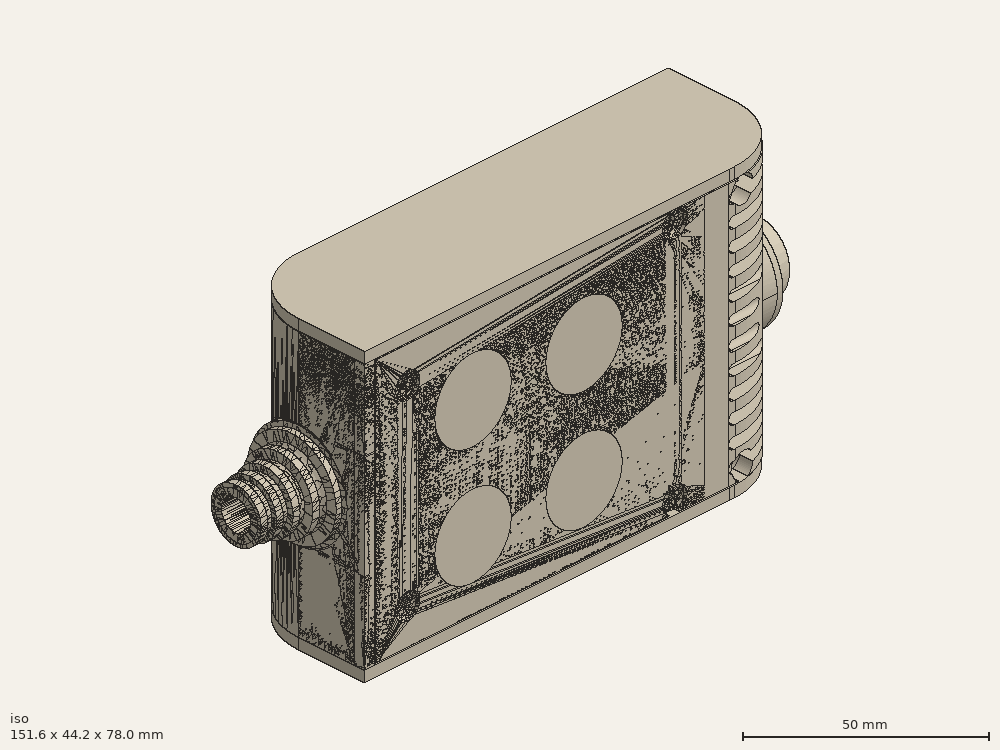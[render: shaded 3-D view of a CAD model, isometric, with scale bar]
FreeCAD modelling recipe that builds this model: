
FCSTD DOCUMENT  (FreeCAD 0.19R0.19.2)
Label: enclosure_189FCStd
License: All rights reserved
LicenseURL: http://en.wikipedia.org/wiki/All_rights_reserved
objects: Part::Revolution×152, Part::MultiFuse×146, Part::Feature×146, Sketcher::SketchObject×84, Part::Cut×70, Part::Cylinder×70, Part::Extrusion×67, Part::Fillet×58, Part::Box×36, App::MeasureDistance×4, PartDesign::Body×2, Image::ImagePlane×1
note: 831 computed .brp shape members not serialized (recipe doc carries the construction recipe); baked Part::Feature solids carry a one-line shape summary decoded from their .brp

FEATURE [Sketcher::SketchObject] Sketch  label="topSketch"
  FullyConstrained = true
  sketch-geometry (20):
    g0: LineSegment StartX=5.21097e-06 StartY=3 StartZ=0 EndX=5.21097e-06 EndY=19 EndZ=0
    g1: ArcOfCircle CenterX=19 CenterY=19 CenterZ=0 NormalX=0 NormalY=0 NormalZ=1 AngleXU=0 Radius=19 StartAngle=1.5708 EndAngle=3.14159
    g2: ArcOfCircle CenterX=19 CenterY=19 CenterZ=0 NormalX=0 NormalY=0 NormalZ=1 AngleXU=0 Radius=16 StartAngle=1.5708 EndAngle=3.14159
    g3: LineSegment StartX=114 StartY=35 StartZ=0 EndX=19 EndY=35 EndZ=0
    g4: LineSegment StartX=5.21097e-06 StartY=3 StartZ=0 EndX=5.21097e-06 EndY=0 EndZ=0
    g5: LineSegment StartX=3 StartY=0 StartZ=0 EndX=5.21097e-06 EndY=0 EndZ=0
    g6: LineSegment StartX=3 StartY=19 StartZ=0 EndX=3 EndY=0 EndZ=0
    g7: LineSegment StartX=19 StartY=38 StartZ=0 EndX=124 EndY=38 EndZ=0
    g8: Circle CenterX=119 CenterY=35 CenterZ=0 NormalX=0 NormalY=0 NormalZ=1 AngleXU=0 Radius=1
    g9: Circle CenterX=121 CenterY=35 CenterZ=0 NormalX=0 NormalY=0 NormalZ=1 AngleXU=0 Radius=1
    g10: Circle CenterX=121 CenterY=33 CenterZ=0 NormalX=0 NormalY=0 NormalZ=1 AngleXU=0 Radius=1
    g11: BSplineCurve PolesCount=3 KnotsCount=2 Degree=2 IsPeriodic=0
    g12: GeomPoint X=119 Y=35 Z=0
    g13: GeomPoint X=121 Y=33 Z=0
    g14: LineSegment StartX=119 StartY=35 StartZ=0 EndX=114 EndY=35 EndZ=0
    g15: ArcOfCircle CenterX=105 CenterY=19 CenterZ=0 NormalX=0 NormalY=0 NormalZ=1 AngleXU=0 Radius=19 StartAngle=5.7297 EndAngle=6.28319
    g16: ArcOfCircle CenterX=105 CenterY=19 CenterZ=0 NormalX=0 NormalY=0 NormalZ=1 AngleXU=0 Radius=16 StartAngle=5.60905 EndAngle=6.28319
    g17: LineSegment StartX=121 StartY=33 StartZ=0 EndX=121 EndY=19 EndZ=0
    g18: LineSegment StartX=124 StartY=38 StartZ=0 EndX=124 EndY=19 EndZ=0
    g19: LineSegment StartX=117.5 StartY=9.01251 StartZ=0 EndX=121.163 EndY=9.0125 EndZ=0
  constraints (46):
    c: Vertical(g0)
    c: Block(g0)
    c: Coincident(g1,g0)
    c: Block(g1)
    c: Coincident(g2,g1)
    c: Block(g2)
    c: Coincident(g3,g2)
    c: Horizontal(g3)
    c: Tangent(g3,g2)
    c: Coincident(g4,g0)
    c: Distance(g4) = 3
    c: Vertical(g4)
    c: Coincident(g5,g4)
    c: Horizontal(g5)
    c: Coincident(g6,g2)
    c: Coincident(g6,g5)
    c: Vertical(g6)
    c: Horizontal(g7)
    c: Distance(g7) = 105
    c: Coincident(g7,g1)
    c: Block(g3)
    c: Weight(g8) = 1
    c: Equal(g8,g9)
    c: Equal(g8,g10)
    c: InternalAlignment(g8,g11)
    c: InternalAlignment(g9,g11)
    c: InternalAlignment(g10,g11)
    c: InternalAlignment(g12,g11)
    c: InternalAlignment(g13,g11)
    c: Block(g11)
    c: Coincident(g14,g11)
    c: Coincident(g14,g3)
    c: Horizontal(g14)
    c: Block(g15)
    c: Coincident(g16,g15)
    c: Block(g16)
    c: Coincident(g17,g11)
    c: Coincident(g17,g16)
    c: Vertical(g17)
    c: Distance(g17) = 14
    c: Coincident(g18,g7)
    c: Coincident(g18,g15)
    c: Vertical(g18)
    c: Distance(g18) = 19
    c: Coincident(g19,g16)
    c: Coincident(g19,g15)
FEATURE [Sketcher::SketchObject] Sketch001  label="bottomSketch"
  FullyConstrained = true
  sketch-geometry (32):
    g0: LineSegment StartX=3.3 StartY=-6.03275e-07 StartZ=0 EndX=98 EndY=-6.03275e-07 EndZ=0
    g1: ArcOfCircle CenterX=98 CenterY=19 CenterZ=0 NormalX=0 NormalY=0 NormalZ=1 AngleXU=0 Radius=19 StartAngle=4.71239 EndAngle=5.71103
    g2: LineSegment StartX=6.3 StartY=8 StartZ=0 EndX=3.3 EndY=8 EndZ=0
    g3: LineSegment StartX=3.3 StartY=8 StartZ=0 EndX=3.3 EndY=-6.03275e-07 EndZ=0
    g4: ArcOfCircle CenterX=8.3 CenterY=5 CenterZ=0 NormalX=0 NormalY=0 NormalZ=1 AngleXU=0 Radius=2 StartAngle=3.14159 EndAngle=4.71239
    g5: LineSegment StartX=6.3 StartY=8 StartZ=0 EndX=6.3 EndY=5 EndZ=0
    g6: ArcOfCircle CenterX=98 CenterY=19 CenterZ=0 NormalX=0 NormalY=0 NormalZ=1 AngleXU=0 Radius=12.7 StartAngle=4.71239 EndAngle=6.28319
    g7: LineSegment StartX=94.7 StartY=3 StartZ=0 EndX=8.3 EndY=3 EndZ=0
    g8-g12: Circle x5 (B-spline internal-alignment scaffolding for g13; pole/knot coordinates omitted)
    g13: BSplineCurve PolesCount=5 KnotsCount=3 Degree=3 IsPeriodic=0
    g14: GeomPoint X=98 Y=6.3 Z=0
    g15: GeomPoint X=96.3938 Y=4.71946 Z=0
    g16: GeomPoint X=94.7 Y=3 Z=0
    g17-g23: Circle x7 (B-spline internal-alignment scaffolding for g24; pole/knot coordinates omitted)
    g24: BSplineCurve PolesCount=7 KnotsCount=5 Degree=3 IsPeriodic=0
    g25-g29: GeomPoint x5 (B-spline internal-alignment scaffolding for g24; pole/knot coordinates omitted)
    g30: ArcOfCircle CenterX=98 CenterY=19 CenterZ=0 NormalX=0 NormalY=0 NormalZ=1 AngleXU=0 Radius=15.7 StartAngle=5.81226 EndAngle=6.28319
    g31: LineSegment StartX=110.7 StartY=19 StartZ=0 EndX=113.7 EndY=19 EndZ=0
  constraints (41):
    c: Horizontal(g0)
    c: Coincident(g1,g0)
    c: Block(g1)
    c: Horizontal(g2)
    c: Distance(g2) = 3
    c: Coincident(g3,g2)
    c: Vertical(g3)
    c: Coincident(g3,g0)
    c: Block(g4)
    c: Block(g2)
    c: Coincident(g5,g2)
    c: Coincident(g5,g4)
    c: Vertical(g5)
    c: Coincident(g6,g1)
    c: Block(g6)
    c: Coincident(g7,g4)
    c: Horizontal(g7)
    c: Block(g0)
    c: Block(g7)
    c: Block(g3)
    c: Coincident(g13,g6)
    c: Weight(g8) = 1
    c: Equal(g8, g9-g12) x4
    c: Coincident(g13,g7)
    c: InternalAlignment(g8-g12 -> g13) x5
    c: InternalAlignment(g14,g13)
    c: InternalAlignment(g15,g13)
    c: InternalAlignment(g16,g13)
    c: Block(g13)
    c: Weight(g17) = 1
    c: Equal(g17, g18-g23) x6
    c: Coincident(g24,g1)
    c: InternalAlignment(g17-g23 -> g24) x7
    c: InternalAlignment(g25-g29 -> g24) x5
    c: Block(g24)
    c: Coincident(g30,g24)
    c: Coincident(g31,g6)
    c: Coincident(g31,g30)
    c: Horizontal(g31)
    c: Block(g31)
    c: Block(g30)
FEATURE [Part::Extrusion] Extrude  label="top"
  Base = -> Sketch
  Dir = (0,0,1)
  DirMode = 2
  FaceMakerClass = Part::FaceMakerBullseye
  LengthFwd = 72
  LengthRev = 0
  Solid = true
  Symmetric = false
FEATURE [Part::Extrusion] Extrude001  label="bottom"
  Base = -> Sketch001
  Dir = (0,0,1)
  DirMode = 2
  FaceMakerClass = Part::FaceMakerBullseye
  LengthFwd = 71.4
  LengthRev = 0
  Placement = pos=(0,0,0.3) rot=(0,0,1;0rad)
  Solid = true
  Symmetric = false
FEATURE [Sketcher::SketchObject] Sketch002  label="topSketch001"
  FullyConstrained = true
  sketch-geometry (8):
    g0: ArcOfCircle CenterX=19 CenterY=19.0975 CenterZ=0 NormalX=0 NormalY=0 NormalZ=1 AngleXU=0 Radius=18.9025 StartAngle=1.5708 EndAngle=3.14674
    g1: LineSegment StartX=0.0977805 StartY=19.0003 StartZ=0 EndX=0.0977805 EndY=0.000251602 EndZ=0
    g2: LineSegment StartX=19 StartY=38 StartZ=0 EndX=124 EndY=38 EndZ=0
    g3: LineSegment StartX=0.0977805 StartY=0.000251602 StartZ=0 EndX=105.098 EndY=0.000251602 EndZ=0
    g4: LineSegment StartX=124 StartY=38 StartZ=0 EndX=125.616 EndY=38 EndZ=0
    g5: LineSegment StartX=105.098 StartY=0.000251602 StartZ=0 EndX=106.713 EndY=0.000251602 EndZ=0
    g6: ArcOfCircle CenterX=106.616 CenterY=19 CenterZ=0 NormalX=0 NormalY=0 NormalZ=1 AngleXU=0 Radius=19 StartAngle=4.71754 EndAngle=6.28319
    g7: LineSegment StartX=125.616 StartY=38 StartZ=0 EndX=125.616 EndY=19 EndZ=0
  constraints (21):
    c: Block(g0)
    c: Coincident(g1,g0)
    c: Vertical(g1)
    c: Horizontal(g2)
    c: Distance(g2) = 105
    c: Coincident(g2,g0)
    c: Distance(g1) = 19
    c: Coincident(g3,g1)
    c: Horizontal(g3)
    c: Distance(g3) = 105
    c: Coincident(g4,g2)
    c: Horizontal(g4)
    c: Distance(g4) = 1.61553
    c: Horizontal(g5)
    c: Equal(g4,g5) = 1.61553
    c: Coincident(g5,g3)
    c: Block(g6)
    c: Coincident(g6,g5)
    c: Coincident(g7,g4)
    c: Coincident(g7,g6)
    c: Vertical(g7)
FEATURE [Part::Extrusion] Extrude002  label="sideA"
  Base = -> Sketch002
  Dir = (0,0,1)
  DirMode = 2
  FaceMakerClass = Part::FaceMakerBullseye
  LengthFwd = 3
  LengthRev = 0
  Placement = pos=(0,0,-3) rot=(0,0,1;0rad)
  Solid = true
  Symmetric = false
FEATURE [Sketcher::SketchObject] Sketch003  label="topSketch002"
  FullyConstrained = true
  sketch-geometry (6):
    g0: LineSegment StartX=19 StartY=38 StartZ=0 EndX=117 EndY=38 EndZ=0
    g1: ArcOfCircle CenterX=19 CenterY=19 CenterZ=0 NormalX=0 NormalY=0 NormalZ=1 AngleXU=0 Radius=19 StartAngle=1.5708 EndAngle=3.14159
    g2: LineSegment StartX=117 StartY=38 StartZ=0 EndX=117 EndY=19 EndZ=0
    g3: LineSegment StartX=98 StartY=1.0161e-12 StartZ=0 EndX=5.22862e-06 EndY=1.0161e-12 EndZ=0
    g4: LineSegment StartX=5.22862e-06 StartY=19 StartZ=0 EndX=5.22862e-06 EndY=1.0161e-12 EndZ=0
    g5: ArcOfCircle CenterX=98 CenterY=19 CenterZ=0 NormalX=0 NormalY=0 NormalZ=1 AngleXU=0 Radius=19 StartAngle=4.71239 EndAngle=6.28319
  constraints (16):
    c: Horizontal(g0)
    c: Distance(g0) = 98
    c: Coincident(g1,g0)
    c: Block(g1)
    c: Coincident(g2,g0)
    c: Vertical(g2)
    c: Distance(g2) = 19
    c: Horizontal(g3)
    c: Coincident(g4,g1)
    c: Vertical(g4)
    c: Coincident(g3,g4)
    c: Block(g3)
    c: Coincident(g5,g2)
    c: Coincident(g5,g3)
    c: Block(g0)
    c: Block(g5)
FEATURE [Sketcher::SketchObject] Sketch004
  FullyConstrained = true
  MapMode = 3
  Placement = pos=(0,0,0) rot=(1,0,0;1.5708rad)
  Support = -> [Extrude]
  sketch-geometry (8):
    g0: Circle CenterX=80.351 CenterY=-67.6202 CenterZ=0 NormalX=0 NormalY=0 NormalZ=1 AngleXU=0 Radius=2
    g1: Circle CenterX=80.351 CenterY=-67.6202 CenterZ=0 NormalX=0 NormalY=0 NormalZ=1 AngleXU=0 Radius=3
    g2: Circle CenterX=80.351 CenterY=-4.92017 CenterZ=0 NormalX=0 NormalY=0 NormalZ=1 AngleXU=0 Radius=2
    g3: Circle CenterX=80.351 CenterY=-4.92017 CenterZ=0 NormalX=0 NormalY=0 NormalZ=1 AngleXU=0 Radius=3
    g4: Circle CenterX=23.851 CenterY=-4.92017 CenterZ=0 NormalX=0 NormalY=0 NormalZ=1 AngleXU=0 Radius=2
    g5: Circle CenterX=23.851 CenterY=-4.92017 CenterZ=0 NormalX=0 NormalY=0 NormalZ=1 AngleXU=0 Radius=3
    g6: Circle CenterX=23.851 CenterY=-67.6202 CenterZ=0 NormalX=0 NormalY=0 NormalZ=1 AngleXU=0 Radius=2
    g7: Circle CenterX=23.851 CenterY=-67.6202 CenterZ=0 NormalX=0 NormalY=0 NormalZ=1 AngleXU=0 Radius=3
  constraints (8):
    c: Block(g3)
    c: Block(g2)
    c: Block(g1)
    c: Block(g0)
    c: Block(g6)
    c: Block(g7)
    c: Block(g4)
    c: Block(g5)
FEATURE [Part::Extrusion] Extrude004
  Base = -> Sketch004
  Dir = (0,-1,2e-16)
  DirMode = 2
  FaceMakerClass = Part::FaceMakerBullseye
  LengthFwd = 6
  LengthRev = 0
  Placement = pos=(0,9,0) rot=(0,0,1;0rad)
  Solid = true
  Symmetric = false
FEATURE [Sketcher::SketchObject] Sketch005
  FullyConstrained = true
  MapMode = 3
  Placement = pos=(0,0,0) rot=(1,0,0;1.5708rad)
  Support = -> [Extrude]
  sketch-geometry (8):
    g0: Circle CenterX=80.351 CenterY=-67.6202 CenterZ=0 NormalX=0 NormalY=0 NormalZ=1 AngleXU=0 Radius=3
    g1: Circle CenterX=80.351 CenterY=-4.92017 CenterZ=0 NormalX=0 NormalY=0 NormalZ=1 AngleXU=0 Radius=3
    g2: Circle CenterX=23.851 CenterY=-4.92017 CenterZ=0 NormalX=0 NormalY=0 NormalZ=1 AngleXU=0 Radius=3
    g3: Circle CenterX=23.851 CenterY=-67.6202 CenterZ=0 NormalX=0 NormalY=0 NormalZ=1 AngleXU=0 Radius=3
    g4: Circle CenterX=23.851 CenterY=-67.6202 CenterZ=0 NormalX=0 NormalY=0 NormalZ=1 AngleXU=0 Radius=5
    g5: Circle CenterX=80.351 CenterY=-67.6202 CenterZ=0 NormalX=0 NormalY=0 NormalZ=1 AngleXU=0 Radius=5
    g6: Circle CenterX=23.851 CenterY=-4.92017 CenterZ=0 NormalX=0 NormalY=0 NormalZ=1 AngleXU=0 Radius=5
    g7: Circle CenterX=80.351 CenterY=-4.92017 CenterZ=0 NormalX=0 NormalY=0 NormalZ=1 AngleXU=0 Radius=5
  constraints (8):
    c: Block(g1)
    c: Block(g0)
    c: Block(g3)
    c: Block(g2)
    c: Block(g5)
    c: Block(g4)
    c: Block(g6)
    c: Block(g7)
FEATURE [Part::Extrusion] Extrude005
  Base = -> Sketch005
  Dir = (0,-1,2e-16)
  DirMode = 2
  FaceMakerClass = Part::FaceMakerBullseye
  LengthFwd = 2
  LengthRev = 0
  Solid = true
  Symmetric = false
FEATURE [Sketcher::SketchObject] Sketch006
  FullyConstrained = true
  MapMode = 3
  Placement = pos=(0,0,0) rot=(1,0,0;1.5708rad)
  sketch-geometry (8):
    g0: Circle CenterX=80.351 CenterY=-67.6202 CenterZ=0 NormalX=0 NormalY=0 NormalZ=1 AngleXU=0 Radius=3
    g1: Circle CenterX=80.351 CenterY=-4.92017 CenterZ=0 NormalX=0 NormalY=0 NormalZ=1 AngleXU=0 Radius=3
    g2: Circle CenterX=23.851 CenterY=-4.92017 CenterZ=0 NormalX=0 NormalY=0 NormalZ=1 AngleXU=0 Radius=3
    g3: Circle CenterX=23.851 CenterY=-67.6202 CenterZ=0 NormalX=0 NormalY=0 NormalZ=1 AngleXU=0 Radius=3
    g4: Circle CenterX=23.851 CenterY=-67.6202 CenterZ=0 NormalX=0 NormalY=0 NormalZ=1 AngleXU=0 Radius=5
    g5: Circle CenterX=80.351 CenterY=-67.6202 CenterZ=0 NormalX=0 NormalY=0 NormalZ=1 AngleXU=0 Radius=5
    g6: Circle CenterX=23.851 CenterY=-4.92017 CenterZ=0 NormalX=0 NormalY=0 NormalZ=1 AngleXU=0 Radius=5
    g7: Circle CenterX=80.351 CenterY=-4.92017 CenterZ=0 NormalX=0 NormalY=0 NormalZ=1 AngleXU=0 Radius=5
  constraints (8):
    c: Block(g1)
    c: Block(g0)
    c: Block(g3)
    c: Block(g2)
    c: Block(g5)
    c: Block(g4)
    c: Block(g6)
    c: Block(g7)
FEATURE [Part::Extrusion] Extrude007
  Base = -> Sketch006
  Dir = (0,-1,2e-16)
  DirMode = 2
  FaceMakerClass = Part::FaceMakerBullseye
  LengthFwd = 2
  LengthRev = 0
  Solid = true
  Symmetric = false
FEATURE [Part::Fillet] Fillet
  Base = -> Extrude007
  Edges = 4 edges r=1.99: [Edge6,Edge12,Edge18,Edge24]
FEATURE [Part::Cut] Cut
  Base = -> Extrude005
  Placement = pos=(0,5,0) rot=(0,0,1;0rad)
  Tool = -> Fillet
FEATURE [Part::MultiFuse] Fusion  label="pCBScrews"
  Placement = pos=(-2.5,0,72.3) rot=(0,0,1;0rad)
  Shapes = -> [Extrude004,Cut]
FEATURE [App::MeasureDistance] Distance  label="Distance: 0.69 mm"
  Distance = 0.685967
  P1 = (24.0138,2.9647,0.3)
  P2 = (23.8901,3,-0.373787)
FEATURE [App::MeasureDistance] Distance001  label="Distance: 0.53 mm"
  Distance = 0.533607
  P1 = (80.2939,3,72.2334)
  P2 = (80.281,2.99661,71.7)
FEATURE [Part::Fillet] Fillet001
  Base = -> Extrude001
  Edges = 1 edges r=2.4: [Edge17]
FEATURE [Part::Fillet] Fillet002  label="bottom001"
  Base = -> Fillet001
  Edges = 1 edges r=2.4: [Edge36]
FEATURE [Part::Fillet] Fillet003  label="top001"
  Base = -> Extrude
  Edges = 1 edges r=2: [Edge1]
FEATURE [Sketcher::SketchObject] Sketch007
  FullyConstrained = true
  sketch-geometry (16):
    g0: LineSegment StartX=4 StartY=0 StartZ=0 EndX=4 EndY=2.4 EndZ=0
    g1: LineSegment StartX=4 StartY=2.4 StartZ=0 EndX=7 EndY=2.4 EndZ=0
    g2: LineSegment StartX=4 StartY=0 StartZ=0 EndX=5.7 EndY=0 EndZ=0
    g3: LineSegment StartX=5.7 StartY=0 StartZ=0 EndX=5.7 EndY=-5.6 EndZ=0
    g4-g8: Circle x5 (B-spline internal-alignment scaffolding for g9; pole/knot coordinates omitted)
    g9: BSplineCurve PolesCount=5 KnotsCount=3 Degree=3 IsPeriodic=0
    g10: GeomPoint X=7 Y=2.4 Z=0
    g11: GeomPoint X=10.4582 Y=-1.55472 Z=0
    g12: GeomPoint X=14 Y=-5.6 Z=0
    g13: LineSegment StartX=14 StartY=-5.6 StartZ=0 EndX=14 EndY=-14.1 EndZ=0
    g14: LineSegment StartX=14 StartY=-14.1 StartZ=0 EndX=6.5 EndY=-14.1 EndZ=0
    g15: LineSegment StartX=5.7 StartY=-5.6 StartZ=0 EndX=6.5 EndY=-14.1 EndZ=0
  constraints (28):
    c: Distance(g0) = 2.4
    c: Vertical(g0)
    c: Block(g0)
    c: Coincident(g1,g0)
    c: Horizontal(g1)
    c: Distance(g1) = 3
    c: Coincident(g2,g0)
    c: Horizontal(g2)
    c: Distance(g2) = 1.7
    c: Coincident(g3,g2)
    c: Vertical(g3)
    c: Distance(g3) = 5.6
    c: Coincident(g9,g1)
    c: Weight(g4) = 1
    c: Equal(g4, g5-g8) x4
    c: InternalAlignment(g4-g8 -> g9) x5
    c: InternalAlignment(g10,g9)
    c: InternalAlignment(g11,g9)
    c: InternalAlignment(g12,g9)
    c: Block(g9)
    c: Coincident(g13,g9)
    c: Vertical(g13)
    c: Distance(g13) = 8.5
    c: Coincident(g14,g13)
    c: Horizontal(g14)
    c: Distance(g14) = 7.5
    c: Coincident(g15,g3)
    c: Coincident(g15,g14)
FEATURE [Part::Feature] Face
  shape: bbox 10 x 16.5 x 2e-07 mm, 1 faces, 0 solids (baked)
FEATURE [Part::Revolution] Revolve  label="plugHousing"
  Angle = 360
  Axis = (0,1,0)
  Base = (0,0,0)
  FaceMakerClass = Part::FaceMakerBullseye
  Placement = pos=(0,0,36.15) rot=(0,0,1;0rad)
  Solid = false
  Source = -> Face
  Symmetric = false
FEATURE [Part::Feature] Face001
  shape: bbox 10 x 16.5 x 2e-07 mm, 1 faces, 0 solids (baked)
FEATURE [Part::Revolution] Revolve001  label="plugHousing001"
  Angle = 360
  Axis = (0,1,0)
  Base = (0,0,0)
  FaceMakerClass = Part::FaceMakerBullseye
  Placement = pos=(0,0,36.15) rot=(0,0,1;0rad)
  Solid = false
  Source = -> Face001
  Symmetric = false
FEATURE [Part::MultiFuse] Fusion001  label="plugHousing002"
  Placement = pos=(0,0,0) rot=(0,0,1;1.5708rad)
  Shapes = -> [Revolve001,Revolve]
FEATURE [Part::Feature] Face002
  shape: bbox 10 x 16.5 x 2e-07 mm, 1 faces, 0 solids (baked)
FEATURE [Part::Revolution] Revolve003  label="plugHousing005"
  Angle = 360
  Axis = (0,1,0)
  Base = (0,0,0)
  FaceMakerClass = Part::FaceMakerBullseye
  Placement = pos=(0,0,36.15) rot=(0,0,1;0rad)
  Solid = false
  Source = -> Face002
  Symmetric = false
FEATURE [Part::Feature] Face003
  shape: bbox 10 x 16.5 x 2e-07 mm, 1 faces, 0 solids (baked)
FEATURE [Part::Revolution] Revolve002  label="plugHousing003"
  Angle = 360
  Axis = (0,1,0)
  Base = (0,0,0)
  FaceMakerClass = Part::FaceMakerBullseye
  Placement = pos=(0,0,36.15) rot=(0,0,1;0rad)
  Solid = false
  Source = -> Face003
  Symmetric = false
FEATURE [Part::MultiFuse] Fusion002  label="plugHousing004"
  Placement = pos=(0,0,0) rot=(0,0,1;1.5708rad)
  Shapes = -> [Revolve002,Revolve003]
FEATURE [Part::MultiFuse] Fusion003  label="plugHousing006"
  Placement = pos=(0,19,0) rot=(0,0,1;3.14159rad)
  Shapes = -> [Fusion002,Fusion001]
FEATURE [Part::Feature] Face004
  shape: bbox 10 x 16.5 x 2e-07 mm, 1 faces, 0 solids (baked)
FEATURE [Part::Revolution] Revolve006  label="plugHousing010"
  Angle = 360
  Axis = (0,1,0)
  Base = (0,0,0)
  FaceMakerClass = Part::FaceMakerBullseye
  Placement = pos=(0,0,36.15) rot=(0,0,1;0rad)
  Solid = false
  Source = -> Face004
  Symmetric = false
FEATURE [Part::Feature] Face005
  shape: bbox 10 x 16.5 x 2e-07 mm, 1 faces, 0 solids (baked)
FEATURE [Part::Revolution] Revolve007  label="plugHousing011"
  Angle = 360
  Axis = (0,1,0)
  Base = (0,0,0)
  FaceMakerClass = Part::FaceMakerBullseye
  Placement = pos=(0,0,36.15) rot=(0,0,1;0rad)
  Solid = false
  Source = -> Face005
  Symmetric = false
FEATURE [Part::Feature] Face006
  shape: bbox 10 x 16.5 x 2e-07 mm, 1 faces, 0 solids (baked)
FEATURE [Part::Revolution] Revolve004  label="plugHousing007"
  Angle = 360
  Axis = (0,1,0)
  Base = (0,0,0)
  FaceMakerClass = Part::FaceMakerBullseye
  Placement = pos=(0,0,36.15) rot=(0,0,1;0rad)
  Solid = false
  Source = -> Face006
  Symmetric = false
FEATURE [Part::MultiFuse] Fusion004  label="plugHousing009"
  Placement = pos=(0,0,0) rot=(0,0,1;1.5708rad)
  Shapes = -> [Revolve004,Revolve007]
FEATURE [Part::Feature] Face007
  shape: bbox 10 x 16.5 x 2e-07 mm, 1 faces, 0 solids (baked)
FEATURE [Part::Revolution] Revolve005  label="plugHousing008"
  Angle = 360
  Axis = (0,1,0)
  Base = (0,0,0)
  FaceMakerClass = Part::FaceMakerBullseye
  Placement = pos=(0,0,36.15) rot=(0,0,1;0rad)
  Solid = false
  Source = -> Face007
  Symmetric = false
FEATURE [Part::MultiFuse] Fusion005  label="plugHousing012"
  Placement = pos=(0,0,0) rot=(0,0,1;1.5708rad)
  Shapes = -> [Revolve006,Revolve005]
FEATURE [Part::MultiFuse] Fusion006  label="plugHousing013"
  Placement = pos=(0,19,0) rot=(0,0,1;3.14159rad)
  Shapes = -> [Fusion005,Fusion004]
FEATURE [Part::MultiFuse] Fusion007  label="plugHousing014"
  Placement = pos=(122.621,0,-0.15) rot=(0,0,1;0rad)
  Shapes = -> [Fusion003,Fusion006]
FEATURE [Part::Cylinder] Cylinder002
  Angle = 360
  AttacherType = Attacher::AttachEngine3D
  Height = 20
  Placement = pos=(0,0,36.15) rot=(0,0,1;0rad)
  Radius = 4
FEATURE [Part::Cylinder] Cylinder003
  Angle = 360
  AttacherType = Attacher::AttachEngine3D
  Height = 10
  Placement = pos=(0,0,36.15) rot=(0,0,1;0rad)
  Radius = 4
FEATURE [Part::MultiFuse] Fusion009  label="removeToCreateHoleForPlugHousing"
  Placement = pos=(70,19,36.15) rot=(0,1,0;1.5708rad)
  Shapes = -> [Cylinder002,Cylinder003]
FEATURE [Part::Cylinder] Cylinder004
  Angle = 360
  AttacherType = Attacher::AttachEngine3D
  Height = 20
  Placement = pos=(0,0,36.15) rot=(0,0,1;0rad)
  Radius = 4
FEATURE [Part::Cylinder] Cylinder005
  Angle = 360
  AttacherType = Attacher::AttachEngine3D
  Height = 10
  Placement = pos=(0,0,36.15) rot=(0,0,1;0rad)
  Radius = 4
FEATURE [Part::MultiFuse] Fusion010  label="removeToCreateHoleForPlugHousing001"
  Placement = pos=(70,19,36.15) rot=(0,1,0;1.5708rad)
  Shapes = -> [Cylinder004,Cylinder005]
FEATURE [Part::Cut] Cut001
  Base = -> Fillet003
  Tool = -> Fusion010
FEATURE [Part::Cut] Cut002  label="Bottom"
  Base = -> Fillet002
  Tool = -> Fusion009
FEATURE [Part::Feature] Face008
  shape: bbox 10 x 16.5 x 2e-07 mm, 1 faces, 0 solids (baked)
FEATURE [Part::Revolution] Revolve011  label="plugHousing021"
  Angle = 360
  Axis = (0,1,0)
  Base = (0,0,0)
  FaceMakerClass = Part::FaceMakerBullseye
  Placement = pos=(0,0,36.15) rot=(0,0,1;0rad)
  Solid = false
  Source = -> Face008
  Symmetric = false
FEATURE [Part::Feature] Face009
  shape: bbox 10 x 16.5 x 2e-07 mm, 1 faces, 0 solids (baked)
FEATURE [Part::Revolution] Revolve012  label="plugHousing022"
  Angle = 360
  Axis = (0,1,0)
  Base = (0,0,0)
  FaceMakerClass = Part::FaceMakerBullseye
  Placement = pos=(0,0,36.15) rot=(0,0,1;0rad)
  Solid = false
  Source = -> Face009
  Symmetric = false
FEATURE [Part::Feature] Face010 .. Face013  x4 (patterned run collapsed; names and placements below)
  shape: bbox 10 x 16.5 x 2e-07 mm, 1 faces, 0 solids (baked)
FEATURE [Part::Revolution] Revolve015  label="plugHousing027"
  Angle = 360
  Axis = (0,1,0)
  Base = (0,0,0)
  FaceMakerClass = Part::FaceMakerBullseye
  Placement = pos=(0,0,36.15) rot=(0,0,1;0rad)
  Solid = false
  Source = -> Face013
  Symmetric = false
FEATURE [Part::Feature] Face014
  shape: bbox 10 x 16.5 x 2e-07 mm, 1 faces, 0 solids (baked)
FEATURE [Part::Feature] Face015
  shape: bbox 10 x 16.5 x 2e-07 mm, 1 faces, 0 solids (baked)
FEATURE [Part::Feature] Face016
  shape: bbox 10 x 16.5 x 2e-07 mm, 1 faces, 0 solids (baked)
FEATURE [Part::Revolution] Revolve019  label="plugHousing033"
  Angle = 360
  Axis = (0,1,0)
  Base = (0,0,0)
  FaceMakerClass = Part::FaceMakerBullseye
  Placement = pos=(0,0,36.15) rot=(0,0,1;0rad)
  Solid = false
  Source = -> Face016
  Symmetric = false
FEATURE [Part::Feature] Face017
  shape: bbox 10 x 16.5 x 2e-07 mm, 1 faces, 0 solids (baked)
FEATURE [Part::Revolution] Revolve020  label="plugHousing034"
  Angle = 360
  Axis = (0,1,0)
  Base = (0,0,0)
  FaceMakerClass = Part::FaceMakerBullseye
  Placement = pos=(0,0,36.15) rot=(0,0,1;0rad)
  Solid = false
  Source = -> Face017
  Symmetric = false
FEATURE [Part::Feature] Face018
  shape: bbox 10 x 16.5 x 2e-07 mm, 1 faces, 0 solids (baked)
FEATURE [Part::Revolution] Revolve016  label="plugHousing030"
  Angle = 360
  Axis = (0,1,0)
  Base = (0,0,0)
  FaceMakerClass = Part::FaceMakerBullseye
  Placement = pos=(0,0,36.15) rot=(0,0,1;0rad)
  Solid = false
  Source = -> Face018
  Symmetric = false
FEATURE [Part::MultiFuse] Fusion020  label="plugHousing038"
  Placement = pos=(0,0,0) rot=(0,0,1;1.5708rad)
  Shapes = -> [Revolve016,Revolve020]
FEATURE [Part::Feature] Face019
  shape: bbox 10 x 16.5 x 2e-07 mm, 1 faces, 0 solids (baked)
FEATURE [Part::Feature] Face020
  shape: bbox 10 x 16.5 x 2e-07 mm, 1 faces, 0 solids (baked)
FEATURE [Part::Revolution] Revolve017  label="plugHousing031"
  Angle = 360
  Axis = (0,1,0)
  Base = (0,0,0)
  FaceMakerClass = Part::FaceMakerBullseye
  Placement = pos=(0,0,36.15) rot=(0,0,1;0rad)
  Solid = false
  Source = -> Face020
  Symmetric = false
FEATURE [Part::MultiFuse] Fusion021  label="plugHousing039"
  Placement = pos=(0,0,0) rot=(0,0,1;1.5708rad)
  Shapes = -> [Revolve019,Revolve017]
FEATURE [Part::MultiFuse] Fusion023  label="plugHousing041"
  Placement = pos=(0,19,0) rot=(0,0,1;3.14159rad)
  Shapes = -> [Fusion021,Fusion020]
FEATURE [Part::Revolution] Revolve022  label="plugHousing043"
  Angle = 360
  Axis = (0,1,0)
  Base = (0,0,0)
  FaceMakerClass = Part::FaceMakerBullseye
  Placement = pos=(0,0,36.15) rot=(0,0,1;0rad)
  Solid = false
  Source = -> Face019
  Symmetric = false
FEATURE [Part::Feature] Face021
  shape: bbox 10 x 16.5 x 2e-07 mm, 1 faces, 0 solids (baked)
FEATURE [Part::Revolution] Revolve023  label="plugHousing044"
  Angle = 360
  Axis = (0,1,0)
  Base = (0,0,0)
  FaceMakerClass = Part::FaceMakerBullseye
  Placement = pos=(0,0,36.15) rot=(0,0,1;0rad)
  Solid = false
  Source = -> Face021
  Symmetric = false
FEATURE [Part::Feature] Face022
  shape: bbox 10 x 16.5 x 2e-07 mm, 1 faces, 0 solids (baked)
FEATURE [Part::Revolution] Revolve018  label="plugHousing032"
  Angle = 360
  Axis = (0,1,0)
  Base = (0,0,0)
  FaceMakerClass = Part::FaceMakerBullseye
  Placement = pos=(0,0,36.15) rot=(0,0,1;0rad)
  Solid = false
  Source = -> Face022
  Symmetric = false
FEATURE [Part::MultiFuse] Fusion022  label="plugHousing040"
  Placement = pos=(0,0,0) rot=(0,0,1;1.5708rad)
  Shapes = -> [Revolve018,Revolve023]
FEATURE [Part::Feature] Face023
  shape: bbox 10 x 16.5 x 2e-07 mm, 1 faces, 0 solids (baked)
FEATURE [Part::Revolution] Revolve021  label="plugHousing035"
  Angle = 360
  Axis = (0,1,0)
  Base = (0,0,0)
  FaceMakerClass = Part::FaceMakerBullseye
  Placement = pos=(0,0,36.15) rot=(0,0,1;0rad)
  Solid = false
  Source = -> Face023
  Symmetric = false
FEATURE [Part::MultiFuse] Fusion018  label="plugHousing036"
  Placement = pos=(0,0,0) rot=(0,0,1;1.5708rad)
  Shapes = -> [Revolve022,Revolve021]
FEATURE [Part::MultiFuse] Fusion019  label="plugHousing037"
  Placement = pos=(0,19,0) rot=(0,0,1;3.14159rad)
  Shapes = -> [Fusion018,Fusion022]
FEATURE [Part::MultiFuse] Fusion024  label="plugHousing042"
  Placement = pos=(122.621,0,-0.15) rot=(0,0,1;0rad)
  Shapes = -> [Fusion023,Fusion019]
FEATURE [Part::Cylinder] Cylinder006
  Angle = 360
  AttacherType = Attacher::AttachEngine3D
  Height = 20
  Placement = pos=(0,0,36.15) rot=(0,0,1;0rad)
  Radius = 14.3
FEATURE [Part::Cylinder] Cylinder007
  Angle = 360
  AttacherType = Attacher::AttachEngine3D
  Height = 10
  Placement = pos=(0,0,36.15) rot=(0,0,1;0rad)
  Radius = 4
FEATURE [Part::MultiFuse] Fusion026  label="removeToCreteHoleForPlugHousing"
  Placement = pos=(70,19,36) rot=(0,1,0;1.5708rad)
  Shapes = -> [Cylinder006,Cylinder007]
FEATURE [Part::Box] Box001  label="Cube001"
  AttacherType = Attacher::AttachEngine3D
  Height = 28
  Length = 3
  Placement = pos=(110.7,19,22) rot=(0,0,1;0rad)
  Width = 15.7
FEATURE [Part::Cut] Cut003  label="top002"
  Base = -> Cut001
  Tool = -> Fusion007
FEATURE [Part::Revolution] Revolve008  label="plugHousing015"
  Angle = 360
  Axis = (0,1,0)
  Base = (0,0,0)
  FaceMakerClass = Part::FaceMakerBullseye
  Placement = pos=(0,0,36.15) rot=(0,0,1;0rad)
  Solid = false
  Source = -> Face010
  Symmetric = false
FEATURE [Part::MultiFuse] Fusion013  label="plugHousing020"
  Placement = pos=(0,0,0) rot=(0,0,1;1.5708rad)
  Shapes = -> [Revolve008,Revolve012]
FEATURE [Part::Cut] Cut004  label="top003"
  Base = -> Cut003
  Placement = pos=(1,0,0) rot=(0,0,1;0rad)
  Tool = -> Fusion026
FEATURE [Part::Cylinder] Cylinder008
  Angle = 360
  AttacherType = Attacher::AttachEngine3D
  Height = 20
  Placement = pos=(0,0,36.15) rot=(0,0,1;0rad)
  Radius = 10.3
FEATURE [Part::Cylinder] Cylinder009
  Angle = 360
  AttacherType = Attacher::AttachEngine3D
  Height = 10
  Placement = pos=(0,0,36.15) rot=(0,0,1;0rad)
  Radius = 4
FEATURE [Part::MultiFuse] Fusion027  label="removeToCreteHoleForPlugHousing001"
  Placement = pos=(70,19,36) rot=(0,1,0;1.5708rad)
  Shapes = -> [Cylinder008,Cylinder009]
FEATURE [Part::Cut] Cut005  label="plugHousingTab"
  Base = -> Box001
  Tool = -> Fusion027
FEATURE [Part::MultiFuse] Fusion028  label="plugHousing045"
  Shapes = -> [Fusion024,Cut005]
FEATURE [Part::Box] Box002  label="Cube002"
  AttacherType = Attacher::AttachEngine3D
  Height = 28.8
  Length = 3
  Placement = pos=(107.3,28,21.6) rot=(0,0,1;0rad)
  Width = 7
FEATURE [Part::Box] Box003  label="Cube003"
  AttacherType = Attacher::AttachEngine3D
  Height = 3
  Length = 6.4
  Placement = pos=(107.3,28,18.6) rot=(0,0,1;0rad)
  Width = 7
FEATURE [Part::Box] Box004  label="Cube004"
  AttacherType = Attacher::AttachEngine3D
  Height = 3
  Length = 6.4
  Placement = pos=(107.3,28,50.4) rot=(0,0,1;0rad)
  Width = 7
FEATURE [Part::MultiFuse] Fusion029  label="plugHousingBracketHolder"
  Shapes = -> [Box004,Box002,Box003]
FEATURE [Part::Cylinder] Cylinder010
  Angle = 360
  AttacherType = Attacher::AttachEngine3D
  Height = 20
  Placement = pos=(0,0,36.15) rot=(0,0,1;0rad)
  Radius = 14.3
FEATURE [Part::Cylinder] Cylinder011
  Angle = 360
  AttacherType = Attacher::AttachEngine3D
  Height = 10
  Placement = pos=(0,0,36.15) rot=(0,0,1;0rad)
  Radius = 4
FEATURE [Part::MultiFuse] Fusion030  label="removeToCreteHoleForPlugHousing002"
  Placement = pos=(70,19,36) rot=(0,1,0;1.5708rad)
  Shapes = -> [Cylinder010,Cylinder011]
FEATURE [Part::Cut] Cut006  label="plugHousingBracketHolder001"
  Base = -> Fusion029
  Tool = -> Fusion030
FEATURE [Part::Cylinder] Cylinder012
  Angle = 360
  AttacherType = Attacher::AttachEngine3D
  Height = 20
  Placement = pos=(0,0,36.15) rot=(0,0,1;0rad)
  Radius = 7
FEATURE [Part::Cylinder] Cylinder013
  Angle = 360
  AttacherType = Attacher::AttachEngine3D
  Height = 10
  Placement = pos=(0,0,36.15) rot=(0,0,1;0rad)
  Radius = 4
FEATURE [Part::MultiFuse] Fusion032  label="removeToCreteHoleForPlugHousing003"
  Placement = pos=(70,19,36) rot=(0,1,0;1.5708rad)
  Shapes = -> [Cylinder012,Cylinder013]
FEATURE [Part::Cut] Cut007  label="bottom002"
  Base = -> Cut002
  Tool = -> Fusion032
FEATURE [Sketcher::SketchObject] Sketch008
  FullyConstrained = true
  sketch-geometry (54):
    g0: LineSegment StartX=-4.2 StartY=0 StartZ=0 EndX=-6.2 EndY=0 EndZ=0
    g1: LineSegment StartX=-14 StartY=-18 StartZ=0 EndX=-14 EndY=-26.5 EndZ=0
    g2: LineSegment StartX=-4.2 StartY=0 StartZ=0 EndX=-4.2 EndY=-13.4877 EndZ=0
    g3: Circle CenterX=-4.2 CenterY=-13.4877 CenterZ=0 NormalX=0 NormalY=0 NormalZ=1 AngleXU=0 Radius=1
    g4: Circle CenterX=-4.2 CenterY=-26.5 CenterZ=0 NormalX=0 NormalY=0 NormalZ=1 AngleXU=0 Radius=1
    g5: Circle CenterX=-8.2 CenterY=-26.5 CenterZ=0 NormalX=0 NormalY=0 NormalZ=1 AngleXU=0 Radius=1
    g6: BSplineCurve PolesCount=3 KnotsCount=2 Degree=2 IsPeriodic=0
    g7: GeomPoint X=-4.2 Y=-13.4877 Z=0
    g8: GeomPoint X=-8.2 Y=-26.5 Z=0
    g9: LineSegment StartX=-14 StartY=-26.5 StartZ=0 EndX=-8.2 EndY=-26.5 EndZ=0
    g10: LineSegment StartX=-10.15 StartY=-12 StartZ=0 EndX=-10.15 EndY=-14 EndZ=0
    g11: LineSegment StartX=-12.8401 StartY=-16 StartZ=0 EndX=-10.1571 EndY=-16 EndZ=0
    g12: LineSegment StartX=-10.15 StartY=-14 StartZ=0 EndX=-8.70761 EndY=-14 EndZ=0
    g13: LineSegment StartX=-12.8401 StartY=-16 StartZ=0 EndX=-12.8401 EndY=-17.6958 EndZ=0
    g14: LineSegment StartX=-10.15 StartY=-12 StartZ=0 EndX=-7.79258 EndY=-12 EndZ=0
    g15: Circle CenterX=-6.2215 CenterY=-2 CenterZ=0 NormalX=0 NormalY=0 NormalZ=1 AngleXU=0 Radius=1
    g16: Circle CenterX=-6.22762 CenterY=-2.58724 CenterZ=0 NormalX=0 NormalY=0 NormalZ=1 AngleXU=0 Radius=1
    g17: Circle CenterX=-6.32538 CenterY=-4 CenterZ=0 NormalX=0 NormalY=0 NormalZ=1 AngleXU=0 Radius=1
    g18: BSplineCurve PolesCount=3 KnotsCount=2 Degree=2 IsPeriodic=0
    g19: GeomPoint X=-6.2215 Y=-2 Z=0
    g20: GeomPoint X=-6.32538 Y=-4 Z=0
    g21: Circle CenterX=-6.48644 CenterY=-5.99526 CenterZ=0 NormalX=0 NormalY=0 NormalZ=1 AngleXU=0 Radius=1
    g22: Circle CenterX=-6.58486 CenterY=-6.99526 CenterZ=0 NormalX=0 NormalY=0 NormalZ=1 AngleXU=0 Radius=1
    g23: Circle CenterX=-6.77343 CenterY=-8 CenterZ=0 NormalX=0 NormalY=0 NormalZ=1 AngleXU=0 Radius=1
    g24: BSplineCurve PolesCount=3 KnotsCount=2 Degree=2 IsPeriodic=0
    g25: GeomPoint X=-6.48644 Y=-5.99526 Z=0
    g26: GeomPoint X=-6.77343 Y=-8 Z=0
    g27: Circle CenterX=-7.19003 CenterY=-10 CenterZ=0 NormalX=0 NormalY=0 NormalZ=1 AngleXU=0 Radius=1
    g28: Circle CenterX=-7.44407 CenterY=-11.0915 CenterZ=0 NormalX=0 NormalY=0 NormalZ=1 AngleXU=0 Radius=1
    g29: Circle CenterX=-7.79258 CenterY=-12 CenterZ=0 NormalX=0 NormalY=0 NormalZ=1 AngleXU=0 Radius=1
    g30: BSplineCurve PolesCount=3 KnotsCount=2 Degree=2 IsPeriodic=0
    g31: GeomPoint X=-7.19003 Y=-10 Z=0
    g32: GeomPoint X=-7.79258 Y=-12 Z=0
    g33: Circle CenterX=-8.70761 CenterY=-14 CenterZ=0 NormalX=0 NormalY=0 NormalZ=1 AngleXU=0 Radius=1
    g34: Circle CenterX=-9.33087 CenterY=-15.1837 CenterZ=0 NormalX=0 NormalY=0 NormalZ=1 AngleXU=0 Radius=1
    g35: Circle CenterX=-10.1571 CenterY=-16 CenterZ=0 NormalX=0 NormalY=0 NormalZ=1 AngleXU=0 Radius=1
    g36: BSplineCurve PolesCount=3 KnotsCount=2 Degree=2 IsPeriodic=0
    g37: GeomPoint X=-8.70761 Y=-14 Z=0
    g38: GeomPoint X=-10.1571 Y=-16 Z=0
    g39: Circle CenterX=-12.8401 CenterY=-17.6958 CenterZ=0 NormalX=0 NormalY=0 NormalZ=1 AngleXU=0 Radius=1
    g40: Circle CenterX=-13.3521 CenterY=-17.9027 CenterZ=0 NormalX=0 NormalY=0 NormalZ=1 AngleXU=0 Radius=1
    g41: Circle CenterX=-14 CenterY=-18 CenterZ=0 NormalX=0 NormalY=0 NormalZ=1 AngleXU=0 Radius=1
    g42: BSplineCurve PolesCount=3 KnotsCount=2 Degree=2 IsPeriodic=0
    g43: GeomPoint X=-12.8401 Y=-17.6958 Z=0
    g44: GeomPoint X=-14 Y=-18 Z=0
    g45: LineSegment StartX=-6.2 StartY=0 StartZ=0 EndX=-7.2 EndY=0 EndZ=0
    g46: LineSegment StartX=-7.2 StartY=0 StartZ=0 EndX=-7.2 EndY=-2 EndZ=0
    g47: LineSegment StartX=-7.2 StartY=-2 StartZ=0 EndX=-6.2215 EndY=-2 EndZ=0
    g48: LineSegment StartX=-6.32538 StartY=-4 StartZ=0 EndX=-7.65538 EndY=-4 EndZ=0
    g49: LineSegment StartX=-7.65538 StartY=-4 StartZ=0 EndX=-7.65538 EndY=-5.99526 EndZ=0
    g50: LineSegment StartX=-7.65538 StartY=-5.99526 StartZ=0 EndX=-6.48644 EndY=-5.99526 EndZ=0
    g51: LineSegment StartX=-6.77343 StartY=-8 StartZ=0 EndX=-8.43343 EndY=-8 EndZ=0
    g52: LineSegment StartX=-8.43343 StartY=-8 StartZ=0 EndX=-8.43343 EndY=-10 EndZ=0
    g53: LineSegment StartX=-8.43343 StartY=-10 StartZ=0 EndX=-7.19003 EndY=-10 EndZ=0
  constraints (112):
    c: Horizontal(g0)
    c: Distance(g0) = 2
    c: Block(g0)
    c: Vertical(g1)
    c: Coincident(g2,g0)
    c: Vertical(g2)
    c: Block(g2)
    c: Coincident(g6,g2)
    c: Weight(g3) = 1
    c: Equal(g3,g4)
    c: Equal(g3,g5)
    c: InternalAlignment(g3,g6)
    c: InternalAlignment(g4,g6)
    c: InternalAlignment(g5,g6)
    c: InternalAlignment(g7,g6)
    c: InternalAlignment(g8,g6)
    c: Block(g6)
    c: Coincident(g9,g1)
    c: Coincident(g9,g6)
    c: Horizontal(g9)
    c: Vertical(g10)
    c: Block(g10)
    c: Horizontal(g11)
    c: Block(g11)
    c: Coincident(g12,g10)
    c: Horizontal(g12)
    c: Block(g12)
    c: Coincident(g13,g11)
    c: Vertical(g13)
    c: Block(g13)
    c: Coincident(g14,g10)
    c: Horizontal(g14)
    c: Block(g14)
    c: Block(g9)
    c: Block(g1)
    c: Weight(g15) = 1
    c: Equal(g15,g16)
    c: Equal(g15,g17)
    c: InternalAlignment(g15,g18)
    c: InternalAlignment(g16,g18)
    c: InternalAlignment(g17,g18)
    c: InternalAlignment(g19,g18)
    c: InternalAlignment(g20,g18)
    c: Weight(g21) = 1
    c: Equal(g21,g22)
    c: Equal(g21,g23)
    c: InternalAlignment(g21,g24)
    c: InternalAlignment(g22,g24)
    c: InternalAlignment(g23,g24)
    c: InternalAlignment(g25,g24)
    c: InternalAlignment(g26,g24)
    c: Weight(g27) = 1
    c: Equal(g27,g28)
    c: Equal(g27,g29)
    c: Coincident(g30,g14)
    c: InternalAlignment(g27,g30)
    c: InternalAlignment(g28,g30)
    c: InternalAlignment(g29,g30)
    c: InternalAlignment(g31,g30)
    c: InternalAlignment(g32,g30)
    c: Coincident(g36,g12)
    c: Weight(g33) = 1
    c: Equal(g33,g34)
    c: Equal(g33,g35)
    c: Coincident(g36,g11)
    c: InternalAlignment(g33,g36)
    c: InternalAlignment(g34,g36)
    c: InternalAlignment(g35,g36)
    c: InternalAlignment(g37,g36)
    c: InternalAlignment(g38,g36)
    c: Coincident(g42,g13)
    c: Weight(g39) = 1
    c: Equal(g39,g40)
    c: Equal(g39,g41)
    c: Coincident(g42,g1)
    c: InternalAlignment(g39,g42)
    c: InternalAlignment(g40,g42)
    c: InternalAlignment(g41,g42)
    c: InternalAlignment(g43,g42)
    c: InternalAlignment(g44,g42)
    c: Block(g18)
    c: Block(g24)
    c: Block(g30)
    c: Block(g36)
    c: Block(g42)
    c: Horizontal(g45)
    c: Coincident(g45,g0)
    c: Vertical(g46)
    c: Coincident(g46,g45)
    c: Coincident(g47,g46)
    c: Coincident(g47,g18)
    c: Horizontal(g47)
    c: Block(g46)
    c: Coincident(g48,g18)
    c: Horizontal(g48)
    c: Distance(g48) = 1.33
    c: Vertical(g49)
    c: Coincident(g49,g48)
    c: Coincident(g50,g49)
    c: Coincident(g50,g24)
    c: Horizontal(g50)
    c: Tangent(g50,g22)
    c: Horizontal(g51)
    c: Coincident(g51,g24)
    c: Block(g51)
    c: Vertical(g52)
    c: Block(g52)
    c: Coincident(g52,g51)
    c: Coincident(g53,g52)
    c: Coincident(g53,g30)
    c: Horizontal(g53)
    c: Distance(g1) = 8.5
FEATURE [Part::Feature] Face024
  shape: bbox 9.8 x 26.5 x 2e-07 mm, 1 faces, 0 solids (baked)
FEATURE [Part::Revolution] Revolve024
  Angle = 360
  Axis = (0,1,0)
  Base = (0,0,0)
  FaceMakerClass = Part::FaceMakerBullseye
  Placement = pos=(0,0,0) rot=(0,0,1;1.5708rad)
  Solid = false
  Source = -> Face024
  Symmetric = false
FEATURE [Part::Feature] Face025
  shape: bbox 9.8 x 26.5 x 2e-07 mm, 1 faces, 0 solids (baked)
FEATURE [Part::Revolution] Revolve025
  Angle = 360
  Axis = (0,1,0)
  Base = (0,0,0)
  FaceMakerClass = Part::FaceMakerBullseye
  Placement = pos=(0,0,0) rot=(0,0,1;1.5708rad)
  Solid = false
  Source = -> Face025
  Symmetric = false
FEATURE [Part::MultiFuse] Fusion033
  Placement = pos=(-18,19,36) rot=(0,0,1;0rad)
  Shapes = -> [Revolve025,Revolve024]
FEATURE [Part::Cylinder] Cylinder014
  Angle = 360
  AttacherType = Attacher::AttachEngine3D
  Height = 20
  Placement = pos=(0,0,36.15) rot=(0,0,1;0rad)
  Radius = 14.3
FEATURE [Part::Cylinder] Cylinder015
  Angle = 360
  AttacherType = Attacher::AttachEngine3D
  Height = 10
  Placement = pos=(0,0,36.15) rot=(0,0,1;0rad)
  Radius = 4
FEATURE [Part::MultiFuse] Fusion034  label="removeToCreteHoleForPlugHousing004"
  Placement = pos=(-42,19,36) rot=(0,1,0;1.5708rad)
  Shapes = -> [Cylinder014,Cylinder015]
FEATURE [Part::Cut] Cut008  label="top004"
  Base = -> Cut004
  Placement = pos=(-1,0,0) rot=(0,0,1;0rad)
  Tool = -> Fusion034
FEATURE [Part::Box] Box005  label="Cube005"
  AttacherType = Attacher::AttachEngine3D
  Height = 28
  Length = 3
  Placement = pos=(110.7,19,22) rot=(0,0,1;0rad)
  Width = 15.7
FEATURE [Part::Cylinder] Cylinder016
  Angle = 360
  AttacherType = Attacher::AttachEngine3D
  Height = 10
  Placement = pos=(0,0,36.15) rot=(0,0,1;0rad)
  Radius = 4
FEATURE [Part::Cylinder] Cylinder017
  Angle = 360
  AttacherType = Attacher::AttachEngine3D
  Height = 20
  Placement = pos=(0,0,36.15) rot=(0,0,1;0rad)
  Radius = 10.3
FEATURE [Part::MultiFuse] Fusion035  label="removeToCreteHoleForPlugHousing005"
  Placement = pos=(70,19,36) rot=(0,1,0;1.5708rad)
  Shapes = -> [Cylinder017,Cylinder016]
FEATURE [Part::Cut] Cut009  label="plugHousingTab001"
  Base = -> Box005
  Placement = pos=(-107.4,-14,0) rot=(0,0,1;0rad)
  Tool = -> Fusion035
FEATURE [Part::Box] Box006  label="Cube006"
  AttacherType = Attacher::AttachEngine3D
  Height = 28
  Length = 3
  Placement = pos=(110.7,19,22) rot=(0,0,1;0rad)
  Width = 15.7
FEATURE [Part::Cylinder] Cylinder018
  Angle = 360
  AttacherType = Attacher::AttachEngine3D
  Height = 10
  Placement = pos=(0,0,36.15) rot=(0,0,1;0rad)
  Radius = 4
FEATURE [Part::Cylinder] Cylinder019
  Angle = 360
  AttacherType = Attacher::AttachEngine3D
  Height = 20
  Placement = pos=(0,0,36.15) rot=(0,0,1;0rad)
  Radius = 10.3
FEATURE [Part::MultiFuse] Fusion036  label="removeToCreteHoleForPlugHousing006"
  Placement = pos=(70,19,36) rot=(0,1,0;1.5708rad)
  Shapes = -> [Cylinder019,Cylinder018]
FEATURE [Part::Cut] Cut010  label="plugHousingTab002"
  Base = -> Box006
  Placement = pos=(-107.4,-14,0) rot=(0,0,1;0rad)
  Tool = -> Fusion036
FEATURE [Part::MultiFuse] Fusion037
  Placement = pos=(9.6,23,0) rot=(0,0,1;3.14159rad)
  Shapes = -> [Cut009,Cut010]
FEATURE [Part::Box] Box  label="Cube"
  AttacherType = Attacher::AttachEngine3D
  Height = 10
  Length = 3
  Placement = pos=(3.3,4,12) rot=(0,0,1;0rad)
  Width = 10
FEATURE [Part::Fillet] Fillet004
  Base = -> Fusion028
  Edges = 1 edges r=2: [Edge25]
FEATURE [Part::Fillet] Fillet005  label="plugHousing046"
  Base = -> Fillet004
  Edges = 1 edges r=2: [Edge8]
FEATURE [Part::Fillet] Fillet006
  Base = -> Box
  Edges = 1 edges r=2: [Edge11]
FEATURE [Part::Box] Box007  label="Cube007"
  AttacherType = Attacher::AttachEngine3D
  Height = 10
  Length = 3
  Placement = pos=(3.3,4,50) rot=(0,0,1;0rad)
  Width = 10
FEATURE [Part::Fillet] Fillet007
  Base = -> Box007
  Edges = 1 edges r=2: [Edge12]
FEATURE [Part::Box] Box008  label="Cube008"
  AttacherType = Attacher::AttachEngine3D
  Height = 28
  Length = 4
  Placement = pos=(5,0,22) rot=(0,0,1;0rad)
  Width = 10
FEATURE [Part::Fillet] Fillet008
  Base = -> Box008
  Edges = 1 edges r=1: [Edge7]
FEATURE [Part::Fillet] Fillet009
  Base = -> Fillet008
  Edges = 1 edges r=2: [Edge5]
FEATURE [Part::Fillet] Fillet010
  Base = -> Fillet009
  Edges = 1 edges r=2: [Edge2]
FEATURE [Sketcher::SketchObject] Sketch009  label="topSketch003"
  FullyConstrained = true
  sketch-geometry (4):
    g0: LineSegment StartX=16.8446 StartY=31.512 StartZ=0 EndX=16.3251 EndY=34.4666 EndZ=0
    g1: ArcOfCircle CenterX=19 CenterY=19.2524 CenterZ=0 NormalX=0 NormalY=0 NormalZ=1 AngleXU=0 Radius=15.4476 StartAngle=1.74483 EndAngle=2.72717
    g2: ArcOfCircle CenterX=19 CenterY=19.2524 CenterZ=0 NormalX=0 NormalY=0 NormalZ=1 AngleXU=0 Radius=12.4476 StartAngle=1.74483 EndAngle=2.73189
    g3: LineSegment StartX=4.86004 StartY=25.4725 StartZ=0 EndX=7.58253 EndY=24.2107 EndZ=0
  constraints (7):
    c: Block(g0)
    c: Coincident(g1,g0)
    c: Coincident(g2,g0)
    c: Coincident(g3,g1)
    c: Coincident(g3,g2)
    c: Block(g1)
    c: Block(g2)
FEATURE [Part::Extrusion] Extrude008
  Base = -> Sketch009
  Dir = (0,0,1)
  DirMode = 2
  FaceMakerClass = Part::FaceMakerBullseye
  LengthFwd = 10
  LengthRev = 0
  Placement = pos=(0,0,31) rot=(0,0,1;0rad)
  Solid = true
  Symmetric = false
FEATURE [Part::Cylinder] Cylinder020
  Angle = 360
  AttacherType = Attacher::AttachEngine3D
  Height = 20
  Placement = pos=(0,0,36.15) rot=(0,0,1;0rad)
  Radius = 8.2
FEATURE [Part::Cylinder] Cylinder021
  Angle = 360
  AttacherType = Attacher::AttachEngine3D
  Height = 10
  Placement = pos=(0,0,36.15) rot=(0,0,1;0rad)
  Radius = 4
FEATURE [Part::MultiFuse] Fusion038  label="removeToCreteHoleForPlugHousing007"
  Placement = pos=(-42,19,36) rot=(0,1,0;1.5708rad)
  Shapes = -> [Cylinder020,Cylinder021]
FEATURE [Part::Cut] Cut011
  Base = -> Extrude008
  Tool = -> Fusion038
FEATURE [Part::Fillet] Fillet011
  Base = -> Cut011
  Edges = 1 edges r=2: [Edge1]
FEATURE [Part::Fillet] Fillet012
  Base = -> Fillet011
  Edges = 1 edges r=2.5: [Edge1]
FEATURE [Part::Fillet] Fillet013
  Base = -> Fillet012
  Edges = 1 edges r=2.5: [Edge2]
FEATURE [Part::Box] Box010  label="Cube010"
  AttacherType = Attacher::AttachEngine3D
  Height = 16
  Length = 8
  Placement = pos=(12.7,31.52,28) rot=(0,0,1;0rad)
  Width = 4
FEATURE [Sketcher::SketchObject] Sketch010  label="topSketch004"
  FullyConstrained = true
  sketch-geometry (4):
    g0: LineSegment StartX=16.8446 StartY=31.512 StartZ=0 EndX=16.3251 EndY=34.4666 EndZ=0
    g1: ArcOfCircle CenterX=19 CenterY=19.2524 CenterZ=0 NormalX=0 NormalY=0 NormalZ=1 AngleXU=0 Radius=15.4476 StartAngle=1.74483 EndAngle=2.72717
    g2: ArcOfCircle CenterX=19 CenterY=19.2524 CenterZ=0 NormalX=0 NormalY=0 NormalZ=1 AngleXU=0 Radius=12.4476 StartAngle=1.74483 EndAngle=2.73189
    g3: LineSegment StartX=4.86004 StartY=25.4725 StartZ=0 EndX=7.58253 EndY=24.2107 EndZ=0
  constraints (7):
    c: Block(g0)
    c: Coincident(g1,g0)
    c: Coincident(g2,g0)
    c: Coincident(g3,g1)
    c: Coincident(g3,g2)
    c: Block(g1)
    c: Block(g2)
FEATURE [Part::Cylinder] Cylinder022
  Angle = 360
  AttacherType = Attacher::AttachEngine3D
  Height = 10
  Placement = pos=(0,0,36.15) rot=(0,0,1;0rad)
  Radius = 4
FEATURE [Sketcher::SketchObject] Sketch011  label="topSketch005"
  FullyConstrained = true
  sketch-geometry (4):
    g0: LineSegment StartX=16.8446 StartY=31.512 StartZ=0 EndX=16.3251 EndY=34.4666 EndZ=0
    g1: ArcOfCircle CenterX=19 CenterY=19.2524 CenterZ=0 NormalX=0 NormalY=0 NormalZ=1 AngleXU=0 Radius=15.4476 StartAngle=1.74483 EndAngle=2.72717
    g2: ArcOfCircle CenterX=19 CenterY=19.2524 CenterZ=0 NormalX=0 NormalY=0 NormalZ=1 AngleXU=0 Radius=12.4476 StartAngle=1.74483 EndAngle=2.73189
    g3: LineSegment StartX=4.86004 StartY=25.4725 StartZ=0 EndX=7.58253 EndY=24.2107 EndZ=0
  constraints (7):
    c: Block(g0)
    c: Coincident(g1,g0)
    c: Coincident(g2,g0)
    c: Coincident(g3,g1)
    c: Coincident(g3,g2)
    c: Block(g1)
    c: Block(g2)
FEATURE [Part::Extrusion] Extrude010
  Base = -> Sketch011
  Dir = (0,0,1)
  DirMode = 2
  FaceMakerClass = Part::FaceMakerBullseye
  LengthFwd = 10.6
  LengthRev = 0
  Placement = pos=(0,0,31) rot=(0,0,1;0rad)
  Solid = true
  Symmetric = false
FEATURE [Part::Cylinder] Cylinder023
  Angle = 360
  AttacherType = Attacher::AttachEngine3D
  Height = 20
  Placement = pos=(0,0,36.15) rot=(0,0,1;0rad)
  Radius = 8.2
FEATURE [Part::MultiFuse] Fusion039  label="removeToCreteHoleForPlugHousing008"
  Placement = pos=(-42,19,36) rot=(0,1,0;1.5708rad)
  Shapes = -> [Cylinder023,Cylinder022]
FEATURE [Part::Cut] Cut012
  Base = -> Extrude010
  Placement = pos=(0,0,-0.3) rot=(0,0,1;0rad)
  Tool = -> Fusion039
FEATURE [Part::Cut] Cut013
  Base = -> Box010
  Tool = -> Cut012
FEATURE [Part::Fillet] Fillet014
  Base = -> Cut013
  Edges = 1 edges r=0.7: [Edge13]
FEATURE [Part::Fillet] Fillet015
  Base = -> Fillet014
  Edges = 1 edges r=0.7: [Edge13]
FEATURE [Part::Fillet] Fillet016
  Base = -> Fillet015
  Edges = 1 edges r=0.7: [Edge16]
FEATURE [Part::Fillet] Fillet017
  Base = -> Fillet016
  Edges = 1 edges r=0.7: [Edge11]
FEATURE [Part::Fillet] Fillet018
  Base = -> Fillet017
  Edges = 1 edges r=0.7: [Edge10]
FEATURE [Part::Fillet] Fillet019
  Base = -> Fillet018
  Edges = 1 edges r=1.2: [Edge5]
FEATURE [Part::Fillet] Fillet020
  Base = -> Fillet019
  Edges = 1 edges r=1.2: [Edge12]
FEATURE [Part::Fillet] Fillet021
  Base = -> Fillet020
  Edges = 1 edges r=2: [Edge1]
  Placement = pos=(0.3,0,0) rot=(0,0,1;0rad)
FEATURE [Part::MultiFuse] Fusion040  label="top005"
  Shapes = -> [Cut008,Fillet021]
FEATURE [Part::MultiFuse] Fusion041  label="wireHolder"
  Shapes = -> [Fusion033,Fillet013]
FEATURE [Part::MultiFuse] Fusion042
  Shapes = -> [Fillet007,Fusion041]
FEATURE [Part::MultiFuse] Fusion043  label="wireHolder001"
  Shapes = -> [Fusion042,Fillet010]
FEATURE [Part::MultiFuse] Fusion044  label="wireHolder002"
  Shapes = -> [Fillet006,Fusion037,Fusion043]
FEATURE [Part::Feature] Face026
  shape: bbox 11 x 6 x 2e-07 mm, 1 faces, 0 solids (baked)
FEATURE [Part::Revolution] Revolve026
  Angle = 360
  Axis = (0,1,0)
  Base = (0,0,0)
  FaceMakerClass = Part::FaceMakerBullseye
  Placement = pos=(30.3,-1,19.7) rot=(0,0,1;0rad)
  Solid = false
  Source = -> Face026
  Symmetric = false
FEATURE [Sketcher::SketchObject] Sketch013  label="topSketch006"
  FullyConstrained = true
  sketch-geometry (13):
    g0: LineSegment StartX=117 StartY=19 StartZ=0 EndX=117 EndY=38 EndZ=0
    g1: ArcOfCircle CenterX=98 CenterY=19 CenterZ=0 NormalX=0 NormalY=0 NormalZ=1 AngleXU=0 Radius=19 StartAngle=5.7297 EndAngle=6.28319
    g2: LineSegment StartX=0 StartY=3 StartZ=0 EndX=0 EndY=19 EndZ=0
    g3: LineSegment StartX=19 StartY=38 StartZ=0 EndX=117 EndY=38 EndZ=0
    g4: ArcOfCircle CenterX=19 CenterY=19 CenterZ=0 NormalX=0 NormalY=0 NormalZ=1 AngleXU=0 Radius=19 StartAngle=1.5708 EndAngle=3.14159
    g5: ArcOfCircle CenterX=19 CenterY=19 CenterZ=0 NormalX=0 NormalY=0 NormalZ=1 AngleXU=0 Radius=16 StartAngle=1.5708 EndAngle=3.14159
    g6: ArcOfCircle CenterX=98 CenterY=19 CenterZ=0 NormalX=0 NormalY=0 NormalZ=1 AngleXU=0 Radius=16 StartAngle=5.60905 EndAngle=6.28319
    g7: LineSegment StartX=114 StartY=19 StartZ=0 EndX=114 EndY=35 EndZ=0
    g8: LineSegment StartX=110.5 StartY=9.01251 StartZ=0 EndX=114.163 EndY=9.01251 EndZ=0
    g9: LineSegment StartX=114 StartY=35 StartZ=0 EndX=19 EndY=35 EndZ=0
    g10: LineSegment StartX=0 StartY=3 StartZ=0 EndX=0 EndY=0 EndZ=0
    g11: LineSegment StartX=3 StartY=0 StartZ=0 EndX=0 EndY=0 EndZ=0
    g12: LineSegment StartX=3 StartY=19 StartZ=0 EndX=3 EndY=0 EndZ=0
  constraints (33):
    c: Vertical(g0)
    c: Distance(g0) = 19
    c: Block(g0)
    c: Coincident(g1,g0)
    c: Block(g1)
    c: Vertical(g2)
    c: Block(g2)
    c: Coincident(g3,g0)
    c: Horizontal(g3)
    c: Distance(g3) = 98
    c: Coincident(g4,g3)
    c: Coincident(g4,g2)
    c: Block(g4)
    c: Coincident(g5,g4)
    c: Coincident(g6,g1)
    c: Block(g6)
    c: Block(g5)
    c: Coincident(g7,g6)
    c: Vertical(g7)
    c: Coincident(g8,g6)
    c: Coincident(g8,g1)
    c: Coincident(g9,g7)
    c: Coincident(g9,g5)
    c: Horizontal(g9)
    c: Tangent(g9,g5)
    c: Coincident(g10,g2)
    c: Distance(g10) = 3
    c: Vertical(g10)
    c: Coincident(g11,g10)
    c: Horizontal(g11)
    c: Coincident(g12,g5)
    c: Coincident(g12,g11)
    c: Vertical(g12)
FEATURE [Part::Extrusion] Extrude011  label="top006"
  Base = -> Sketch013
  Dir = (0,0,1)
  DirMode = 2
  FaceMakerClass = Part::FaceMakerBullseye
  LengthFwd = 72
  LengthRev = 0
  Solid = true
  Symmetric = false
FEATURE [Sketcher::SketchObject] Sketch014
  FullyConstrained = true
  MapMode = 3
  Placement = pos=(0,0,0) rot=(1,0,0;1.5708rad)
  Support = -> [Extrude011]
  sketch-geometry (8):
    g0: Circle CenterX=80.351 CenterY=-67.6202 CenterZ=0 NormalX=0 NormalY=0 NormalZ=1 AngleXU=0 Radius=2
    g1: Circle CenterX=80.351 CenterY=-67.6202 CenterZ=0 NormalX=0 NormalY=0 NormalZ=1 AngleXU=0 Radius=3
    g2: Circle CenterX=80.351 CenterY=-4.92017 CenterZ=0 NormalX=0 NormalY=0 NormalZ=1 AngleXU=0 Radius=2
    g3: Circle CenterX=80.351 CenterY=-4.92017 CenterZ=0 NormalX=0 NormalY=0 NormalZ=1 AngleXU=0 Radius=3
    g4: Circle CenterX=23.851 CenterY=-4.92017 CenterZ=0 NormalX=0 NormalY=0 NormalZ=1 AngleXU=0 Radius=2
    g5: Circle CenterX=23.851 CenterY=-4.92017 CenterZ=0 NormalX=0 NormalY=0 NormalZ=1 AngleXU=0 Radius=3
    g6: Circle CenterX=23.851 CenterY=-67.6202 CenterZ=0 NormalX=0 NormalY=0 NormalZ=1 AngleXU=0 Radius=2
    g7: Circle CenterX=23.851 CenterY=-67.6202 CenterZ=0 NormalX=0 NormalY=0 NormalZ=1 AngleXU=0 Radius=3
  constraints (8):
    c: Block(g3)
    c: Block(g2)
    c: Block(g1)
    c: Block(g0)
    c: Block(g6)
    c: Block(g7)
    c: Block(g4)
    c: Block(g5)
FEATURE [Part::Feature] Face027
  shape: bbox 11 x 6 x 2e-07 mm, 1 faces, 0 solids (baked)
FEATURE [Part::Revolution] Revolve027
  Angle = 360
  Axis = (0,1,0)
  Base = (0,0,0)
  FaceMakerClass = Part::FaceMakerBullseye
  Placement = pos=(30.3,-1,51.7) rot=(0,0,1;0rad)
  Solid = false
  Source = -> Face027
  Symmetric = false
FEATURE [Part::Feature] Face028
  shape: bbox 11 x 6 x 2e-07 mm, 1 faces, 0 solids (baked)
FEATURE [Part::Revolution] Revolve028
  Angle = 360
  Axis = (0,1,0)
  Base = (0,0,0)
  FaceMakerClass = Part::FaceMakerBullseye
  Placement = pos=(62.3,-1,19.7) rot=(0,0,1;0rad)
  Solid = false
  Source = -> Face028
  Symmetric = false
FEATURE [Part::Feature] Face029
  shape: bbox 11 x 6 x 2e-07 mm, 1 faces, 0 solids (baked)
FEATURE [Part::Revolution] Revolve029
  Angle = 360
  Axis = (0,1,0)
  Base = (0,0,0)
  FaceMakerClass = Part::FaceMakerBullseye
  Placement = pos=(62.3,-1,51.7) rot=(0,0,1;0rad)
  Solid = false
  Source = -> Face029
  Symmetric = false
FEATURE [Part::Feature] Wire
  shape: bbox 11 x 5.2 x 2e-07 mm, 0 faces, 0 solids (baked)
FEATURE [Part::Revolution] Revolve030
  Angle = 360
  Axis = (0,1,0)
  Base = (0,0,0)
  FaceMakerClass = Part::FaceMakerBullseye
  Placement = pos=(30.3,38,19.7) rot=(0,0,1;0rad)
  Solid = true
  Source = -> Wire
  Symmetric = false
FEATURE [Part::Feature] Wire001
  shape: bbox 11 x 5.2 x 2e-07 mm, 0 faces, 0 solids (baked)
FEATURE [Part::Revolution] Revolve031
  Angle = 360
  Axis = (0,1,0)
  Base = (0,0,0)
  FaceMakerClass = Part::FaceMakerBullseye
  Placement = pos=(30.3,38,51.7) rot=(0,0,1;0rad)
  Solid = true
  Source = -> Wire001
  Symmetric = false
FEATURE [Part::Feature] Wire002
  shape: bbox 11 x 5.2 x 2e-07 mm, 0 faces, 0 solids (baked)
FEATURE [Part::Revolution] Revolve032
  Angle = 360
  Axis = (0,1,0)
  Base = (0,0,0)
  FaceMakerClass = Part::FaceMakerBullseye
  Placement = pos=(62.3,38,51.7) rot=(0,0,1;0rad)
  Solid = true
  Source = -> Wire002
  Symmetric = false
FEATURE [Part::Feature] Wire003
  shape: bbox 11 x 5.2 x 2e-07 mm, 0 faces, 0 solids (baked)
FEATURE [Part::Revolution] Revolve033
  Angle = 360
  Axis = (0,1,0)
  Base = (0,0,0)
  FaceMakerClass = Part::FaceMakerBullseye
  Placement = pos=(62.3,38,19.7) rot=(0,0,1;0rad)
  Solid = true
  Source = -> Wire003
  Symmetric = false
FEATURE [Part::MultiFuse] Fusion045  label="altRandScrewHousing"
  Shapes = -> [Revolve029,Revolve027,Revolve028,Revolve026]
FEATURE [Part::MultiFuse] Fusion046  label="fanScrewHousing"
  Shapes = -> [Revolve033,Revolve032,Revolve031,Revolve030]
FEATURE [Sketcher::SketchObject] Sketch015
  FullyConstrained = true
  sketch-geometry (17):
    g0: Circle CenterX=-3.5 CenterY=23.5 CenterZ=0 NormalX=0 NormalY=0 NormalZ=1 AngleXU=0 Radius=1
    g1: Circle CenterX=-1 CenterY=15.25 CenterZ=0 NormalX=0 NormalY=0 NormalZ=1 AngleXU=0 Radius=1
    g2: Circle CenterX=-3.5 CenterY=7 CenterZ=0 NormalX=0 NormalY=0 NormalZ=1 AngleXU=0 Radius=1
    g3: BSplineCurve PolesCount=3 KnotsCount=2 Degree=2 IsPeriodic=0
    g4: GeomPoint X=-3.5 Y=23.5 Z=0
    g5: GeomPoint X=-3.5 Y=7 Z=0
    g6: Circle CenterX=-4.8 CenterY=30.5 CenterZ=0 NormalX=0 NormalY=0 NormalZ=1 AngleXU=0 Radius=1
    g7: Circle CenterX=-3.5 CenterY=30.5 CenterZ=0 NormalX=0 NormalY=0 NormalZ=1 AngleXU=0 Radius=1
    g8: Circle CenterX=-3.5 CenterY=29.2 CenterZ=0 NormalX=0 NormalY=0 NormalZ=1 AngleXU=0 Radius=1
    g9: BSplineCurve PolesCount=3 KnotsCount=2 Degree=2 IsPeriodic=0
    g10: GeomPoint X=-4.8 Y=30.5 Z=0
    g11: GeomPoint X=-3.5 Y=29.2 Z=0
    g12: LineSegment StartX=-3.5 StartY=29.2 StartZ=0 EndX=-3.5 EndY=23.5 EndZ=0
    g13: LineSegment StartX=-4.8 StartY=30.5 StartZ=0 EndX=0 EndY=30.5 EndZ=0
    g14: LineSegment StartX=-3.5 StartY=0.3 StartZ=0 EndX=0 EndY=0.3 EndZ=0
    g15: LineSegment StartX=-3.5 StartY=0.3 StartZ=0 EndX=-3.5 EndY=7 EndZ=0
    g16: LineSegment StartX=0 StartY=0.3 StartZ=0 EndX=0 EndY=30.5 EndZ=0
  constraints (33):
    c: Weight(g0) = 1
    c: Equal(g0,g1)
    c: Equal(g0,g2)
    c: InternalAlignment(g0,g3)
    c: InternalAlignment(g1,g3)
    c: InternalAlignment(g2,g3)
    c: InternalAlignment(g4,g3)
    c: InternalAlignment(g5,g3)
    c: Block(g3)
    c: Weight(g6) = 1
    c: Equal(g6,g7)
    c: Equal(g6,g8)
    c: InternalAlignment(g6,g9)
    c: InternalAlignment(g7,g9)
    c: InternalAlignment(g8,g9)
    c: InternalAlignment(g10,g9)
    c: InternalAlignment(g11,g9)
    c: Block(g9)
    c: Coincident(g12,g9)
    c: Coincident(g12,g3)
    c: Vertical(g12)
    c: Coincident(g13,g9)
    c: Horizontal(g13)
    c: Distance(g13) = 4.8
    c: Horizontal(g14)
    c: Block(g14)
    c: Coincident(g15,g14)
    c: Coincident(g15,g3)
    c: Vertical(g15)
    c: Coincident(g16,g14)
    c: Coincident(g16,g13)
    c: Vertical(g16)
    c: Tangent(g16,g1)
FEATURE [Sketcher::SketchObject] Sketch016
  FullyConstrained = true
  sketch-geometry (16):
    g0: Circle CenterX=-3.5 CenterY=23.5 CenterZ=0 NormalX=0 NormalY=0 NormalZ=1 AngleXU=0 Radius=1
    g1: Circle CenterX=-1 CenterY=15.25 CenterZ=0 NormalX=0 NormalY=0 NormalZ=1 AngleXU=0 Radius=1
    g2: Circle CenterX=-3.5 CenterY=7 CenterZ=0 NormalX=0 NormalY=0 NormalZ=1 AngleXU=0 Radius=1
    g3: BSplineCurve PolesCount=3 KnotsCount=2 Degree=2 IsPeriodic=0
    g4: GeomPoint X=-3.5 Y=23.5 Z=0
    g5: GeomPoint X=-3.5 Y=7 Z=0
    g6: LineSegment StartX=-3.5 StartY=28.2 StartZ=0 EndX=-3.5 EndY=23.5 EndZ=0
    g7: LineSegment StartX=0 StartY=29.5 StartZ=0 EndX=0 EndY=30 EndZ=0
    g8: LineSegment StartX=-3.5 StartY=28.2 StartZ=0 EndX=-3.5 EndY=30 EndZ=0
    g9: LineSegment StartX=0 StartY=30 StartZ=0 EndX=0 EndY=30.5 EndZ=0
    g10: LineSegment StartX=0 StartY=30.5 StartZ=0 EndX=-3.5 EndY=30.5 EndZ=0
    g11: LineSegment StartX=-3.5 StartY=30.5 StartZ=0 EndX=-3.5 EndY=30 EndZ=0
    g12: LineSegment StartX=0 StartY=29.5 StartZ=0 EndX=0 EndY=5 EndZ=0
    g13: LineSegment StartX=-3.5 StartY=0.3 StartZ=0 EndX=-3.5 EndY=7 EndZ=0
    g14: LineSegment StartX=-3.5 StartY=0.3 StartZ=0 EndX=0 EndY=0.3 EndZ=0
    g15: LineSegment StartX=0 StartY=5 StartZ=0 EndX=0 EndY=0.3 EndZ=0
  constraints (39):
    c: Weight(g0) = 1
    c: Equal(g0,g1)
    c: Equal(g0,g2)
    c: InternalAlignment(g0,g3)
    c: InternalAlignment(g1,g3)
    c: InternalAlignment(g2,g3)
    c: InternalAlignment(g4,g3)
    c: InternalAlignment(g5,g3)
    c: Block(g3)
    c: Coincident(g6,g3)
    c: Vertical(g6)
    c: Vertical(g7)
    c: Distance(g7) = 0.5
    c: Coincident(g8,g6)
    c: Vertical(g8)
    c: Block(g6)
    c: Block(g7)
    c: Vertical(g9)
    c: Equal(g7,g9) = 0.5
    c: Block(g9)
    c: Coincident(g9,g7)
    c: Horizontal(g10)
    c: Coincident(g10,g9)
    c: Coincident(g11,g10)
    c: Coincident(g11,g8)
    c: Vertical(g11)
    c: Block(g11)
    c: Coincident(g12,g7)
    c: Vertical(g12)
    c: Coincident(g13,g3)
    c: Vertical(g13)
    c: Distance(g13) = 6.7
    c: Coincident(g14,g13)
    c: Horizontal(g14)
    c: Block(g14)
    c: Coincident(g15,g12)
    c: Coincident(g15,g14)
    c: Vertical(g15)
    c: Block(g15)
FEATURE [Sketcher::SketchObject] Sketch017
  FullyConstrained = true
  sketch-geometry (11):
    g0: LineSegment StartX=-3.5 StartY=1e-16 StartZ=0 EndX=-1.6 EndY=1e-16 EndZ=0
    g1: LineSegment StartX=-1.6 StartY=1e-16 StartZ=0 EndX=-1.6 EndY=1.5 EndZ=0
    g2: LineSegment StartX=-3.5 StartY=1.5 StartZ=0 EndX=-1.6 EndY=1.5 EndZ=0
    g3: LineSegment StartX=-3.5 StartY=1e-16 StartZ=0 EndX=-4.8 EndY=1e-16 EndZ=0
    g4: Circle CenterX=-3.5 CenterY=1.3 CenterZ=0 NormalX=0 NormalY=0 NormalZ=1 AngleXU=0 Radius=1
    g5: Circle CenterX=-3.5 CenterY=1e-16 CenterZ=0 NormalX=0 NormalY=0 NormalZ=1 AngleXU=0 Radius=1
    g6: Circle CenterX=-4.8 CenterY=1e-16 CenterZ=0 NormalX=0 NormalY=0 NormalZ=1 AngleXU=0 Radius=1
    g7: BSplineCurve PolesCount=3 KnotsCount=2 Degree=2 IsPeriodic=0
    g8: GeomPoint X=-3.5 Y=1.3 Z=0
    g9: GeomPoint X=-4.8 Y=1e-16 Z=0
    g10: LineSegment StartX=-3.5 StartY=1.3 StartZ=0 EndX=-3.5 EndY=1.5 EndZ=0
  constraints (24):
    c: Horizontal(g0)
    c: Distance(g0) = 1.9
    c: Block(g0)
    c: Coincident(g1,g0)
    c: Vertical(g1)
    c: Coincident(g2,g1)
    c: Horizontal(g2)
    c: Coincident(g3,g0)
    c: Horizontal(g3)
    c: Distance(g3) = 1.3
    c: Weight(g4) = 1
    c: Equal(g4,g5)
    c: Coincident(g5,g0)
    c: Equal(g4,g6)
    c: Coincident(g7,g3)
    c: InternalAlignment(g4,g7)
    c: InternalAlignment(g5,g7)
    c: InternalAlignment(g6,g7)
    c: InternalAlignment(g8,g7)
    c: InternalAlignment(g9,g7)
    c: Coincident(g10,g7)
    c: Coincident(g10,g2)
    c: Vertical(g10)
    c: Block(g10)
FEATURE [Part::Feature] Face035
  shape: bbox 3.2 x 1.5 x 2e-07 mm, 1 faces, 0 solids (baked)
FEATURE [Part::Revolution] Revolve039  label="backCaseScrewRetainer"
  Angle = 360
  Axis = (0,1,0)
  Base = (0,0,0)
  FaceMakerClass = Part::FaceMakerBullseye
  Placement = pos=(12.5,3,62) rot=(0,0,1;0rad)
  Solid = false
  Source = -> Face035
  Symmetric = false
FEATURE [Part::Feature] Face036
  shape: bbox 3.2 x 1.5 x 2e-07 mm, 1 faces, 0 solids (baked)
FEATURE [Part::Feature] Face039
  shape: bbox 4.8 x 30.2 x 2e-07 mm, 1 faces, 0 solids (baked)
FEATURE [Part::Revolution] Revolve043  label="frontCaseScrewPost002"
  Angle = 360
  Axis = (0,1,0)
  Base = (0,0,0)
  FaceMakerClass = Part::FaceMakerBullseye
  Placement = pos=(89.5,4.5,3.5) rot=(0,0,1;0rad)
  Solid = false
  Source = -> Face039
  Symmetric = false
FEATURE [Part::Feature] Face042
  shape: bbox 4.8 x 30.2 x 2e-07 mm, 1 faces, 0 solids (baked)
FEATURE [Part::Revolution] Revolve046  label="frontCaseScrewPost003"
  Angle = 360
  Axis = (0,1,0)
  Base = (0,0,0)
  FaceMakerClass = Part::FaceMakerBullseye
  Placement = pos=(89.5,4.5,68.5) rot=(0,0,1;0rad)
  Solid = false
  Source = -> Face042
  Symmetric = false
FEATURE [Part::Feature] Face043
  shape: bbox 3.2 x 1.5 x 2e-07 mm, 1 faces, 0 solids (baked)
FEATURE [Part::Revolution] Revolve047  label="frontCaseScrewRetainer002"
  Angle = 360
  Axis = (0,1,0)
  Base = (0,0,0)
  FaceMakerClass = Part::FaceMakerBullseye
  Placement = pos=(89.5,3,68.5) rot=(0,0,1;0rad)
  Solid = false
  Source = -> Face043
  Symmetric = false
FEATURE [Part::Feature] Face044
  shape: bbox 3.2 x 1.5 x 2e-07 mm, 1 faces, 0 solids (baked)
FEATURE [Part::Revolution] Revolve048  label="frontCaseScrewRetainer003"
  Angle = 360
  Axis = (0,1,0)
  Base = (0,0,0)
  FaceMakerClass = Part::FaceMakerBullseye
  Placement = pos=(89.5,3,3.5) rot=(0,0,1;0rad)
  Solid = false
  Source = -> Face044
  Symmetric = false
FEATURE [App::MeasureDistance] Distance002  label="Distance: 1.67 mm"
  Distance = 1.66921
  P1 = (99.2361,4.7524,71.7)
  P2 = (99.2347,6.42161,71.7)
FEATURE [Sketcher::SketchObject] Sketch018
  FullyConstrained = true
  sketch-geometry (7):
    g0: LineSegment StartX=0 StartY=0 StartZ=0 EndX=0 EndY=6 EndZ=0
    g1: Circle CenterX=0 CenterY=0 CenterZ=0 NormalX=0 NormalY=0 NormalZ=1 AngleXU=0 Radius=1
    g2: Circle CenterX=8 CenterY=6 CenterZ=0 NormalX=0 NormalY=0 NormalZ=1 AngleXU=0 Radius=1
    g3: BSplineCurve PolesCount=3 KnotsCount=2 Degree=2 IsPeriodic=0
    g4: GeomPoint X=0 Y=0 Z=0
    g5: GeomPoint X=8 Y=6 Z=0
    g6: LineSegment StartX=0 StartY=6 StartZ=0 EndX=8 EndY=6 EndZ=0
  constraints (14):
    c: Coincident(g0,g-1)
    c: Distance(g0) = 6
    c: Vertical(g0)
    c: Coincident(g3,g0)
    c: Weight(g1) = 1
    c: Equal(g1,g2)
    c: InternalAlignment(g1,g3)
    c: InternalAlignment(g2,g3)
    c: InternalAlignment(g4,g3)
    c: InternalAlignment(g5,g3)
    c: Block(g3)
    c: Coincident(g6,g0)
    c: Coincident(g6,g3)
    c: Horizontal(g6)
FEATURE [Part::Extrusion] Extrude012  label="caseScrewPillarBracket"
  Base = -> Sketch018
  Dir = (0,0,1)
  DirMode = 2
  FaceMakerClass = Part::FaceMakerBullseye
  LengthFwd = 2.4
  LengthRev = 0
  Placement = pos=(15.76,29,8.8) rot=(0,1,0;0rad)
  Solid = true
  Symmetric = false
FEATURE [Sketcher::SketchObject] Sketch019
  FullyConstrained = true
  sketch-geometry (7):
    g0: LineSegment StartX=0 StartY=0 StartZ=0 EndX=0 EndY=6 EndZ=0
    g1: Circle CenterX=0 CenterY=0 CenterZ=0 NormalX=0 NormalY=0 NormalZ=1 AngleXU=0 Radius=1
    g2: Circle CenterX=8 CenterY=6 CenterZ=0 NormalX=0 NormalY=0 NormalZ=1 AngleXU=0 Radius=1
    g3: BSplineCurve PolesCount=3 KnotsCount=2 Degree=2 IsPeriodic=0
    g4: GeomPoint X=0 Y=0 Z=0
    g5: GeomPoint X=8 Y=6 Z=0
    g6: LineSegment StartX=0 StartY=6 StartZ=0 EndX=8 EndY=6 EndZ=0
  constraints (14):
    c: Coincident(g0,g-1)
    c: Distance(g0) = 6
    c: Vertical(g0)
    c: Coincident(g3,g0)
    c: Weight(g1) = 1
    c: Equal(g1,g2)
    c: InternalAlignment(g1,g3)
    c: InternalAlignment(g2,g3)
    c: InternalAlignment(g4,g3)
    c: InternalAlignment(g5,g3)
    c: Block(g3)
    c: Coincident(g6,g0)
    c: Coincident(g6,g3)
    c: Horizontal(g6)
FEATURE [Part::Extrusion] Extrude013  label="caseScrewPillarBracket001"
  Base = -> Sketch019
  Dir = (0,0,1)
  DirMode = 2
  FaceMakerClass = Part::FaceMakerBullseye
  LengthFwd = 2.4
  LengthRev = 0
  Placement = pos=(15.76,29,60.8) rot=(0,0,1;0rad)
  Solid = true
  Symmetric = false
FEATURE [Sketcher::SketchObject] Sketch020
  FullyConstrained = true
  sketch-geometry (7):
    g0: LineSegment StartX=0 StartY=0 StartZ=0 EndX=0 EndY=6 EndZ=0
    g1: Circle CenterX=0 CenterY=0 CenterZ=0 NormalX=0 NormalY=0 NormalZ=1 AngleXU=0 Radius=1
    g2: Circle CenterX=8 CenterY=6 CenterZ=0 NormalX=0 NormalY=0 NormalZ=1 AngleXU=0 Radius=1
    g3: BSplineCurve PolesCount=3 KnotsCount=2 Degree=2 IsPeriodic=0
    g4: GeomPoint X=0 Y=0 Z=0
    g5: GeomPoint X=8 Y=6 Z=0
    g6: LineSegment StartX=0 StartY=6 StartZ=0 EndX=8 EndY=6 EndZ=0
  constraints (14):
    c: Coincident(g0,g-1)
    c: Distance(g0) = 6
    c: Vertical(g0)
    c: Coincident(g3,g0)
    c: Weight(g1) = 1
    c: Equal(g1,g2)
    c: InternalAlignment(g1,g3)
    c: InternalAlignment(g2,g3)
    c: InternalAlignment(g4,g3)
    c: InternalAlignment(g5,g3)
    c: Block(g3)
    c: Coincident(g6,g0)
    c: Coincident(g6,g3)
    c: Horizontal(g6)
FEATURE [Part::Extrusion] Extrude014  label="caseScrewPillarBracket002"
  Base = -> Sketch020
  Dir = (0,0,1)
  DirMode = 2
  FaceMakerClass = Part::FaceMakerBullseye
  LengthFwd = 2.4
  LengthRev = 0
  Placement = pos=(13.7,29,13.26) rot=(0,-1,0;1.5708rad)
  Solid = true
  Symmetric = false
FEATURE [Sketcher::SketchObject] Sketch021
  FullyConstrained = true
  sketch-geometry (7):
    g0: LineSegment StartX=0 StartY=0 StartZ=0 EndX=0 EndY=6 EndZ=0
    g1: Circle CenterX=0 CenterY=0 CenterZ=0 NormalX=0 NormalY=0 NormalZ=1 AngleXU=0 Radius=1
    g2: Circle CenterX=8 CenterY=6 CenterZ=0 NormalX=0 NormalY=0 NormalZ=1 AngleXU=0 Radius=1
    g3: BSplineCurve PolesCount=3 KnotsCount=2 Degree=2 IsPeriodic=0
    g4: GeomPoint X=0 Y=0 Z=0
    g5: GeomPoint X=8 Y=6 Z=0
    g6: LineSegment StartX=0 StartY=6 StartZ=0 EndX=8 EndY=6 EndZ=0
  constraints (14):
    c: Coincident(g0,g-1)
    c: Distance(g0) = 6
    c: Vertical(g0)
    c: Coincident(g3,g0)
    c: Weight(g1) = 1
    c: Equal(g1,g2)
    c: InternalAlignment(g1,g3)
    c: InternalAlignment(g2,g3)
    c: InternalAlignment(g4,g3)
    c: InternalAlignment(g5,g3)
    c: Block(g3)
    c: Coincident(g6,g0)
    c: Coincident(g6,g3)
    c: Horizontal(g6)
FEATURE [Part::Extrusion] Extrude015  label="caseScrewPillarBracket003"
  Base = -> Sketch021
  Dir = (0,0,1)
  DirMode = 2
  FaceMakerClass = Part::FaceMakerBullseye
  LengthFwd = 2.4
  LengthRev = 0
  Placement = pos=(11.3,29,58.74) rot=(0,1,0;1.5708rad)
  Solid = true
  Symmetric = false
FEATURE [Sketcher::SketchObject] Sketch022
  FullyConstrained = true
  sketch-geometry (7):
    g0: LineSegment StartX=0 StartY=0 StartZ=0 EndX=0 EndY=6 EndZ=0
    g1: Circle CenterX=0 CenterY=0 CenterZ=0 NormalX=0 NormalY=0 NormalZ=1 AngleXU=0 Radius=1
    g2: Circle CenterX=8 CenterY=6 CenterZ=0 NormalX=0 NormalY=0 NormalZ=1 AngleXU=0 Radius=1
    g3: BSplineCurve PolesCount=3 KnotsCount=2 Degree=2 IsPeriodic=0
    g4: GeomPoint X=0 Y=0 Z=0
    g5: GeomPoint X=8 Y=6 Z=0
    g6: LineSegment StartX=0 StartY=6 StartZ=0 EndX=8 EndY=6 EndZ=0
  constraints (14):
    c: Coincident(g0,g-1)
    c: Distance(g0) = 6
    c: Vertical(g0)
    c: Coincident(g3,g0)
    c: Weight(g1) = 1
    c: Equal(g1,g2)
    c: InternalAlignment(g1,g3)
    c: InternalAlignment(g2,g3)
    c: InternalAlignment(g4,g3)
    c: InternalAlignment(g5,g3)
    c: Block(g3)
    c: Coincident(g6,g0)
    c: Coincident(g6,g3)
    c: Horizontal(g6)
FEATURE [Part::Extrusion] Extrude016  label="caseScrewPillarBracket004"
  Base = -> Sketch022
  Dir = (0,0,1)
  DirMode = 2
  FaceMakerClass = Part::FaceMakerBullseye
  LengthFwd = 2.4
  LengthRev = 0
  Placement = pos=(88.3,29,65.23) rot=(0,1,0;1.5708rad)
  Solid = true
  Symmetric = false
FEATURE [Sketcher::SketchObject] Sketch023
  FullyConstrained = true
  sketch-geometry (7):
    g0: LineSegment StartX=0 StartY=0 StartZ=0 EndX=0 EndY=6 EndZ=0
    g1: Circle CenterX=0 CenterY=0 CenterZ=0 NormalX=0 NormalY=0 NormalZ=1 AngleXU=0 Radius=1
    g2: Circle CenterX=8 CenterY=6 CenterZ=0 NormalX=0 NormalY=0 NormalZ=1 AngleXU=0 Radius=1
    g3: BSplineCurve PolesCount=3 KnotsCount=2 Degree=2 IsPeriodic=0
    g4: GeomPoint X=0 Y=0 Z=0
    g5: GeomPoint X=8 Y=6 Z=0
    g6: LineSegment StartX=0 StartY=6 StartZ=0 EndX=8 EndY=6 EndZ=0
  constraints (14):
    c: Coincident(g0,g-1)
    c: Distance(g0) = 6
    c: Vertical(g0)
    c: Coincident(g3,g0)
    c: Weight(g1) = 1
    c: Equal(g1,g2)
    c: InternalAlignment(g1,g3)
    c: InternalAlignment(g2,g3)
    c: InternalAlignment(g4,g3)
    c: InternalAlignment(g5,g3)
    c: Block(g3)
    c: Coincident(g6,g0)
    c: Coincident(g6,g3)
    c: Horizontal(g6)
FEATURE [Part::Extrusion] Extrude017  label="caseScrewPillarBracket005"
  Base = -> Sketch023
  Dir = (0,0,1)
  DirMode = 2
  FaceMakerClass = Part::FaceMakerBullseye
  LengthFwd = 2.4
  LengthRev = 0
  Placement = pos=(90.7,29,6.77) rot=(0,-1,0;1.5708rad)
  Solid = true
  Symmetric = false
FEATURE [Sketcher::SketchObject] Sketch024
  FullyConstrained = true
  sketch-geometry (7):
    g0: LineSegment StartX=0 StartY=0 StartZ=0 EndX=0 EndY=6 EndZ=0
    g1: Circle CenterX=0 CenterY=0 CenterZ=0 NormalX=0 NormalY=0 NormalZ=1 AngleXU=0 Radius=1
    g2: Circle CenterX=8 CenterY=6 CenterZ=0 NormalX=0 NormalY=0 NormalZ=1 AngleXU=0 Radius=1
    g3: BSplineCurve PolesCount=3 KnotsCount=2 Degree=2 IsPeriodic=0
    g4: GeomPoint X=0 Y=0 Z=0
    g5: GeomPoint X=8 Y=6 Z=0
    g6: LineSegment StartX=0 StartY=6 StartZ=0 EndX=8 EndY=6 EndZ=0
  constraints (14):
    c: Coincident(g0,g-1)
    c: Distance(g0) = 6
    c: Vertical(g0)
    c: Coincident(g3,g0)
    c: Weight(g1) = 1
    c: Equal(g1,g2)
    c: InternalAlignment(g1,g3)
    c: InternalAlignment(g2,g3)
    c: InternalAlignment(g4,g3)
    c: InternalAlignment(g5,g3)
    c: Block(g3)
    c: Coincident(g6,g0)
    c: Coincident(g6,g3)
    c: Horizontal(g6)
FEATURE [Part::Extrusion] Extrude018  label="caseScrewPillarBracket006"
  Base = -> Sketch024
  Dir = (0,0,1)
  DirMode = 2
  FaceMakerClass = Part::FaceMakerBullseye
  LengthFwd = 2.4
  LengthRev = 0
  Placement = pos=(103.7,29,6.77) rot=(0,-1,0;1.5708rad)
  Solid = true
  Symmetric = false
FEATURE [Sketcher::SketchObject] Sketch025
  FullyConstrained = true
  sketch-geometry (7):
    g0: LineSegment StartX=0 StartY=0 StartZ=0 EndX=0 EndY=6 EndZ=0
    g1: Circle CenterX=0 CenterY=0 CenterZ=0 NormalX=0 NormalY=0 NormalZ=1 AngleXU=0 Radius=1
    g2: Circle CenterX=8 CenterY=6 CenterZ=0 NormalX=0 NormalY=0 NormalZ=1 AngleXU=0 Radius=1
    g3: BSplineCurve PolesCount=3 KnotsCount=2 Degree=2 IsPeriodic=0
    g4: GeomPoint X=0 Y=0 Z=0
    g5: GeomPoint X=8 Y=6 Z=0
    g6: LineSegment StartX=0 StartY=6 StartZ=0 EndX=8 EndY=6 EndZ=0
  constraints (14):
    c: Coincident(g0,g-1)
    c: Distance(g0) = 6
    c: Vertical(g0)
    c: Coincident(g3,g0)
    c: Weight(g1) = 1
    c: Equal(g1,g2)
    c: InternalAlignment(g1,g3)
    c: InternalAlignment(g2,g3)
    c: InternalAlignment(g4,g3)
    c: InternalAlignment(g5,g3)
    c: Block(g3)
    c: Coincident(g6,g0)
    c: Coincident(g6,g3)
    c: Horizontal(g6)
FEATURE [Part::Extrusion] Extrude019  label="caseScrewPillarBracket007"
  Base = -> Sketch025
  Dir = (0,0,1)
  DirMode = 2
  FaceMakerClass = Part::FaceMakerBullseye
  LengthFwd = 2.4
  LengthRev = 0
  Placement = pos=(101.3,29,65.23) rot=(0,1,0;1.5708rad)
  Solid = true
  Symmetric = false
FEATURE [Part::Box] Box011  label="frontCaseScrewPillarBracket"
  AttacherType = Attacher::AttachEngine3D
  Height = 2.4
  Length = 16
  Placement = pos=(87,28,2.3) rot=(0,0,1;0rad)
  Width = 7
FEATURE [Part::Box] Box012  label="frontCaseScrewPillarBracket001"
  AttacherType = Attacher::AttachEngine3D
  Height = 2.4
  Length = 16
  Placement = pos=(87,28,67.3) rot=(0,0,1;0rad)
  Width = 7
FEATURE [Sketcher::SketchObject] Sketch026
  FullyConstrained = true
  sketch-geometry (17):
    g0: Circle CenterX=-3.5 CenterY=23.5 CenterZ=0 NormalX=0 NormalY=0 NormalZ=1 AngleXU=0 Radius=1
    g1: Circle CenterX=-1 CenterY=15.25 CenterZ=0 NormalX=0 NormalY=0 NormalZ=1 AngleXU=0 Radius=1
    g2: Circle CenterX=-3.5 CenterY=7 CenterZ=0 NormalX=0 NormalY=0 NormalZ=1 AngleXU=0 Radius=1
    g3: BSplineCurve PolesCount=3 KnotsCount=2 Degree=2 IsPeriodic=0
    g4: GeomPoint X=-3.5 Y=23.5 Z=0
    g5: GeomPoint X=-3.5 Y=7 Z=0
    g6: Circle CenterX=-4.8 CenterY=30.5 CenterZ=0 NormalX=0 NormalY=0 NormalZ=1 AngleXU=0 Radius=1
    g7: Circle CenterX=-3.5 CenterY=30.5 CenterZ=0 NormalX=0 NormalY=0 NormalZ=1 AngleXU=0 Radius=1
    g8: Circle CenterX=-3.5 CenterY=29.2 CenterZ=0 NormalX=0 NormalY=0 NormalZ=1 AngleXU=0 Radius=1
    g9: BSplineCurve PolesCount=3 KnotsCount=2 Degree=2 IsPeriodic=0
    g10: GeomPoint X=-4.8 Y=30.5 Z=0
    g11: GeomPoint X=-3.5 Y=29.2 Z=0
    g12: LineSegment StartX=-3.5 StartY=29.2 StartZ=0 EndX=-3.5 EndY=23.5 EndZ=0
    g13: LineSegment StartX=-4.8 StartY=30.5 StartZ=0 EndX=0 EndY=30.5 EndZ=0
    g14: LineSegment StartX=-3.5 StartY=5 StartZ=0 EndX=-3.5 EndY=7 EndZ=0
    g15: LineSegment StartX=0 StartY=5 StartZ=0 EndX=0 EndY=30.5 EndZ=0
    g16: LineSegment StartX=-3.5 StartY=5 StartZ=0 EndX=0 EndY=5 EndZ=0
  constraints (33):
    c: Weight(g0) = 1
    c: Equal(g0,g1)
    c: Equal(g0,g2)
    c: InternalAlignment(g0,g3)
    c: InternalAlignment(g1,g3)
    c: InternalAlignment(g2,g3)
    c: InternalAlignment(g4,g3)
    c: InternalAlignment(g5,g3)
    c: Block(g3)
    c: Weight(g6) = 1
    c: Equal(g6,g7)
    c: Equal(g6,g8)
    c: InternalAlignment(g6,g9)
    c: InternalAlignment(g7,g9)
    c: InternalAlignment(g8,g9)
    c: InternalAlignment(g10,g9)
    c: InternalAlignment(g11,g9)
    c: Block(g9)
    c: Coincident(g12,g9)
    c: Coincident(g12,g3)
    c: Vertical(g12)
    c: Coincident(g13,g9)
    c: Horizontal(g13)
    c: Distance(g13) = 4.8
    c: Coincident(g14,g3)
    c: Vertical(g14)
    c: Coincident(g15,g13)
    c: Vertical(g15)
    c: Tangent(g15,g1)
    c: Distance(g14) = 2
    c: Coincident(g16,g14)
    c: Horizontal(g16)
    c: Coincident(g15,g16)
FEATURE [Part::Feature] Face050
  shape: bbox 4.8 x 25.5 x 2e-07 mm, 1 faces, 0 solids (baked)
FEATURE [Part::Revolution] Revolve054  label="moreFrontCaseScrewPost001"
  Angle = 360
  Axis = (0,1,0)
  Base = (0,0,0)
  FaceMakerClass = Part::FaceMakerBullseye
  Placement = pos=(102.5,4.5,3.5) rot=(0,0,1;0rad)
  Solid = false
  Source = -> Face050
  Symmetric = false
FEATURE [Part::Feature] Face051
  shape: bbox 4.8 x 25.5 x 2e-07 mm, 1 faces, 0 solids (baked)
FEATURE [Part::Revolution] Revolve055  label="moreFrontCaseScrewPost002"
  Angle = 360
  Axis = (0,1,0)
  Base = (0,0,0)
  FaceMakerClass = Part::FaceMakerBullseye
  Placement = pos=(102.5,4.5,68.5) rot=(0,0,1;0rad)
  Solid = false
  Source = -> Face051
  Symmetric = false
FEATURE [Sketcher::SketchObject] Sketch027
  FullyConstrained = true
  sketch-geometry (10):
    g0: LineSegment StartX=-1.6 StartY=4.7 StartZ=0 EndX=-1.6 EndY=1.7 EndZ=0
    g1: LineSegment StartX=-3.5 StartY=4.7 StartZ=0 EndX=-1.6 EndY=4.7 EndZ=0
    g2: LineSegment StartX=-1.6 StartY=1.7 StartZ=0 EndX=-1.6 EndY=1.5 EndZ=0
    g3: LineSegment StartX=-1.6 StartY=1.5 StartZ=0 EndX=-5.2 EndY=1.5 EndZ=0
    g4: Circle CenterX=-3.5 CenterY=4.7 CenterZ=0 NormalX=0 NormalY=0 NormalZ=1 AngleXU=0 Radius=1
    g5: Circle CenterX=-3.59627 CenterY=2.99743 CenterZ=0 NormalX=0 NormalY=0 NormalZ=1 AngleXU=0 Radius=1
    g6: Circle CenterX=-5.2 CenterY=1.5 CenterZ=0 NormalX=0 NormalY=0 NormalZ=1 AngleXU=0 Radius=1
    g7: BSplineCurve PolesCount=3 KnotsCount=2 Degree=2 IsPeriodic=0
    g8: GeomPoint X=-3.5 Y=4.7 Z=0
    g9: GeomPoint X=-5.2 Y=1.5 Z=0
  constraints (23):
    c: Vertical(g0)
    c: Distance(g0) = 3
    c: Coincident(g1,g0)
    c: Horizontal(g1)
    c: Block(g0)
    c: Block(g1)
    c: Coincident(g2,g0)
    c: Vertical(g2)
    c: Distance(g2) = 0.2
    c: Coincident(g3,g2)
    c: Horizontal(g3)
    c: Block(g3)
    c: Coincident(g7,g1)
    c: Weight(g4) = 1
    c: Equal(g4,g5)
    c: Equal(g4,g6)
    c: Coincident(g7,g3)
    c: InternalAlignment(g4,g7)
    c: InternalAlignment(g5,g7)
    c: InternalAlignment(g6,g7)
    c: InternalAlignment(g8,g7)
    c: InternalAlignment(g9,g7)
    c: Block(g7)
FEATURE [Sketcher::SketchObject] Sketch028
  FullyConstrained = true
  sketch-geometry (18):
    g0: LineSegment StartX=0 StartY=3e-16 StartZ=0 EndX=0 EndY=1.7 EndZ=0
    g1: LineSegment StartX=-3.5 StartY=0 StartZ=0 EndX=-3.5 EndY=0.9 EndZ=0
    g2: Circle CenterX=-2.7 CenterY=1.7 CenterZ=0 NormalX=0 NormalY=0 NormalZ=1 AngleXU=0 Radius=1
    g3: Circle CenterX=-3.5 CenterY=1.7 CenterZ=0 NormalX=0 NormalY=0 NormalZ=1 AngleXU=0 Radius=1
    g4: Circle CenterX=-3.5 CenterY=0.9 CenterZ=0 NormalX=0 NormalY=0 NormalZ=1 AngleXU=0 Radius=1
    g5: BSplineCurve PolesCount=3 KnotsCount=2 Degree=2 IsPeriodic=0
    g6: GeomPoint X=-2.7 Y=1.7 Z=0
    g7: GeomPoint X=-3.5 Y=0.9 Z=0
    g8: LineSegment StartX=-3.5 StartY=0 StartZ=0 EndX=-3.5 EndY=-7 EndZ=0
    g9: LineSegment StartX=0 StartY=3e-16 StartZ=0 EndX=0 EndY=-7 EndZ=0
    g10: LineSegment StartX=-3.5 StartY=-7 StartZ=0 EndX=0 EndY=-7 EndZ=0
    g11: LineSegment StartX=-2.7 StartY=1.7 StartZ=0 EndX=-1.6 EndY=1.7 EndZ=0
    g12: LineSegment StartX=0 StartY=1.7 StartZ=0 EndX=0 EndY=4.5 EndZ=0
    g13: LineSegment StartX=0 StartY=4.5 StartZ=0 EndX=0 EndY=10.8 EndZ=0
    g14: LineSegment StartX=0 StartY=10.8 StartZ=0 EndX=-2 EndY=10.8 EndZ=0
    g15: LineSegment StartX=-1.6 StartY=4.7 StartZ=0 EndX=-1.6 EndY=1.7 EndZ=0
    g16: LineSegment StartX=-1.6 StartY=4.7 StartZ=0 EndX=-2 EndY=4.7 EndZ=0
    g17: LineSegment StartX=-2 StartY=4.7 StartZ=0 EndX=-2 EndY=10.8 EndZ=0
  constraints (44):
    c: Vertical(g0)
    c: Vertical(g1)
    c: Distance(g1) = 0.9
    c: Block(g0)
    c: Distance(g0) = 1.7
    c: Weight(g2) = 1
    c: Equal(g2,g3)
    c: Equal(g2,g4)
    c: Coincident(g5,g1)
    c: InternalAlignment(g2,g5)
    c: InternalAlignment(g3,g5)
    c: InternalAlignment(g4,g5)
    c: InternalAlignment(g6,g5)
    c: InternalAlignment(g7,g5)
    c: Block(g5)
    c: Coincident(g8,g1)
    c: Vertical(g8)
    c: Distance(g8) = 7
    c: Vertical(g9)
    c: Equal(g8,g9) = 7
    c: Coincident(g9,g0)
    c: Coincident(g10,g8)
    c: Coincident(g10,g9)
    c: Horizontal(g10)
    c: Coincident(g11,g5)
    c: Horizontal(g11)
    c: Coincident(g12,g0)
    c: Vertical(g12)
    c: Distance(g12) = 2.8
    c: Coincident(g13,g12)
    c: Vertical(g13)
    c: Distance(g13) = 6.3
    c: Coincident(g14,g13)
    c: Horizontal(g14)
    c: Distance(g14) = 2
    c: Vertical(g15)
    c: Distance(g15) = 3
    c: Block(g11)
    c: Coincident(g15,g11)
    c: Coincident(g16,g15)
    c: Horizontal(g16)
    c: Coincident(g17,g16)
    c: Coincident(g17,g14)
    c: Vertical(g17)
FEATURE [Part::Revolution] Revolve040  label="backCaseScrewRetainer001"
  Angle = 360
  Axis = (0,1,0)
  Base = (0,0,0)
  FaceMakerClass = Part::FaceMakerBullseye
  Placement = pos=(12.5,3,10) rot=(0,0,1;0rad)
  Solid = false
  Source = -> Face036
  Symmetric = false
FEATURE [Part::Feature] Face055
  shape: bbox 3.5 x 30.2 x 2e-07 mm, 1 faces, 0 solids (baked)
FEATURE [Part::Revolution] Revolve059  label="backCaseScrewPost"
  Angle = 360
  Axis = (0,1,0)
  Base = (0,0,0)
  FaceMakerClass = Part::FaceMakerBullseye
  Placement = pos=(12.5,4.5,10) rot=(0,0,1;0rad)
  Solid = false
  Source = -> Face055
  Symmetric = false
FEATURE [Part::Feature] Face056
  shape: bbox 3.5 x 30.2 x 2e-07 mm, 1 faces, 0 solids (baked)
FEATURE [Part::Revolution] Revolve060  label="backCaseScrewPost001"
  Angle = 360
  Axis = (0,1,0)
  Base = (0,0,0)
  FaceMakerClass = Part::FaceMakerBullseye
  Placement = pos=(12.5,4.5,62) rot=(0,0,1;0rad)
  Solid = false
  Source = -> Face056
  Symmetric = false
FEATURE [Part::Feature] Face057
  shape: bbox 3.5 x 17.8 x 2e-07 mm, 1 faces, 0 solids (baked)
FEATURE [Part::Revolution] Revolve061  label="removeToCreateScrewAndThreadedInsertHole"
  Angle = 360
  Axis = (0,1,0)
  Base = (0,0,0)
  FaceMakerClass = Part::FaceMakerBullseye
  Placement = pos=(12.5,0,10) rot=(0,0,1;0rad)
  Solid = false
  Source = -> Face057
  Symmetric = false
FEATURE [Part::Feature] Face058
  shape: bbox 3.5 x 17.8 x 2e-07 mm, 1 faces, 0 solids (baked)
FEATURE [Part::Revolution] Revolve062  label="removeToCreateScrewAndThreadedInsertHole001"
  Angle = 360
  Axis = (0,1,0)
  Base = (0,0,0)
  FaceMakerClass = Part::FaceMakerBullseye
  Placement = pos=(12.5,0,62) rot=(0,0,1;0rad)
  Solid = false
  Source = -> Face058
  Symmetric = false
FEATURE [Part::Feature] Face059
  shape: bbox 3.5 x 17.8 x 2e-07 mm, 1 faces, 0 solids (baked)
FEATURE [Part::Revolution] Revolve063  label="removeToCreateScrewAndThreadedInsertHole002"
  Angle = 360
  Axis = (0,1,0)
  Base = (0,0,0)
  FaceMakerClass = Part::FaceMakerBullseye
  Placement = pos=(89.5,0,68.5) rot=(0,0,1;0rad)
  Solid = false
  Source = -> Face059
  Symmetric = false
FEATURE [Part::Feature] Face060
  shape: bbox 3.5 x 17.8 x 2e-07 mm, 1 faces, 0 solids (baked)
FEATURE [Part::Revolution] Revolve064  label="removeToCreateScrewAndThreadedInsertHole003"
  Angle = 360
  Axis = (0,1,0)
  Base = (0,0,0)
  FaceMakerClass = Part::FaceMakerBullseye
  Placement = pos=(89.5,0,3.5) rot=(0,0,1;0rad)
  Solid = false
  Source = -> Face060
  Symmetric = false
FEATURE [Part::Feature] Face061
  shape: bbox 3.5 x 17.8 x 2e-07 mm, 1 faces, 0 solids (baked)
FEATURE [Part::Revolution] Revolve065  label="removeToCreateScrewAndThreadedInsertHole004"
  Angle = 360
  Axis = (0,1,0)
  Base = (0,0,0)
  FaceMakerClass = Part::FaceMakerBullseye
  Placement = pos=(102.5,4.7,3.5) rot=(0,0,1;0rad)
  Solid = false
  Source = -> Face061
  Symmetric = false
FEATURE [Part::Feature] Face062
  shape: bbox 3.5 x 17.8 x 2e-07 mm, 1 faces, 0 solids (baked)
FEATURE [Part::Revolution] Revolve066  label="removeToCreateScrewAndThreadedInsertHole005"
  Angle = 360
  Axis = (0,1,0)
  Base = (0,0,0)
  FaceMakerClass = Part::FaceMakerBullseye
  Placement = pos=(102.5,4.7,68.5) rot=(0,0,1;0rad)
  Solid = false
  Source = -> Face062
  Symmetric = false
FEATURE [Part::MultiFuse] Fusion047  label="makeHoles"
  Shapes = -> [Revolve066,Revolve065,Revolve064,Revolve063,Revolve062,Revolve061]
FEATURE [Part::Feature] Face063
  shape: bbox 3.6 x 3.2 x 2e-07 mm, 1 faces, 0 solids (baked)
FEATURE [Part::Revolution] Revolve067  label="moreFrontCaseScrewRetainer002"
  Angle = 360
  Axis = (0,1,0)
  Base = (0,0,0)
  FaceMakerClass = Part::FaceMakerBullseye
  Placement = pos=(102.5,4.5,68.5) rot=(0,0,1;0rad)
  Solid = false
  Source = -> Face063
  Symmetric = false
FEATURE [Part::Feature] Face064
  shape: bbox 3.6 x 3.2 x 2e-07 mm, 1 faces, 0 solids (baked)
FEATURE [Part::Revolution] Revolve068  label="moreFrontCaseScrewRetainer003"
  Angle = 360
  Axis = (0,1,0)
  Base = (0,0,0)
  FaceMakerClass = Part::FaceMakerBullseye
  Placement = pos=(102.5,4.5,3.5) rot=(0,0,1;0rad)
  Solid = false
  Source = -> Face064
  Symmetric = false
FEATURE [Part::Feature] Face065
  shape: bbox 3.5 x 17.8 x 2e-07 mm, 1 faces, 0 solids (baked)
FEATURE [Part::Revolution] Revolve069  label="removeToCreateScrewAndThreadedInsertHole006"
  Angle = 360
  Axis = (0,1,0)
  Base = (0,0,0)
  FaceMakerClass = Part::FaceMakerBullseye
  Placement = pos=(12.5,0,10) rot=(0,0,1;0rad)
  Solid = false
  Source = -> Face065
  Symmetric = false
FEATURE [Part::Feature] Face066
  shape: bbox 3.5 x 17.8 x 2e-07 mm, 1 faces, 0 solids (baked)
FEATURE [Part::Revolution] Revolve070  label="removeToCreateScrewAndThreadedInsertHole007"
  Angle = 360
  Axis = (0,1,0)
  Base = (0,0,0)
  FaceMakerClass = Part::FaceMakerBullseye
  Placement = pos=(12.5,0,62) rot=(0,0,1;0rad)
  Solid = false
  Source = -> Face066
  Symmetric = false
FEATURE [Part::Feature] Face067
  shape: bbox 3.5 x 17.8 x 2e-07 mm, 1 faces, 0 solids (baked)
FEATURE [Part::Revolution] Revolve071  label="removeToCreateScrewAndThreadedInsertHole008"
  Angle = 360
  Axis = (0,1,0)
  Base = (0,0,0)
  FaceMakerClass = Part::FaceMakerBullseye
  Placement = pos=(89.5,0,68.5) rot=(0,0,1;0rad)
  Solid = false
  Source = -> Face067
  Symmetric = false
FEATURE [Part::Feature] Face068
  shape: bbox 3.5 x 17.8 x 2e-07 mm, 1 faces, 0 solids (baked)
FEATURE [Part::Revolution] Revolve072  label="removeToCreateScrewAndThreadedInsertHole009"
  Angle = 360
  Axis = (0,1,0)
  Base = (0,0,0)
  FaceMakerClass = Part::FaceMakerBullseye
  Placement = pos=(89.5,0,3.5) rot=(0,0,1;0rad)
  Solid = false
  Source = -> Face068
  Symmetric = false
FEATURE [Part::Feature] Face069
  shape: bbox 3.5 x 17.8 x 2e-07 mm, 1 faces, 0 solids (baked)
FEATURE [Part::Feature] Face070
  shape: bbox 3.5 x 17.8 x 2e-07 mm, 1 faces, 0 solids (baked)
FEATURE [Part::Revolution] Revolve073  label="removeToCreateScrewAndThreadedInsertHole010"
  Angle = 360
  Axis = (0,1,0)
  Base = (0,0,0)
  FaceMakerClass = Part::FaceMakerBullseye
  Placement = pos=(102.5,4.7,3.5) rot=(0,0,1;0rad)
  Solid = false
  Source = -> Face069
  Symmetric = false
FEATURE [Part::Revolution] Revolve074  label="removeToCreateScrewAndThreadedInsertHole011"
  Angle = 360
  Axis = (0,1,0)
  Base = (0,0,0)
  FaceMakerClass = Part::FaceMakerBullseye
  Placement = pos=(102.5,4.7,68.5) rot=(0,0,1;0rad)
  Solid = false
  Source = -> Face070
  Symmetric = false
FEATURE [Part::MultiFuse] Fusion048  label="makeHoles001"
  Shapes = -> [Revolve074,Revolve073,Revolve072,Revolve071,Revolve070,Revolve069]
FEATURE [Part::MultiFuse] Fusion049  label="caseScrewRetainers"
  Shapes = -> [Revolve067,Revolve068,Revolve048,Revolve047,Revolve039,Revolve040]
FEATURE [Part::Cut] Cut015  label="caseScrewRetainers001"
  Base = -> Fusion049
  Tool = -> Fusion048
FEATURE [Part::MultiFuse] Fusion050  label="casePillars"
  Shapes = -> [Revolve055,Revolve054,Revolve043,Revolve046,Revolve059,Revolve060]
FEATURE [Part::Feature] Face071 .. Face076  x6 (patterned run collapsed; names and placements below)
  shape: bbox 3.5 x 17.8 x 2e-07 mm, 1 faces, 0 solids (baked)
FEATURE [Part::Revolution] Revolve075  label="removeToCreateScrewAndThreadedInsertHole012"
  Angle = 360
  Axis = (0,1,0)
  Base = (0,0,0)
  FaceMakerClass = Part::FaceMakerBullseye
  Placement = pos=(12.5,0,10) rot=(0,0,1;0rad)
  Solid = false
  Source = -> Face071
  Symmetric = false
FEATURE [Part::Revolution] Revolve076  label="removeToCreateScrewAndThreadedInsertHole013"
  Angle = 360
  Axis = (0,1,0)
  Base = (0,0,0)
  FaceMakerClass = Part::FaceMakerBullseye
  Placement = pos=(12.5,0,62) rot=(0,0,1;0rad)
  Solid = false
  Source = -> Face072
  Symmetric = false
FEATURE [Part::Revolution] Revolve077  label="removeToCreateScrewAndThreadedInsertHole014"
  Angle = 360
  Axis = (0,1,0)
  Base = (0,0,0)
  FaceMakerClass = Part::FaceMakerBullseye
  Placement = pos=(89.5,0,68.5) rot=(0,0,1;0rad)
  Solid = false
  Source = -> Face073
  Symmetric = false
FEATURE [Part::Revolution] Revolve078  label="removeToCreateScrewAndThreadedInsertHole015"
  Angle = 360
  Axis = (0,1,0)
  Base = (0,0,0)
  FaceMakerClass = Part::FaceMakerBullseye
  Placement = pos=(89.5,0,3.5) rot=(0,0,1;0rad)
  Solid = false
  Source = -> Face074
  Symmetric = false
FEATURE [Part::Revolution] Revolve079  label="removeToCreateScrewAndThreadedInsertHole016"
  Angle = 360
  Axis = (0,1,0)
  Base = (0,0,0)
  FaceMakerClass = Part::FaceMakerBullseye
  Placement = pos=(102.5,4.7,3.5) rot=(0,0,1;0rad)
  Solid = false
  Source = -> Face075
  Symmetric = false
FEATURE [Part::Revolution] Revolve080  label="removeToCreateScrewAndThreadedInsertHole017"
  Angle = 360
  Axis = (0,1,0)
  Base = (0,0,0)
  FaceMakerClass = Part::FaceMakerBullseye
  Placement = pos=(102.5,4.7,68.5) rot=(0,0,1;0rad)
  Solid = false
  Source = -> Face076
  Symmetric = false
FEATURE [Part::MultiFuse] Fusion051  label="makeHoles002"
  Shapes = -> [Revolve080,Revolve079,Revolve078,Revolve077,Revolve076,Revolve075]
FEATURE [Part::Cut] Cut016  label="caesPillars"
  Base = -> Fusion050
  Tool = -> Fusion051
FEATURE [Part::Revolution] Revolve009  label="plugHousing016"
  Angle = 360
  Axis = (0,1,0)
  Base = (0,0,0)
  FaceMakerClass = Part::FaceMakerBullseye
  Placement = pos=(0,0,36.15) rot=(0,0,1;0rad)
  Solid = false
  Source = -> Face012
  Symmetric = false
FEATURE [Part::MultiFuse] Fusion014  label="plugHousing023"
  Placement = pos=(0,0,0) rot=(0,0,1;1.5708rad)
  Shapes = -> [Revolve011,Revolve009]
FEATURE [Part::Revolution] Revolve010  label="plugHousing017"
  Angle = 360
  Axis = (0,1,0)
  Base = (0,0,0)
  FaceMakerClass = Part::FaceMakerBullseye
  Placement = pos=(0,0,36.15) rot=(0,0,1;0rad)
  Solid = false
  Source = -> Face014
  Symmetric = false
FEATURE [Part::MultiFuse] Fusion015  label="plugHousing024"
  Placement = pos=(0,0,0) rot=(0,0,1;1.5708rad)
  Shapes = -> [Revolve010,Revolve015]
FEATURE [Part::Revolution] Revolve014  label="plugHousing026"
  Angle = 360
  Axis = (0,1,0)
  Base = (0,0,0)
  FaceMakerClass = Part::FaceMakerBullseye
  Placement = pos=(0,0,36.15) rot=(0,0,1;0rad)
  Solid = false
  Source = -> Face011
  Symmetric = false
FEATURE [Part::Revolution] Revolve013  label="plugHousing025"
  Angle = 360
  Axis = (0,1,0)
  Base = (0,0,0)
  FaceMakerClass = Part::FaceMakerBullseye
  Placement = pos=(0,0,36.15) rot=(0,0,1;0rad)
  Solid = false
  Source = -> Face015
  Symmetric = false
FEATURE [Part::MultiFuse] Fusion016  label="plugHousing028"
  Placement = pos=(0,19,0) rot=(0,0,1;3.14159rad)
  Shapes = -> [Fusion014,Fusion013]
FEATURE [Part::MultiFuse] Fusion011  label="plugHousing018"
  Placement = pos=(0,0,0) rot=(0,0,1;1.5708rad)
  Shapes = -> [Revolve014,Revolve013]
FEATURE [Part::MultiFuse] Fusion012  label="plugHousing019"
  Placement = pos=(0,19,0) rot=(0,0,1;3.14159rad)
  Shapes = -> [Fusion011,Fusion015]
FEATURE [Part::MultiFuse] Fusion017  label="plugHousing029"
  Placement = pos=(122.621,0,-0.15) rot=(0,0,1;0rad)
  Shapes = -> [Fusion016,Fusion012]
FEATURE [Part::MultiFuse] Fusion052  label="casePillarRetainers"
  Shapes = -> [Extrude012,Extrude013,Extrude014,Extrude015,Extrude016,Extrude017,Extrude018,Extrude019,Box011,Box012]
FEATURE [Part::Feature] Face077
  shape: bbox 3.5 x 17.8 x 2e-07 mm, 1 faces, 0 solids (baked)
FEATURE [Part::Revolution] Revolve081  label="removeToCreateScrewAndThreadedInsertHole018"
  Angle = 360
  Axis = (0,1,0)
  Base = (0,0,0)
  FaceMakerClass = Part::FaceMakerBullseye
  Placement = pos=(62.3,30.3,19.7) rot=(0,0,1;0rad)
  Solid = false
  Source = -> Face077
  Symmetric = false
FEATURE [Part::Feature] Face078
  shape: bbox 3.5 x 17.8 x 2e-07 mm, 1 faces, 0 solids (baked)
FEATURE [Part::Revolution] Revolve082  label="removeToCreateScrewAndThreadedInsertHole019"
  Angle = 360
  Axis = (0,1,0)
  Base = (0,0,0)
  FaceMakerClass = Part::FaceMakerBullseye
  Placement = pos=(62.3,30.3,51.7) rot=(0,0,1;0rad)
  Solid = false
  Source = -> Face078
  Symmetric = false
FEATURE [Part::Feature] Face079
  shape: bbox 3.5 x 17.8 x 2e-07 mm, 1 faces, 0 solids (baked)
FEATURE [Part::Revolution] Revolve083  label="removeToCreateScrewAndThreadedInsertHole020"
  Angle = 360
  Axis = (0,1,0)
  Base = (0,0,0)
  FaceMakerClass = Part::FaceMakerBullseye
  Placement = pos=(30.3,30.3,19.7) rot=(0,0,1;0rad)
  Solid = false
  Source = -> Face079
  Symmetric = false
FEATURE [Part::Feature] Face080
  shape: bbox 3.5 x 17.8 x 2e-07 mm, 1 faces, 0 solids (baked)
FEATURE [Part::Revolution] Revolve084  label="removeToCreateScrewAndThreadedInsertHole021"
  Angle = 360
  Axis = (0,1,0)
  Base = (0,0,0)
  FaceMakerClass = Part::FaceMakerBullseye
  Placement = pos=(30.3,30.3,51.7) rot=(0,0,1;0rad)
  Solid = false
  Source = -> Face080
  Symmetric = false
FEATURE [Part::MultiFuse] Fusion053  label="createThreadedInsertHolesForFan"
  Shapes = -> [Revolve081,Revolve082,Revolve083,Revolve084]
FEATURE [Part::Cut] Cut017  label="fanScrewHousing001"
  Base = -> Fusion046
  Tool = -> Fusion053
FEATURE [Part::Feature] Face081
  shape: bbox 3.5 x 17.8 x 2e-07 mm, 1 faces, 0 solids (baked)
FEATURE [Part::Revolution] Revolve085  label="removeToCreateScrewAndThreadedInsertHole022"
  Angle = 360
  Axis = (0,1,0)
  Base = (0,0,0)
  FaceMakerClass = Part::FaceMakerBullseye
  Placement = pos=(62.3,30.3,19.7) rot=(0,0,1;0rad)
  Solid = false
  Source = -> Face081
  Symmetric = false
FEATURE [Part::Feature] Face082
  shape: bbox 3.5 x 17.8 x 2e-07 mm, 1 faces, 0 solids (baked)
FEATURE [Part::Revolution] Revolve086  label="removeToCreateScrewAndThreadedInsertHole023"
  Angle = 360
  Axis = (0,1,0)
  Base = (0,0,0)
  FaceMakerClass = Part::FaceMakerBullseye
  Placement = pos=(62.3,30.3,51.7) rot=(0,0,1;0rad)
  Solid = false
  Source = -> Face082
  Symmetric = false
FEATURE [Part::Feature] Face083
  shape: bbox 3.5 x 17.8 x 2e-07 mm, 1 faces, 0 solids (baked)
FEATURE [Part::Revolution] Revolve087  label="removeToCreateScrewAndThreadedInsertHole024"
  Angle = 360
  Axis = (0,1,0)
  Base = (0,0,0)
  FaceMakerClass = Part::FaceMakerBullseye
  Placement = pos=(30.3,30.3,19.7) rot=(0,0,1;0rad)
  Solid = false
  Source = -> Face083
  Symmetric = false
FEATURE [Part::Feature] Face084
  shape: bbox 3.5 x 17.8 x 2e-07 mm, 1 faces, 0 solids (baked)
FEATURE [Part::Revolution] Revolve088  label="removeToCreateScrewAndThreadedInsertHole025"
  Angle = 360
  Axis = (0,1,0)
  Base = (0,0,0)
  FaceMakerClass = Part::FaceMakerBullseye
  Placement = pos=(30.3,30.3,51.7) rot=(0,0,1;0rad)
  Solid = false
  Source = -> Face084
  Symmetric = false
FEATURE [Part::MultiFuse] Fusion054  label="createThreadedInsertHolesForFan001"
  Shapes = -> [Revolve085,Revolve086,Revolve087,Revolve088]
FEATURE [Part::Cut] Cut018  label="top007"
  Base = -> Fusion040
  Tool = -> Fusion054
FEATURE [Sketcher::SketchObject] Sketch029
  FullyConstrained = false
  Placement = pos=(0,0,0) rot=(1,0,0;1.5708rad)
  sketch-geometry (24):
    g0: ArcOfCircle CenterX=-4 CenterY=-10.5 CenterZ=0 NormalX=0 NormalY=0 NormalZ=1 AngleXU=0 Radius=1.5 StartAngle=6e-16 EndAngle=3.14159
    g1: ArcOfCircle CenterX=-34.2 CenterY=-10.5 CenterZ=0 NormalX=0 NormalY=0 NormalZ=1 AngleXU=0 Radius=1.5 StartAngle=0 EndAngle=3.14159
    g2: ArcOfCircle CenterX=-34.2 CenterY=-27.7 CenterZ=0 NormalX=0 NormalY=0 NormalZ=1 AngleXU=0 Radius=1.5 StartAngle=3.14159 EndAngle=6.28319
    g3: ArcOfCircle CenterX=-4 CenterY=-27.7 CenterZ=0 NormalX=0 NormalY=0 NormalZ=1 AngleXU=0 Radius=1.5 StartAngle=3.1416 EndAngle=6.28319
    g4: ArcOfCircle CenterX=-10 CenterY=-4.3 CenterZ=0 NormalX=0 NormalY=0 NormalZ=1 AngleXU=0 Radius=1.5 StartAngle=2e-16 EndAngle=3.14159
    g5: ArcOfCircle CenterX=-16.1 CenterY=-1.8 CenterZ=0 NormalX=0 NormalY=0 NormalZ=1 AngleXU=0 Radius=1.5 StartAngle=5e-16 EndAngle=3.14159
    g6: ArcOfCircle CenterX=-22.1 CenterY=-1.8 CenterZ=0 NormalX=0 NormalY=0 NormalZ=1 AngleXU=0 Radius=1.5 StartAngle=5e-16 EndAngle=3.14159
    g7: ArcOfCircle CenterX=-28.2 CenterY=-4.3 CenterZ=0 NormalX=0 NormalY=0 NormalZ=1 AngleXU=0 Radius=1.5 StartAngle=2e-16 EndAngle=3.14159
    g8: ArcOfCircle CenterX=-10 CenterY=-33.9 CenterZ=0 NormalX=0 NormalY=0 NormalZ=1 AngleXU=0 Radius=1.5 StartAngle=3.14159 EndAngle=6.28319
    g9: ArcOfCircle CenterX=-16.1 CenterY=-36.4 CenterZ=0 NormalX=0 NormalY=0 NormalZ=1 AngleXU=0 Radius=1.5 StartAngle=3.14159 EndAngle=6.28319
    g10: ArcOfCircle CenterX=-22.1 CenterY=-36.4 CenterZ=0 NormalX=0 NormalY=0 NormalZ=1 AngleXU=0 Radius=1.5 StartAngle=3.14159 EndAngle=6.28319
    g11: ArcOfCircle CenterX=-28.2 CenterY=-33.9 CenterZ=0 NormalX=0 NormalY=0 NormalZ=1 AngleXU=0 Radius=1.5 StartAngle=3.14159 EndAngle=6.28319
    g12: LineSegment StartX=-35.7 StartY=-10.5 StartZ=0 EndX=-35.7 EndY=-27.7 EndZ=0
    g13: LineSegment StartX=-32.7 StartY=-10.5 StartZ=0 EndX=-32.7 EndY=-27.7 EndZ=0
    g14: LineSegment StartX=-29.7 StartY=-33.9 StartZ=0 EndX=-29.7 EndY=-4.3 EndZ=0
    g15: LineSegment StartX=-26.7 StartY=-33.9 StartZ=0 EndX=-26.7 EndY=-4.3 EndZ=0
    g16: LineSegment StartX=-2.5 StartY=-10.5 StartZ=0 EndX=-2.5 EndY=-27.7 EndZ=0
    g17: LineSegment StartX=-8.5 StartY=-4.3 StartZ=0 EndX=-8.5 EndY=-33.9 EndZ=0
    g18: LineSegment StartX=-5.5 StartY=-10.5 StartZ=0 EndX=-5.5 EndY=-27.7 EndZ=0
    g19: LineSegment StartX=-11.5 StartY=-4.3 StartZ=0 EndX=-11.5 EndY=-33.9 EndZ=0
    g20: LineSegment StartX=-14.6 StartY=-1.8 StartZ=0 EndX=-14.6 EndY=-36.4 EndZ=0
    g21: LineSegment StartX=-17.6 StartY=-1.8 StartZ=0 EndX=-17.6 EndY=-36.4 EndZ=0
    g22: LineSegment StartX=-20.6 StartY=-36.4 StartZ=0 EndX=-20.6 EndY=-1.8 EndZ=0
    g23: LineSegment StartX=-23.6 StartY=-1.8 StartZ=0 EndX=-23.6 EndY=-36.4 EndZ=0
  constraints (48):
    c: Block(g0)
    c: Block(g1)
    c: Block(g2)
    c: Block(g3)
    c: Block(g4)
    c: Block(g5)
    c: Block(g6)
    c: Block(g7)
    c: Block(g8)
    c: Block(g9)
    c: Block(g10)
    c: Block(g11)
    c: Coincident(g12,g1)
    c: Coincident(g12,g2)
    c: Vertical(g12)
    c: Coincident(g13,g1)
    c: Coincident(g13,g2)
    c: Vertical(g13)
    c: Coincident(g14,g11)
    c: Coincident(g14,g7)
    c: Vertical(g14)
    c: Coincident(g15,g11)
    c: Coincident(g15,g7)
    c: Vertical(g15)
    c: Coincident(g16,g0)
    c: Coincident(g16,g3)
    c: Vertical(g16)
    c: Coincident(g17,g4)
    c: Coincident(g17,g8)
    c: Vertical(g17)
    c: Coincident(g18,g0)
    c: Coincident(g18,g3)
    c: Vertical(g18)
    c: Coincident(g19,g4)
    c: Coincident(g19,g8)
    c: Vertical(g19)
    c: Coincident(g20,g5)
    c: Coincident(g20,g9)
    c: Vertical(g20)
    c: Coincident(g21,g5)
    c: Coincident(g21,g9)
    c: Vertical(g21)
    c: Coincident(g22,g10)
    c: Coincident(g22,g6)
    c: Vertical(g22)
    c: Coincident(g23,g6)
    c: Coincident(g23,g10)
    c: Vertical(g23)
FEATURE [Part::Extrusion] Extrude020  label="removeToCreateFanGrillHoles"
  Base = -> Sketch029
  Dir = (0,-1,6e-16)
  DirMode = 2
  FaceMakerClass = Part::FaceMakerBullseye
  LengthFwd = 10
  LengthRev = 0
  Placement = pos=(65.4,44,54.82) rot=(0,0,1;0rad)
  Solid = true
  Symmetric = false
FEATURE [Part::MultiFuse] Fusion055  label="top008"
  Shapes = -> [Cut017,Cut018]
FEATURE [Part::Cut] Cut019  label="top009"
  Base = -> Fusion055
  Tool = -> Extrude020
FEATURE [App::MeasureDistance] Distance003  label="Distance: 71.95 mm"
  Distance = 71.9513
  P1 = (117,38,72)
  P2 = (117,38,0.0487319)
FEATURE [Sketcher::SketchObject] Sketch030
  FullyConstrained = true
  Placement = pos=(117,19,0) rot=(0.57735,0.57735,0.57735;2.0944rad)
  sketch-geometry (48):
    g0: LineSegment StartX=-49.19 StartY=69.25 StartZ=0 EndX=-49.19 EndY=66.25 EndZ=0
    g1: LineSegment StartX=-49.19 StartY=63.5 StartZ=0 EndX=-49.19 EndY=60.5 EndZ=0
    g2: LineSegment StartX=-49.19 StartY=57.75 StartZ=0 EndX=-49.19 EndY=54.75 EndZ=0
    g3: LineSegment StartX=-49.19 StartY=52 StartZ=0 EndX=-49.19 EndY=49 EndZ=0
    g4: LineSegment StartX=-49.19 StartY=46.25 StartZ=0 EndX=-49.19 EndY=43.25 EndZ=0
    g5: LineSegment StartX=-49.19 StartY=40.5 StartZ=0 EndX=-49.19 EndY=37.5 EndZ=0
    g6: LineSegment StartX=-49.19 StartY=34.5 StartZ=0 EndX=-49.19 EndY=31.5 EndZ=0
    g7: LineSegment StartX=-49.19 StartY=28.75 StartZ=0 EndX=-49.19 EndY=25.75 EndZ=0
    g8: LineSegment StartX=-49.19 StartY=23 StartZ=0 EndX=-49.19 EndY=20 EndZ=0
    g9: LineSegment StartX=-49.19 StartY=17.25 StartZ=0 EndX=-49.19 EndY=14.25 EndZ=0
    g10: LineSegment StartX=-49.19 StartY=11.5 StartZ=0 EndX=-49.19 EndY=8.5 EndZ=0
    g11: LineSegment StartX=-49.19 StartY=5.75 StartZ=0 EndX=-49.19 EndY=2.75 EndZ=0
    g12: ArcOfCircle CenterX=-1.5 CenterY=67.75 CenterZ=0 NormalX=0 NormalY=0 NormalZ=1 AngleXU=0 Radius=1.5 StartAngle=4.71239 EndAngle=7.85398
    g13: ArcOfCircle CenterX=-1.5 CenterY=62 CenterZ=0 NormalX=0 NormalY=0 NormalZ=1 AngleXU=0 Radius=1.5 StartAngle=4.71239 EndAngle=7.85398
    g14: ArcOfCircle CenterX=-1.5 CenterY=56.25 CenterZ=0 NormalX=0 NormalY=0 NormalZ=1 AngleXU=0 Radius=1.5 StartAngle=4.71239 EndAngle=7.85398
    g15: ArcOfCircle CenterX=-11.49 CenterY=50.5 CenterZ=0 NormalX=0 NormalY=0 NormalZ=1 AngleXU=0 Radius=1.5 StartAngle=4.71239 EndAngle=7.85398
    g16: ArcOfCircle CenterX=-16.28 CenterY=44.75 CenterZ=0 NormalX=0 NormalY=0 NormalZ=1 AngleXU=0 Radius=1.5 StartAngle=4.71239 EndAngle=7.85398
    g17: ArcOfCircle CenterX=-18.2337 CenterY=39 CenterZ=0 NormalX=0 NormalY=0 NormalZ=1 AngleXU=0 Radius=1.5 StartAngle=4.71485 EndAngle=7.85398
    g18: ArcOfCircle CenterX=-16.2837 CenterY=27.25 CenterZ=0 NormalX=0 NormalY=0 NormalZ=1 AngleXU=0 Radius=1.5 StartAngle=4.71485 EndAngle=7.85398
    g19: ArcOfCircle CenterX=-18.2337 CenterY=33 CenterZ=0 NormalX=0 NormalY=0 NormalZ=1 AngleXU=0 Radius=1.5 StartAngle=4.71485 EndAngle=7.85398
    g20: ArcOfCircle CenterX=-11.49 CenterY=21.5 CenterZ=0 NormalX=0 NormalY=0 NormalZ=1 AngleXU=0 Radius=1.5 StartAngle=4.71239 EndAngle=7.85398
    g21: ArcOfCircle CenterX=-1.5 CenterY=4.25 CenterZ=0 NormalX=0 NormalY=0 NormalZ=1 AngleXU=0 Radius=1.5 StartAngle=4.71239 EndAngle=7.85398
    g22: ArcOfCircle CenterX=-1.5 CenterY=10 CenterZ=0 NormalX=0 NormalY=0 NormalZ=1 AngleXU=0 Radius=1.5 StartAngle=4.71239 EndAngle=7.85398
    g23: ArcOfCircle CenterX=-1.5 CenterY=15.75 CenterZ=0 NormalX=0 NormalY=0 NormalZ=1 AngleXU=0 Radius=1.5 StartAngle=4.71239 EndAngle=7.85398
    g24: LineSegment StartX=-49.19 StartY=69.25 StartZ=0 EndX=-1.5 EndY=69.25 EndZ=0
    g25: LineSegment StartX=-49.19 StartY=66.25 StartZ=0 EndX=-1.5 EndY=66.25 EndZ=0
    g26: LineSegment StartX=-49.19 StartY=63.5 StartZ=0 EndX=-1.5 EndY=63.5 EndZ=0
    g27: LineSegment StartX=-49.19 StartY=60.5 StartZ=0 EndX=-1.5 EndY=60.5 EndZ=0
    g28: LineSegment StartX=-49.19 StartY=57.75 StartZ=0 EndX=-1.5 EndY=57.75 EndZ=0
    g29: LineSegment StartX=-49.19 StartY=54.75 StartZ=0 EndX=-1.5 EndY=54.75 EndZ=0
    g30: LineSegment StartX=-49.19 StartY=52 StartZ=0 EndX=-11.49 EndY=52 EndZ=0
    g31: LineSegment StartX=-49.19 StartY=49 StartZ=0 EndX=-11.49 EndY=49 EndZ=0
    g32: LineSegment StartX=-49.19 StartY=46.25 StartZ=0 EndX=-16.28 EndY=46.25 EndZ=0
    g33: LineSegment StartX=-49.19 StartY=43.25 StartZ=0 EndX=-16.28 EndY=43.25 EndZ=0
    g34: LineSegment StartX=-49.19 StartY=40.5 StartZ=0 EndX=-18.2337 EndY=40.5 EndZ=0
    g35: LineSegment StartX=-49.19 StartY=37.5 StartZ=0 EndX=-18.23 EndY=37.5 EndZ=0
    g36: LineSegment StartX=-49.19 StartY=34.5 StartZ=0 EndX=-18.2337 EndY=34.5 EndZ=0
    g37: LineSegment StartX=-49.19 StartY=31.5 StartZ=0 EndX=-18.23 EndY=31.5 EndZ=0
    g38: LineSegment StartX=-49.19 StartY=28.75 StartZ=0 EndX=-16.2837 EndY=28.75 EndZ=0
    g39: LineSegment StartX=-49.19 StartY=25.75 StartZ=0 EndX=-16.28 EndY=25.75 EndZ=0
    g40: LineSegment StartX=-49.19 StartY=23 StartZ=0 EndX=-11.49 EndY=23 EndZ=0
    g41: LineSegment StartX=-49.19 StartY=20 StartZ=0 EndX=-11.49 EndY=20 EndZ=0
    g42: LineSegment StartX=-49.19 StartY=17.25 StartZ=0 EndX=-1.5 EndY=17.25 EndZ=0
    g43: LineSegment StartX=-49.19 StartY=14.25 StartZ=0 EndX=-1.5 EndY=14.25 EndZ=0
    g44: LineSegment StartX=-49.19 StartY=11.5 StartZ=0 EndX=-1.5 EndY=11.5 EndZ=0
    g45: LineSegment StartX=-49.19 StartY=8.5 StartZ=0 EndX=-1.5 EndY=8.5 EndZ=0
    g46: LineSegment StartX=-49.19 StartY=5.75 StartZ=0 EndX=-1.5 EndY=5.75 EndZ=0
    g47: LineSegment StartX=-49.19 StartY=2.75 StartZ=0 EndX=-1.5 EndY=2.75 EndZ=0
  constraints (120):
    c: Vertical(g0)
    c: Distance(g0) = 3
    c: Block(g0)
    c: Vertical(g1)
    c: Distance(g1) = 3
    c: Vertical(g2)
    c: Equal(g0,g2) = 3
    c: Block(g2)
    c: Vertical(g3)
    c: Equal(g1,g3) = 3
    c: Vertical(g4)
    c: Equal(g0,g4) = 3
    c: Block(g4)
    c: Vertical(g5)
    c: Equal(g1,g5) = 3
    c: Vertical(g6)
    c: Equal(g0,g6) = 3
    c: Block(g6)
    c: Vertical(g7)
    c: Equal(g1,g7) = 3
    c: Vertical(g8)
    c: Equal(g0,g8) = 3
    c: Block(g8)
    c: Vertical(g9)
    c: Equal(g1,g9) = 3
    c: Vertical(g10)
    c: Equal(g0,g10) = 3
    c: Block(g10)
    c: Vertical(g11)
    c: Equal(g1,g11) = 3
    c: Block(g12)
    c: Block(g13)
    c: Block(g14)
    c: Block(g15)
    c: Block(g16)
    c: Block(g17)
    c: Block(g18)
    c: Block(g19)
    c: Block(g20)
    c: Block(g21)
    c: Block(g22)
    c: Block(g23)
    c: Block(g11)
    c: Block(g9)
    c: Block(g7)
    c: Block(g5)
    c: Block(g3)
    c: Block(g1)
    c: Coincident(g24,g0)
    c: Coincident(g24,g12)
    c: Horizontal(g24)
    c: Coincident(g25,g0)
    c: Coincident(g25,g12)
    c: Horizontal(g25)
    c: Coincident(g26,g1)
    c: Coincident(g26,g13)
    c: Horizontal(g26)
    c: Coincident(g27,g1)
    c: Coincident(g27,g13)
    c: Horizontal(g27)
    c: Coincident(g28,g2)
    c: Coincident(g28,g14)
    c: Horizontal(g28)
    c: Coincident(g29,g2)
    c: Coincident(g29,g14)
    c: Horizontal(g29)
    c: Coincident(g30,g3)
    c: Coincident(g30,g15)
    c: Horizontal(g30)
    c: Coincident(g31,g3)
    c: Coincident(g31,g15)
    c: Horizontal(g31)
    c: Coincident(g32,g4)
    c: Coincident(g32,g16)
    c: Horizontal(g32)
    c: Coincident(g33,g4)
    c: Coincident(g33,g16)
    c: Horizontal(g33)
    c: Coincident(g34,g5)
    c: Coincident(g34,g17)
    c: Horizontal(g34)
    c: Coincident(g35,g5)
    c: Coincident(g35,g17)
    c: Horizontal(g35)
    c: Coincident(g36,g6)
    c: Coincident(g36,g19)
    c: Horizontal(g36)
    c: Coincident(g37,g6)
    c: Coincident(g37,g19)
    c: Horizontal(g37)
    c: Coincident(g38,g7)
    c: Coincident(g38,g18)
    c: Horizontal(g38)
    c: Coincident(g39,g7)
    c: Coincident(g39,g18)
    c: Horizontal(g39)
    c: Coincident(g40,g8)
    c: Coincident(g40,g20)
    c: Horizontal(g40)
    c: Coincident(g41,g8)
    c: Coincident(g41,g20)
    c: Horizontal(g41)
    c: Coincident(g42,g9)
    c: Coincident(g42,g23)
    c: Horizontal(g42)
    c: Coincident(g43,g9)
    c: Coincident(g43,g23)
    c: Horizontal(g43)
    c: Coincident(g44,g10)
    c: Coincident(g44,g22)
    c: Horizontal(g44)
    c: Coincident(g45,g10)
    c: Coincident(g45,g22)
    c: Horizontal(g45)
    c: Coincident(g46,g11)
    c: Coincident(g46,g21)
    c: Horizontal(g46)
    c: Coincident(g47,g11)
    c: Coincident(g47,g21)
    c: Horizontal(g47)
FEATURE [Sketcher::SketchObject] Sketch031
  FullyConstrained = true
  Placement = pos=(117,19,0) rot=(0.57735,0.57735,0.57735;2.0944rad)
  sketch-geometry (24):
    g0: ArcOfCircle CenterX=-49.19 CenterY=67.75 CenterZ=0 NormalX=0 NormalY=0 NormalZ=1 AngleXU=0 Radius=1.5 StartAngle=1.5708 EndAngle=4.71239
    g1: ArcOfCircle CenterX=-49.19 CenterY=62 CenterZ=0 NormalX=0 NormalY=0 NormalZ=1 AngleXU=0 Radius=1.5 StartAngle=1.5708 EndAngle=4.71239
    g2: ArcOfCircle CenterX=-49.19 CenterY=56.25 CenterZ=0 NormalX=0 NormalY=0 NormalZ=1 AngleXU=0 Radius=1.5 StartAngle=1.5708 EndAngle=4.71239
    g3: ArcOfCircle CenterX=-49.19 CenterY=50.5 CenterZ=0 NormalX=0 NormalY=0 NormalZ=1 AngleXU=0 Radius=1.5 StartAngle=1.5708 EndAngle=4.71239
    g4: ArcOfCircle CenterX=-49.19 CenterY=44.75 CenterZ=0 NormalX=0 NormalY=0 NormalZ=1 AngleXU=0 Radius=1.5 StartAngle=1.5708 EndAngle=4.71239
    g5: ArcOfCircle CenterX=-49.19 CenterY=39 CenterZ=0 NormalX=0 NormalY=0 NormalZ=1 AngleXU=0 Radius=1.5 StartAngle=1.5708 EndAngle=4.71239
    g6: ArcOfCircle CenterX=-49.19 CenterY=33 CenterZ=0 NormalX=0 NormalY=0 NormalZ=1 AngleXU=0 Radius=1.5 StartAngle=1.5708 EndAngle=4.71239
    g7: ArcOfCircle CenterX=-49.19 CenterY=27.25 CenterZ=0 NormalX=0 NormalY=0 NormalZ=1 AngleXU=0 Radius=1.5 StartAngle=1.5708 EndAngle=4.71239
    g8: ArcOfCircle CenterX=-49.19 CenterY=21.5 CenterZ=0 NormalX=0 NormalY=0 NormalZ=1 AngleXU=0 Radius=1.5 StartAngle=1.5708 EndAngle=4.71239
    g9: ArcOfCircle CenterX=-49.19 CenterY=15.75 CenterZ=0 NormalX=0 NormalY=0 NormalZ=1 AngleXU=0 Radius=1.5 StartAngle=1.5708 EndAngle=4.71239
    g10: ArcOfCircle CenterX=-49.19 CenterY=10 CenterZ=0 NormalX=0 NormalY=0 NormalZ=1 AngleXU=0 Radius=1.5 StartAngle=1.5708 EndAngle=4.71239
    g11: ArcOfCircle CenterX=-49.19 CenterY=4.25 CenterZ=0 NormalX=0 NormalY=0 NormalZ=1 AngleXU=0 Radius=1.5 StartAngle=1.5708 EndAngle=4.71239
    g12: LineSegment StartX=-49.19 StartY=69.25 StartZ=0 EndX=-49.19 EndY=66.25 EndZ=0
    g13: LineSegment StartX=-49.19 StartY=63.5 StartZ=0 EndX=-49.19 EndY=60.5 EndZ=0
    g14: LineSegment StartX=-49.19 StartY=57.75 StartZ=0 EndX=-49.19 EndY=54.75 EndZ=0
    g15: LineSegment StartX=-49.19 StartY=52 StartZ=0 EndX=-49.19 EndY=49 EndZ=0
    g16: LineSegment StartX=-49.19 StartY=46.25 StartZ=0 EndX=-49.19 EndY=43.25 EndZ=0
    g17: LineSegment StartX=-49.19 StartY=40.5 StartZ=0 EndX=-49.19 EndY=37.5 EndZ=0
    g18: LineSegment StartX=-49.19 StartY=34.5 StartZ=0 EndX=-49.19 EndY=31.5 EndZ=0
    g19: LineSegment StartX=-49.19 StartY=28.75 StartZ=0 EndX=-49.19 EndY=25.75 EndZ=0
    g20: LineSegment StartX=-49.19 StartY=23 StartZ=0 EndX=-49.19 EndY=20 EndZ=0
    g21: LineSegment StartX=-49.19 StartY=17.25 StartZ=0 EndX=-49.19 EndY=14.25 EndZ=0
    g22: LineSegment StartX=-49.19 StartY=11.5 StartZ=0 EndX=-49.19 EndY=8.5 EndZ=0
    g23: LineSegment StartX=-49.19 StartY=5.75 StartZ=0 EndX=-49.19 EndY=2.75 EndZ=0
  constraints (48):
    c: Block(g0)
    c: Block(g1)
    c: Block(g2)
    c: Block(g3)
    c: Block(g4)
    c: Block(g5)
    c: Block(g6)
    c: Block(g7)
    c: Block(g8)
    c: Block(g9)
    c: Block(g10)
    c: Block(g11)
    c: Coincident(g12,g0)
    c: Coincident(g12,g0)
    c: Vertical(g12)
    c: Vertical(g13)
    c: Coincident(g13,g1)
    c: Vertical(g14)
    c: Coincident(g14,g2)
    c: Vertical(g15)
    c: Coincident(g15,g3)
    c: Vertical(g16)
    c: Coincident(g16,g4)
    c: Vertical(g17)
    c: Coincident(g17,g5)
    c: Vertical(g18)
    c: Coincident(g18,g6)
    c: Vertical(g19)
    c: Coincident(g19,g7)
    c: Vertical(g20)
    c: Coincident(g20,g8)
    c: Vertical(g21)
    c: Coincident(g21,g9)
    c: Vertical(g22)
    c: Coincident(g22,g10)
    c: Vertical(g23)
    c: Coincident(g23,g11)
    c: Block(g23)
    c: Block(g22)
    c: Block(g21)
    c: Block(g20)
    c: Block(g13)
    c: Block(g14)
    c: Block(g15)
    c: Block(g16)
    c: Block(g17)
    c: Block(g18)
    c: Block(g19)
FEATURE [Part::Extrusion] Extrude022
  Base = -> Sketch030
  Dir = (1,-2e-16,2e-16)
  DirMode = 2
  FaceMakerClass = Part::FaceMakerBullseye
  LengthFwd = 19
  LengthRev = 0
  Placement = pos=(-19,0,0) rot=(0,0,1;0rad)
  Solid = true
  Symmetric = false
FEATURE [Part::Fillet] Fillet022
  Base = -> Extrude022
  Edges = 24 edges r=1.49: [Edge6,Edge11,Edge18,Edge23,Edge30,Edge35,Edge42,Edge47,Edge54,Edge59,Edge66,Edge71,Edge78,Edge83,Edge90,Edge95,Edge102,Edge107,Edge114,Edge119,Edge126,Edge131,Edge138,Edge143]
FEATURE [Part::Cut] Cut020  label="top010"
  Base = -> Cut019
  Tool = -> Fillet022
FEATURE [Sketcher::SketchObject] Sketch032
  FullyConstrained = true
  Placement = pos=(117,19,0) rot=(0.57735,0.57735,0.57735;2.0944rad)
  sketch-geometry (48):
    g0: LineSegment StartX=-49.19 StartY=69.25 StartZ=0 EndX=-49.19 EndY=66.25 EndZ=0
    g1: LineSegment StartX=-49.19 StartY=63.5 StartZ=0 EndX=-49.19 EndY=60.5 EndZ=0
    g2: LineSegment StartX=-49.19 StartY=57.75 StartZ=0 EndX=-49.19 EndY=54.75 EndZ=0
    g3: LineSegment StartX=-49.19 StartY=52 StartZ=0 EndX=-49.19 EndY=49 EndZ=0
    g4: LineSegment StartX=-49.19 StartY=46.25 StartZ=0 EndX=-49.19 EndY=43.25 EndZ=0
    g5: LineSegment StartX=-49.19 StartY=40.5 StartZ=0 EndX=-49.19 EndY=37.5 EndZ=0
    g6: LineSegment StartX=-49.19 StartY=34.5 StartZ=0 EndX=-49.19 EndY=31.5 EndZ=0
    g7: LineSegment StartX=-49.19 StartY=28.75 StartZ=0 EndX=-49.19 EndY=25.75 EndZ=0
    g8: LineSegment StartX=-49.19 StartY=23 StartZ=0 EndX=-49.19 EndY=20 EndZ=0
    g9: LineSegment StartX=-49.19 StartY=17.25 StartZ=0 EndX=-49.19 EndY=14.25 EndZ=0
    g10: LineSegment StartX=-49.19 StartY=11.5 StartZ=0 EndX=-49.19 EndY=8.5 EndZ=0
    g11: LineSegment StartX=-49.19 StartY=5.75 StartZ=0 EndX=-49.19 EndY=2.75 EndZ=0
    g12: ArcOfCircle CenterX=-1.5 CenterY=67.75 CenterZ=0 NormalX=0 NormalY=0 NormalZ=1 AngleXU=0 Radius=1.5 StartAngle=4.71239 EndAngle=7.85398
    g13: ArcOfCircle CenterX=-1.5 CenterY=62 CenterZ=0 NormalX=0 NormalY=0 NormalZ=1 AngleXU=0 Radius=1.5 StartAngle=4.71239 EndAngle=7.85398
    g14: ArcOfCircle CenterX=-1.5 CenterY=56.25 CenterZ=0 NormalX=0 NormalY=0 NormalZ=1 AngleXU=0 Radius=1.5 StartAngle=4.71239 EndAngle=7.85398
    g15: ArcOfCircle CenterX=-11.49 CenterY=50.5 CenterZ=0 NormalX=0 NormalY=0 NormalZ=1 AngleXU=0 Radius=1.5 StartAngle=4.71239 EndAngle=7.85398
    g16: ArcOfCircle CenterX=-16.28 CenterY=44.75 CenterZ=0 NormalX=0 NormalY=0 NormalZ=1 AngleXU=0 Radius=1.5 StartAngle=4.71239 EndAngle=7.85398
    g17: ArcOfCircle CenterX=-18.2337 CenterY=39 CenterZ=0 NormalX=0 NormalY=0 NormalZ=1 AngleXU=0 Radius=1.5 StartAngle=4.71485 EndAngle=7.85398
    g18: ArcOfCircle CenterX=-16.2837 CenterY=27.25 CenterZ=0 NormalX=0 NormalY=0 NormalZ=1 AngleXU=0 Radius=1.5 StartAngle=4.71485 EndAngle=7.85398
    g19: ArcOfCircle CenterX=-18.2337 CenterY=33 CenterZ=0 NormalX=0 NormalY=0 NormalZ=1 AngleXU=0 Radius=1.5 StartAngle=4.71485 EndAngle=7.85398
    g20: ArcOfCircle CenterX=-11.49 CenterY=21.5 CenterZ=0 NormalX=0 NormalY=0 NormalZ=1 AngleXU=0 Radius=1.5 StartAngle=4.71239 EndAngle=7.85398
    g21: ArcOfCircle CenterX=-1.5 CenterY=4.25 CenterZ=0 NormalX=0 NormalY=0 NormalZ=1 AngleXU=0 Radius=1.5 StartAngle=4.71239 EndAngle=7.85398
    g22: ArcOfCircle CenterX=-1.5 CenterY=10 CenterZ=0 NormalX=0 NormalY=0 NormalZ=1 AngleXU=0 Radius=1.5 StartAngle=4.71239 EndAngle=7.85398
    g23: ArcOfCircle CenterX=-1.5 CenterY=15.75 CenterZ=0 NormalX=0 NormalY=0 NormalZ=1 AngleXU=0 Radius=1.5 StartAngle=4.71239 EndAngle=7.85398
    g24: LineSegment StartX=-49.19 StartY=69.25 StartZ=0 EndX=-1.5 EndY=69.25 EndZ=0
    g25: LineSegment StartX=-49.19 StartY=66.25 StartZ=0 EndX=-1.5 EndY=66.25 EndZ=0
    g26: LineSegment StartX=-49.19 StartY=63.5 StartZ=0 EndX=-1.5 EndY=63.5 EndZ=0
    g27: LineSegment StartX=-49.19 StartY=60.5 StartZ=0 EndX=-1.5 EndY=60.5 EndZ=0
    g28: LineSegment StartX=-49.19 StartY=57.75 StartZ=0 EndX=-1.5 EndY=57.75 EndZ=0
    g29: LineSegment StartX=-49.19 StartY=54.75 StartZ=0 EndX=-1.5 EndY=54.75 EndZ=0
    g30: LineSegment StartX=-49.19 StartY=52 StartZ=0 EndX=-11.49 EndY=52 EndZ=0
    g31: LineSegment StartX=-49.19 StartY=49 StartZ=0 EndX=-11.49 EndY=49 EndZ=0
    g32: LineSegment StartX=-49.19 StartY=46.25 StartZ=0 EndX=-16.28 EndY=46.25 EndZ=0
    g33: LineSegment StartX=-49.19 StartY=43.25 StartZ=0 EndX=-16.28 EndY=43.25 EndZ=0
    g34: LineSegment StartX=-49.19 StartY=40.5 StartZ=0 EndX=-18.2337 EndY=40.5 EndZ=0
    g35: LineSegment StartX=-49.19 StartY=37.5 StartZ=0 EndX=-18.23 EndY=37.5 EndZ=0
    g36: LineSegment StartX=-49.19 StartY=34.5 StartZ=0 EndX=-18.2337 EndY=34.5 EndZ=0
    g37: LineSegment StartX=-49.19 StartY=31.5 StartZ=0 EndX=-18.23 EndY=31.5 EndZ=0
    g38: LineSegment StartX=-49.19 StartY=28.75 StartZ=0 EndX=-16.2837 EndY=28.75 EndZ=0
    g39: LineSegment StartX=-49.19 StartY=25.75 StartZ=0 EndX=-16.28 EndY=25.75 EndZ=0
    g40: LineSegment StartX=-49.19 StartY=23 StartZ=0 EndX=-11.49 EndY=23 EndZ=0
    g41: LineSegment StartX=-49.19 StartY=20 StartZ=0 EndX=-11.49 EndY=20 EndZ=0
    g42: LineSegment StartX=-49.19 StartY=17.25 StartZ=0 EndX=-1.5 EndY=17.25 EndZ=0
    g43: LineSegment StartX=-49.19 StartY=14.25 StartZ=0 EndX=-1.5 EndY=14.25 EndZ=0
    g44: LineSegment StartX=-49.19 StartY=11.5 StartZ=0 EndX=-1.5 EndY=11.5 EndZ=0
    g45: LineSegment StartX=-49.19 StartY=8.5 StartZ=0 EndX=-1.5 EndY=8.5 EndZ=0
    g46: LineSegment StartX=-49.19 StartY=5.75 StartZ=0 EndX=-1.5 EndY=5.75 EndZ=0
    g47: LineSegment StartX=-49.19 StartY=2.75 StartZ=0 EndX=-1.5 EndY=2.75 EndZ=0
  constraints (120):
    c: Vertical(g0)
    c: Distance(g0) = 3
    c: Block(g0)
    c: Vertical(g1)
    c: Distance(g1) = 3
    c: Vertical(g2)
    c: Equal(g0,g2) = 3
    c: Block(g2)
    c: Vertical(g3)
    c: Equal(g1,g3) = 3
    c: Vertical(g4)
    c: Equal(g0,g4) = 3
    c: Block(g4)
    c: Vertical(g5)
    c: Equal(g1,g5) = 3
    c: Vertical(g6)
    c: Equal(g0,g6) = 3
    c: Block(g6)
    c: Vertical(g7)
    c: Equal(g1,g7) = 3
    c: Vertical(g8)
    c: Equal(g0,g8) = 3
    c: Block(g8)
    c: Vertical(g9)
    c: Equal(g1,g9) = 3
    c: Vertical(g10)
    c: Equal(g0,g10) = 3
    c: Block(g10)
    c: Vertical(g11)
    c: Equal(g1,g11) = 3
    c: Block(g12)
    c: Block(g13)
    c: Block(g14)
    c: Block(g15)
    c: Block(g16)
    c: Block(g17)
    c: Block(g18)
    c: Block(g19)
    c: Block(g20)
    c: Block(g21)
    c: Block(g22)
    c: Block(g23)
    c: Block(g11)
    c: Block(g9)
    c: Block(g7)
    c: Block(g5)
    c: Block(g3)
    c: Block(g1)
    c: Coincident(g24,g0)
    c: Coincident(g24,g12)
    c: Horizontal(g24)
    c: Coincident(g25,g0)
    c: Coincident(g25,g12)
    c: Horizontal(g25)
    c: Coincident(g26,g1)
    c: Coincident(g26,g13)
    c: Horizontal(g26)
    c: Coincident(g27,g1)
    c: Coincident(g27,g13)
    c: Horizontal(g27)
    c: Coincident(g28,g2)
    c: Coincident(g28,g14)
    c: Horizontal(g28)
    c: Coincident(g29,g2)
    c: Coincident(g29,g14)
    c: Horizontal(g29)
    c: Coincident(g30,g3)
    c: Coincident(g30,g15)
    c: Horizontal(g30)
    c: Coincident(g31,g3)
    c: Coincident(g31,g15)
    c: Horizontal(g31)
    c: Coincident(g32,g4)
    c: Coincident(g32,g16)
    c: Horizontal(g32)
    c: Coincident(g33,g4)
    c: Coincident(g33,g16)
    c: Horizontal(g33)
    c: Coincident(g34,g5)
    c: Coincident(g34,g17)
    c: Horizontal(g34)
    c: Coincident(g35,g5)
    c: Coincident(g35,g17)
    c: Horizontal(g35)
    c: Coincident(g36,g6)
    c: Coincident(g36,g19)
    c: Horizontal(g36)
    c: Coincident(g37,g6)
    c: Coincident(g37,g19)
    c: Horizontal(g37)
    c: Coincident(g38,g7)
    c: Coincident(g38,g18)
    c: Horizontal(g38)
    c: Coincident(g39,g7)
    c: Coincident(g39,g18)
    c: Horizontal(g39)
    c: Coincident(g40,g8)
    c: Coincident(g40,g20)
    c: Horizontal(g40)
    c: Coincident(g41,g8)
    c: Coincident(g41,g20)
    c: Horizontal(g41)
    c: Coincident(g42,g9)
    c: Coincident(g42,g23)
    c: Horizontal(g42)
    c: Coincident(g43,g9)
    c: Coincident(g43,g23)
    c: Horizontal(g43)
    c: Coincident(g44,g10)
    c: Coincident(g44,g22)
    c: Horizontal(g44)
    c: Coincident(g45,g10)
    c: Coincident(g45,g22)
    c: Horizontal(g45)
    c: Coincident(g46,g11)
    c: Coincident(g46,g21)
    c: Horizontal(g46)
    c: Coincident(g47,g11)
    c: Coincident(g47,g21)
    c: Horizontal(g47)
FEATURE [Part::Extrusion] Extrude023
  Base = -> Sketch032
  Dir = (1,-2e-16,2e-16)
  DirMode = 2
  FaceMakerClass = Part::FaceMakerBullseye
  LengthFwd = 19
  LengthRev = 0
  Placement = pos=(-19,0,0) rot=(0,0,1;0rad)
  Solid = true
  Symmetric = false
FEATURE [Part::Fillet] Fillet023
  Base = -> Extrude023
  Edges = <same value as first occurrence — deduplicated (x6 in doc)>
  Placement = pos=(0,0.05,0) rot=(0,0,1;0rad)
FEATURE [Part::Cut] Cut014  label="bottom003"
  Base = -> Cut007
  Tool = -> Fusion047
FEATURE [Part::Cut] Cut021  label="bottom004"
  Base = -> Cut014
  Tool = -> Fillet023
FEATURE [Sketcher::SketchObject] Sketch033
  FullyConstrained = true
  Placement = pos=(117,19,0) rot=(0.57735,0.57735,0.57735;2.0944rad)
  sketch-geometry (8):
    g0: LineSegment StartX=-49.19 StartY=69.25 StartZ=0 EndX=-49.19 EndY=66.25 EndZ=0
    g1: LineSegment StartX=-49.19 StartY=5.75 StartZ=0 EndX=-49.19 EndY=2.75 EndZ=0
    g2: ArcOfCircle CenterX=-1.5 CenterY=67.75 CenterZ=0 NormalX=0 NormalY=0 NormalZ=1 AngleXU=0 Radius=1.5 StartAngle=4.71239 EndAngle=7.85398
    g3: ArcOfCircle CenterX=-1.5 CenterY=4.25 CenterZ=0 NormalX=0 NormalY=0 NormalZ=1 AngleXU=0 Radius=1.5 StartAngle=4.71239 EndAngle=7.85398
    g4: LineSegment StartX=-49.19 StartY=69.25 StartZ=0 EndX=-1.5 EndY=69.25 EndZ=0
    g5: LineSegment StartX=-49.19 StartY=66.25 StartZ=0 EndX=-1.5 EndY=66.25 EndZ=0
    g6: LineSegment StartX=-49.19 StartY=5.75 StartZ=0 EndX=-1.5 EndY=5.75 EndZ=0
    g7: LineSegment StartX=-49.19 StartY=2.75 StartZ=0 EndX=-1.5 EndY=2.75 EndZ=0
  constraints (19):
    c: Vertical(g0)
    c: Distance(g0) = 3
    c: Block(g0)
    c: Vertical(g1)
    c: Block(g2)
    c: Block(g3)
    c: Block(g1)
    c: Coincident(g4,g0)
    c: Coincident(g4,g2)
    c: Horizontal(g4)
    c: Coincident(g5,g0)
    c: Coincident(g5,g2)
    c: Horizontal(g5)
    c: Coincident(g6,g1)
    c: Coincident(g6,g3)
    c: Horizontal(g6)
    c: Coincident(g7,g1)
    c: Coincident(g7,g3)
    c: Horizontal(g7)
FEATURE [Sketcher::SketchObject] Sketch034
  FullyConstrained = true
  Placement = pos=(117,19,0) rot=(0.57735,0.57735,0.57735;2.0944rad)
  sketch-geometry (8):
    g0: LineSegment StartX=-49.19 StartY=63.5 StartZ=0 EndX=-49.19 EndY=60.5 EndZ=0
    g1: LineSegment StartX=-49.19 StartY=11.5 StartZ=0 EndX=-49.19 EndY=8.5 EndZ=0
    g2: ArcOfCircle CenterX=-1.5 CenterY=62 CenterZ=0 NormalX=0 NormalY=0 NormalZ=1 AngleXU=0 Radius=1.5 StartAngle=4.71239 EndAngle=7.85398
    g3: ArcOfCircle CenterX=-1.5 CenterY=10 CenterZ=0 NormalX=0 NormalY=0 NormalZ=1 AngleXU=0 Radius=1.5 StartAngle=4.71239 EndAngle=7.85398
    g4: LineSegment StartX=-49.19 StartY=63.5 StartZ=0 EndX=-1.5 EndY=63.5 EndZ=0
    g5: LineSegment StartX=-49.19 StartY=60.5 StartZ=0 EndX=-1.5 EndY=60.5 EndZ=0
    g6: LineSegment StartX=-49.19 StartY=11.5 StartZ=0 EndX=-1.5 EndY=11.5 EndZ=0
    g7: LineSegment StartX=-49.19 StartY=8.5 StartZ=0 EndX=-1.5 EndY=8.5 EndZ=0
  constraints (19):
    c: Vertical(g0)
    c: Distance(g0) = 3
    c: Vertical(g1)
    c: Block(g1)
    c: Block(g2)
    c: Block(g3)
    c: Block(g0)
    c: Coincident(g4,g0)
    c: Coincident(g4,g2)
    c: Horizontal(g4)
    c: Coincident(g5,g0)
    c: Coincident(g5,g2)
    c: Horizontal(g5)
    c: Coincident(g6,g1)
    c: Coincident(g6,g3)
    c: Horizontal(g6)
    c: Coincident(g7,g1)
    c: Coincident(g7,g3)
    c: Horizontal(g7)
FEATURE [Part::Extrusion] Extrude024
  Base = -> Sketch033
  Dir = (1,0,0)
  DirMode = 2
  FaceMakerClass = Part::FaceMakerBullseye
  LengthFwd = 10
  LengthRev = 0
  Solid = true
  Symmetric = false
FEATURE [Part::Extrusion] Extrude025
  Base = -> Sketch034
  Dir = (1,0,0)
  DirMode = 2
  FaceMakerClass = Part::FaceMakerBullseye
  LengthFwd = 10
  LengthRev = 0
  Solid = true
  Symmetric = false
FEATURE [Part::Fillet] Fillet024  label="removeFromtMoreFrontCaseScrewRetainers"
  Base = -> Extrude024
  Edges = 4 edges r=1.49: [Edge6,Edge11,Edge18,Edge23]
  Placement = pos=(-11,0,0) rot=(0,0,1;0rad)
FEATURE [Part::Fillet] Fillet025  label="removeFromtMoreFrontCaseScrewRetainers001"
  Base = -> Extrude025
  Edges = 4 edges r=1.49: [Edge6,Edge11,Edge18,Edge23]
  Placement = pos=(-19,0,0) rot=(0,0,1;0rad)
FEATURE [Part::Cut] Cut022
  Base = -> Cut015
  Tool = -> Fillet025
FEATURE [Part::Cut] Cut023  label="screwRetainers"
  Base = -> Cut022
  Tool = -> Fillet024
FEATURE [Part::MultiFuse] Fusion056  label="bottom005"
  Shapes = -> [Fusion044,Cut021]
FEATURE [Part::MultiFuse] Fusion057  label="casePillars001"
  Shapes = -> [Cut016,Fusion052]
FEATURE [Part::MultiFuse] Fusion058  label="bottom006"
  Shapes = -> [Fusion056,Cut023]
FEATURE [Part::MultiFuse] Fusion059  label="bottom007"
  Shapes = -> [Fusion058,Fillet005]
FEATURE [Part::MultiFuse] Fusion060  label="bottom008"
  Shapes = -> [Fusion059,Fusion]
FEATURE [Part::MultiFuse] Fusion061  label="top011"
  Shapes = -> [Cut006,Cut020]
FEATURE [Part::MultiFuse] Fusion062  label="top012"
  Shapes = -> [Fusion057,Fusion061]
FEATURE [Sketcher::SketchObject] Sketch035  label="topSketch007"
  FullyConstrained = true
  sketch-geometry (6):
    g0: LineSegment StartX=19 StartY=38 StartZ=0 EndX=117 EndY=38 EndZ=0
    g1: ArcOfCircle CenterX=19 CenterY=19 CenterZ=0 NormalX=0 NormalY=0 NormalZ=1 AngleXU=0 Radius=19 StartAngle=1.5708 EndAngle=3.14159
    g2: LineSegment StartX=117 StartY=38 StartZ=0 EndX=117 EndY=19 EndZ=0
    g3: LineSegment StartX=98 StartY=1.0161e-12 StartZ=0 EndX=5.22862e-06 EndY=1.0161e-12 EndZ=0
    g4: LineSegment StartX=5.22862e-06 StartY=19 StartZ=0 EndX=5.22862e-06 EndY=1.0161e-12 EndZ=0
    g5: ArcOfCircle CenterX=98 CenterY=19 CenterZ=0 NormalX=0 NormalY=0 NormalZ=1 AngleXU=0 Radius=19 StartAngle=4.71239 EndAngle=6.28319
  constraints (16):
    c: Horizontal(g0)
    c: Distance(g0) = 98
    c: Coincident(g1,g0)
    c: Block(g1)
    c: Coincident(g2,g0)
    c: Vertical(g2)
    c: Distance(g2) = 19
    c: Horizontal(g3)
    c: Coincident(g4,g1)
    c: Vertical(g4)
    c: Coincident(g3,g4)
    c: Block(g3)
    c: Coincident(g5,g2)
    c: Coincident(g5,g3)
    c: Block(g0)
    c: Block(g5)
FEATURE [Part::Extrusion] Extrude026  label="sideA001"
  Base = -> Sketch035
  Dir = (0,0,1)
  DirMode = 2
  FaceMakerClass = Part::FaceMakerBullseye
  LengthFwd = 3
  LengthRev = 0
  Placement = pos=(0,0,-2.7) rot=(0,0,1;0rad)
  Solid = true
  Symmetric = false
FEATURE [Sketcher::SketchObject] Sketch036  label="topSketch008"
  FullyConstrained = true
  sketch-geometry (6):
    g0: LineSegment StartX=19 StartY=38 StartZ=0 EndX=117 EndY=38 EndZ=0
    g1: ArcOfCircle CenterX=19 CenterY=19 CenterZ=0 NormalX=0 NormalY=0 NormalZ=1 AngleXU=0 Radius=19 StartAngle=1.5708 EndAngle=3.14159
    g2: LineSegment StartX=117 StartY=38 StartZ=0 EndX=117 EndY=19 EndZ=0
    g3: LineSegment StartX=98 StartY=1.0161e-12 StartZ=0 EndX=5.22862e-06 EndY=1.0161e-12 EndZ=0
    g4: LineSegment StartX=5.22862e-06 StartY=19 StartZ=0 EndX=5.22862e-06 EndY=1.0161e-12 EndZ=0
    g5: ArcOfCircle CenterX=98 CenterY=19 CenterZ=0 NormalX=0 NormalY=0 NormalZ=1 AngleXU=0 Radius=19 StartAngle=4.71239 EndAngle=6.28319
  constraints (16):
    c: Horizontal(g0)
    c: Distance(g0) = 98
    c: Coincident(g1,g0)
    c: Block(g1)
    c: Coincident(g2,g0)
    c: Vertical(g2)
    c: Distance(g2) = 19
    c: Horizontal(g3)
    c: Coincident(g4,g1)
    c: Vertical(g4)
    c: Coincident(g3,g4)
    c: Block(g3)
    c: Coincident(g5,g2)
    c: Coincident(g5,g3)
    c: Block(g0)
    c: Block(g5)
FEATURE [Part::Extrusion] Extrude027  label="sideB001"
  Base = -> Sketch036
  Dir = (0,0,1)
  DirMode = 2
  FaceMakerClass = Part::FaceMakerBullseye
  LengthFwd = 3
  LengthRev = 0
  Placement = pos=(0,0,71.7) rot=(0,0,1;0rad)
  Solid = true
  Symmetric = false
FEATURE [Part::MultiFuse] Fusion064  label="removeFromBottom"
  Shapes = -> [Extrude026,Extrude027]
FEATURE [Part::Cut] Cut024  label="bottom009"
  Base = -> Fusion060
  Tool = -> Fusion064
FEATURE [Sketcher::SketchObject] Sketch037  label="topSketch009"
  FullyConstrained = true
  sketch-geometry (8):
    g0: ArcOfCircle CenterX=19 CenterY=19.1201 CenterZ=0 NormalX=0 NormalY=0 NormalZ=1 AngleXU=0 Radius=18.8799 StartAngle=1.5708 EndAngle=3.14793
    g1: LineSegment StartX=0.120501 StartY=19.0004 StartZ=0 EndX=0.120501 EndY=0.000382114 EndZ=0
    g2: LineSegment StartX=19 StartY=38 StartZ=0 EndX=124 EndY=38 EndZ=0
    g3: LineSegment StartX=0.120501 StartY=0.000382114 StartZ=0 EndX=105.121 EndY=0.000382114 EndZ=0
    g4: LineSegment StartX=124 StartY=38 StartZ=0 EndX=125.616 EndY=38 EndZ=0
    g5: LineSegment StartX=105.121 StartY=0.000382114 StartZ=0 EndX=106.736 EndY=0.000382114 EndZ=0
    g6: ArcOfCircle CenterX=106.616 CenterY=19 CenterZ=0 NormalX=0 NormalY=0 NormalZ=1 AngleXU=0 Radius=19 StartAngle=4.71873 EndAngle=6.28319
    g7: LineSegment StartX=125.616 StartY=38 StartZ=0 EndX=125.616 EndY=19 EndZ=0
  constraints (21):
    c: Block(g0)
    c: Coincident(g1,g0)
    c: Vertical(g1)
    c: Horizontal(g2)
    c: Distance(g2) = 105
    c: Coincident(g2,g0)
    c: Distance(g1) = 19
    c: Coincident(g3,g1)
    c: Horizontal(g3)
    c: Distance(g3) = 105
    c: Coincident(g4,g2)
    c: Horizontal(g4)
    c: Distance(g4) = 1.61553
    c: Horizontal(g5)
    c: Equal(g4,g5) = 1.61553
    c: Coincident(g5,g3)
    c: Block(g6)
    c: Coincident(g6,g5)
    c: Coincident(g7,g4)
    c: Coincident(g7,g6)
    c: Vertical(g7)
FEATURE [Part::Extrusion] Extrude028  label="sideB"
  Base = -> Sketch037
  Dir = (0,0,1)
  DirMode = 2
  FaceMakerClass = Part::FaceMakerBullseye
  LengthFwd = 3
  LengthRev = 0
  Placement = pos=(0,0,72) rot=(0,0,1;0rad)
  Solid = true
  Symmetric = false
FEATURE [Sketcher::SketchObject] Sketch038  label="topSketch010"
  FullyConstrained = true
  sketch-geometry (22):
    g0: LineSegment StartX=5.21097e-06 StartY=3 StartZ=0 EndX=5.21097e-06 EndY=19 EndZ=0
    g1: ArcOfCircle CenterX=19 CenterY=19 CenterZ=0 NormalX=0 NormalY=0 NormalZ=1 AngleXU=0 Radius=19 StartAngle=1.5708 EndAngle=3.14159
    g2: ArcOfCircle CenterX=19 CenterY=19 CenterZ=0 NormalX=0 NormalY=0 NormalZ=1 AngleXU=0 Radius=16 StartAngle=1.5708 EndAngle=3.14159
    g3: LineSegment StartX=114 StartY=35 StartZ=0 EndX=19 EndY=35 EndZ=0
    g4: LineSegment StartX=5.21097e-06 StartY=3 StartZ=0 EndX=5.21097e-06 EndY=0 EndZ=0
    g5: LineSegment StartX=3 StartY=0 StartZ=0 EndX=5.21097e-06 EndY=0 EndZ=0
    g6: LineSegment StartX=3 StartY=19 StartZ=0 EndX=3 EndY=0 EndZ=0
    g7: LineSegment StartX=19 StartY=38 StartZ=0 EndX=124 EndY=38 EndZ=0
    g8: Circle CenterX=119 CenterY=35 CenterZ=0 NormalX=0 NormalY=0 NormalZ=1 AngleXU=0 Radius=1
    g9: Circle CenterX=121 CenterY=35 CenterZ=0 NormalX=0 NormalY=0 NormalZ=1 AngleXU=0 Radius=1
    g10: Circle CenterX=121 CenterY=33 CenterZ=0 NormalX=0 NormalY=0 NormalZ=1 AngleXU=0 Radius=1
    g11: BSplineCurve PolesCount=3 KnotsCount=2 Degree=2 IsPeriodic=0
    g12: GeomPoint X=119 Y=35 Z=0
    g13: GeomPoint X=121 Y=33 Z=0
    g14: LineSegment StartX=119 StartY=35 StartZ=0 EndX=114 EndY=35 EndZ=0
    g15: ArcOfCircle CenterX=105 CenterY=19 CenterZ=0 NormalX=0 NormalY=0 NormalZ=1 AngleXU=0 Radius=16 StartAngle=5.60905 EndAngle=6.28319
    g16: LineSegment StartX=121 StartY=33 StartZ=0 EndX=121 EndY=19 EndZ=0
    g17: LineSegment StartX=117.5 StartY=9.01251 StartZ=0 EndX=121.163 EndY=9.0125 EndZ=0
    g18: ArcOfCircle CenterX=105 CenterY=19 CenterZ=0 NormalX=0 NormalY=0 NormalZ=1 AngleXU=0 Radius=20.6155 StartAngle=5.7297 EndAngle=6.28319
    g19: LineSegment StartX=121.163 StartY=9.0125 StartZ=0 EndX=122.538 EndY=8.16329 EndZ=0
    g20: LineSegment StartX=124 StartY=38 StartZ=0 EndX=125.616 EndY=38 EndZ=0
    g21: LineSegment StartX=125.616 StartY=19 StartZ=0 EndX=125.616 EndY=38 EndZ=0
  constraints (49):
    c: Vertical(g0)
    c: Block(g0)
    c: Coincident(g1,g0)
    c: Block(g1)
    c: Coincident(g2,g1)
    c: Block(g2)
    c: Coincident(g3,g2)
    c: Horizontal(g3)
    c: Tangent(g3,g2)
    c: Coincident(g4,g0)
    c: Distance(g4) = 3
    c: Vertical(g4)
    c: Coincident(g5,g4)
    c: Horizontal(g5)
    c: Coincident(g6,g2)
    c: Coincident(g6,g5)
    c: Vertical(g6)
    c: Horizontal(g7)
    c: Distance(g7) = 105
    c: Coincident(g7,g1)
    c: Block(g3)
    c: Weight(g8) = 1
    c: Equal(g8,g9)
    c: Equal(g8,g10)
    c: InternalAlignment(g8,g11)
    c: InternalAlignment(g9,g11)
    c: InternalAlignment(g10,g11)
    c: InternalAlignment(g12,g11)
    c: InternalAlignment(g13,g11)
    c: Block(g11)
    c: Coincident(g14,g11)
    c: Coincident(g14,g3)
    c: Horizontal(g14)
    c: Block(g15)
    c: Coincident(g16,g11)
    c: Coincident(g16,g15)
    c: Vertical(g16)
    c: Distance(g16) = 14
    c: Coincident(g17,g15)
    c: Block(g18)
    c: Coincident(g19,g18)
    c: Coincident(g20,g7)
    c: Horizontal(g20)
    c: Vertical(g21)
    c: Coincident(g20,g21)
    c: Block(g20)
    c: Block(g21)
    c: Block(g19)
    c: Block(g17)
FEATURE [Part::Extrusion] Extrude029
  Base = -> Sketch038
  Dir = (0,0,1)
  DirMode = 2
  FaceMakerClass = Part::FaceMakerBullseye
  LengthFwd = 72
  LengthRev = 0
  Solid = true
  Symmetric = false
FEATURE [Part::Feature] Face085
  shape: bbox 4.8 x 25.5 x 2e-07 mm, 1 faces, 0 solids (baked)
FEATURE [Part::Revolution] Revolve089  label="moreFrontCaseScrewPost003"
  Angle = 360
  Axis = (0,1,0)
  Base = (0,0,0)
  FaceMakerClass = Part::FaceMakerBullseye
  Placement = pos=(109.5,4.5,3.5) rot=(0,0,1;0rad)
  Solid = false
  Source = -> Face085
  Symmetric = false
FEATURE [Part::Feature] Face086
  shape: bbox 4.8 x 25.5 x 2e-07 mm, 1 faces, 0 solids (baked)
FEATURE [Part::Revolution] Revolve090  label="moreFrontCaseScrewPost004"
  Angle = 360
  Axis = (0,1,0)
  Base = (0,0,0)
  FaceMakerClass = Part::FaceMakerBullseye
  Placement = pos=(109.5,4.5,68.5) rot=(0,0,1;0rad)
  Solid = false
  Source = -> Face086
  Symmetric = false
FEATURE [Part::Fillet] Fillet026  label="top013"
  Base = -> Extrude029
  Edges = 1 edges r=2: [Edge35]
FEATURE [Sketcher::SketchObject] Sketch039
  FullyConstrained = true
  sketch-geometry (7):
    g0: LineSegment StartX=0 StartY=0 StartZ=0 EndX=0 EndY=6 EndZ=0
    g1: Circle CenterX=0 CenterY=0 CenterZ=0 NormalX=0 NormalY=0 NormalZ=1 AngleXU=0 Radius=1
    g2: Circle CenterX=8 CenterY=6 CenterZ=0 NormalX=0 NormalY=0 NormalZ=1 AngleXU=0 Radius=1
    g3: BSplineCurve PolesCount=3 KnotsCount=2 Degree=2 IsPeriodic=0
    g4: GeomPoint X=0 Y=0 Z=0
    g5: GeomPoint X=8 Y=6 Z=0
    g6: LineSegment StartX=0 StartY=6 StartZ=0 EndX=8 EndY=6 EndZ=0
  constraints (14):
    c: Coincident(g0,g-1)
    c: Distance(g0) = 6
    c: Vertical(g0)
    c: Coincident(g3,g0)
    c: Weight(g1) = 1
    c: Equal(g1,g2)
    c: InternalAlignment(g1,g3)
    c: InternalAlignment(g2,g3)
    c: InternalAlignment(g4,g3)
    c: InternalAlignment(g5,g3)
    c: Block(g3)
    c: Coincident(g6,g0)
    c: Coincident(g6,g3)
    c: Horizontal(g6)
FEATURE [Sketcher::SketchObject] Sketch040
  FullyConstrained = true
  sketch-geometry (7):
    g0: LineSegment StartX=0 StartY=0 StartZ=0 EndX=0 EndY=6 EndZ=0
    g1: Circle CenterX=0 CenterY=0 CenterZ=0 NormalX=0 NormalY=0 NormalZ=1 AngleXU=0 Radius=1
    g2: Circle CenterX=8 CenterY=6 CenterZ=0 NormalX=0 NormalY=0 NormalZ=1 AngleXU=0 Radius=1
    g3: BSplineCurve PolesCount=3 KnotsCount=2 Degree=2 IsPeriodic=0
    g4: GeomPoint X=0 Y=0 Z=0
    g5: GeomPoint X=8 Y=6 Z=0
    g6: LineSegment StartX=0 StartY=6 StartZ=0 EndX=8 EndY=6 EndZ=0
  constraints (14):
    c: Coincident(g0,g-1)
    c: Distance(g0) = 6
    c: Vertical(g0)
    c: Coincident(g3,g0)
    c: Weight(g1) = 1
    c: Equal(g1,g2)
    c: InternalAlignment(g1,g3)
    c: InternalAlignment(g2,g3)
    c: InternalAlignment(g4,g3)
    c: InternalAlignment(g5,g3)
    c: Block(g3)
    c: Coincident(g6,g0)
    c: Coincident(g6,g3)
    c: Horizontal(g6)
FEATURE [Sketcher::SketchObject] Sketch041
  FullyConstrained = true
  sketch-geometry (7):
    g0: LineSegment StartX=0 StartY=0 StartZ=0 EndX=0 EndY=6 EndZ=0
    g1: Circle CenterX=0 CenterY=0 CenterZ=0 NormalX=0 NormalY=0 NormalZ=1 AngleXU=0 Radius=1
    g2: Circle CenterX=8 CenterY=6 CenterZ=0 NormalX=0 NormalY=0 NormalZ=1 AngleXU=0 Radius=1
    g3: BSplineCurve PolesCount=3 KnotsCount=2 Degree=2 IsPeriodic=0
    g4: GeomPoint X=0 Y=0 Z=0
    g5: GeomPoint X=8 Y=6 Z=0
    g6: LineSegment StartX=0 StartY=6 StartZ=0 EndX=8 EndY=6 EndZ=0
  constraints (14):
    c: Coincident(g0,g-1)
    c: Distance(g0) = 6
    c: Vertical(g0)
    c: Coincident(g3,g0)
    c: Weight(g1) = 1
    c: Equal(g1,g2)
    c: InternalAlignment(g1,g3)
    c: InternalAlignment(g2,g3)
    c: InternalAlignment(g4,g3)
    c: InternalAlignment(g5,g3)
    c: Block(g3)
    c: Coincident(g6,g0)
    c: Coincident(g6,g3)
    c: Horizontal(g6)
FEATURE [Sketcher::SketchObject] Sketch042
  FullyConstrained = true
  sketch-geometry (7):
    g0: LineSegment StartX=0 StartY=0 StartZ=0 EndX=0 EndY=6 EndZ=0
    g1: Circle CenterX=0 CenterY=0 CenterZ=0 NormalX=0 NormalY=0 NormalZ=1 AngleXU=0 Radius=1
    g2: Circle CenterX=8 CenterY=6 CenterZ=0 NormalX=0 NormalY=0 NormalZ=1 AngleXU=0 Radius=1
    g3: BSplineCurve PolesCount=3 KnotsCount=2 Degree=2 IsPeriodic=0
    g4: GeomPoint X=0 Y=0 Z=0
    g5: GeomPoint X=8 Y=6 Z=0
    g6: LineSegment StartX=0 StartY=6 StartZ=0 EndX=8 EndY=6 EndZ=0
  constraints (14):
    c: Coincident(g0,g-1)
    c: Distance(g0) = 6
    c: Vertical(g0)
    c: Coincident(g3,g0)
    c: Weight(g1) = 1
    c: Equal(g1,g2)
    c: InternalAlignment(g1,g3)
    c: InternalAlignment(g2,g3)
    c: InternalAlignment(g4,g3)
    c: InternalAlignment(g5,g3)
    c: Block(g3)
    c: Coincident(g6,g0)
    c: Coincident(g6,g3)
    c: Horizontal(g6)
FEATURE [Part::Extrusion] Extrude030  label="caseScrewPillarBracket008"
  Base = -> Sketch039
  Dir = (0,0,1)
  DirMode = 2
  FaceMakerClass = Part::FaceMakerBullseye
  LengthFwd = 2.4
  LengthRev = 0
  Placement = pos=(15.76,29,8.8) rot=(0,1,0;0rad)
  Solid = true
  Symmetric = false
FEATURE [Part::Extrusion] Extrude031  label="caseScrewPillarBracket009"
  Base = -> Sketch040
  Dir = (0,0,1)
  DirMode = 2
  FaceMakerClass = Part::FaceMakerBullseye
  LengthFwd = 2.4
  LengthRev = 0
  Placement = pos=(15.76,29,60.8) rot=(0,0,1;0rad)
  Solid = true
  Symmetric = false
FEATURE [Part::Extrusion] Extrude032  label="caseScrewPillarBracket010"
  Base = -> Sketch041
  Dir = (0,0,1)
  DirMode = 2
  FaceMakerClass = Part::FaceMakerBullseye
  LengthFwd = 2.4
  LengthRev = 0
  Placement = pos=(13.7,29,13.26) rot=(0,-1,0;1.5708rad)
  Solid = true
  Symmetric = false
FEATURE [Part::Extrusion] Extrude033  label="caseScrewPillarBracket011"
  Base = -> Sketch042
  Dir = (0,0,1)
  DirMode = 2
  FaceMakerClass = Part::FaceMakerBullseye
  LengthFwd = 2.4
  LengthRev = 0
  Placement = pos=(11.3,29,58.74) rot=(0,1,0;1.5708rad)
  Solid = true
  Symmetric = false
FEATURE [Sketcher::SketchObject] Sketch043
  FullyConstrained = true
  sketch-geometry (7):
    g0: LineSegment StartX=0 StartY=0 StartZ=0 EndX=0 EndY=6 EndZ=0
    g1: Circle CenterX=0 CenterY=0 CenterZ=0 NormalX=0 NormalY=0 NormalZ=1 AngleXU=0 Radius=1
    g2: Circle CenterX=8 CenterY=6 CenterZ=0 NormalX=0 NormalY=0 NormalZ=1 AngleXU=0 Radius=1
    g3: BSplineCurve PolesCount=3 KnotsCount=2 Degree=2 IsPeriodic=0
    g4: GeomPoint X=0 Y=0 Z=0
    g5: GeomPoint X=8 Y=6 Z=0
    g6: LineSegment StartX=0 StartY=6 StartZ=0 EndX=8 EndY=6 EndZ=0
  constraints (14):
    c: Coincident(g0,g-1)
    c: Distance(g0) = 6
    c: Vertical(g0)
    c: Coincident(g3,g0)
    c: Weight(g1) = 1
    c: Equal(g1,g2)
    c: InternalAlignment(g1,g3)
    c: InternalAlignment(g2,g3)
    c: InternalAlignment(g4,g3)
    c: InternalAlignment(g5,g3)
    c: Block(g3)
    c: Coincident(g6,g0)
    c: Coincident(g6,g3)
    c: Horizontal(g6)
FEATURE [Part::Extrusion] Extrude034  label="caseScrewPillarBracket012"
  Base = -> Sketch043
  Dir = (0,0,1)
  DirMode = 2
  FaceMakerClass = Part::FaceMakerBullseye
  LengthFwd = 2.4
  LengthRev = 0
  Placement = pos=(88.3,29,65.23) rot=(0,1,0;1.5708rad)
  Solid = true
  Symmetric = false
FEATURE [Sketcher::SketchObject] Sketch044
  FullyConstrained = true
  sketch-geometry (7):
    g0: LineSegment StartX=0 StartY=0 StartZ=0 EndX=0 EndY=6 EndZ=0
    g1: Circle CenterX=0 CenterY=0 CenterZ=0 NormalX=0 NormalY=0 NormalZ=1 AngleXU=0 Radius=1
    g2: Circle CenterX=8 CenterY=6 CenterZ=0 NormalX=0 NormalY=0 NormalZ=1 AngleXU=0 Radius=1
    g3: BSplineCurve PolesCount=3 KnotsCount=2 Degree=2 IsPeriodic=0
    g4: GeomPoint X=0 Y=0 Z=0
    g5: GeomPoint X=8 Y=6 Z=0
    g6: LineSegment StartX=0 StartY=6 StartZ=0 EndX=8 EndY=6 EndZ=0
  constraints (14):
    c: Coincident(g0,g-1)
    c: Distance(g0) = 6
    c: Vertical(g0)
    c: Coincident(g3,g0)
    c: Weight(g1) = 1
    c: Equal(g1,g2)
    c: InternalAlignment(g1,g3)
    c: InternalAlignment(g2,g3)
    c: InternalAlignment(g4,g3)
    c: InternalAlignment(g5,g3)
    c: Block(g3)
    c: Coincident(g6,g0)
    c: Coincident(g6,g3)
    c: Horizontal(g6)
FEATURE [Part::Extrusion] Extrude035  label="caseScrewPillarBracket013"
  Base = -> Sketch044
  Dir = (0,0,1)
  DirMode = 2
  FaceMakerClass = Part::FaceMakerBullseye
  LengthFwd = 2.4
  LengthRev = 0
  Placement = pos=(90.7,29,6.77) rot=(0,-1,0;1.5708rad)
  Solid = true
  Symmetric = false
FEATURE [Sketcher::SketchObject] Sketch045
  FullyConstrained = true
  sketch-geometry (7):
    g0: LineSegment StartX=0 StartY=0 StartZ=0 EndX=0 EndY=6 EndZ=0
    g1: Circle CenterX=0 CenterY=0 CenterZ=0 NormalX=0 NormalY=0 NormalZ=1 AngleXU=0 Radius=1
    g2: Circle CenterX=8 CenterY=6 CenterZ=0 NormalX=0 NormalY=0 NormalZ=1 AngleXU=0 Radius=1
    g3: BSplineCurve PolesCount=3 KnotsCount=2 Degree=2 IsPeriodic=0
    g4: GeomPoint X=0 Y=0 Z=0
    g5: GeomPoint X=8 Y=6 Z=0
    g6: LineSegment StartX=0 StartY=6 StartZ=0 EndX=8 EndY=6 EndZ=0
  constraints (14):
    c: Coincident(g0,g-1)
    c: Distance(g0) = 6
    c: Vertical(g0)
    c: Coincident(g3,g0)
    c: Weight(g1) = 1
    c: Equal(g1,g2)
    c: InternalAlignment(g1,g3)
    c: InternalAlignment(g2,g3)
    c: InternalAlignment(g4,g3)
    c: InternalAlignment(g5,g3)
    c: Block(g3)
    c: Coincident(g6,g0)
    c: Coincident(g6,g3)
    c: Horizontal(g6)
FEATURE [Sketcher::SketchObject] Sketch046
  FullyConstrained = true
  sketch-geometry (7):
    g0: LineSegment StartX=0 StartY=0 StartZ=0 EndX=0 EndY=6 EndZ=0
    g1: Circle CenterX=0 CenterY=0 CenterZ=0 NormalX=0 NormalY=0 NormalZ=1 AngleXU=0 Radius=1
    g2: Circle CenterX=8 CenterY=6 CenterZ=0 NormalX=0 NormalY=0 NormalZ=1 AngleXU=0 Radius=1
    g3: BSplineCurve PolesCount=3 KnotsCount=2 Degree=2 IsPeriodic=0
    g4: GeomPoint X=0 Y=0 Z=0
    g5: GeomPoint X=8 Y=6 Z=0
    g6: LineSegment StartX=0 StartY=6 StartZ=0 EndX=8 EndY=6 EndZ=0
  constraints (14):
    c: Coincident(g0,g-1)
    c: Distance(g0) = 6
    c: Vertical(g0)
    c: Coincident(g3,g0)
    c: Weight(g1) = 1
    c: Equal(g1,g2)
    c: InternalAlignment(g1,g3)
    c: InternalAlignment(g2,g3)
    c: InternalAlignment(g4,g3)
    c: InternalAlignment(g5,g3)
    c: Block(g3)
    c: Coincident(g6,g0)
    c: Coincident(g6,g3)
    c: Horizontal(g6)
FEATURE [Part::Extrusion] Extrude036  label="caseScrewPillarBracket014"
  Base = -> Sketch045
  Dir = (0,0,1)
  DirMode = 2
  FaceMakerClass = Part::FaceMakerBullseye
  LengthFwd = 2.4
  LengthRev = 0
  Placement = pos=(110.7,29,6.77) rot=(0,-1,0;1.5708rad)
  Solid = true
  Symmetric = false
FEATURE [Part::Extrusion] Extrude037  label="caseScrewPillarBracket015"
  Base = -> Sketch046
  Dir = (0,0,1)
  DirMode = 2
  FaceMakerClass = Part::FaceMakerBullseye
  LengthFwd = 2.4
  LengthRev = 0
  Placement = pos=(108.3,29,65.23) rot=(0,1,0;1.5708rad)
  Solid = true
  Symmetric = false
FEATURE [Part::Box] Box013  label="frontCaseScrewPillarBracket002"
  AttacherType = Attacher::AttachEngine3D
  Height = 2.4
  Length = 22
  Placement = pos=(87,28,2.3) rot=(0,0,1;0rad)
  Width = 7
FEATURE [Part::Box] Box014  label="frontCaseScrewPillarBracket003"
  AttacherType = Attacher::AttachEngine3D
  Height = 2.4
  Length = 22
  Placement = pos=(87,28,67.3) rot=(0,0,1;0rad)
  Width = 7
FEATURE [Part::Feature] Face087
  shape: bbox 4.8 x 30.2 x 2e-07 mm, 1 faces, 0 solids (baked)
FEATURE [Part::Revolution] Revolve091  label="frontCaseScrewPost004"
  Angle = 360
  Axis = (0,1,0)
  Base = (0,0,0)
  FaceMakerClass = Part::FaceMakerBullseye
  Placement = pos=(89.5,4.5,3.5) rot=(0,0,1;0rad)
  Solid = false
  Source = -> Face087
  Symmetric = false
FEATURE [Part::Feature] Face088
  shape: bbox 4.8 x 30.2 x 2e-07 mm, 1 faces, 0 solids (baked)
FEATURE [Part::Revolution] Revolve092  label="frontCaseScrewPost005"
  Angle = 360
  Axis = (0,1,0)
  Base = (0,0,0)
  FaceMakerClass = Part::FaceMakerBullseye
  Placement = pos=(89.5,4.5,68.5) rot=(0,0,1;0rad)
  Solid = false
  Source = -> Face088
  Symmetric = false
FEATURE [Part::Feature] Face089
  shape: bbox 3.5 x 30.2 x 2e-07 mm, 1 faces, 0 solids (baked)
FEATURE [Part::Revolution] Revolve093  label="backCaseScrewPost002"
  Angle = 360
  Axis = (0,1,0)
  Base = (0,0,0)
  FaceMakerClass = Part::FaceMakerBullseye
  Placement = pos=(12.5,4.5,10) rot=(0,0,1;0rad)
  Solid = false
  Source = -> Face089
  Symmetric = false
FEATURE [Part::Feature] Face090
  shape: bbox 3.5 x 30.2 x 2e-07 mm, 1 faces, 0 solids (baked)
FEATURE [Part::Revolution] Revolve094  label="backCaseScrewPost003"
  Angle = 360
  Axis = (0,1,0)
  Base = (0,0,0)
  FaceMakerClass = Part::FaceMakerBullseye
  Placement = pos=(12.5,4.5,62) rot=(0,0,1;0rad)
  Solid = false
  Source = -> Face090
  Symmetric = false
FEATURE [Part::Box] Box015  label="Cube011"
  AttacherType = Attacher::AttachEngine3D
  Height = 28.8
  Length = 3
  Placement = pos=(107.3,28,21.6) rot=(0,0,1;0rad)
  Width = 7
FEATURE [Part::Box] Box016  label="Cube012"
  AttacherType = Attacher::AttachEngine3D
  Height = 3
  Length = 7.4
  Placement = pos=(107.3,28,18.6) rot=(0,0,1;0rad)
  Width = 7
FEATURE [Part::Box] Box017  label="Cube013"
  AttacherType = Attacher::AttachEngine3D
  Height = 3
  Length = 7.4
  Placement = pos=(107.3,28,50.4) rot=(0,0,1;0rad)
  Width = 7
FEATURE [Part::Cylinder] Cylinder024
  Angle = 360
  AttacherType = Attacher::AttachEngine3D
  Height = 20
  Placement = pos=(0,0,36.15) rot=(0,0,1;0rad)
  Radius = 14.3
FEATURE [Part::Cylinder] Cylinder025
  Angle = 360
  AttacherType = Attacher::AttachEngine3D
  Height = 10
  Placement = pos=(0,0,36.15) rot=(0,0,1;0rad)
  Radius = 4
FEATURE [Part::MultiFuse] Fusion066  label="removeToCreteHoleForPlugHousing009"
  Placement = pos=(70,19,36) rot=(0,1,0;1.5708rad)
  Shapes = -> [Cylinder024,Cylinder025]
FEATURE [Part::MultiFuse] Fusion065  label="plugHousingBracketHolder002"
  Shapes = -> [Box017,Box015,Box016]
FEATURE [Part::Cut] Cut025  label="plugHousingBracketHolder003"
  Base = -> Fusion065
  Placement = pos=(7,0,0) rot=(0,0,1;0rad)
  Tool = -> Fusion066
FEATURE [Sketcher::SketchObject] Sketch047
  FullyConstrained = false
  Placement = pos=(0,0,0) rot=(1,0,0;1.5708rad)
  sketch-geometry (24):
    g0: ArcOfCircle CenterX=-4 CenterY=-10.5 CenterZ=0 NormalX=0 NormalY=0 NormalZ=1 AngleXU=0 Radius=1.5 StartAngle=6e-16 EndAngle=3.14159
    g1: ArcOfCircle CenterX=-34.2 CenterY=-10.5 CenterZ=0 NormalX=0 NormalY=0 NormalZ=1 AngleXU=0 Radius=1.5 StartAngle=0 EndAngle=3.14159
    g2: ArcOfCircle CenterX=-34.2 CenterY=-27.7 CenterZ=0 NormalX=0 NormalY=0 NormalZ=1 AngleXU=0 Radius=1.5 StartAngle=3.14159 EndAngle=6.28319
    g3: ArcOfCircle CenterX=-4 CenterY=-27.7 CenterZ=0 NormalX=0 NormalY=0 NormalZ=1 AngleXU=0 Radius=1.5 StartAngle=3.1416 EndAngle=6.28319
    g4: ArcOfCircle CenterX=-10 CenterY=-4.3 CenterZ=0 NormalX=0 NormalY=0 NormalZ=1 AngleXU=0 Radius=1.5 StartAngle=2e-16 EndAngle=3.14159
    g5: ArcOfCircle CenterX=-16.1 CenterY=-1.8 CenterZ=0 NormalX=0 NormalY=0 NormalZ=1 AngleXU=0 Radius=1.5 StartAngle=5e-16 EndAngle=3.14159
    g6: ArcOfCircle CenterX=-22.1 CenterY=-1.8 CenterZ=0 NormalX=0 NormalY=0 NormalZ=1 AngleXU=0 Radius=1.5 StartAngle=5e-16 EndAngle=3.14159
    g7: ArcOfCircle CenterX=-28.2 CenterY=-4.3 CenterZ=0 NormalX=0 NormalY=0 NormalZ=1 AngleXU=0 Radius=1.5 StartAngle=2e-16 EndAngle=3.14159
    g8: ArcOfCircle CenterX=-10 CenterY=-33.9 CenterZ=0 NormalX=0 NormalY=0 NormalZ=1 AngleXU=0 Radius=1.5 StartAngle=3.14159 EndAngle=6.28319
    g9: ArcOfCircle CenterX=-16.1 CenterY=-36.4 CenterZ=0 NormalX=0 NormalY=0 NormalZ=1 AngleXU=0 Radius=1.5 StartAngle=3.14159 EndAngle=6.28319
    g10: ArcOfCircle CenterX=-22.1 CenterY=-36.4 CenterZ=0 NormalX=0 NormalY=0 NormalZ=1 AngleXU=0 Radius=1.5 StartAngle=3.14159 EndAngle=6.28319
    g11: ArcOfCircle CenterX=-28.2 CenterY=-33.9 CenterZ=0 NormalX=0 NormalY=0 NormalZ=1 AngleXU=0 Radius=1.5 StartAngle=3.14159 EndAngle=6.28319
    g12: LineSegment StartX=-35.7 StartY=-10.5 StartZ=0 EndX=-35.7 EndY=-27.7 EndZ=0
    g13: LineSegment StartX=-32.7 StartY=-10.5 StartZ=0 EndX=-32.7 EndY=-27.7 EndZ=0
    g14: LineSegment StartX=-29.7 StartY=-33.9 StartZ=0 EndX=-29.7 EndY=-4.3 EndZ=0
    g15: LineSegment StartX=-26.7 StartY=-33.9 StartZ=0 EndX=-26.7 EndY=-4.3 EndZ=0
    g16: LineSegment StartX=-2.5 StartY=-10.5 StartZ=0 EndX=-2.5 EndY=-27.7 EndZ=0
    g17: LineSegment StartX=-8.5 StartY=-4.3 StartZ=0 EndX=-8.5 EndY=-33.9 EndZ=0
    g18: LineSegment StartX=-5.5 StartY=-10.5 StartZ=0 EndX=-5.5 EndY=-27.7 EndZ=0
    g19: LineSegment StartX=-11.5 StartY=-4.3 StartZ=0 EndX=-11.5 EndY=-33.9 EndZ=0
    g20: LineSegment StartX=-14.6 StartY=-1.8 StartZ=0 EndX=-14.6 EndY=-36.4 EndZ=0
    g21: LineSegment StartX=-17.6 StartY=-1.8 StartZ=0 EndX=-17.6 EndY=-36.4 EndZ=0
    g22: LineSegment StartX=-20.6 StartY=-36.4 StartZ=0 EndX=-20.6 EndY=-1.8 EndZ=0
    g23: LineSegment StartX=-23.6 StartY=-1.8 StartZ=0 EndX=-23.6 EndY=-36.4 EndZ=0
  constraints (48):
    c: Block(g0)
    c: Block(g1)
    c: Block(g2)
    c: Block(g3)
    c: Block(g4)
    c: Block(g5)
    c: Block(g6)
    c: Block(g7)
    c: Block(g8)
    c: Block(g9)
    c: Block(g10)
    c: Block(g11)
    c: Coincident(g12,g1)
    c: Coincident(g12,g2)
    c: Vertical(g12)
    c: Coincident(g13,g1)
    c: Coincident(g13,g2)
    c: Vertical(g13)
    c: Coincident(g14,g11)
    c: Coincident(g14,g7)
    c: Vertical(g14)
    c: Coincident(g15,g11)
    c: Coincident(g15,g7)
    c: Vertical(g15)
    c: Coincident(g16,g0)
    c: Coincident(g16,g3)
    c: Vertical(g16)
    c: Coincident(g17,g4)
    c: Coincident(g17,g8)
    c: Vertical(g17)
    c: Coincident(g18,g0)
    c: Coincident(g18,g3)
    c: Vertical(g18)
    c: Coincident(g19,g4)
    c: Coincident(g19,g8)
    c: Vertical(g19)
    c: Coincident(g20,g5)
    c: Coincident(g20,g9)
    c: Vertical(g20)
    c: Coincident(g21,g5)
    c: Coincident(g21,g9)
    c: Vertical(g21)
    c: Coincident(g22,g10)
    c: Coincident(g22,g6)
    c: Vertical(g22)
    c: Coincident(g23,g6)
    c: Coincident(g23,g10)
    c: Vertical(g23)
FEATURE [Part::Extrusion] Extrude038  label="removeToCreateFanGrillHoles001"
  Base = -> Sketch047
  Dir = (0,-1,6e-16)
  DirMode = 2
  FaceMakerClass = Part::FaceMakerBullseye
  LengthFwd = 10
  LengthRev = 0
  Placement = pos=(65.4,44,54.82) rot=(0,0,1;0rad)
  Solid = true
  Symmetric = false
FEATURE [Part::Feature] Wire004
  shape: bbox 11 x 5.2 x 2e-07 mm, 0 faces, 0 solids (baked)
FEATURE [Part::Revolution] Revolve095
  Angle = 360
  Axis = (0,1,0)
  Base = (0,0,0)
  FaceMakerClass = Part::FaceMakerBullseye
  Placement = pos=(30.3,38,19.7) rot=(0,0,1;0rad)
  Solid = true
  Source = -> Wire004
  Symmetric = false
FEATURE [Part::Feature] Wire005
  shape: bbox 11 x 5.2 x 2e-07 mm, 0 faces, 0 solids (baked)
FEATURE [Part::Revolution] Revolve096
  Angle = 360
  Axis = (0,1,0)
  Base = (0,0,0)
  FaceMakerClass = Part::FaceMakerBullseye
  Placement = pos=(30.3,38,51.7) rot=(0,0,1;0rad)
  Solid = true
  Source = -> Wire005
  Symmetric = false
FEATURE [Part::Feature] Wire006
  shape: bbox 11 x 5.2 x 2e-07 mm, 0 faces, 0 solids (baked)
FEATURE [Part::Revolution] Revolve097
  Angle = 360
  Axis = (0,1,0)
  Base = (0,0,0)
  FaceMakerClass = Part::FaceMakerBullseye
  Placement = pos=(62.3,38,51.7) rot=(0,0,1;0rad)
  Solid = true
  Source = -> Wire006
  Symmetric = false
FEATURE [Part::Feature] Wire007
  shape: bbox 11 x 5.2 x 2e-07 mm, 0 faces, 0 solids (baked)
FEATURE [Part::Revolution] Revolve098
  Angle = 360
  Axis = (0,1,0)
  Base = (0,0,0)
  FaceMakerClass = Part::FaceMakerBullseye
  Placement = pos=(62.3,38,19.7) rot=(0,0,1;0rad)
  Solid = true
  Source = -> Wire007
  Symmetric = false
FEATURE [Part::MultiFuse] Fusion067  label="fanScrewHousing002"
  Shapes = -> [Revolve098,Revolve097,Revolve096,Revolve095]
FEATURE [Part::Feature] Face091 .. Face094  x4 (patterned run collapsed; names and placements below)
  shape: bbox 3.5 x 17.8 x 2e-07 mm, 1 faces, 0 solids (baked)
FEATURE [Part::Revolution] Revolve099  label="removeToCreateScrewAndThreadedInsertHole026"
  Angle = 360
  Axis = (0,1,0)
  Base = (0,0,0)
  FaceMakerClass = Part::FaceMakerBullseye
  Placement = pos=(62.3,30.3,19.7) rot=(0,0,1;0rad)
  Solid = false
  Source = -> Face091
  Symmetric = false
FEATURE [Part::Revolution] Revolve100  label="removeToCreateScrewAndThreadedInsertHole027"
  Angle = 360
  Axis = (0,1,0)
  Base = (0,0,0)
  FaceMakerClass = Part::FaceMakerBullseye
  Placement = pos=(62.3,30.3,51.7) rot=(0,0,1;0rad)
  Solid = false
  Source = -> Face092
  Symmetric = false
FEATURE [Part::Revolution] Revolve101  label="removeToCreateScrewAndThreadedInsertHole028"
  Angle = 360
  Axis = (0,1,0)
  Base = (0,0,0)
  FaceMakerClass = Part::FaceMakerBullseye
  Placement = pos=(30.3,30.3,19.7) rot=(0,0,1;0rad)
  Solid = false
  Source = -> Face093
  Symmetric = false
FEATURE [Part::Revolution] Revolve102  label="removeToCreateScrewAndThreadedInsertHole029"
  Angle = 360
  Axis = (0,1,0)
  Base = (0,0,0)
  FaceMakerClass = Part::FaceMakerBullseye
  Placement = pos=(30.3,30.3,51.7) rot=(0,0,1;0rad)
  Solid = false
  Source = -> Face094
  Symmetric = false
FEATURE [Part::MultiFuse] Fusion068  label="createThreadedInsertHolesForFan002"
  Shapes = -> [Revolve099,Revolve100,Revolve101,Revolve102]
FEATURE [Part::Cut] Cut026  label="fanScrewHousing003"
  Base = -> Fusion067
  Tool = -> Fusion068
FEATURE [Sketcher::SketchObject] Sketch048
  FullyConstrained = false
  Placement = pos=(0,0,0) rot=(1,0,0;1.5708rad)
  sketch-geometry (24):
    g0: ArcOfCircle CenterX=-4 CenterY=-10.5 CenterZ=0 NormalX=0 NormalY=0 NormalZ=1 AngleXU=0 Radius=1.5 StartAngle=6e-16 EndAngle=3.14159
    g1: ArcOfCircle CenterX=-34.2 CenterY=-10.5 CenterZ=0 NormalX=0 NormalY=0 NormalZ=1 AngleXU=0 Radius=1.5 StartAngle=0 EndAngle=3.14159
    g2: ArcOfCircle CenterX=-34.2 CenterY=-27.7 CenterZ=0 NormalX=0 NormalY=0 NormalZ=1 AngleXU=0 Radius=1.5 StartAngle=3.14159 EndAngle=6.28319
    g3: ArcOfCircle CenterX=-4 CenterY=-27.7 CenterZ=0 NormalX=0 NormalY=0 NormalZ=1 AngleXU=0 Radius=1.5 StartAngle=3.1416 EndAngle=6.28319
    g4: ArcOfCircle CenterX=-10 CenterY=-4.3 CenterZ=0 NormalX=0 NormalY=0 NormalZ=1 AngleXU=0 Radius=1.5 StartAngle=2e-16 EndAngle=3.14159
    g5: ArcOfCircle CenterX=-16.1 CenterY=-1.8 CenterZ=0 NormalX=0 NormalY=0 NormalZ=1 AngleXU=0 Radius=1.5 StartAngle=5e-16 EndAngle=3.14159
    g6: ArcOfCircle CenterX=-22.1 CenterY=-1.8 CenterZ=0 NormalX=0 NormalY=0 NormalZ=1 AngleXU=0 Radius=1.5 StartAngle=5e-16 EndAngle=3.14159
    g7: ArcOfCircle CenterX=-28.2 CenterY=-4.3 CenterZ=0 NormalX=0 NormalY=0 NormalZ=1 AngleXU=0 Radius=1.5 StartAngle=2e-16 EndAngle=3.14159
    g8: ArcOfCircle CenterX=-10 CenterY=-33.9 CenterZ=0 NormalX=0 NormalY=0 NormalZ=1 AngleXU=0 Radius=1.5 StartAngle=3.14159 EndAngle=6.28319
    g9: ArcOfCircle CenterX=-16.1 CenterY=-36.4 CenterZ=0 NormalX=0 NormalY=0 NormalZ=1 AngleXU=0 Radius=1.5 StartAngle=3.14159 EndAngle=6.28319
    g10: ArcOfCircle CenterX=-22.1 CenterY=-36.4 CenterZ=0 NormalX=0 NormalY=0 NormalZ=1 AngleXU=0 Radius=1.5 StartAngle=3.14159 EndAngle=6.28319
    g11: ArcOfCircle CenterX=-28.2 CenterY=-33.9 CenterZ=0 NormalX=0 NormalY=0 NormalZ=1 AngleXU=0 Radius=1.5 StartAngle=3.14159 EndAngle=6.28319
    g12: LineSegment StartX=-35.7 StartY=-10.5 StartZ=0 EndX=-35.7 EndY=-27.7 EndZ=0
    g13: LineSegment StartX=-32.7 StartY=-10.5 StartZ=0 EndX=-32.7 EndY=-27.7 EndZ=0
    g14: LineSegment StartX=-29.7 StartY=-33.9 StartZ=0 EndX=-29.7 EndY=-4.3 EndZ=0
    g15: LineSegment StartX=-26.7 StartY=-33.9 StartZ=0 EndX=-26.7 EndY=-4.3 EndZ=0
    g16: LineSegment StartX=-2.5 StartY=-10.5 StartZ=0 EndX=-2.5 EndY=-27.7 EndZ=0
    g17: LineSegment StartX=-8.5 StartY=-4.3 StartZ=0 EndX=-8.5 EndY=-33.9 EndZ=0
    g18: LineSegment StartX=-5.5 StartY=-10.5 StartZ=0 EndX=-5.5 EndY=-27.7 EndZ=0
    g19: LineSegment StartX=-11.5 StartY=-4.3 StartZ=0 EndX=-11.5 EndY=-33.9 EndZ=0
    g20: LineSegment StartX=-14.6 StartY=-1.8 StartZ=0 EndX=-14.6 EndY=-36.4 EndZ=0
    g21: LineSegment StartX=-17.6 StartY=-1.8 StartZ=0 EndX=-17.6 EndY=-36.4 EndZ=0
    g22: LineSegment StartX=-20.6 StartY=-36.4 StartZ=0 EndX=-20.6 EndY=-1.8 EndZ=0
    g23: LineSegment StartX=-23.6 StartY=-1.8 StartZ=0 EndX=-23.6 EndY=-36.4 EndZ=0
  constraints (48):
    c: Block(g0)
    c: Block(g1)
    c: Block(g2)
    c: Block(g3)
    c: Block(g4)
    c: Block(g5)
    c: Block(g6)
    c: Block(g7)
    c: Block(g8)
    c: Block(g9)
    c: Block(g10)
    c: Block(g11)
    c: Coincident(g12,g1)
    c: Coincident(g12,g2)
    c: Vertical(g12)
    c: Coincident(g13,g1)
    c: Coincident(g13,g2)
    c: Vertical(g13)
    c: Coincident(g14,g11)
    c: Coincident(g14,g7)
    c: Vertical(g14)
    c: Coincident(g15,g11)
    c: Coincident(g15,g7)
    c: Vertical(g15)
    c: Coincident(g16,g0)
    c: Coincident(g16,g3)
    c: Vertical(g16)
    c: Coincident(g17,g4)
    c: Coincident(g17,g8)
    c: Vertical(g17)
    c: Coincident(g18,g0)
    c: Coincident(g18,g3)
    c: Vertical(g18)
    c: Coincident(g19,g4)
    c: Coincident(g19,g8)
    c: Vertical(g19)
    c: Coincident(g20,g5)
    c: Coincident(g20,g9)
    c: Vertical(g20)
    c: Coincident(g21,g5)
    c: Coincident(g21,g9)
    c: Vertical(g21)
    c: Coincident(g22,g10)
    c: Coincident(g22,g6)
    c: Vertical(g22)
    c: Coincident(g23,g6)
    c: Coincident(g23,g10)
    c: Vertical(g23)
FEATURE [Part::Extrusion] Extrude039  label="removeToCreateFanGrillHoles002"
  Base = -> Sketch048
  Dir = (0,-1,6e-16)
  DirMode = 2
  FaceMakerClass = Part::FaceMakerBullseye
  LengthFwd = 10
  LengthRev = 0
  Placement = pos=(65.4,44,54.82) rot=(0,0,1;0rad)
  Solid = true
  Symmetric = false
FEATURE [Part::Cut] Cut027  label="fanScrewHousing004"
  Base = -> Cut026
  Tool = -> Extrude038
FEATURE [Part::Cut] Cut028  label="top014"
  Base = -> Fillet026
  Tool = -> Extrude039
FEATURE [Part::Feature] Face095 .. Face098  x4 (patterned run collapsed; names and placements below)
  shape: bbox 3.5 x 17.8 x 2e-07 mm, 1 faces, 0 solids (baked)
FEATURE [Part::Revolution] Revolve103  label="removeToCreateScrewAndThreadedInsertHole030"
  Angle = 360
  Axis = (0,1,0)
  Base = (0,0,0)
  FaceMakerClass = Part::FaceMakerBullseye
  Placement = pos=(62.3,30.3,19.7) rot=(0,0,1;0rad)
  Solid = false
  Source = -> Face095
  Symmetric = false
FEATURE [Part::Revolution] Revolve104  label="removeToCreateScrewAndThreadedInsertHole031"
  Angle = 360
  Axis = (0,1,0)
  Base = (0,0,0)
  FaceMakerClass = Part::FaceMakerBullseye
  Placement = pos=(62.3,30.3,51.7) rot=(0,0,1;0rad)
  Solid = false
  Source = -> Face096
  Symmetric = false
FEATURE [Part::Revolution] Revolve105  label="removeToCreateScrewAndThreadedInsertHole032"
  Angle = 360
  Axis = (0,1,0)
  Base = (0,0,0)
  FaceMakerClass = Part::FaceMakerBullseye
  Placement = pos=(30.3,30.3,19.7) rot=(0,0,1;0rad)
  Solid = false
  Source = -> Face097
  Symmetric = false
FEATURE [Part::Revolution] Revolve106  label="removeToCreateScrewAndThreadedInsertHole033"
  Angle = 360
  Axis = (0,1,0)
  Base = (0,0,0)
  FaceMakerClass = Part::FaceMakerBullseye
  Placement = pos=(30.3,30.3,51.7) rot=(0,0,1;0rad)
  Solid = false
  Source = -> Face098
  Symmetric = false
FEATURE [Part::MultiFuse] Fusion069  label="createThreadedInsertHolesForFan003"
  Shapes = -> [Revolve103,Revolve104,Revolve105,Revolve106]
FEATURE [Part::Cut] Cut029  label="top015"
  Base = -> Cut028
  Tool = -> Fusion054
FEATURE [Part::Cut] Cut030  label="fanScrewHousing005"
  Base = -> Cut027
  Tool = -> Fusion069
FEATURE [Part::Cylinder] Cylinder026  label="removeToCreteHoleForPlugHousing010"
  Angle = 360
  AttacherType = Attacher::AttachEngine3D
  Height = 20
  Placement = pos=(-2,19,36) rot=(0,1,0;1.5708rad)
  Radius = 14.3
FEATURE [Part::Box] Box018  label="removeToCreteHoleForPlugHousing011"
  AttacherType = Attacher::AttachEngine3D
  Height = 28.6
  Length = 10
  Placement = pos=(-2,0,21.7) rot=(0,0,1;0rad)
  Width = 19
FEATURE [Part::Box] Box019  label="wireHolderBottomCaseBit"
  AttacherType = Attacher::AttachEngine3D
  Height = 28
  Length = 3
  Placement = pos=(0,0,22) rot=(0,0,1;0rad)
  Width = 21
FEATURE [Part::Cylinder] Cylinder027  label="removeToCreteHoleForPlugHousing012"
  Angle = 360
  AttacherType = Attacher::AttachEngine3D
  Height = 20
  Placement = pos=(-2,19,36) rot=(0,1,0;1.5708rad)
  Radius = 14.3
FEATURE [Part::Cut] Cut031  label="wireHolderBottomCaseBit001"
  Base = -> Box019
  Tool = -> Cylinder027
FEATURE [Part::MultiFuse] Fusion070  label="removeToCreteHoleForPlugHousing013"
  Shapes = -> [Box018,Cylinder026]
FEATURE [Part::Cut] Cut032  label="top016"
  Base = -> Cut029
  Tool = -> Fusion070
FEATURE [Part::Cylinder] Cylinder028
  Angle = 360
  AttacherType = Attacher::AttachEngine3D
  Height = 20
  Placement = pos=(0,0,36.15) rot=(0,0,1;0rad)
  Radius = 14.3
FEATURE [Part::Cylinder] Cylinder029
  Angle = 360
  AttacherType = Attacher::AttachEngine3D
  Height = 10
  Placement = pos=(0,0,36.15) rot=(0,0,1;0rad)
  Radius = 4
FEATURE [Part::MultiFuse] Fusion071  label="removeToCreteHoleForPlugHousing014"
  Placement = pos=(70,19,36) rot=(0,1,0;1.5708rad)
  Shapes = -> [Cylinder028,Cylinder029]
FEATURE [Sketcher::SketchObject] Sketch049  label="topSketch011"
  FullyConstrained = true
  sketch-geometry (4):
    g0: ArcOfCircle CenterX=105 CenterY=19 CenterZ=0 NormalX=0 NormalY=0 NormalZ=1 AngleXU=0 Radius=20.6155 StartAngle=5.54125 EndAngle=6.28319
    g1: ArcOfCircle CenterX=105 CenterY=19 CenterZ=0 NormalX=0 NormalY=0 NormalZ=1 AngleXU=0 Radius=13 StartAngle=5.54125 EndAngle=6.28319
    g2: LineSegment StartX=118 StartY=19 StartZ=0 EndX=125.616 EndY=19 EndZ=0
    g3: LineSegment StartX=114.583 StartY=10.2157 StartZ=0 EndX=120.197 EndY=5.06982 EndZ=0
  constraints (7):
    c: Block(g0)
    c: Block(g1)
    c: Coincident(g2,g1)
    c: Coincident(g2,g0)
    c: Horizontal(g2)
    c: Coincident(g3,g1)
    c: Coincident(g3,g0)
FEATURE [Part::Box] Box020  label="removeToCreteHoleForPlugHousing015"
  AttacherType = Attacher::AttachEngine3D
  Height = 28.6
  Length = 20
  Placement = pos=(106.15,0,21.7) rot=(0,0,1;0rad)
  Width = 19
FEATURE [Part::MultiFuse] Fusion072  label="removeToCreteHoleForPlugHousing016"
  Shapes = -> [Box020,Fusion071]
FEATURE [Part::Cut] Cut033  label="removeToCreteHoleForPlugHousing017"
  Base = -> Cut032
  Tool = -> Fusion072
FEATURE [Part::Cylinder] Cylinder030
  Angle = 360
  AttacherType = Attacher::AttachEngine3D
  Height = 20
  Placement = pos=(0,0,36.15) rot=(0,0,1;0rad)
  Radius = 14.3
FEATURE [Part::Cylinder] Cylinder031
  Angle = 360
  AttacherType = Attacher::AttachEngine3D
  Height = 10
  Placement = pos=(0,0,36.15) rot=(0,0,1;0rad)
  Radius = 4
FEATURE [Part::Box] Box021  label="removeToCreteHoleForPlugHousing019"
  AttacherType = Attacher::AttachEngine3D
  Height = 28.6
  Length = 20
  Placement = pos=(106.15,0,21.7) rot=(0,0,1;0rad)
  Width = 19
FEATURE [Part::MultiFuse] Fusion074  label="removeToCreteHoleForPlugHousing020"
  Placement = pos=(70,19,36) rot=(0,1,0;1.5708rad)
  Shapes = -> [Cylinder030,Cylinder031]
FEATURE [Part::MultiFuse] Fusion073  label="removeToCreteHoleForPlugHousing018"
  Placement = pos=(0,0,28.3) rot=(0,0,1;0rad)
  Shapes = -> [Box021,Fusion074]
FEATURE [Part::Cylinder] Cylinder032
  Angle = 360
  AttacherType = Attacher::AttachEngine3D
  Height = 20
  Placement = pos=(0,0,36.15) rot=(0,0,1;0rad)
  Radius = 14.3
FEATURE [Part::Cylinder] Cylinder033
  Angle = 360
  AttacherType = Attacher::AttachEngine3D
  Height = 10
  Placement = pos=(0,0,36.15) rot=(0,0,1;0rad)
  Radius = 4
FEATURE [Part::Box] Box022  label="removeToCreteHoleForPlugHousing021"
  AttacherType = Attacher::AttachEngine3D
  Height = 28.6
  Length = 20
  Placement = pos=(106.15,0,21.7) rot=(0,0,1;0rad)
  Width = 19
FEATURE [Part::MultiFuse] Fusion076  label="removeToCreteHoleForPlugHousing023"
  Placement = pos=(70,19,36) rot=(0,1,0;1.5708rad)
  Shapes = -> [Cylinder032,Cylinder033]
FEATURE [Part::MultiFuse] Fusion075  label="removeToCreteHoleForPlugHousing022"
  Placement = pos=(0,0,-28.3) rot=(0,0,1;0rad)
  Shapes = -> [Box022,Fusion076]
FEATURE [Part::MultiFuse] Fusion077  label="removeToCreatePlugHousingBottomBit"
  Shapes = -> [Fusion075,Fusion073]
FEATURE [Part::Cylinder] Cylinder034
  Angle = 360
  AttacherType = Attacher::AttachEngine3D
  Height = 20
  Placement = pos=(0,0,36.15) rot=(0,0,1;0rad)
  Radius = 14
FEATURE [Part::Cylinder] Cylinder035
  Angle = 360
  AttacherType = Attacher::AttachEngine3D
  Height = 10
  Placement = pos=(0,0,36.15) rot=(0,0,1;0rad)
  Radius = 4
FEATURE [Part::MultiFuse] Fusion078  label="removeToCreteHoleForPlugHousing024"
  Placement = pos=(70,19,36) rot=(0,1,0;1.5708rad)
  Shapes = -> [Cylinder034,Cylinder035]
FEATURE [Part::MultiFuse] Fusion079  label="removeToCreatePlugHousingBottomBit001"
  Shapes = -> [Fusion078,Fusion077]
FEATURE [Part::Extrusion] Extrude040  label="bottomPlugHousingBit"
  Base = -> Sketch049
  Dir = (0,0,1)
  DirMode = 2
  FaceMakerClass = Part::FaceMakerBullseye
  LengthFwd = 72
  LengthRev = 0
  Solid = true
  Symmetric = false
FEATURE [Part::Cut] Cut034  label="bottomPlugHousingBit001"
  Base = -> Extrude040
  Placement = pos=(-0.09,0,0) rot=(0,0,1;0rad)
  Tool = -> Fusion079
FEATURE [Part::Box] Box023  label="Cube014"
  AttacherType = Attacher::AttachEngine3D
  Height = 16
  Length = 8
  Placement = pos=(12.7,31.52,28) rot=(0,0,1;0rad)
  Width = 4
FEATURE [Part::Cylinder] Cylinder036
  Angle = 360
  AttacherType = Attacher::AttachEngine3D
  Height = 10
  Placement = pos=(0,0,36.15) rot=(0,0,1;0rad)
  Radius = 4
FEATURE [Part::Cylinder] Cylinder037
  Angle = 360
  AttacherType = Attacher::AttachEngine3D
  Height = 20
  Placement = pos=(0,0,36.15) rot=(0,0,1;0rad)
  Radius = 8.2
FEATURE [Part::MultiFuse] Fusion080  label="removeToCreteHoleForPlugHousing025"
  Placement = pos=(-42,19,36) rot=(0,1,0;1.5708rad)
  Shapes = -> [Cylinder037,Cylinder036]
FEATURE [Sketcher::SketchObject] Sketch050  label="topSketch012"
  FullyConstrained = true
  sketch-geometry (4):
    g0: LineSegment StartX=16.8446 StartY=31.512 StartZ=0 EndX=16.3251 EndY=34.4666 EndZ=0
    g1: ArcOfCircle CenterX=19 CenterY=19.2524 CenterZ=0 NormalX=0 NormalY=0 NormalZ=1 AngleXU=0 Radius=15.4476 StartAngle=1.74483 EndAngle=2.72717
    g2: ArcOfCircle CenterX=19 CenterY=19.2524 CenterZ=0 NormalX=0 NormalY=0 NormalZ=1 AngleXU=0 Radius=12.4476 StartAngle=1.74483 EndAngle=2.73189
    g3: LineSegment StartX=4.86004 StartY=25.4725 StartZ=0 EndX=7.58253 EndY=24.2107 EndZ=0
  constraints (7):
    c: Block(g0)
    c: Coincident(g1,g0)
    c: Coincident(g2,g0)
    c: Coincident(g3,g1)
    c: Coincident(g3,g2)
    c: Block(g1)
    c: Block(g2)
FEATURE [Part::Extrusion] Extrude041
  Base = -> Sketch050
  Dir = (0,0,1)
  DirMode = 2
  FaceMakerClass = Part::FaceMakerBullseye
  LengthFwd = 10.6
  LengthRev = 0
  Placement = pos=(0,0,31) rot=(0,0,1;0rad)
  Solid = true
  Symmetric = false
FEATURE [Part::Cut] Cut035
  Base = -> Extrude041
  Placement = pos=(0,0,-0.3) rot=(0,0,1;0rad)
  Tool = -> Fusion080
FEATURE [Part::Cut] Cut036
  Base = -> Box023
  Tool = -> Cut035
FEATURE [Part::Fillet] Fillet027
  Base = -> Cut036
  Edges = 1 edges r=0.7: [Edge13]
FEATURE [Part::Fillet] Fillet028
  Base = -> Fillet027
  Edges = 1 edges r=0.7: [Edge13]
FEATURE [Part::Fillet] Fillet029
  Base = -> Fillet028
  Edges = 1 edges r=0.7: [Edge16]
FEATURE [Part::Fillet] Fillet030
  Base = -> Fillet029
  Edges = 1 edges r=0.7: [Edge11]
FEATURE [Part::Fillet] Fillet031
  Base = -> Fillet030
  Edges = 1 edges r=0.7: [Edge10]
FEATURE [Part::Fillet] Fillet032
  Base = -> Fillet031
  Edges = 1 edges r=1.2: [Edge5]
FEATURE [Part::Fillet] Fillet033
  Base = -> Fillet032
  Edges = 1 edges r=1.2: [Edge12]
FEATURE [Part::Fillet] Fillet034  label="wireHousingRetainer"
  Base = -> Fillet033
  Edges = 1 edges r=2: [Edge1]
  Placement = pos=(0.3,0,0) rot=(0,0,1;0rad)
FEATURE [Part::Feature] Face099
  shape: bbox 3.5 x 17.8 x 2e-07 mm, 1 faces, 0 solids (baked)
FEATURE [Part::Revolution] Revolve107  label="removeToCreateScrewAndThreadedInsertHole034"
  Angle = 360
  Axis = (0,1,0)
  Base = (0,0,0)
  FaceMakerClass = Part::FaceMakerBullseye
  Placement = pos=(12.5,0,10) rot=(0,0,1;0rad)
  Solid = false
  Source = -> Face099
  Symmetric = false
FEATURE [Part::Feature] Face100
  shape: bbox 3.5 x 17.8 x 2e-07 mm, 1 faces, 0 solids (baked)
FEATURE [Part::Revolution] Revolve108  label="removeToCreateScrewAndThreadedInsertHole035"
  Angle = 360
  Axis = (0,1,0)
  Base = (0,0,0)
  FaceMakerClass = Part::FaceMakerBullseye
  Placement = pos=(12.5,0,62) rot=(0,0,1;0rad)
  Solid = false
  Source = -> Face100
  Symmetric = false
FEATURE [Part::Feature] Face101
  shape: bbox 3.5 x 17.8 x 2e-07 mm, 1 faces, 0 solids (baked)
FEATURE [Part::Revolution] Revolve109  label="removeToCreateScrewAndThreadedInsertHole036"
  Angle = 360
  Axis = (0,1,0)
  Base = (0,0,0)
  FaceMakerClass = Part::FaceMakerBullseye
  Placement = pos=(89.5,0,68.5) rot=(0,0,1;0rad)
  Solid = false
  Source = -> Face101
  Symmetric = false
FEATURE [Part::Feature] Face102
  shape: bbox 3.5 x 17.8 x 2e-07 mm, 1 faces, 0 solids (baked)
FEATURE [Part::Revolution] Revolve110  label="removeToCreateScrewAndThreadedInsertHole037"
  Angle = 360
  Axis = (0,1,0)
  Base = (0,0,0)
  FaceMakerClass = Part::FaceMakerBullseye
  Placement = pos=(89.5,0,3.5) rot=(0,0,1;0rad)
  Solid = false
  Source = -> Face102
  Symmetric = false
FEATURE [Part::Feature] Face103
  shape: bbox 3.5 x 17.8 x 2e-07 mm, 1 faces, 0 solids (baked)
FEATURE [Part::Revolution] Revolve111  label="removeToCreateScrewAndThreadedInsertHole038"
  Angle = 360
  Axis = (0,1,0)
  Base = (0,0,0)
  FaceMakerClass = Part::FaceMakerBullseye
  Placement = pos=(109.5,4.7,3.5) rot=(0,0,1;0rad)
  Solid = false
  Source = -> Face103
  Symmetric = false
FEATURE [Part::Feature] Face104
  shape: bbox 3.5 x 17.8 x 2e-07 mm, 1 faces, 0 solids (baked)
FEATURE [Part::Revolution] Revolve112  label="removeToCreateScrewAndThreadedInsertHole039"
  Angle = 360
  Axis = (0,1,0)
  Base = (0,0,0)
  FaceMakerClass = Part::FaceMakerBullseye
  Placement = pos=(109.5,4.7,68.5) rot=(0,0,1;0rad)
  Solid = false
  Source = -> Face104
  Symmetric = false
FEATURE [Part::MultiFuse] Fusion081  label="removeToCreateScrewAndThreadedInsertHole040"
  Shapes = -> [Revolve107,Revolve108,Revolve109,Revolve110,Revolve111,Revolve112]
FEATURE [Part::MultiFuse] Fusion082  label="casePillars002"
  Shapes = -> [Revolve094,Revolve092,Revolve090,Revolve089,Revolve091,Revolve093]
FEATURE [Part::Cut] Cut037  label="casePillars003"
  Base = -> Fusion082
  Tool = -> Fusion081
FEATURE [Sketcher::SketchObject] Sketch051
  FullyConstrained = true
  Placement = pos=(117,19,0) rot=(0.57735,0.57735,0.57735;2.0944rad)
  sketch-geometry (48):
    g0: LineSegment StartX=-49.19 StartY=69.25 StartZ=0 EndX=-49.19 EndY=66.25 EndZ=0
    g1: LineSegment StartX=-49.19 StartY=63.5 StartZ=0 EndX=-49.19 EndY=60.5 EndZ=0
    g2: LineSegment StartX=-49.19 StartY=57.75 StartZ=0 EndX=-49.19 EndY=54.75 EndZ=0
    g3: LineSegment StartX=-49.19 StartY=52 StartZ=0 EndX=-49.19 EndY=49 EndZ=0
    g4: LineSegment StartX=-49.19 StartY=46.25 StartZ=0 EndX=-49.19 EndY=43.25 EndZ=0
    g5: LineSegment StartX=-49.19 StartY=40.5 StartZ=0 EndX=-49.19 EndY=37.5 EndZ=0
    g6: LineSegment StartX=-49.19 StartY=34.5 StartZ=0 EndX=-49.19 EndY=31.5 EndZ=0
    g7: LineSegment StartX=-49.19 StartY=28.75 StartZ=0 EndX=-49.19 EndY=25.75 EndZ=0
    g8: LineSegment StartX=-49.19 StartY=23 StartZ=0 EndX=-49.19 EndY=20 EndZ=0
    g9: LineSegment StartX=-49.19 StartY=17.25 StartZ=0 EndX=-49.19 EndY=14.25 EndZ=0
    g10: LineSegment StartX=-49.19 StartY=11.5 StartZ=0 EndX=-49.19 EndY=8.5 EndZ=0
    g11: LineSegment StartX=-49.19 StartY=5.75 StartZ=0 EndX=-49.19 EndY=2.75 EndZ=0
    g12: ArcOfCircle CenterX=-1.5 CenterY=67.75 CenterZ=0 NormalX=0 NormalY=0 NormalZ=1 AngleXU=0 Radius=1.5 StartAngle=4.71239 EndAngle=7.85398
    g13: ArcOfCircle CenterX=-1.5 CenterY=62 CenterZ=0 NormalX=0 NormalY=0 NormalZ=1 AngleXU=0 Radius=1.5 StartAngle=4.71239 EndAngle=7.85398
    g14: ArcOfCircle CenterX=-1.5 CenterY=56.25 CenterZ=0 NormalX=0 NormalY=0 NormalZ=1 AngleXU=0 Radius=1.5 StartAngle=4.71239 EndAngle=7.85398
    g15: ArcOfCircle CenterX=-11.49 CenterY=50.5 CenterZ=0 NormalX=0 NormalY=0 NormalZ=1 AngleXU=0 Radius=1.5 StartAngle=4.71239 EndAngle=7.85398
    g16: ArcOfCircle CenterX=-16.28 CenterY=44.75 CenterZ=0 NormalX=0 NormalY=0 NormalZ=1 AngleXU=0 Radius=1.5 StartAngle=4.71239 EndAngle=7.85398
    g17: ArcOfCircle CenterX=-18.2337 CenterY=39 CenterZ=0 NormalX=0 NormalY=0 NormalZ=1 AngleXU=0 Radius=1.5 StartAngle=4.71485 EndAngle=7.85398
    g18: ArcOfCircle CenterX=-16.2837 CenterY=27.25 CenterZ=0 NormalX=0 NormalY=0 NormalZ=1 AngleXU=0 Radius=1.5 StartAngle=4.71485 EndAngle=7.85398
    g19: ArcOfCircle CenterX=-18.2337 CenterY=33 CenterZ=0 NormalX=0 NormalY=0 NormalZ=1 AngleXU=0 Radius=1.5 StartAngle=4.71485 EndAngle=7.85398
    g20: ArcOfCircle CenterX=-11.49 CenterY=21.5 CenterZ=0 NormalX=0 NormalY=0 NormalZ=1 AngleXU=0 Radius=1.5 StartAngle=4.71239 EndAngle=7.85398
    g21: ArcOfCircle CenterX=-1.5 CenterY=4.25 CenterZ=0 NormalX=0 NormalY=0 NormalZ=1 AngleXU=0 Radius=1.5 StartAngle=4.71239 EndAngle=7.85398
    g22: ArcOfCircle CenterX=-1.5 CenterY=10 CenterZ=0 NormalX=0 NormalY=0 NormalZ=1 AngleXU=0 Radius=1.5 StartAngle=4.71239 EndAngle=7.85398
    g23: ArcOfCircle CenterX=-1.5 CenterY=15.75 CenterZ=0 NormalX=0 NormalY=0 NormalZ=1 AngleXU=0 Radius=1.5 StartAngle=4.71239 EndAngle=7.85398
    g24: LineSegment StartX=-49.19 StartY=69.25 StartZ=0 EndX=-1.5 EndY=69.25 EndZ=0
    g25: LineSegment StartX=-49.19 StartY=66.25 StartZ=0 EndX=-1.5 EndY=66.25 EndZ=0
    g26: LineSegment StartX=-49.19 StartY=63.5 StartZ=0 EndX=-1.5 EndY=63.5 EndZ=0
    g27: LineSegment StartX=-49.19 StartY=60.5 StartZ=0 EndX=-1.5 EndY=60.5 EndZ=0
    g28: LineSegment StartX=-49.19 StartY=57.75 StartZ=0 EndX=-1.5 EndY=57.75 EndZ=0
    g29: LineSegment StartX=-49.19 StartY=54.75 StartZ=0 EndX=-1.5 EndY=54.75 EndZ=0
    g30: LineSegment StartX=-49.19 StartY=52 StartZ=0 EndX=-11.49 EndY=52 EndZ=0
    g31: LineSegment StartX=-49.19 StartY=49 StartZ=0 EndX=-11.49 EndY=49 EndZ=0
    g32: LineSegment StartX=-49.19 StartY=46.25 StartZ=0 EndX=-16.28 EndY=46.25 EndZ=0
    g33: LineSegment StartX=-49.19 StartY=43.25 StartZ=0 EndX=-16.28 EndY=43.25 EndZ=0
    g34: LineSegment StartX=-49.19 StartY=40.5 StartZ=0 EndX=-18.2337 EndY=40.5 EndZ=0
    g35: LineSegment StartX=-49.19 StartY=37.5 StartZ=0 EndX=-18.23 EndY=37.5 EndZ=0
    g36: LineSegment StartX=-49.19 StartY=34.5 StartZ=0 EndX=-18.2337 EndY=34.5 EndZ=0
    g37: LineSegment StartX=-49.19 StartY=31.5 StartZ=0 EndX=-18.23 EndY=31.5 EndZ=0
    g38: LineSegment StartX=-49.19 StartY=28.75 StartZ=0 EndX=-16.2837 EndY=28.75 EndZ=0
    g39: LineSegment StartX=-49.19 StartY=25.75 StartZ=0 EndX=-16.28 EndY=25.75 EndZ=0
    g40: LineSegment StartX=-49.19 StartY=23 StartZ=0 EndX=-11.49 EndY=23 EndZ=0
    g41: LineSegment StartX=-49.19 StartY=20 StartZ=0 EndX=-11.49 EndY=20 EndZ=0
    g42: LineSegment StartX=-49.19 StartY=17.25 StartZ=0 EndX=-1.5 EndY=17.25 EndZ=0
    g43: LineSegment StartX=-49.19 StartY=14.25 StartZ=0 EndX=-1.5 EndY=14.25 EndZ=0
    g44: LineSegment StartX=-49.19 StartY=11.5 StartZ=0 EndX=-1.5 EndY=11.5 EndZ=0
    g45: LineSegment StartX=-49.19 StartY=8.5 StartZ=0 EndX=-1.5 EndY=8.5 EndZ=0
    g46: LineSegment StartX=-49.19 StartY=5.75 StartZ=0 EndX=-1.5 EndY=5.75 EndZ=0
    g47: LineSegment StartX=-49.19 StartY=2.75 StartZ=0 EndX=-1.5 EndY=2.75 EndZ=0
  constraints (120):
    c: Vertical(g0)
    c: Distance(g0) = 3
    c: Block(g0)
    c: Vertical(g1)
    c: Distance(g1) = 3
    c: Vertical(g2)
    c: Equal(g0,g2) = 3
    c: Block(g2)
    c: Vertical(g3)
    c: Equal(g1,g3) = 3
    c: Vertical(g4)
    c: Equal(g0,g4) = 3
    c: Block(g4)
    c: Vertical(g5)
    c: Equal(g1,g5) = 3
    c: Vertical(g6)
    c: Equal(g0,g6) = 3
    c: Block(g6)
    c: Vertical(g7)
    c: Equal(g1,g7) = 3
    c: Vertical(g8)
    c: Equal(g0,g8) = 3
    c: Block(g8)
    c: Vertical(g9)
    c: Equal(g1,g9) = 3
    c: Vertical(g10)
    c: Equal(g0,g10) = 3
    c: Block(g10)
    c: Vertical(g11)
    c: Equal(g1,g11) = 3
    c: Block(g12)
    c: Block(g13)
    c: Block(g14)
    c: Block(g15)
    c: Block(g16)
    c: Block(g17)
    c: Block(g18)
    c: Block(g19)
    c: Block(g20)
    c: Block(g21)
    c: Block(g22)
    c: Block(g23)
    c: Block(g11)
    c: Block(g9)
    c: Block(g7)
    c: Block(g5)
    c: Block(g3)
    c: Block(g1)
    c: Coincident(g24,g0)
    c: Coincident(g24,g12)
    c: Horizontal(g24)
    c: Coincident(g25,g0)
    c: Coincident(g25,g12)
    c: Horizontal(g25)
    c: Coincident(g26,g1)
    c: Coincident(g26,g13)
    c: Horizontal(g26)
    c: Coincident(g27,g1)
    c: Coincident(g27,g13)
    c: Horizontal(g27)
    c: Coincident(g28,g2)
    c: Coincident(g28,g14)
    c: Horizontal(g28)
    c: Coincident(g29,g2)
    c: Coincident(g29,g14)
    c: Horizontal(g29)
    c: Coincident(g30,g3)
    c: Coincident(g30,g15)
    c: Horizontal(g30)
    c: Coincident(g31,g3)
    c: Coincident(g31,g15)
    c: Horizontal(g31)
    c: Coincident(g32,g4)
    c: Coincident(g32,g16)
    c: Horizontal(g32)
    c: Coincident(g33,g4)
    c: Coincident(g33,g16)
    c: Horizontal(g33)
    c: Coincident(g34,g5)
    c: Coincident(g34,g17)
    c: Horizontal(g34)
    c: Coincident(g35,g5)
    c: Coincident(g35,g17)
    c: Horizontal(g35)
    c: Coincident(g36,g6)
    c: Coincident(g36,g19)
    c: Horizontal(g36)
    c: Coincident(g37,g6)
    c: Coincident(g37,g19)
    c: Horizontal(g37)
    c: Coincident(g38,g7)
    c: Coincident(g38,g18)
    c: Horizontal(g38)
    c: Coincident(g39,g7)
    c: Coincident(g39,g18)
    c: Horizontal(g39)
    c: Coincident(g40,g8)
    c: Coincident(g40,g20)
    c: Horizontal(g40)
    c: Coincident(g41,g8)
    c: Coincident(g41,g20)
    c: Horizontal(g41)
    c: Coincident(g42,g9)
    c: Coincident(g42,g23)
    c: Horizontal(g42)
    c: Coincident(g43,g9)
    c: Coincident(g43,g23)
    c: Horizontal(g43)
    c: Coincident(g44,g10)
    c: Coincident(g44,g22)
    c: Horizontal(g44)
    c: Coincident(g45,g10)
    c: Coincident(g45,g22)
    c: Horizontal(g45)
    c: Coincident(g46,g11)
    c: Coincident(g46,g21)
    c: Horizontal(g46)
    c: Coincident(g47,g11)
    c: Coincident(g47,g21)
    c: Horizontal(g47)
FEATURE [Part::Extrusion] Extrude042
  Base = -> Sketch051
  Dir = (1,-2e-16,2e-16)
  DirMode = 2
  FaceMakerClass = Part::FaceMakerBullseye
  LengthFwd = 19
  LengthRev = 0
  Placement = pos=(-19,0,0) rot=(0,0,1;0rad)
  Solid = true
  Symmetric = false
FEATURE [Part::Fillet] Fillet035  label="removeToCreateVentalationHoles"
  Base = -> Extrude042
  Edges = <same value as first occurrence — deduplicated (x6 in doc)>
  Placement = pos=(7,0,0) rot=(0,0,1;0rad)
FEATURE [Part::Cut] Cut038  label="top017"
  Base = -> Cut033
  Tool = -> Fillet035
FEATURE [Sketcher::SketchObject] Sketch052  label="bottomSketch001"
  FullyConstrained = true
  sketch-geometry (45):
    g0: LineSegment StartX=6.29999 StartY=8 StartZ=0 EndX=3.29999 EndY=8 EndZ=0
    g1: LineSegment StartX=3.29999 StartY=8 StartZ=0 EndX=3.29999 EndY=-6.03275e-07 EndZ=0
    g2: ArcOfCircle CenterX=8.29999 CenterY=5 CenterZ=0 NormalX=0 NormalY=0 NormalZ=1 AngleXU=0 Radius=2 StartAngle=3.14159 EndAngle=4.71239
    g3: LineSegment StartX=6.29999 StartY=8 StartZ=0 EndX=6.29999 EndY=5 EndZ=0
    g4: ArcOfCircle CenterX=105 CenterY=19 CenterZ=0 NormalX=0 NormalY=0 NormalZ=1 AngleXU=0 Radius=12.7 StartAngle=4.71239 EndAngle=5.94289
    g5-g11: Circle x7 (B-spline internal-alignment scaffolding for g12; pole/knot coordinates omitted)
    g12: BSplineCurve PolesCount=7 KnotsCount=5 Degree=3 IsPeriodic=0
    g13-g17: GeomPoint x5 (B-spline internal-alignment scaffolding for g12; pole/knot coordinates omitted)
    g18: ArcOfCircle CenterX=105 CenterY=19 CenterZ=0 NormalX=0 NormalY=0 NormalZ=1 AngleXU=0 Radius=15.7 StartAngle=5.81226 EndAngle=6.28319
    g19: BSplineCurve PolesCount=5 KnotsCount=3 Degree=3 IsPeriodic=0
    g20: LineSegment StartX=8.29999 StartY=3 StartZ=0 EndX=101.7 EndY=3 EndZ=0
    g21: LineSegment StartX=3.29999 StartY=-6.03275e-07 StartZ=0 EndX=105 EndY=-6.03275e-07 EndZ=0
    g22: LineSegment StartX=120.974 StartY=8.71251 StartZ=0 EndX=122.332 EndY=7.83778 EndZ=0
    g23: LineSegment StartX=105 StartY=-6.03274e-07 StartZ=0 EndX=113 EndY=-6.03274e-07 EndZ=0
    g24: ArcOfCircle CenterX=105 CenterY=19 CenterZ=0 NormalX=0 NormalY=0 NormalZ=1 AngleXU=0 Radius=20.6155 StartAngle=5.11091 EndAngle=5.71103
    g25: ArcOfCircle CenterX=117.7 CenterY=19 CenterZ=0 NormalX=0 NormalY=0 NormalZ=1 AngleXU=0 Radius=3 StartAngle=1.2e-15 EndAngle=2.10468
    g26: Circle CenterX=116.345 CenterY=16.3232 CenterZ=0 NormalX=0 NormalY=0 NormalZ=1 AngleXU=0 Radius=1
    g27: Circle CenterX=117.24 CenterY=15.7584 CenterZ=0 NormalX=0 NormalY=0 NormalZ=1 AngleXU=0 Radius=1
    g28: Circle CenterX=116.972 CenterY=14.7612 CenterZ=0 NormalX=0 NormalY=0 NormalZ=1 AngleXU=0 Radius=1
    g29: BSplineCurve PolesCount=3 KnotsCount=2 Degree=2 IsPeriodic=0
    g30: GeomPoint X=116.345 Y=16.3232 Z=0
    g31: GeomPoint X=116.972 Y=14.7612 Z=0
    g32: Circle CenterX=115.828 CenterY=17.157 CenterZ=0 NormalX=0 NormalY=0 NormalZ=1 AngleXU=0 Radius=1
    g33: Circle CenterX=115.841 CenterY=16.639 CenterZ=0 NormalX=0 NormalY=0 NormalZ=1 AngleXU=0 Radius=1
    g34: Circle CenterX=116.345 CenterY=16.3232 CenterZ=0 NormalX=0 NormalY=0 NormalZ=1 AngleXU=0 Radius=1
    g35: BSplineCurve PolesCount=3 KnotsCount=2 Degree=2 IsPeriodic=0
    g36: GeomPoint X=115.828 Y=17.157 Z=0
    g37: GeomPoint X=116.345 Y=16.3232 Z=0
    g38: LineSegment StartX=115.828 StartY=17.157 StartZ=0 EndX=115.828 EndY=20.8307 EndZ=0
    g39: Circle CenterX=115.828 CenterY=20.8307 CenterZ=0 NormalX=0 NormalY=0 NormalZ=1 AngleXU=0 Radius=1
    g40: Circle CenterX=115.831 CenterY=21.3396 CenterZ=0 NormalX=0 NormalY=0 NormalZ=1 AngleXU=0 Radius=1
    g41: Circle CenterX=116.173 CenterY=21.5825 CenterZ=0 NormalX=0 NormalY=0 NormalZ=1 AngleXU=0 Radius=1
    g42: BSplineCurve PolesCount=3 KnotsCount=2 Degree=2 IsPeriodic=0
    g43: GeomPoint X=115.828 Y=20.8307 Z=0
    g44: GeomPoint X=116.173 Y=21.5825 Z=0
  constraints (70):
    c: Horizontal(g0)
    c: Distance(g0) = 3
    c: Coincident(g1,g0)
    c: Vertical(g1)
    c: Block(g2)
    c: Block(g0)
    c: Coincident(g3,g0)
    c: Coincident(g3,g2)
    c: Vertical(g3)
    c: Block(g1)
    c: Block(g4)
    c: Coincident(g19,g4)
    c: Block(g19)
    c: Equal(g5, g6-g11) x6
    c: InternalAlignment(g5-g11 -> g12) x7
    c: InternalAlignment(g13-g17 -> g12) x5
    c: Block(g12)
    c: Coincident(g18,g12)
    c: Block(g18)
    c: Coincident(g20,g2)
    c: Coincident(g20,g19)
    c: Horizontal(g20)
    c: Distance(g20) = 93.4
    c: Coincident(g21,g1)
    c: Horizontal(g21)
    c: Distance(g21) = 101.7
    c: Horizontal(g23)
    c: Distance(g23) = 8
    c: Coincident(g24,g23)
    c: Block(g23)
    c: Coincident(g22,g24)
    c: Block(g24)
    c: Block(g22)
    c: Distance(g22) = 1.61553
    c: Coincident(g25,g18)
    c: Block(g25)
    c: Weight(g26) = 1
    c: Equal(g26,g27)
    c: Equal(g26,g28)
    c: Coincident(g29,g4)
    c: InternalAlignment(g26,g29)
    c: InternalAlignment(g27,g29)
    c: InternalAlignment(g28,g29)
    c: InternalAlignment(g30,g29)
    c: InternalAlignment(g31,g29)
    c: Block(g29)
    c: Weight(g32) = 1
    c: Equal(g32,g33)
    c: Equal(g32,g34)
    c: Coincident(g35,g29)
    c: InternalAlignment(g32,g35)
    c: InternalAlignment(g33,g35)
    c: InternalAlignment(g34,g35)
    c: InternalAlignment(g36,g35)
    c: InternalAlignment(g37,g35)
    c: Block(g35)
    c: Coincident(g38,g35)
    c: Vertical(g38)
    c: Block(g38)
    c: Coincident(g42,g38)
    c: Weight(g39) = 1
    c: Equal(g39,g40)
    c: Equal(g39,g41)
    c: Coincident(g42,g25)
    c: InternalAlignment(g39,g42)
    c: InternalAlignment(g40,g42)
    c: InternalAlignment(g41,g42)
    c: InternalAlignment(g43,g42)
    c: InternalAlignment(g44,g42)
    c: Block(g42)
FEATURE [Part::Extrusion] Extrude043  label="bottom010"
  Base = -> Sketch052
  Dir = (0,0,1)
  DirMode = 2
  FaceMakerClass = Part::FaceMakerBullseye
  LengthFwd = 71.4
  LengthRev = 0
  Placement = pos=(0,0,0.3) rot=(0,0,1;0rad)
  Solid = true
  Symmetric = false
FEATURE [Sketcher::SketchObject] Sketch053  label="topSketch013"
  FullyConstrained = true
  sketch-geometry (22):
    g0: LineSegment StartX=5.21097e-06 StartY=3 StartZ=0 EndX=5.21097e-06 EndY=19 EndZ=0
    g1: ArcOfCircle CenterX=19 CenterY=19 CenterZ=0 NormalX=0 NormalY=0 NormalZ=1 AngleXU=0 Radius=19 StartAngle=1.5708 EndAngle=3.14159
    g2: ArcOfCircle CenterX=19 CenterY=19 CenterZ=0 NormalX=0 NormalY=0 NormalZ=1 AngleXU=0 Radius=16 StartAngle=1.5708 EndAngle=3.14159
    g3: LineSegment StartX=114 StartY=35 StartZ=0 EndX=19 EndY=35 EndZ=0
    g4: LineSegment StartX=5.21097e-06 StartY=3 StartZ=0 EndX=5.21097e-06 EndY=0 EndZ=0
    g5: LineSegment StartX=3 StartY=0 StartZ=0 EndX=5.21097e-06 EndY=0 EndZ=0
    g6: LineSegment StartX=3 StartY=19 StartZ=0 EndX=3 EndY=0 EndZ=0
    g7: LineSegment StartX=19 StartY=38 StartZ=0 EndX=124 EndY=38 EndZ=0
    g8: Circle CenterX=119 CenterY=35 CenterZ=0 NormalX=0 NormalY=0 NormalZ=1 AngleXU=0 Radius=1
    g9: Circle CenterX=121 CenterY=35 CenterZ=0 NormalX=0 NormalY=0 NormalZ=1 AngleXU=0 Radius=1
    g10: Circle CenterX=121 CenterY=33 CenterZ=0 NormalX=0 NormalY=0 NormalZ=1 AngleXU=0 Radius=1
    g11: BSplineCurve PolesCount=3 KnotsCount=2 Degree=2 IsPeriodic=0
    g12: GeomPoint X=119 Y=35 Z=0
    g13: GeomPoint X=121 Y=33 Z=0
    g14: LineSegment StartX=119 StartY=35 StartZ=0 EndX=114 EndY=35 EndZ=0
    g15: ArcOfCircle CenterX=105 CenterY=19 CenterZ=0 NormalX=0 NormalY=0 NormalZ=1 AngleXU=0 Radius=16 StartAngle=5.60905 EndAngle=6.28319
    g16: LineSegment StartX=121 StartY=33 StartZ=0 EndX=121 EndY=19 EndZ=0
    g17: LineSegment StartX=117.5 StartY=9.01251 StartZ=0 EndX=121.163 EndY=9.0125 EndZ=0
    g18: ArcOfCircle CenterX=105 CenterY=19 CenterZ=0 NormalX=0 NormalY=0 NormalZ=1 AngleXU=0 Radius=20.6155 StartAngle=5.7297 EndAngle=6.28319
    g19: LineSegment StartX=121.163 StartY=9.0125 StartZ=0 EndX=122.538 EndY=8.16329 EndZ=0
    g20: LineSegment StartX=124 StartY=38 StartZ=0 EndX=125.616 EndY=38 EndZ=0
    g21: LineSegment StartX=125.616 StartY=19 StartZ=0 EndX=125.616 EndY=38 EndZ=0
  constraints (50):
    c: Vertical(g0)
    c: Block(g0)
    c: Coincident(g1,g0)
    c: Block(g1)
    c: Coincident(g2,g1)
    c: Block(g2)
    c: Coincident(g3,g2)
    c: Horizontal(g3)
    c: Tangent(g3,g2)
    c: Coincident(g4,g0)
    c: Distance(g4) = 3
    c: Vertical(g4)
    c: Coincident(g5,g4)
    c: Horizontal(g5)
    c: Coincident(g6,g2)
    c: Coincident(g6,g5)
    c: Vertical(g6)
    c: Horizontal(g7)
    c: Distance(g7) = 105
    c: Coincident(g7,g1)
    c: Block(g3)
    c: Weight(g8) = 1
    c: Equal(g8,g9)
    c: Equal(g8,g10)
    c: InternalAlignment(g8,g11)
    c: InternalAlignment(g9,g11)
    c: InternalAlignment(g10,g11)
    c: InternalAlignment(g12,g11)
    c: InternalAlignment(g13,g11)
    c: Block(g11)
    c: Coincident(g14,g11)
    c: Coincident(g14,g3)
    c: Horizontal(g14)
    c: Block(g15)
    c: Coincident(g16,g11)
    c: Coincident(g16,g15)
    c: Vertical(g16)
    c: Distance(g16) = 14
    c: Coincident(g17,g15)
    c: Block(g18)
    c: Coincident(g19,g18)
    c: Coincident(g20,g7)
    c: Horizontal(g20)
    c: Vertical(g21)
    c: Coincident(g20,g21)
    c: Block(g20)
    c: Block(g21)
    c: Block(g19)
    c: Block(g17)
    c: Distance(g20) = 1.61553
FEATURE [Part::Extrusion] Extrude044
  Base = -> Sketch053
  Dir = (0,0,1)
  DirMode = 2
  FaceMakerClass = Part::FaceMakerBullseye
  LengthFwd = 72
  LengthRev = 0
  Solid = true
  Symmetric = false
FEATURE [Part::Fillet] Fillet036  label="top018"
  Base = -> Extrude044
  Edges = 1 edges r=2: [Edge41]
FEATURE [Sketcher::SketchObject] Sketch054
  FullyConstrained = false
  Placement = pos=(0,0,0) rot=(1,0,0;1.5708rad)
  sketch-geometry (24):
    g0: ArcOfCircle CenterX=-4 CenterY=-10.5 CenterZ=0 NormalX=0 NormalY=0 NormalZ=1 AngleXU=0 Radius=1.5 StartAngle=6e-16 EndAngle=3.14159
    g1: ArcOfCircle CenterX=-34.2 CenterY=-10.5 CenterZ=0 NormalX=0 NormalY=0 NormalZ=1 AngleXU=0 Radius=1.5 StartAngle=0 EndAngle=3.14159
    g2: ArcOfCircle CenterX=-34.2 CenterY=-27.7 CenterZ=0 NormalX=0 NormalY=0 NormalZ=1 AngleXU=0 Radius=1.5 StartAngle=3.14159 EndAngle=6.28319
    g3: ArcOfCircle CenterX=-4 CenterY=-27.7 CenterZ=0 NormalX=0 NormalY=0 NormalZ=1 AngleXU=0 Radius=1.5 StartAngle=3.1416 EndAngle=6.28319
    g4: ArcOfCircle CenterX=-10 CenterY=-4.3 CenterZ=0 NormalX=0 NormalY=0 NormalZ=1 AngleXU=0 Radius=1.5 StartAngle=2e-16 EndAngle=3.14159
    g5: ArcOfCircle CenterX=-16.1 CenterY=-1.8 CenterZ=0 NormalX=0 NormalY=0 NormalZ=1 AngleXU=0 Radius=1.5 StartAngle=5e-16 EndAngle=3.14159
    g6: ArcOfCircle CenterX=-22.1 CenterY=-1.8 CenterZ=0 NormalX=0 NormalY=0 NormalZ=1 AngleXU=0 Radius=1.5 StartAngle=5e-16 EndAngle=3.14159
    g7: ArcOfCircle CenterX=-28.2 CenterY=-4.3 CenterZ=0 NormalX=0 NormalY=0 NormalZ=1 AngleXU=0 Radius=1.5 StartAngle=2e-16 EndAngle=3.14159
    g8: ArcOfCircle CenterX=-10 CenterY=-33.9 CenterZ=0 NormalX=0 NormalY=0 NormalZ=1 AngleXU=0 Radius=1.5 StartAngle=3.14159 EndAngle=6.28319
    g9: ArcOfCircle CenterX=-16.1 CenterY=-36.4 CenterZ=0 NormalX=0 NormalY=0 NormalZ=1 AngleXU=0 Radius=1.5 StartAngle=3.14159 EndAngle=6.28319
    g10: ArcOfCircle CenterX=-22.1 CenterY=-36.4 CenterZ=0 NormalX=0 NormalY=0 NormalZ=1 AngleXU=0 Radius=1.5 StartAngle=3.14159 EndAngle=6.28319
    g11: ArcOfCircle CenterX=-28.2 CenterY=-33.9 CenterZ=0 NormalX=0 NormalY=0 NormalZ=1 AngleXU=0 Radius=1.5 StartAngle=3.14159 EndAngle=6.28319
    g12: LineSegment StartX=-35.7 StartY=-10.5 StartZ=0 EndX=-35.7 EndY=-27.7 EndZ=0
    g13: LineSegment StartX=-32.7 StartY=-10.5 StartZ=0 EndX=-32.7 EndY=-27.7 EndZ=0
    g14: LineSegment StartX=-29.7 StartY=-33.9 StartZ=0 EndX=-29.7 EndY=-4.3 EndZ=0
    g15: LineSegment StartX=-26.7 StartY=-33.9 StartZ=0 EndX=-26.7 EndY=-4.3 EndZ=0
    g16: LineSegment StartX=-2.5 StartY=-10.5 StartZ=0 EndX=-2.5 EndY=-27.7 EndZ=0
    g17: LineSegment StartX=-8.5 StartY=-4.3 StartZ=0 EndX=-8.5 EndY=-33.9 EndZ=0
    g18: LineSegment StartX=-5.5 StartY=-10.5 StartZ=0 EndX=-5.5 EndY=-27.7 EndZ=0
    g19: LineSegment StartX=-11.5 StartY=-4.3 StartZ=0 EndX=-11.5 EndY=-33.9 EndZ=0
    g20: LineSegment StartX=-14.6 StartY=-1.8 StartZ=0 EndX=-14.6 EndY=-36.4 EndZ=0
    g21: LineSegment StartX=-17.6 StartY=-1.8 StartZ=0 EndX=-17.6 EndY=-36.4 EndZ=0
    g22: LineSegment StartX=-20.6 StartY=-36.4 StartZ=0 EndX=-20.6 EndY=-1.8 EndZ=0
    g23: LineSegment StartX=-23.6 StartY=-1.8 StartZ=0 EndX=-23.6 EndY=-36.4 EndZ=0
  constraints (48):
    c: Block(g0)
    c: Block(g1)
    c: Block(g2)
    c: Block(g3)
    c: Block(g4)
    c: Block(g5)
    c: Block(g6)
    c: Block(g7)
    c: Block(g8)
    c: Block(g9)
    c: Block(g10)
    c: Block(g11)
    c: Coincident(g12,g1)
    c: Coincident(g12,g2)
    c: Vertical(g12)
    c: Coincident(g13,g1)
    c: Coincident(g13,g2)
    c: Vertical(g13)
    c: Coincident(g14,g11)
    c: Coincident(g14,g7)
    c: Vertical(g14)
    c: Coincident(g15,g11)
    c: Coincident(g15,g7)
    c: Vertical(g15)
    c: Coincident(g16,g0)
    c: Coincident(g16,g3)
    c: Vertical(g16)
    c: Coincident(g17,g4)
    c: Coincident(g17,g8)
    c: Vertical(g17)
    c: Coincident(g18,g0)
    c: Coincident(g18,g3)
    c: Vertical(g18)
    c: Coincident(g19,g4)
    c: Coincident(g19,g8)
    c: Vertical(g19)
    c: Coincident(g20,g5)
    c: Coincident(g20,g9)
    c: Vertical(g20)
    c: Coincident(g21,g5)
    c: Coincident(g21,g9)
    c: Vertical(g21)
    c: Coincident(g22,g10)
    c: Coincident(g22,g6)
    c: Vertical(g22)
    c: Coincident(g23,g6)
    c: Coincident(g23,g10)
    c: Vertical(g23)
FEATURE [Part::Extrusion] Extrude045  label="removeToCreateFanGrillHoles003"
  Base = -> Sketch054
  Dir = (0,-1,6e-16)
  DirMode = 2
  FaceMakerClass = Part::FaceMakerBullseye
  LengthFwd = 10
  LengthRev = 0
  Placement = pos=(65.4,44,54.82) rot=(0,0,1;0rad)
  Solid = true
  Symmetric = false
FEATURE [Part::Feature] Face105 .. Face108  x4 (patterned run collapsed; names and placements below)
  shape: bbox 3.5 x 17.8 x 2e-07 mm, 1 faces, 0 solids (baked)
FEATURE [Part::Revolution] Revolve113  label="removeToCreateScrewAndThreadedInsertHole041"
  Angle = 360
  Axis = (0,1,0)
  Base = (0,0,0)
  FaceMakerClass = Part::FaceMakerBullseye
  Placement = pos=(62.3,30.3,19.7) rot=(0,0,1;0rad)
  Solid = false
  Source = -> Face105
  Symmetric = false
FEATURE [Part::Revolution] Revolve114  label="removeToCreateScrewAndThreadedInsertHole042"
  Angle = 360
  Axis = (0,1,0)
  Base = (0,0,0)
  FaceMakerClass = Part::FaceMakerBullseye
  Placement = pos=(62.3,30.3,51.7) rot=(0,0,1;0rad)
  Solid = false
  Source = -> Face106
  Symmetric = false
FEATURE [Part::Revolution] Revolve115  label="removeToCreateScrewAndThreadedInsertHole043"
  Angle = 360
  Axis = (0,1,0)
  Base = (0,0,0)
  FaceMakerClass = Part::FaceMakerBullseye
  Placement = pos=(30.3,30.3,19.7) rot=(0,0,1;0rad)
  Solid = false
  Source = -> Face107
  Symmetric = false
FEATURE [Part::Revolution] Revolve116  label="removeToCreateScrewAndThreadedInsertHole044"
  Angle = 360
  Axis = (0,1,0)
  Base = (0,0,0)
  FaceMakerClass = Part::FaceMakerBullseye
  Placement = pos=(30.3,30.3,51.7) rot=(0,0,1;0rad)
  Solid = false
  Source = -> Face108
  Symmetric = false
FEATURE [Part::MultiFuse] Fusion083  label="createThreadedInsertHolesForFan004"
  Shapes = -> [Revolve113,Revolve114,Revolve115,Revolve116]
FEATURE [Part::Box] Box024  label="removeToCreteHoleForPlugHousing026"
  AttacherType = Attacher::AttachEngine3D
  Height = 28.6
  Length = 10
  Placement = pos=(-2,0,21.7) rot=(0,0,1;0rad)
  Width = 19
FEATURE [Part::Cylinder] Cylinder038  label="removeToCreteHoleForPlugHousing027"
  Angle = 360
  AttacherType = Attacher::AttachEngine3D
  Height = 20
  Placement = pos=(-2,19,36) rot=(0,1,0;1.5708rad)
  Radius = 14.3
FEATURE [Part::MultiFuse] Fusion084  label="removeToCreteHoleForPlugHousing028"
  Shapes = -> [Box024,Cylinder038]
FEATURE [Part::Cylinder] Cylinder039
  Angle = 360
  AttacherType = Attacher::AttachEngine3D
  Height = 20
  Placement = pos=(0,0,36.15) rot=(0,0,1;0rad)
  Radius = 14.3
FEATURE [Part::Cylinder] Cylinder040
  Angle = 360
  AttacherType = Attacher::AttachEngine3D
  Height = 10
  Placement = pos=(0,0,36.15) rot=(0,0,1;0rad)
  Radius = 4
FEATURE [Part::Box] Box025  label="removeToCreteHoleForPlugHousing030"
  AttacherType = Attacher::AttachEngine3D
  Height = 28.6
  Length = 20
  Placement = pos=(106.15,0,21.7) rot=(0,0,1;0rad)
  Width = 19
FEATURE [Part::MultiFuse] Fusion086  label="removeToCreteHoleForPlugHousing031"
  Placement = pos=(70,19,36) rot=(0,1,0;1.5708rad)
  Shapes = -> [Cylinder039,Cylinder040]
FEATURE [Part::MultiFuse] Fusion085  label="removeToCreteHoleForPlugHousing029"
  Shapes = -> [Box025,Fusion086]
FEATURE [Sketcher::SketchObject] Sketch055
  FullyConstrained = true
  Placement = pos=(117,19,0) rot=(0.57735,0.57735,0.57735;2.0944rad)
  sketch-geometry (48):
    g0: LineSegment StartX=-49.19 StartY=69.25 StartZ=0 EndX=-49.19 EndY=66.25 EndZ=0
    g1: LineSegment StartX=-49.19 StartY=63.5 StartZ=0 EndX=-49.19 EndY=60.5 EndZ=0
    g2: LineSegment StartX=-49.19 StartY=57.75 StartZ=0 EndX=-49.19 EndY=54.75 EndZ=0
    g3: LineSegment StartX=-49.19 StartY=52 StartZ=0 EndX=-49.19 EndY=49 EndZ=0
    g4: LineSegment StartX=-49.19 StartY=46.25 StartZ=0 EndX=-49.19 EndY=43.25 EndZ=0
    g5: LineSegment StartX=-49.19 StartY=40.5 StartZ=0 EndX=-49.19 EndY=37.5 EndZ=0
    g6: LineSegment StartX=-49.19 StartY=34.5 StartZ=0 EndX=-49.19 EndY=31.5 EndZ=0
    g7: LineSegment StartX=-49.19 StartY=28.75 StartZ=0 EndX=-49.19 EndY=25.75 EndZ=0
    g8: LineSegment StartX=-49.19 StartY=23 StartZ=0 EndX=-49.19 EndY=20 EndZ=0
    g9: LineSegment StartX=-49.19 StartY=17.25 StartZ=0 EndX=-49.19 EndY=14.25 EndZ=0
    g10: LineSegment StartX=-49.19 StartY=11.5 StartZ=0 EndX=-49.19 EndY=8.5 EndZ=0
    g11: LineSegment StartX=-49.19 StartY=5.75 StartZ=0 EndX=-49.19 EndY=2.75 EndZ=0
    g12: ArcOfCircle CenterX=-1.5 CenterY=67.75 CenterZ=0 NormalX=0 NormalY=0 NormalZ=1 AngleXU=0 Radius=1.5 StartAngle=4.71239 EndAngle=7.85398
    g13: ArcOfCircle CenterX=-1.5 CenterY=62 CenterZ=0 NormalX=0 NormalY=0 NormalZ=1 AngleXU=0 Radius=1.5 StartAngle=4.71239 EndAngle=7.85398
    g14: ArcOfCircle CenterX=-1.5 CenterY=56.25 CenterZ=0 NormalX=0 NormalY=0 NormalZ=1 AngleXU=0 Radius=1.5 StartAngle=4.71239 EndAngle=7.85398
    g15: ArcOfCircle CenterX=-11.49 CenterY=50.5 CenterZ=0 NormalX=0 NormalY=0 NormalZ=1 AngleXU=0 Radius=1.5 StartAngle=4.71239 EndAngle=7.85398
    g16: ArcOfCircle CenterX=-16.28 CenterY=44.75 CenterZ=0 NormalX=0 NormalY=0 NormalZ=1 AngleXU=0 Radius=1.5 StartAngle=4.71239 EndAngle=7.85398
    g17: ArcOfCircle CenterX=-18.2337 CenterY=39 CenterZ=0 NormalX=0 NormalY=0 NormalZ=1 AngleXU=0 Radius=1.5 StartAngle=4.71485 EndAngle=7.85398
    g18: ArcOfCircle CenterX=-16.2837 CenterY=27.25 CenterZ=0 NormalX=0 NormalY=0 NormalZ=1 AngleXU=0 Radius=1.5 StartAngle=4.71485 EndAngle=7.85398
    g19: ArcOfCircle CenterX=-18.2337 CenterY=33 CenterZ=0 NormalX=0 NormalY=0 NormalZ=1 AngleXU=0 Radius=1.5 StartAngle=4.71485 EndAngle=7.85398
    g20: ArcOfCircle CenterX=-11.49 CenterY=21.5 CenterZ=0 NormalX=0 NormalY=0 NormalZ=1 AngleXU=0 Radius=1.5 StartAngle=4.71239 EndAngle=7.85398
    g21: ArcOfCircle CenterX=-1.5 CenterY=4.25 CenterZ=0 NormalX=0 NormalY=0 NormalZ=1 AngleXU=0 Radius=1.5 StartAngle=4.71239 EndAngle=7.85398
    g22: ArcOfCircle CenterX=-1.5 CenterY=10 CenterZ=0 NormalX=0 NormalY=0 NormalZ=1 AngleXU=0 Radius=1.5 StartAngle=4.71239 EndAngle=7.85398
    g23: ArcOfCircle CenterX=-1.5 CenterY=15.75 CenterZ=0 NormalX=0 NormalY=0 NormalZ=1 AngleXU=0 Radius=1.5 StartAngle=4.71239 EndAngle=7.85398
    g24: LineSegment StartX=-49.19 StartY=69.25 StartZ=0 EndX=-1.5 EndY=69.25 EndZ=0
    g25: LineSegment StartX=-49.19 StartY=66.25 StartZ=0 EndX=-1.5 EndY=66.25 EndZ=0
    g26: LineSegment StartX=-49.19 StartY=63.5 StartZ=0 EndX=-1.5 EndY=63.5 EndZ=0
    g27: LineSegment StartX=-49.19 StartY=60.5 StartZ=0 EndX=-1.5 EndY=60.5 EndZ=0
    g28: LineSegment StartX=-49.19 StartY=57.75 StartZ=0 EndX=-1.5 EndY=57.75 EndZ=0
    g29: LineSegment StartX=-49.19 StartY=54.75 StartZ=0 EndX=-1.5 EndY=54.75 EndZ=0
    g30: LineSegment StartX=-49.19 StartY=52 StartZ=0 EndX=-11.49 EndY=52 EndZ=0
    g31: LineSegment StartX=-49.19 StartY=49 StartZ=0 EndX=-11.49 EndY=49 EndZ=0
    g32: LineSegment StartX=-49.19 StartY=46.25 StartZ=0 EndX=-16.28 EndY=46.25 EndZ=0
    g33: LineSegment StartX=-49.19 StartY=43.25 StartZ=0 EndX=-16.28 EndY=43.25 EndZ=0
    g34: LineSegment StartX=-49.19 StartY=40.5 StartZ=0 EndX=-18.2337 EndY=40.5 EndZ=0
    g35: LineSegment StartX=-49.19 StartY=37.5 StartZ=0 EndX=-18.23 EndY=37.5 EndZ=0
    g36: LineSegment StartX=-49.19 StartY=34.5 StartZ=0 EndX=-18.2337 EndY=34.5 EndZ=0
    g37: LineSegment StartX=-49.19 StartY=31.5 StartZ=0 EndX=-18.23 EndY=31.5 EndZ=0
    g38: LineSegment StartX=-49.19 StartY=28.75 StartZ=0 EndX=-16.2837 EndY=28.75 EndZ=0
    g39: LineSegment StartX=-49.19 StartY=25.75 StartZ=0 EndX=-16.28 EndY=25.75 EndZ=0
    g40: LineSegment StartX=-49.19 StartY=23 StartZ=0 EndX=-11.49 EndY=23 EndZ=0
    g41: LineSegment StartX=-49.19 StartY=20 StartZ=0 EndX=-11.49 EndY=20 EndZ=0
    g42: LineSegment StartX=-49.19 StartY=17.25 StartZ=0 EndX=-1.5 EndY=17.25 EndZ=0
    g43: LineSegment StartX=-49.19 StartY=14.25 StartZ=0 EndX=-1.5 EndY=14.25 EndZ=0
    g44: LineSegment StartX=-49.19 StartY=11.5 StartZ=0 EndX=-1.5 EndY=11.5 EndZ=0
    g45: LineSegment StartX=-49.19 StartY=8.5 StartZ=0 EndX=-1.5 EndY=8.5 EndZ=0
    g46: LineSegment StartX=-49.19 StartY=5.75 StartZ=0 EndX=-1.5 EndY=5.75 EndZ=0
    g47: LineSegment StartX=-49.19 StartY=2.75 StartZ=0 EndX=-1.5 EndY=2.75 EndZ=0
  constraints (120):
    c: Vertical(g0)
    c: Distance(g0) = 3
    c: Block(g0)
    c: Vertical(g1)
    c: Distance(g1) = 3
    c: Vertical(g2)
    c: Equal(g0,g2) = 3
    c: Block(g2)
    c: Vertical(g3)
    c: Equal(g1,g3) = 3
    c: Vertical(g4)
    c: Equal(g0,g4) = 3
    c: Block(g4)
    c: Vertical(g5)
    c: Equal(g1,g5) = 3
    c: Vertical(g6)
    c: Equal(g0,g6) = 3
    c: Block(g6)
    c: Vertical(g7)
    c: Equal(g1,g7) = 3
    c: Vertical(g8)
    c: Equal(g0,g8) = 3
    c: Block(g8)
    c: Vertical(g9)
    c: Equal(g1,g9) = 3
    c: Vertical(g10)
    c: Equal(g0,g10) = 3
    c: Block(g10)
    c: Vertical(g11)
    c: Equal(g1,g11) = 3
    c: Block(g12)
    c: Block(g13)
    c: Block(g14)
    c: Block(g15)
    c: Block(g16)
    c: Block(g17)
    c: Block(g18)
    c: Block(g19)
    c: Block(g20)
    c: Block(g21)
    c: Block(g22)
    c: Block(g23)
    c: Block(g11)
    c: Block(g9)
    c: Block(g7)
    c: Block(g5)
    c: Block(g3)
    c: Block(g1)
    c: Coincident(g24,g0)
    c: Coincident(g24,g12)
    c: Horizontal(g24)
    c: Coincident(g25,g0)
    c: Coincident(g25,g12)
    c: Horizontal(g25)
    c: Coincident(g26,g1)
    c: Coincident(g26,g13)
    c: Horizontal(g26)
    c: Coincident(g27,g1)
    c: Coincident(g27,g13)
    c: Horizontal(g27)
    c: Coincident(g28,g2)
    c: Coincident(g28,g14)
    c: Horizontal(g28)
    c: Coincident(g29,g2)
    c: Coincident(g29,g14)
    c: Horizontal(g29)
    c: Coincident(g30,g3)
    c: Coincident(g30,g15)
    c: Horizontal(g30)
    c: Coincident(g31,g3)
    c: Coincident(g31,g15)
    c: Horizontal(g31)
    c: Coincident(g32,g4)
    c: Coincident(g32,g16)
    c: Horizontal(g32)
    c: Coincident(g33,g4)
    c: Coincident(g33,g16)
    c: Horizontal(g33)
    c: Coincident(g34,g5)
    c: Coincident(g34,g17)
    c: Horizontal(g34)
    c: Coincident(g35,g5)
    c: Coincident(g35,g17)
    c: Horizontal(g35)
    c: Coincident(g36,g6)
    c: Coincident(g36,g19)
    c: Horizontal(g36)
    c: Coincident(g37,g6)
    c: Coincident(g37,g19)
    c: Horizontal(g37)
    c: Coincident(g38,g7)
    c: Coincident(g38,g18)
    c: Horizontal(g38)
    c: Coincident(g39,g7)
    c: Coincident(g39,g18)
    c: Horizontal(g39)
    c: Coincident(g40,g8)
    c: Coincident(g40,g20)
    c: Horizontal(g40)
    c: Coincident(g41,g8)
    c: Coincident(g41,g20)
    c: Horizontal(g41)
    c: Coincident(g42,g9)
    c: Coincident(g42,g23)
    c: Horizontal(g42)
    c: Coincident(g43,g9)
    c: Coincident(g43,g23)
    c: Horizontal(g43)
    c: Coincident(g44,g10)
    c: Coincident(g44,g22)
    c: Horizontal(g44)
    c: Coincident(g45,g10)
    c: Coincident(g45,g22)
    c: Horizontal(g45)
    c: Coincident(g46,g11)
    c: Coincident(g46,g21)
    c: Horizontal(g46)
    c: Coincident(g47,g11)
    c: Coincident(g47,g21)
    c: Horizontal(g47)
FEATURE [Part::Extrusion] Extrude046
  Base = -> Sketch055
  Dir = (1,0,0)
  DirMode = 2
  FaceMakerClass = Part::FaceMakerBullseye
  LengthFwd = 23
  LengthRev = 0
  Placement = pos=(-19,0,0) rot=(0,0,1;0rad)
  Solid = true
  Symmetric = false
FEATURE [Part::Fillet] Fillet038  label="removeToCreateVentalationHoles001"
  Base = -> Extrude046
  Edges = <same value as first occurrence — deduplicated (x6 in doc)>
  Placement = pos=(7,0,0) rot=(0,0,1;0rad)
FEATURE [Sketcher::SketchObject] Sketch056  label="topSketch014"
  FullyConstrained = true
  sketch-geometry (22):
    g0: LineSegment StartX=5.21097e-06 StartY=3 StartZ=0 EndX=5.21097e-06 EndY=19 EndZ=0
    g1: ArcOfCircle CenterX=19 CenterY=19 CenterZ=0 NormalX=0 NormalY=0 NormalZ=1 AngleXU=0 Radius=19 StartAngle=1.5708 EndAngle=3.14159
    g2: ArcOfCircle CenterX=19 CenterY=19 CenterZ=0 NormalX=0 NormalY=0 NormalZ=1 AngleXU=0 Radius=16 StartAngle=1.5708 EndAngle=3.14159
    g3: LineSegment StartX=114 StartY=35 StartZ=0 EndX=19 EndY=35 EndZ=0
    g4: LineSegment StartX=5.21097e-06 StartY=3 StartZ=0 EndX=5.21097e-06 EndY=0 EndZ=0
    g5: LineSegment StartX=3 StartY=0 StartZ=0 EndX=5.21097e-06 EndY=0 EndZ=0
    g6: LineSegment StartX=3 StartY=19 StartZ=0 EndX=3 EndY=0 EndZ=0
    g7: LineSegment StartX=19 StartY=38 StartZ=0 EndX=124 EndY=38 EndZ=0
    g8: Circle CenterX=119 CenterY=35 CenterZ=0 NormalX=0 NormalY=0 NormalZ=1 AngleXU=0 Radius=1
    g9: Circle CenterX=121 CenterY=35 CenterZ=0 NormalX=0 NormalY=0 NormalZ=1 AngleXU=0 Radius=1
    g10: Circle CenterX=121 CenterY=33 CenterZ=0 NormalX=0 NormalY=0 NormalZ=1 AngleXU=0 Radius=1
    g11: BSplineCurve PolesCount=3 KnotsCount=2 Degree=2 IsPeriodic=0
    g12: GeomPoint X=119 Y=35 Z=0
    g13: GeomPoint X=121 Y=33 Z=0
    g14: LineSegment StartX=119 StartY=35 StartZ=0 EndX=114 EndY=35 EndZ=0
    g15: ArcOfCircle CenterX=105 CenterY=19 CenterZ=0 NormalX=0 NormalY=0 NormalZ=1 AngleXU=0 Radius=16 StartAngle=5.60905 EndAngle=6.28319
    g16: LineSegment StartX=121 StartY=33 StartZ=0 EndX=121 EndY=19 EndZ=0
    g17: LineSegment StartX=117.5 StartY=9.01251 StartZ=0 EndX=121.163 EndY=9.0125 EndZ=0
    g18: ArcOfCircle CenterX=105 CenterY=19 CenterZ=0 NormalX=0 NormalY=0 NormalZ=1 AngleXU=0 Radius=20.6155 StartAngle=5.7297 EndAngle=6.28319
    g19: LineSegment StartX=121.163 StartY=9.0125 StartZ=0 EndX=122.538 EndY=8.16329 EndZ=0
    g20: LineSegment StartX=124 StartY=38 StartZ=0 EndX=125.616 EndY=38 EndZ=0
    g21: LineSegment StartX=125.616 StartY=19 StartZ=0 EndX=125.616 EndY=38 EndZ=0
  constraints (49):
    c: Vertical(g0)
    c: Block(g0)
    c: Coincident(g1,g0)
    c: Block(g1)
    c: Coincident(g2,g1)
    c: Block(g2)
    c: Coincident(g3,g2)
    c: Horizontal(g3)
    c: Tangent(g3,g2)
    c: Coincident(g4,g0)
    c: Distance(g4) = 3
    c: Vertical(g4)
    c: Coincident(g5,g4)
    c: Horizontal(g5)
    c: Coincident(g6,g2)
    c: Coincident(g6,g5)
    c: Vertical(g6)
    c: Horizontal(g7)
    c: Distance(g7) = 105
    c: Coincident(g7,g1)
    c: Block(g3)
    c: Weight(g8) = 1
    c: Equal(g8,g9)
    c: Equal(g8,g10)
    c: InternalAlignment(g8,g11)
    c: InternalAlignment(g9,g11)
    c: InternalAlignment(g10,g11)
    c: InternalAlignment(g12,g11)
    c: InternalAlignment(g13,g11)
    c: Block(g11)
    c: Coincident(g14,g11)
    c: Coincident(g14,g3)
    c: Horizontal(g14)
    c: Block(g15)
    c: Coincident(g16,g11)
    c: Coincident(g16,g15)
    c: Vertical(g16)
    c: Distance(g16) = 14
    c: Coincident(g17,g15)
    c: Block(g18)
    c: Coincident(g19,g18)
    c: Coincident(g20,g7)
    c: Horizontal(g20)
    c: Vertical(g21)
    c: Coincident(g20,g21)
    c: Block(g20)
    c: Block(g21)
    c: Block(g19)
    c: Block(g17)
FEATURE [Part::Box] Box026  label="removeToCreteHoleForPlugHousing032"
  AttacherType = Attacher::AttachEngine3D
  Height = 28.6
  Length = 10
  Placement = pos=(-2,0,21.7) rot=(0,0,1;0rad)
  Width = 19
FEATURE [Part::Feature] Face109 .. Face112  x4 (patterned run collapsed; names and placements below)
  shape: bbox 3.5 x 17.8 x 2e-07 mm, 1 faces, 0 solids (baked)
FEATURE [Part::Revolution] Revolve117  label="removeToCreateScrewAndThreadedInsertHole045"
  Angle = 360
  Axis = (0,1,0)
  Base = (0,0,0)
  FaceMakerClass = Part::FaceMakerBullseye
  Placement = pos=(62.3,30.3,19.7) rot=(0,0,1;0rad)
  Solid = false
  Source = -> Face109
  Symmetric = false
FEATURE [Part::Revolution] Revolve118  label="removeToCreateScrewAndThreadedInsertHole046"
  Angle = 360
  Axis = (0,1,0)
  Base = (0,0,0)
  FaceMakerClass = Part::FaceMakerBullseye
  Placement = pos=(62.3,30.3,51.7) rot=(0,0,1;0rad)
  Solid = false
  Source = -> Face110
  Symmetric = false
FEATURE [Part::Revolution] Revolve119  label="removeToCreateScrewAndThreadedInsertHole047"
  Angle = 360
  Axis = (0,1,0)
  Base = (0,0,0)
  FaceMakerClass = Part::FaceMakerBullseye
  Placement = pos=(30.3,30.3,19.7) rot=(0,0,1;0rad)
  Solid = false
  Source = -> Face111
  Symmetric = false
FEATURE [Part::Revolution] Revolve120  label="removeToCreateScrewAndThreadedInsertHole048"
  Angle = 360
  Axis = (0,1,0)
  Base = (0,0,0)
  FaceMakerClass = Part::FaceMakerBullseye
  Placement = pos=(30.3,30.3,51.7) rot=(0,0,1;0rad)
  Solid = false
  Source = -> Face112
  Symmetric = false
FEATURE [Part::MultiFuse] Fusion087  label="createThreadedInsertHolesForFan005"
  Shapes = -> [Revolve117,Revolve118,Revolve119,Revolve120]
FEATURE [Part::Extrusion] Extrude047
  Base = -> Sketch056
  Dir = (0,0,1)
  DirMode = 2
  FaceMakerClass = Part::FaceMakerBullseye
  LengthFwd = 72
  LengthRev = 0
  Solid = true
  Symmetric = false
FEATURE [Part::Fillet] Fillet039  label="top019"
  Base = -> Extrude047
  Edges = 1 edges r=2: [Edge35]
FEATURE [Sketcher::SketchObject] Sketch057
  FullyConstrained = false
  Placement = pos=(0,0,0) rot=(1,0,0;1.5708rad)
  sketch-geometry (24):
    g0: ArcOfCircle CenterX=-4 CenterY=-10.5 CenterZ=0 NormalX=0 NormalY=0 NormalZ=1 AngleXU=0 Radius=1.5 StartAngle=6e-16 EndAngle=3.14159
    g1: ArcOfCircle CenterX=-34.2 CenterY=-10.5 CenterZ=0 NormalX=0 NormalY=0 NormalZ=1 AngleXU=0 Radius=1.5 StartAngle=0 EndAngle=3.14159
    g2: ArcOfCircle CenterX=-34.2 CenterY=-27.7 CenterZ=0 NormalX=0 NormalY=0 NormalZ=1 AngleXU=0 Radius=1.5 StartAngle=3.14159 EndAngle=6.28319
    g3: ArcOfCircle CenterX=-4 CenterY=-27.7 CenterZ=0 NormalX=0 NormalY=0 NormalZ=1 AngleXU=0 Radius=1.5 StartAngle=3.1416 EndAngle=6.28319
    g4: ArcOfCircle CenterX=-10 CenterY=-4.3 CenterZ=0 NormalX=0 NormalY=0 NormalZ=1 AngleXU=0 Radius=1.5 StartAngle=2e-16 EndAngle=3.14159
    g5: ArcOfCircle CenterX=-16.1 CenterY=-1.8 CenterZ=0 NormalX=0 NormalY=0 NormalZ=1 AngleXU=0 Radius=1.5 StartAngle=5e-16 EndAngle=3.14159
    g6: ArcOfCircle CenterX=-22.1 CenterY=-1.8 CenterZ=0 NormalX=0 NormalY=0 NormalZ=1 AngleXU=0 Radius=1.5 StartAngle=5e-16 EndAngle=3.14159
    g7: ArcOfCircle CenterX=-28.2 CenterY=-4.3 CenterZ=0 NormalX=0 NormalY=0 NormalZ=1 AngleXU=0 Radius=1.5 StartAngle=2e-16 EndAngle=3.14159
    g8: ArcOfCircle CenterX=-10 CenterY=-33.9 CenterZ=0 NormalX=0 NormalY=0 NormalZ=1 AngleXU=0 Radius=1.5 StartAngle=3.14159 EndAngle=6.28319
    g9: ArcOfCircle CenterX=-16.1 CenterY=-36.4 CenterZ=0 NormalX=0 NormalY=0 NormalZ=1 AngleXU=0 Radius=1.5 StartAngle=3.14159 EndAngle=6.28319
    g10: ArcOfCircle CenterX=-22.1 CenterY=-36.4 CenterZ=0 NormalX=0 NormalY=0 NormalZ=1 AngleXU=0 Radius=1.5 StartAngle=3.14159 EndAngle=6.28319
    g11: ArcOfCircle CenterX=-28.2 CenterY=-33.9 CenterZ=0 NormalX=0 NormalY=0 NormalZ=1 AngleXU=0 Radius=1.5 StartAngle=3.14159 EndAngle=6.28319
    g12: LineSegment StartX=-35.7 StartY=-10.5 StartZ=0 EndX=-35.7 EndY=-27.7 EndZ=0
    g13: LineSegment StartX=-32.7 StartY=-10.5 StartZ=0 EndX=-32.7 EndY=-27.7 EndZ=0
    g14: LineSegment StartX=-29.7 StartY=-33.9 StartZ=0 EndX=-29.7 EndY=-4.3 EndZ=0
    g15: LineSegment StartX=-26.7 StartY=-33.9 StartZ=0 EndX=-26.7 EndY=-4.3 EndZ=0
    g16: LineSegment StartX=-2.5 StartY=-10.5 StartZ=0 EndX=-2.5 EndY=-27.7 EndZ=0
    g17: LineSegment StartX=-8.5 StartY=-4.3 StartZ=0 EndX=-8.5 EndY=-33.9 EndZ=0
    g18: LineSegment StartX=-5.5 StartY=-10.5 StartZ=0 EndX=-5.5 EndY=-27.7 EndZ=0
    g19: LineSegment StartX=-11.5 StartY=-4.3 StartZ=0 EndX=-11.5 EndY=-33.9 EndZ=0
    g20: LineSegment StartX=-14.6 StartY=-1.8 StartZ=0 EndX=-14.6 EndY=-36.4 EndZ=0
    g21: LineSegment StartX=-17.6 StartY=-1.8 StartZ=0 EndX=-17.6 EndY=-36.4 EndZ=0
    g22: LineSegment StartX=-20.6 StartY=-36.4 StartZ=0 EndX=-20.6 EndY=-1.8 EndZ=0
    g23: LineSegment StartX=-23.6 StartY=-1.8 StartZ=0 EndX=-23.6 EndY=-36.4 EndZ=0
  constraints (48):
    c: Block(g0)
    c: Block(g1)
    c: Block(g2)
    c: Block(g3)
    c: Block(g4)
    c: Block(g5)
    c: Block(g6)
    c: Block(g7)
    c: Block(g8)
    c: Block(g9)
    c: Block(g10)
    c: Block(g11)
    c: Coincident(g12,g1)
    c: Coincident(g12,g2)
    c: Vertical(g12)
    c: Coincident(g13,g1)
    c: Coincident(g13,g2)
    c: Vertical(g13)
    c: Coincident(g14,g11)
    c: Coincident(g14,g7)
    c: Vertical(g14)
    c: Coincident(g15,g11)
    c: Coincident(g15,g7)
    c: Vertical(g15)
    c: Coincident(g16,g0)
    c: Coincident(g16,g3)
    c: Vertical(g16)
    c: Coincident(g17,g4)
    c: Coincident(g17,g8)
    c: Vertical(g17)
    c: Coincident(g18,g0)
    c: Coincident(g18,g3)
    c: Vertical(g18)
    c: Coincident(g19,g4)
    c: Coincident(g19,g8)
    c: Vertical(g19)
    c: Coincident(g20,g5)
    c: Coincident(g20,g9)
    c: Vertical(g20)
    c: Coincident(g21,g5)
    c: Coincident(g21,g9)
    c: Vertical(g21)
    c: Coincident(g22,g10)
    c: Coincident(g22,g6)
    c: Vertical(g22)
    c: Coincident(g23,g6)
    c: Coincident(g23,g10)
    c: Vertical(g23)
FEATURE [Part::Extrusion] Extrude048  label="removeToCreateFanGrillHoles004"
  Base = -> Sketch057
  Dir = (0,-1,6e-16)
  DirMode = 2
  FaceMakerClass = Part::FaceMakerBullseye
  LengthFwd = 10
  LengthRev = 0
  Placement = pos=(65.4,44,54.82) rot=(0,0,1;0rad)
  Solid = true
  Symmetric = false
FEATURE [Part::Cut] Cut040  label="top021"
  Base = -> Fillet039
  Tool = -> Extrude048
FEATURE [Part::Cylinder] Cylinder041  label="removeToCreteHoleForPlugHousing034"
  Angle = 360
  AttacherType = Attacher::AttachEngine3D
  Height = 20
  Placement = pos=(-2,19,36) rot=(0,1,0;1.5708rad)
  Radius = 14.3
FEATURE [Part::MultiFuse] Fusion089  label="removeToCreteHoleForPlugHousing035"
  Shapes = -> [Box026,Cylinder041]
FEATURE [Part::Cylinder] Cylinder042
  Angle = 360
  AttacherType = Attacher::AttachEngine3D
  Height = 20
  Placement = pos=(0,0,36.15) rot=(0,0,1;0rad)
  Radius = 14.3
FEATURE [Part::Cylinder] Cylinder043
  Angle = 360
  AttacherType = Attacher::AttachEngine3D
  Height = 10
  Placement = pos=(0,0,36.15) rot=(0,0,1;0rad)
  Radius = 4
FEATURE [Part::Box] Box027  label="removeToCreteHoleForPlugHousing036"
  AttacherType = Attacher::AttachEngine3D
  Height = 28.6
  Length = 20
  Placement = pos=(106.15,0,21.7) rot=(0,0,1;0rad)
  Width = 19
FEATURE [Part::Cut] Cut041  label="top022"
  Base = -> Cut040
  Tool = -> Fusion087
FEATURE [Part::Cut] Cut039  label="top020"
  Base = -> Cut041
  Tool = -> Fusion089
FEATURE [Part::MultiFuse] Fusion090  label="removeToCreteHoleForPlugHousing037"
  Placement = pos=(70,19,36) rot=(0,1,0;1.5708rad)
  Shapes = -> [Cylinder042,Cylinder043]
FEATURE [Part::MultiFuse] Fusion088  label="removeToCreteHoleForPlugHousing033"
  Shapes = -> [Box027,Fusion090]
FEATURE [Part::Cut] Cut042  label="removeToCreteHoleForPlugHousing038"
  Base = -> Cut039
  Tool = -> Fusion088
FEATURE [Part::MultiFuse] Fusion091  label="removeFromTop"
  Shapes = -> [Fillet038,Fusion085,Fusion084,Fusion083,Extrude045]
FEATURE [Part::Cut] Cut043  label="REAL TOP ====="
  Base = -> Fillet036
  Tool = -> Fusion091
FEATURE [Part::MultiFuse] Fusion092  label="caseScrewPillarBracket016"
  Shapes = -> [Extrude030,Extrude031,Extrude032,Extrude033,Extrude034,Extrude035,Extrude036,Extrude037,Box013,Box014]
FEATURE [Sketcher::SketchObject] Sketch058  label="topSketch015"
  FullyConstrained = true
  sketch-geometry (20):
    g0: LineSegment StartX=5.21097e-06 StartY=3 StartZ=0 EndX=5.21097e-06 EndY=19 EndZ=0
    g1: ArcOfCircle CenterX=19 CenterY=19 CenterZ=0 NormalX=0 NormalY=0 NormalZ=1 AngleXU=0 Radius=19 StartAngle=1.5708 EndAngle=3.14159
    g2: ArcOfCircle CenterX=19 CenterY=19 CenterZ=0 NormalX=0 NormalY=0 NormalZ=1 AngleXU=0 Radius=16 StartAngle=1.5708 EndAngle=3.14159
    g3: LineSegment StartX=114 StartY=35 StartZ=0 EndX=19 EndY=35 EndZ=0
    g4: LineSegment StartX=5.21097e-06 StartY=3 StartZ=0 EndX=5.21097e-06 EndY=0 EndZ=0
    g5: LineSegment StartX=3 StartY=0 StartZ=0 EndX=5.21097e-06 EndY=0 EndZ=0
    g6: LineSegment StartX=3 StartY=19 StartZ=0 EndX=3 EndY=0 EndZ=0
    g7: LineSegment StartX=19 StartY=38 StartZ=0 EndX=124 EndY=38 EndZ=0
    g8: Circle CenterX=119 CenterY=35 CenterZ=0 NormalX=0 NormalY=0 NormalZ=1 AngleXU=0 Radius=1
    g9: Circle CenterX=121 CenterY=35 CenterZ=0 NormalX=0 NormalY=0 NormalZ=1 AngleXU=0 Radius=1
    g10: Circle CenterX=121 CenterY=33 CenterZ=0 NormalX=0 NormalY=0 NormalZ=1 AngleXU=0 Radius=1
    g11: BSplineCurve PolesCount=3 KnotsCount=2 Degree=2 IsPeriodic=0
    g12: GeomPoint X=119 Y=35 Z=0
    g13: GeomPoint X=121 Y=33 Z=0
    g14: LineSegment StartX=119 StartY=35 StartZ=0 EndX=114 EndY=35 EndZ=0
    g15: ArcOfCircle CenterX=105 CenterY=19 CenterZ=0 NormalX=0 NormalY=0 NormalZ=1 AngleXU=0 Radius=19 StartAngle=5.7297 EndAngle=6.28319
    g16: ArcOfCircle CenterX=105 CenterY=19 CenterZ=0 NormalX=0 NormalY=0 NormalZ=1 AngleXU=0 Radius=16 StartAngle=5.60905 EndAngle=6.28319
    g17: LineSegment StartX=121 StartY=33 StartZ=0 EndX=121 EndY=19 EndZ=0
    g18: LineSegment StartX=124 StartY=38 StartZ=0 EndX=124 EndY=19 EndZ=0
    g19: LineSegment StartX=117.5 StartY=9.01251 StartZ=0 EndX=121.163 EndY=9.0125 EndZ=0
  constraints (46):
    c: Vertical(g0)
    c: Block(g0)
    c: Coincident(g1,g0)
    c: Block(g1)
    c: Coincident(g2,g1)
    c: Block(g2)
    c: Coincident(g3,g2)
    c: Horizontal(g3)
    c: Tangent(g3,g2)
    c: Coincident(g4,g0)
    c: Distance(g4) = 3
    c: Vertical(g4)
    c: Coincident(g5,g4)
    c: Horizontal(g5)
    c: Coincident(g6,g2)
    c: Coincident(g6,g5)
    c: Vertical(g6)
    c: Horizontal(g7)
    c: Distance(g7) = 105
    c: Coincident(g7,g1)
    c: Block(g3)
    c: Weight(g8) = 1
    c: Equal(g8,g9)
    c: Equal(g8,g10)
    c: InternalAlignment(g8,g11)
    c: InternalAlignment(g9,g11)
    c: InternalAlignment(g10,g11)
    c: InternalAlignment(g12,g11)
    c: InternalAlignment(g13,g11)
    c: Block(g11)
    c: Coincident(g14,g11)
    c: Coincident(g14,g3)
    c: Horizontal(g14)
    c: Block(g15)
    c: Coincident(g16,g15)
    c: Block(g16)
    c: Coincident(g17,g11)
    c: Coincident(g17,g16)
    c: Vertical(g17)
    c: Distance(g17) = 14
    c: Coincident(g18,g7)
    c: Coincident(g18,g15)
    c: Vertical(g18)
    c: Distance(g18) = 19
    c: Coincident(g19,g16)
    c: Coincident(g19,g15)
FEATURE [Part::Extrusion] Extrude049  label="top023"
  Base = -> Sketch058
  Dir = (0,0,1)
  DirMode = 2
  FaceMakerClass = Part::FaceMakerBullseye
  LengthFwd = 72
  LengthRev = 0
  Solid = true
  Symmetric = false
FEATURE [Sketcher::SketchObject] Sketch059
  FullyConstrained = true
  MapMode = 3
  Placement = pos=(0,0,0) rot=(1,0,0;1.5708rad)
  Support = -> [Extrude049]
  sketch-geometry (8):
    g0: Circle CenterX=80.351 CenterY=-67.6202 CenterZ=0 NormalX=0 NormalY=0 NormalZ=1 AngleXU=0 Radius=2
    g1: Circle CenterX=80.351 CenterY=-67.6202 CenterZ=0 NormalX=0 NormalY=0 NormalZ=1 AngleXU=0 Radius=3
    g2: Circle CenterX=80.351 CenterY=-4.92017 CenterZ=0 NormalX=0 NormalY=0 NormalZ=1 AngleXU=0 Radius=2
    g3: Circle CenterX=80.351 CenterY=-4.92017 CenterZ=0 NormalX=0 NormalY=0 NormalZ=1 AngleXU=0 Radius=3
    g4: Circle CenterX=23.851 CenterY=-4.92017 CenterZ=0 NormalX=0 NormalY=0 NormalZ=1 AngleXU=0 Radius=2
    g5: Circle CenterX=23.851 CenterY=-4.92017 CenterZ=0 NormalX=0 NormalY=0 NormalZ=1 AngleXU=0 Radius=3
    g6: Circle CenterX=23.851 CenterY=-67.6202 CenterZ=0 NormalX=0 NormalY=0 NormalZ=1 AngleXU=0 Radius=2
    g7: Circle CenterX=23.851 CenterY=-67.6202 CenterZ=0 NormalX=0 NormalY=0 NormalZ=1 AngleXU=0 Radius=3
  constraints (8):
    c: Block(g3)
    c: Block(g2)
    c: Block(g1)
    c: Block(g0)
    c: Block(g6)
    c: Block(g7)
    c: Block(g4)
    c: Block(g5)
FEATURE [Sketcher::SketchObject] Sketch060
  FullyConstrained = true
  MapMode = 3
  Placement = pos=(0,0,0) rot=(1,0,0;1.5708rad)
  Support = -> [Extrude049]
  sketch-geometry (8):
    g0: Circle CenterX=80.351 CenterY=-67.6202 CenterZ=0 NormalX=0 NormalY=0 NormalZ=1 AngleXU=0 Radius=3
    g1: Circle CenterX=80.351 CenterY=-4.92017 CenterZ=0 NormalX=0 NormalY=0 NormalZ=1 AngleXU=0 Radius=3
    g2: Circle CenterX=23.851 CenterY=-4.92017 CenterZ=0 NormalX=0 NormalY=0 NormalZ=1 AngleXU=0 Radius=3
    g3: Circle CenterX=23.851 CenterY=-67.6202 CenterZ=0 NormalX=0 NormalY=0 NormalZ=1 AngleXU=0 Radius=3
    g4: Circle CenterX=23.851 CenterY=-67.6202 CenterZ=0 NormalX=0 NormalY=0 NormalZ=1 AngleXU=0 Radius=5
    g5: Circle CenterX=80.351 CenterY=-67.6202 CenterZ=0 NormalX=0 NormalY=0 NormalZ=1 AngleXU=0 Radius=5
    g6: Circle CenterX=23.851 CenterY=-4.92017 CenterZ=0 NormalX=0 NormalY=0 NormalZ=1 AngleXU=0 Radius=5
    g7: Circle CenterX=80.351 CenterY=-4.92017 CenterZ=0 NormalX=0 NormalY=0 NormalZ=1 AngleXU=0 Radius=5
  constraints (8):
    c: Block(g1)
    c: Block(g0)
    c: Block(g3)
    c: Block(g2)
    c: Block(g5)
    c: Block(g4)
    c: Block(g6)
    c: Block(g7)
FEATURE [Sketcher::SketchObject] Sketch061
  FullyConstrained = true
  MapMode = 3
  Placement = pos=(0,0,0) rot=(1,0,0;1.5708rad)
  sketch-geometry (8):
    g0: Circle CenterX=80.351 CenterY=-67.6202 CenterZ=0 NormalX=0 NormalY=0 NormalZ=1 AngleXU=0 Radius=3
    g1: Circle CenterX=80.351 CenterY=-4.92017 CenterZ=0 NormalX=0 NormalY=0 NormalZ=1 AngleXU=0 Radius=3
    g2: Circle CenterX=23.851 CenterY=-4.92017 CenterZ=0 NormalX=0 NormalY=0 NormalZ=1 AngleXU=0 Radius=3
    g3: Circle CenterX=23.851 CenterY=-67.6202 CenterZ=0 NormalX=0 NormalY=0 NormalZ=1 AngleXU=0 Radius=3
    g4: Circle CenterX=23.851 CenterY=-67.6202 CenterZ=0 NormalX=0 NormalY=0 NormalZ=1 AngleXU=0 Radius=5
    g5: Circle CenterX=80.351 CenterY=-67.6202 CenterZ=0 NormalX=0 NormalY=0 NormalZ=1 AngleXU=0 Radius=5
    g6: Circle CenterX=23.851 CenterY=-4.92017 CenterZ=0 NormalX=0 NormalY=0 NormalZ=1 AngleXU=0 Radius=5
    g7: Circle CenterX=80.351 CenterY=-4.92017 CenterZ=0 NormalX=0 NormalY=0 NormalZ=1 AngleXU=0 Radius=5
  constraints (8):
    c: Block(g1)
    c: Block(g0)
    c: Block(g3)
    c: Block(g2)
    c: Block(g5)
    c: Block(g4)
    c: Block(g6)
    c: Block(g7)
FEATURE [Sketcher::SketchObject] Sketch062  label="topSketch016"
  FullyConstrained = true
  sketch-geometry (20):
    g0: LineSegment StartX=5.21097e-06 StartY=3 StartZ=0 EndX=5.21097e-06 EndY=19 EndZ=0
    g1: ArcOfCircle CenterX=19 CenterY=19 CenterZ=0 NormalX=0 NormalY=0 NormalZ=1 AngleXU=0 Radius=19 StartAngle=1.5708 EndAngle=3.14159
    g2: ArcOfCircle CenterX=19 CenterY=19 CenterZ=0 NormalX=0 NormalY=0 NormalZ=1 AngleXU=0 Radius=16 StartAngle=1.5708 EndAngle=3.14159
    g3: LineSegment StartX=114 StartY=35 StartZ=0 EndX=19 EndY=35 EndZ=0
    g4: LineSegment StartX=5.21097e-06 StartY=3 StartZ=0 EndX=5.21097e-06 EndY=0 EndZ=0
    g5: LineSegment StartX=3 StartY=0 StartZ=0 EndX=5.21097e-06 EndY=0 EndZ=0
    g6: LineSegment StartX=3 StartY=19 StartZ=0 EndX=3 EndY=0 EndZ=0
    g7: LineSegment StartX=19 StartY=38 StartZ=0 EndX=124 EndY=38 EndZ=0
    g8: Circle CenterX=119 CenterY=35 CenterZ=0 NormalX=0 NormalY=0 NormalZ=1 AngleXU=0 Radius=1
    g9: Circle CenterX=121 CenterY=35 CenterZ=0 NormalX=0 NormalY=0 NormalZ=1 AngleXU=0 Radius=1
    g10: Circle CenterX=121 CenterY=33 CenterZ=0 NormalX=0 NormalY=0 NormalZ=1 AngleXU=0 Radius=1
    g11: BSplineCurve PolesCount=3 KnotsCount=2 Degree=2 IsPeriodic=0
    g12: GeomPoint X=119 Y=35 Z=0
    g13: GeomPoint X=121 Y=33 Z=0
    g14: LineSegment StartX=119 StartY=35 StartZ=0 EndX=114 EndY=35 EndZ=0
    g15: ArcOfCircle CenterX=105 CenterY=19 CenterZ=0 NormalX=0 NormalY=0 NormalZ=1 AngleXU=0 Radius=19 StartAngle=5.7297 EndAngle=6.28319
    g16: ArcOfCircle CenterX=105 CenterY=19 CenterZ=0 NormalX=0 NormalY=0 NormalZ=1 AngleXU=0 Radius=16 StartAngle=5.60905 EndAngle=6.28319
    g17: LineSegment StartX=121 StartY=33 StartZ=0 EndX=121 EndY=19 EndZ=0
    g18: LineSegment StartX=124 StartY=38 StartZ=0 EndX=124 EndY=19 EndZ=0
    g19: LineSegment StartX=117.5 StartY=9.01251 StartZ=0 EndX=121.163 EndY=9.0125 EndZ=0
  constraints (46):
    c: Vertical(g0)
    c: Block(g0)
    c: Coincident(g1,g0)
    c: Block(g1)
    c: Coincident(g2,g1)
    c: Block(g2)
    c: Coincident(g3,g2)
    c: Horizontal(g3)
    c: Tangent(g3,g2)
    c: Coincident(g4,g0)
    c: Distance(g4) = 3
    c: Vertical(g4)
    c: Coincident(g5,g4)
    c: Horizontal(g5)
    c: Coincident(g6,g2)
    c: Coincident(g6,g5)
    c: Vertical(g6)
    c: Horizontal(g7)
    c: Distance(g7) = 105
    c: Coincident(g7,g1)
    c: Block(g3)
    c: Weight(g8) = 1
    c: Equal(g8,g9)
    c: Equal(g8,g10)
    c: InternalAlignment(g8,g11)
    c: InternalAlignment(g9,g11)
    c: InternalAlignment(g10,g11)
    c: InternalAlignment(g12,g11)
    c: InternalAlignment(g13,g11)
    c: Block(g11)
    c: Coincident(g14,g11)
    c: Coincident(g14,g3)
    c: Horizontal(g14)
    c: Block(g15)
    c: Coincident(g16,g15)
    c: Block(g16)
    c: Coincident(g17,g11)
    c: Coincident(g17,g16)
    c: Vertical(g17)
    c: Distance(g17) = 14
    c: Coincident(g18,g7)
    c: Coincident(g18,g15)
    c: Vertical(g18)
    c: Distance(g18) = 19
    c: Coincident(g19,g16)
    c: Coincident(g19,g15)
FEATURE [Part::Extrusion] Extrude053  label="top024"
  Base = -> Sketch062
  Dir = (0,0,1)
  DirMode = 2
  FaceMakerClass = Part::FaceMakerBullseye
  LengthFwd = 72
  LengthRev = 0
  Solid = true
  Symmetric = false
FEATURE [Sketcher::SketchObject] Sketch063
  FullyConstrained = true
  MapMode = 3
  Placement = pos=(0,0,0) rot=(1,0,0;1.5708rad)
  Support = -> [Extrude053]
  sketch-geometry (8):
    g0: Circle CenterX=80.351 CenterY=-67.6202 CenterZ=0 NormalX=0 NormalY=0 NormalZ=1 AngleXU=0 Radius=2
    g1: Circle CenterX=80.351 CenterY=-67.6202 CenterZ=0 NormalX=0 NormalY=0 NormalZ=1 AngleXU=0 Radius=3
    g2: Circle CenterX=80.351 CenterY=-4.92017 CenterZ=0 NormalX=0 NormalY=0 NormalZ=1 AngleXU=0 Radius=2
    g3: Circle CenterX=80.351 CenterY=-4.92017 CenterZ=0 NormalX=0 NormalY=0 NormalZ=1 AngleXU=0 Radius=3
    g4: Circle CenterX=23.851 CenterY=-4.92017 CenterZ=0 NormalX=0 NormalY=0 NormalZ=1 AngleXU=0 Radius=2
    g5: Circle CenterX=23.851 CenterY=-4.92017 CenterZ=0 NormalX=0 NormalY=0 NormalZ=1 AngleXU=0 Radius=3
    g6: Circle CenterX=23.851 CenterY=-67.6202 CenterZ=0 NormalX=0 NormalY=0 NormalZ=1 AngleXU=0 Radius=2
    g7: Circle CenterX=23.851 CenterY=-67.6202 CenterZ=0 NormalX=0 NormalY=0 NormalZ=1 AngleXU=0 Radius=3
  constraints (8):
    c: Block(g3)
    c: Block(g2)
    c: Block(g1)
    c: Block(g0)
    c: Block(g6)
    c: Block(g7)
    c: Block(g4)
    c: Block(g5)
FEATURE [Part::Extrusion] Extrude054
  Base = -> Sketch063
  Dir = (0,-1,2e-16)
  DirMode = 2
  FaceMakerClass = Part::FaceMakerBullseye
  LengthFwd = 6
  LengthRev = 0
  Placement = pos=(0,9,0) rot=(0,0,1;0rad)
  Solid = true
  Symmetric = false
FEATURE [Sketcher::SketchObject] Sketch064  label="topSketch017"
  FullyConstrained = true
  sketch-geometry (20):
    g0: LineSegment StartX=5.21097e-06 StartY=3 StartZ=0 EndX=5.21097e-06 EndY=19 EndZ=0
    g1: ArcOfCircle CenterX=19 CenterY=19 CenterZ=0 NormalX=0 NormalY=0 NormalZ=1 AngleXU=0 Radius=19 StartAngle=1.5708 EndAngle=3.14159
    g2: ArcOfCircle CenterX=19 CenterY=19 CenterZ=0 NormalX=0 NormalY=0 NormalZ=1 AngleXU=0 Radius=16 StartAngle=1.5708 EndAngle=3.14159
    g3: LineSegment StartX=114 StartY=35 StartZ=0 EndX=19 EndY=35 EndZ=0
    g4: LineSegment StartX=5.21097e-06 StartY=3 StartZ=0 EndX=5.21097e-06 EndY=0 EndZ=0
    g5: LineSegment StartX=3 StartY=0 StartZ=0 EndX=5.21097e-06 EndY=0 EndZ=0
    g6: LineSegment StartX=3 StartY=19 StartZ=0 EndX=3 EndY=0 EndZ=0
    g7: LineSegment StartX=19 StartY=38 StartZ=0 EndX=124 EndY=38 EndZ=0
    g8: Circle CenterX=119 CenterY=35 CenterZ=0 NormalX=0 NormalY=0 NormalZ=1 AngleXU=0 Radius=1
    g9: Circle CenterX=121 CenterY=35 CenterZ=0 NormalX=0 NormalY=0 NormalZ=1 AngleXU=0 Radius=1
    g10: Circle CenterX=121 CenterY=33 CenterZ=0 NormalX=0 NormalY=0 NormalZ=1 AngleXU=0 Radius=1
    g11: BSplineCurve PolesCount=3 KnotsCount=2 Degree=2 IsPeriodic=0
    g12: GeomPoint X=119 Y=35 Z=0
    g13: GeomPoint X=121 Y=33 Z=0
    g14: LineSegment StartX=119 StartY=35 StartZ=0 EndX=114 EndY=35 EndZ=0
    g15: ArcOfCircle CenterX=105 CenterY=19 CenterZ=0 NormalX=0 NormalY=0 NormalZ=1 AngleXU=0 Radius=19 StartAngle=5.7297 EndAngle=6.28319
    g16: ArcOfCircle CenterX=105 CenterY=19 CenterZ=0 NormalX=0 NormalY=0 NormalZ=1 AngleXU=0 Radius=16 StartAngle=5.60905 EndAngle=6.28319
    g17: LineSegment StartX=121 StartY=33 StartZ=0 EndX=121 EndY=19 EndZ=0
    g18: LineSegment StartX=124 StartY=38 StartZ=0 EndX=124 EndY=19 EndZ=0
    g19: LineSegment StartX=117.5 StartY=9.01251 StartZ=0 EndX=121.163 EndY=9.0125 EndZ=0
  constraints (46):
    c: Vertical(g0)
    c: Block(g0)
    c: Coincident(g1,g0)
    c: Block(g1)
    c: Coincident(g2,g1)
    c: Block(g2)
    c: Coincident(g3,g2)
    c: Horizontal(g3)
    c: Tangent(g3,g2)
    c: Coincident(g4,g0)
    c: Distance(g4) = 3
    c: Vertical(g4)
    c: Coincident(g5,g4)
    c: Horizontal(g5)
    c: Coincident(g6,g2)
    c: Coincident(g6,g5)
    c: Vertical(g6)
    c: Horizontal(g7)
    c: Distance(g7) = 105
    c: Coincident(g7,g1)
    c: Block(g3)
    c: Weight(g8) = 1
    c: Equal(g8,g9)
    c: Equal(g8,g10)
    c: InternalAlignment(g8,g11)
    c: InternalAlignment(g9,g11)
    c: InternalAlignment(g10,g11)
    c: InternalAlignment(g12,g11)
    c: InternalAlignment(g13,g11)
    c: Block(g11)
    c: Coincident(g14,g11)
    c: Coincident(g14,g3)
    c: Horizontal(g14)
    c: Block(g15)
    c: Coincident(g16,g15)
    c: Block(g16)
    c: Coincident(g17,g11)
    c: Coincident(g17,g16)
    c: Vertical(g17)
    c: Distance(g17) = 14
    c: Coincident(g18,g7)
    c: Coincident(g18,g15)
    c: Vertical(g18)
    c: Distance(g18) = 19
    c: Coincident(g19,g16)
    c: Coincident(g19,g15)
FEATURE [Sketcher::SketchObject] Sketch065
  FullyConstrained = true
  MapMode = 3
  Placement = pos=(0,0,0) rot=(1,0,0;1.5708rad)
  sketch-geometry (8):
    g0: Circle CenterX=80.351 CenterY=-67.6202 CenterZ=0 NormalX=0 NormalY=0 NormalZ=1 AngleXU=0 Radius=3
    g1: Circle CenterX=80.351 CenterY=-4.92017 CenterZ=0 NormalX=0 NormalY=0 NormalZ=1 AngleXU=0 Radius=3
    g2: Circle CenterX=23.851 CenterY=-4.92017 CenterZ=0 NormalX=0 NormalY=0 NormalZ=1 AngleXU=0 Radius=3
    g3: Circle CenterX=23.851 CenterY=-67.6202 CenterZ=0 NormalX=0 NormalY=0 NormalZ=1 AngleXU=0 Radius=3
    g4: Circle CenterX=23.851 CenterY=-67.6202 CenterZ=0 NormalX=0 NormalY=0 NormalZ=1 AngleXU=0 Radius=5
    g5: Circle CenterX=80.351 CenterY=-67.6202 CenterZ=0 NormalX=0 NormalY=0 NormalZ=1 AngleXU=0 Radius=5
    g6: Circle CenterX=23.851 CenterY=-4.92017 CenterZ=0 NormalX=0 NormalY=0 NormalZ=1 AngleXU=0 Radius=5
    g7: Circle CenterX=80.351 CenterY=-4.92017 CenterZ=0 NormalX=0 NormalY=0 NormalZ=1 AngleXU=0 Radius=5
  constraints (8):
    c: Block(g1)
    c: Block(g0)
    c: Block(g3)
    c: Block(g2)
    c: Block(g5)
    c: Block(g4)
    c: Block(g6)
    c: Block(g7)
FEATURE [Part::Extrusion] Extrude056
  Base = -> Sketch065
  Dir = (0,-1,2e-16)
  DirMode = 2
  FaceMakerClass = Part::FaceMakerBullseye
  LengthFwd = 2
  LengthRev = 0
  Solid = true
  Symmetric = false
FEATURE [Part::Extrusion] Extrude057  label="top025"
  Base = -> Sketch064
  Dir = (0,0,1)
  DirMode = 2
  FaceMakerClass = Part::FaceMakerBullseye
  LengthFwd = 72
  LengthRev = 0
  Solid = true
  Symmetric = false
FEATURE [Sketcher::SketchObject] Sketch066
  FullyConstrained = true
  MapMode = 3
  Placement = pos=(0,0,0) rot=(1,0,0;1.5708rad)
  Support = -> [Extrude057]
  sketch-geometry (8):
    g0: Circle CenterX=80.351 CenterY=-67.6202 CenterZ=0 NormalX=0 NormalY=0 NormalZ=1 AngleXU=0 Radius=3
    g1: Circle CenterX=80.351 CenterY=-4.92017 CenterZ=0 NormalX=0 NormalY=0 NormalZ=1 AngleXU=0 Radius=3
    g2: Circle CenterX=23.851 CenterY=-4.92017 CenterZ=0 NormalX=0 NormalY=0 NormalZ=1 AngleXU=0 Radius=3
    g3: Circle CenterX=23.851 CenterY=-67.6202 CenterZ=0 NormalX=0 NormalY=0 NormalZ=1 AngleXU=0 Radius=3
    g4: Circle CenterX=23.851 CenterY=-67.6202 CenterZ=0 NormalX=0 NormalY=0 NormalZ=1 AngleXU=0 Radius=5
    g5: Circle CenterX=80.351 CenterY=-67.6202 CenterZ=0 NormalX=0 NormalY=0 NormalZ=1 AngleXU=0 Radius=5
    g6: Circle CenterX=23.851 CenterY=-4.92017 CenterZ=0 NormalX=0 NormalY=0 NormalZ=1 AngleXU=0 Radius=5
    g7: Circle CenterX=80.351 CenterY=-4.92017 CenterZ=0 NormalX=0 NormalY=0 NormalZ=1 AngleXU=0 Radius=5
  constraints (8):
    c: Block(g1)
    c: Block(g0)
    c: Block(g3)
    c: Block(g2)
    c: Block(g5)
    c: Block(g4)
    c: Block(g6)
    c: Block(g7)
FEATURE [Part::Extrusion] Extrude055
  Base = -> Sketch066
  Dir = (0,-1,2e-16)
  DirMode = 2
  FaceMakerClass = Part::FaceMakerBullseye
  LengthFwd = 2
  LengthRev = 0
  Solid = true
  Symmetric = false
FEATURE [Part::Fillet] Fillet041
  Base = -> Extrude056
  Edges = 4 edges r=1.99: [Edge6,Edge12,Edge18,Edge24]
FEATURE [Part::Cut] Cut045
  Base = -> Extrude055
  Placement = pos=(0,6,0) rot=(0,0,1;0rad)
  Tool = -> Fillet041
FEATURE [Part::MultiFuse] Fusion095  label="pcbScrewPillars"
  Placement = pos=(-3.2,-1,72.3) rot=(0,0,1;0rad)
  Shapes = -> [Cut045,Extrude054]
FEATURE [Part::Feature] Face113
  shape: bbox 3.2 x 1.5 x 2e-07 mm, 1 faces, 0 solids (baked)
FEATURE [Part::Revolution] Revolve121  label="backCaseScrewRetainer002"
  Angle = 360
  Axis = (0,1,0)
  Base = (0,0,0)
  FaceMakerClass = Part::FaceMakerBullseye
  Placement = pos=(12.5,3,62) rot=(0,0,1;0rad)
  Solid = false
  Source = -> Face113
  Symmetric = false
FEATURE [Part::Feature] Face114
  shape: bbox 3.2 x 1.5 x 2e-07 mm, 1 faces, 0 solids (baked)
FEATURE [Part::Feature] Face115
  shape: bbox 3.2 x 1.5 x 2e-07 mm, 1 faces, 0 solids (baked)
FEATURE [Part::Feature] Face116
  shape: bbox 3.2 x 1.5 x 2e-07 mm, 1 faces, 0 solids (baked)
FEATURE [Part::Revolution] Revolve122  label="frontCaseScrewRetainer004"
  Angle = 360
  Axis = (0,1,0)
  Base = (0,0,0)
  FaceMakerClass = Part::FaceMakerBullseye
  Placement = pos=(89.5,3,68.5) rot=(0,0,1;0rad)
  Solid = false
  Source = -> Face115
  Symmetric = false
FEATURE [Part::Revolution] Revolve123  label="frontCaseScrewRetainer005"
  Angle = 360
  Axis = (0,1,0)
  Base = (0,0,0)
  FaceMakerClass = Part::FaceMakerBullseye
  Placement = pos=(89.5,3,3.5) rot=(0,0,1;0rad)
  Solid = false
  Source = -> Face116
  Symmetric = false
FEATURE [Part::Revolution] Revolve124  label="backCaseScrewRetainer003"
  Angle = 360
  Axis = (0,1,0)
  Base = (0,0,0)
  FaceMakerClass = Part::FaceMakerBullseye
  Placement = pos=(12.5,3,10) rot=(0,0,1;0rad)
  Solid = false
  Source = -> Face114
  Symmetric = false
FEATURE [Part::Feature] Face117
  shape: bbox 3.6 x 3.2 x 2e-07 mm, 1 faces, 0 solids (baked)
FEATURE [Part::Revolution] Revolve125  label="moreFrontCaseScrewRetainer004"
  Angle = 360
  Axis = (0,1,0)
  Base = (0,0,0)
  FaceMakerClass = Part::FaceMakerBullseye
  Placement = pos=(109.5,4.5,68.5) rot=(0,0,1;0rad)
  Solid = false
  Source = -> Face117
  Symmetric = false
FEATURE [Part::Feature] Face118
  shape: bbox 3.6 x 3.2 x 2e-07 mm, 1 faces, 0 solids (baked)
FEATURE [Part::Revolution] Revolve126  label="moreFrontCaseScrewRetainer005"
  Angle = 360
  Axis = (0,1,0)
  Base = (0,0,0)
  FaceMakerClass = Part::FaceMakerBullseye
  Placement = pos=(109.5,4.5,3.5) rot=(0,0,1;0rad)
  Solid = false
  Source = -> Face118
  Symmetric = false
FEATURE [Part::MultiFuse] Fusion096  label="screwRetainers001"
  Shapes = -> [Revolve126,Revolve125,Revolve124,Revolve123,Revolve122,Revolve121]
FEATURE [Part::Feature] Face119
  shape: bbox 10 x 16.5 x 2e-07 mm, 1 faces, 0 solids (baked)
FEATURE [Part::Revolution] Revolve130  label="plugHousing050"
  Angle = 360
  Axis = (0,1,0)
  Base = (0,0,0)
  FaceMakerClass = Part::FaceMakerBullseye
  Placement = pos=(0,0,36.15) rot=(0,0,1;0rad)
  Solid = false
  Source = -> Face119
  Symmetric = false
FEATURE [Part::Feature] Face120
  shape: bbox 10 x 16.5 x 2e-07 mm, 1 faces, 0 solids (baked)
FEATURE [Part::Feature] Face121
  shape: bbox 10 x 16.5 x 2e-07 mm, 1 faces, 0 solids (baked)
FEATURE [Part::Revolution] Revolve127  label="plugHousing047"
  Angle = 360
  Axis = (0,1,0)
  Base = (0,0,0)
  FaceMakerClass = Part::FaceMakerBullseye
  Placement = pos=(0,0,36.15) rot=(0,0,1;0rad)
  Solid = false
  Source = -> Face121
  Symmetric = false
FEATURE [Part::Feature] Face122
  shape: bbox 10 x 16.5 x 2e-07 mm, 1 faces, 0 solids (baked)
FEATURE [Part::Feature] Face123
  shape: bbox 10 x 16.5 x 2e-07 mm, 1 faces, 0 solids (baked)
FEATURE [Part::Revolution] Revolve128  label="plugHousing048"
  Angle = 360
  Axis = (0,1,0)
  Base = (0,0,0)
  FaceMakerClass = Part::FaceMakerBullseye
  Placement = pos=(0,0,36.15) rot=(0,0,1;0rad)
  Solid = false
  Source = -> Face123
  Symmetric = false
FEATURE [Part::MultiFuse] Fusion100  label="plugHousing054"
  Placement = pos=(0,0,0) rot=(0,0,1;1.5708rad)
  Shapes = -> [Revolve130,Revolve128]
FEATURE [Part::Feature] Face124
  shape: bbox 10 x 16.5 x 2e-07 mm, 1 faces, 0 solids (baked)
FEATURE [Part::Feature] Face125
  shape: bbox 10 x 16.5 x 2e-07 mm, 1 faces, 0 solids (baked)
FEATURE [Part::Revolution] Revolve129  label="plugHousing049"
  Angle = 360
  Axis = (0,1,0)
  Base = (0,0,0)
  FaceMakerClass = Part::FaceMakerBullseye
  Placement = pos=(0,0,36.15) rot=(0,0,1;0rad)
  Solid = false
  Source = -> Face125
  Symmetric = false
FEATURE [Part::Feature] Face126
  shape: bbox 10 x 16.5 x 2e-07 mm, 1 faces, 0 solids (baked)
FEATURE [Part::Revolution] Revolve131  label="plugHousing058"
  Angle = 360
  Axis = (0,1,0)
  Base = (0,0,0)
  FaceMakerClass = Part::FaceMakerBullseye
  Placement = pos=(0,0,36.15) rot=(0,0,1;0rad)
  Solid = false
  Source = -> Face120
  Symmetric = false
FEATURE [Part::MultiFuse] Fusion099  label="plugHousing053"
  Placement = pos=(0,0,0) rot=(0,0,1;1.5708rad)
  Shapes = -> [Revolve127,Revolve131]
FEATURE [Part::MultiFuse] Fusion102  label="plugHousing056"
  Placement = pos=(0,19,0) rot=(0,0,1;3.14159rad)
  Shapes = -> [Fusion100,Fusion099]
FEATURE [Part::Revolution] Revolve132  label="plugHousing059"
  Angle = 360
  Axis = (0,1,0)
  Base = (0,0,0)
  FaceMakerClass = Part::FaceMakerBullseye
  Placement = pos=(0,0,36.15) rot=(0,0,1;0rad)
  Solid = false
  Source = -> Face126
  Symmetric = false
FEATURE [Part::Revolution] Revolve133  label="plugHousing060"
  Angle = 360
  Axis = (0,1,0)
  Base = (0,0,0)
  FaceMakerClass = Part::FaceMakerBullseye
  Placement = pos=(0,0,36.15) rot=(0,0,1;0rad)
  Solid = false
  Source = -> Face122
  Symmetric = false
FEATURE [Part::MultiFuse] Fusion097  label="plugHousing051"
  Placement = pos=(0,0,0) rot=(0,0,1;1.5708rad)
  Shapes = -> [Revolve133,Revolve132]
FEATURE [Part::Revolution] Revolve134  label="plugHousing061"
  Angle = 360
  Axis = (0,1,0)
  Base = (0,0,0)
  FaceMakerClass = Part::FaceMakerBullseye
  Placement = pos=(0,0,36.15) rot=(0,0,1;0rad)
  Solid = false
  Source = -> Face124
  Symmetric = false
FEATURE [Part::MultiFuse] Fusion101  label="plugHousing055"
  Placement = pos=(0,0,0) rot=(0,0,1;1.5708rad)
  Shapes = -> [Revolve129,Revolve134]
FEATURE [Part::MultiFuse] Fusion098  label="plugHousing052"
  Placement = pos=(0,19,0) rot=(0,0,1;3.14159rad)
  Shapes = -> [Fusion097,Fusion101]
FEATURE [Part::MultiFuse] Fusion103  label="plugHousing057"
  Placement = pos=(122.621,0,-0.15) rot=(0,0,1;0rad)
  Shapes = -> [Fusion102,Fusion098]
FEATURE [Part::Box] Box028  label="Cube015"
  AttacherType = Attacher::AttachEngine3D
  Height = 28
  Length = 3
  Placement = pos=(110.7,19,22) rot=(0,0,1;0rad)
  Width = 15.7
FEATURE [Part::Cylinder] Cylinder044
  Angle = 360
  AttacherType = Attacher::AttachEngine3D
  Height = 20
  Placement = pos=(0,0,36.15) rot=(0,0,1;0rad)
  Radius = 10.3
FEATURE [Part::Cylinder] Cylinder045
  Angle = 360
  AttacherType = Attacher::AttachEngine3D
  Height = 10
  Placement = pos=(0,0,36.15) rot=(0,0,1;0rad)
  Radius = 4
FEATURE [Part::MultiFuse] Fusion104  label="removeToCreteHoleForPlugHousing040"
  Placement = pos=(70,19,36) rot=(0,1,0;1.5708rad)
  Shapes = -> [Cylinder044,Cylinder045]
FEATURE [Part::Cut] Cut046  label="plugHousingTab003"
  Base = -> Box028
  Tool = -> Fusion104
FEATURE [Part::MultiFuse] Fusion105  label="plugHousing062"
  Shapes = -> [Fusion103,Cut046]
FEATURE [Part::Fillet] Fillet042
  Base = -> Fusion105
  Edges = 1 edges r=2: [Edge25]
FEATURE [Part::Fillet] Fillet043  label="plugHousing063"
  Base = -> Fillet042
  Edges = 1 edges r=2: [Edge8]
  Placement = pos=(7,0,0) rot=(0,0,1;0rad)
FEATURE [Part::Feature] Face127
  shape: bbox 10 x 16.5 x 2e-07 mm, 1 faces, 0 solids (baked)
FEATURE [Part::Feature] Face128
  shape: bbox 10 x 16.5 x 2e-07 mm, 1 faces, 0 solids (baked)
FEATURE [Part::Revolution] Revolve137  label="plugHousing070"
  Angle = 360
  Axis = (0,1,0)
  Base = (0,0,0)
  FaceMakerClass = Part::FaceMakerBullseye
  Placement = pos=(0,0,36.15) rot=(0,0,1;0rad)
  Solid = false
  Source = -> Face127
  Symmetric = false
FEATURE [Part::Revolution] Revolve140  label="plugHousing073"
  Angle = 360
  Axis = (0,1,0)
  Base = (0,0,0)
  FaceMakerClass = Part::FaceMakerBullseye
  Placement = pos=(0,0,36.15) rot=(0,0,1;0rad)
  Solid = false
  Source = -> Face128
  Symmetric = false
FEATURE [Part::Feature] Face129
  shape: bbox 10 x 16.5 x 2e-07 mm, 1 faces, 0 solids (baked)
FEATURE [Part::Revolution] Revolve138  label="plugHousing071"
  Angle = 360
  Axis = (0,1,0)
  Base = (0,0,0)
  FaceMakerClass = Part::FaceMakerBullseye
  Placement = pos=(0,0,36.15) rot=(0,0,1;0rad)
  Solid = false
  Source = -> Face129
  Symmetric = false
FEATURE [Part::Feature] Face130
  shape: bbox 10 x 16.5 x 2e-07 mm, 1 faces, 0 solids (baked)
FEATURE [Part::Revolution] Revolve139  label="plugHousing072"
  Angle = 360
  Axis = (0,1,0)
  Base = (0,0,0)
  FaceMakerClass = Part::FaceMakerBullseye
  Placement = pos=(0,0,36.15) rot=(0,0,1;0rad)
  Solid = false
  Source = -> Face130
  Symmetric = false
FEATURE [Part::Feature] Face131
  shape: bbox 10 x 16.5 x 2e-07 mm, 1 faces, 0 solids (baked)
FEATURE [Part::Revolution] Revolve135  label="plugHousing068"
  Angle = 360
  Axis = (0,1,0)
  Base = (0,0,0)
  FaceMakerClass = Part::FaceMakerBullseye
  Placement = pos=(0,0,36.15) rot=(0,0,1;0rad)
  Solid = false
  Source = -> Face131
  Symmetric = false
FEATURE [Part::MultiFuse] Fusion112  label="plugHousing078"
  Placement = pos=(0,0,0) rot=(0,0,1;1.5708rad)
  Shapes = -> [Revolve135,Revolve139]
FEATURE [Part::Feature] Face132
  shape: bbox 10 x 16.5 x 2e-07 mm, 1 faces, 0 solids (baked)
FEATURE [Part::Revolution] Revolve141  label="plugHousing074"
  Angle = 360
  Axis = (0,1,0)
  Base = (0,0,0)
  FaceMakerClass = Part::FaceMakerBullseye
  Placement = pos=(0,0,36.15) rot=(0,0,1;0rad)
  Solid = false
  Source = -> Face132
  Symmetric = false
FEATURE [Part::MultiFuse] Fusion110  label="plugHousing076"
  Placement = pos=(0,0,0) rot=(0,0,1;1.5708rad)
  Shapes = -> [Revolve141,Revolve140]
FEATURE [Part::Feature] Face133
  shape: bbox 10 x 16.5 x 2e-07 mm, 1 faces, 0 solids (baked)
FEATURE [Part::Revolution] Revolve136  label="plugHousing069"
  Angle = 360
  Axis = (0,1,0)
  Base = (0,0,0)
  FaceMakerClass = Part::FaceMakerBullseye
  Placement = pos=(0,0,36.15) rot=(0,0,1;0rad)
  Solid = false
  Source = -> Face133
  Symmetric = false
FEATURE [Part::MultiFuse] Fusion106  label="plugHousing064"
  Placement = pos=(0,0,0) rot=(0,0,1;1.5708rad)
  Shapes = -> [Revolve138,Revolve136]
FEATURE [Part::MultiFuse] Fusion108  label="plugHousing066"
  Placement = pos=(0,19,0) rot=(0,0,1;3.14159rad)
  Shapes = -> [Fusion106,Fusion112]
FEATURE [Part::Feature] Face134
  shape: bbox 10 x 16.5 x 2e-07 mm, 1 faces, 0 solids (baked)
FEATURE [Part::Revolution] Revolve142  label="plugHousing075"
  Angle = 360
  Axis = (0,1,0)
  Base = (0,0,0)
  FaceMakerClass = Part::FaceMakerBullseye
  Placement = pos=(0,0,36.15) rot=(0,0,1;0rad)
  Solid = false
  Source = -> Face134
  Symmetric = false
FEATURE [Part::MultiFuse] Fusion107  label="plugHousing065"
  Placement = pos=(0,0,0) rot=(0,0,1;1.5708rad)
  Shapes = -> [Revolve137,Revolve142]
FEATURE [Part::MultiFuse] Fusion111  label="plugHousing077"
  Placement = pos=(0,19,0) rot=(0,0,1;3.14159rad)
  Shapes = -> [Fusion110,Fusion107]
FEATURE [Part::MultiFuse] Fusion109  label="plugHousing067"
  Placement = pos=(131.236,0,-0.15) rot=(0,0,1;0rad)
  Shapes = -> [Fusion108,Fusion111]
FEATURE [Part::MultiFuse] Fusion113  label="plugHousing079"
  Shapes = -> [Fillet043,Fusion109]
FEATURE [Part::Feature] Face135
  shape: bbox 3.5 x 17.8 x 2e-07 mm, 1 faces, 0 solids (baked)
FEATURE [Part::Revolution] Revolve143  label="removeToCreateScrewAndThreadedInsertHole049"
  Angle = 360
  Axis = (0,1,0)
  Base = (0,0,0)
  FaceMakerClass = Part::FaceMakerBullseye
  Placement = pos=(12.5,0,10) rot=(0,0,1;0rad)
  Solid = false
  Source = -> Face135
  Symmetric = false
FEATURE [Part::Feature] Face136
  shape: bbox 3.5 x 17.8 x 2e-07 mm, 1 faces, 0 solids (baked)
FEATURE [Part::Revolution] Revolve144  label="removeToCreateScrewAndThreadedInsertHole050"
  Angle = 360
  Axis = (0,1,0)
  Base = (0,0,0)
  FaceMakerClass = Part::FaceMakerBullseye
  Placement = pos=(12.5,0,62) rot=(0,0,1;0rad)
  Solid = false
  Source = -> Face136
  Symmetric = false
FEATURE [Part::Feature] Face137
  shape: bbox 3.5 x 17.8 x 2e-07 mm, 1 faces, 0 solids (baked)
FEATURE [Part::Revolution] Revolve145  label="removeToCreateScrewAndThreadedInsertHole051"
  Angle = 360
  Axis = (0,1,0)
  Base = (0,0,0)
  FaceMakerClass = Part::FaceMakerBullseye
  Placement = pos=(89.5,0,68.5) rot=(0,0,1;0rad)
  Solid = false
  Source = -> Face137
  Symmetric = false
FEATURE [Part::Feature] Face138
  shape: bbox 3.5 x 17.8 x 2e-07 mm, 1 faces, 0 solids (baked)
FEATURE [Part::Revolution] Revolve146  label="removeToCreateScrewAndThreadedInsertHole052"
  Angle = 360
  Axis = (0,1,0)
  Base = (0,0,0)
  FaceMakerClass = Part::FaceMakerBullseye
  Placement = pos=(89.5,0,3.5) rot=(0,0,1;0rad)
  Solid = false
  Source = -> Face138
  Symmetric = false
FEATURE [Part::Feature] Face139
  shape: bbox 3.5 x 17.8 x 2e-07 mm, 1 faces, 0 solids (baked)
FEATURE [Part::Revolution] Revolve147  label="removeToCreateScrewAndThreadedInsertHole053"
  Angle = 360
  Axis = (0,1,0)
  Base = (0,0,0)
  FaceMakerClass = Part::FaceMakerBullseye
  Placement = pos=(109.5,4.7,3.5) rot=(0,0,1;0rad)
  Solid = false
  Source = -> Face139
  Symmetric = false
FEATURE [Part::Feature] Face140
  shape: bbox 3.5 x 17.8 x 2e-07 mm, 1 faces, 0 solids (baked)
FEATURE [Part::Revolution] Revolve148  label="removeToCreateScrewAndThreadedInsertHole054"
  Angle = 360
  Axis = (0,1,0)
  Base = (0,0,0)
  FaceMakerClass = Part::FaceMakerBullseye
  Placement = pos=(109.5,4.7,68.5) rot=(0,0,1;0rad)
  Solid = false
  Source = -> Face140
  Symmetric = false
FEATURE [Part::MultiFuse] Fusion114  label="removeToCreateScrewAndThreadedInsertHole055"
  Shapes = -> [Revolve148,Revolve147,Revolve146,Revolve145,Revolve144,Revolve143]
FEATURE [Part::Cut] Cut047  label="casePillars004"
  Base = -> Cut037
  Tool = -> Fusion114
FEATURE [Part::Feature] Face141
  shape: bbox 3.5 x 17.8 x 2e-07 mm, 1 faces, 0 solids (baked)
FEATURE [Part::Feature] Face142
  shape: bbox 3.5 x 17.8 x 2e-07 mm, 1 faces, 0 solids (baked)
FEATURE [Part::Feature] Face143
  shape: bbox 3.5 x 17.8 x 2e-07 mm, 1 faces, 0 solids (baked)
FEATURE [Part::Revolution] Revolve149  label="removeToCreateScrewAndThreadedInsertHole057"
  Angle = 360
  Axis = (0,1,0)
  Base = (0,0,0)
  FaceMakerClass = Part::FaceMakerBullseye
  Placement = pos=(12.5,0,10) rot=(0,0,1;0rad)
  Solid = false
  Source = -> Face141
  Symmetric = false
FEATURE [Part::Feature] Face144
  shape: bbox 3.5 x 17.8 x 2e-07 mm, 1 faces, 0 solids (baked)
FEATURE [Part::Feature] Face145
  shape: bbox 3.5 x 17.8 x 2e-07 mm, 1 faces, 0 solids (baked)
FEATURE [Part::Feature] Face146
  shape: bbox 3.5 x 17.8 x 2e-07 mm, 1 faces, 0 solids (baked)
FEATURE [Part::Revolution] Revolve150  label="removeToCreateScrewAndThreadedInsertHole058"
  Angle = 360
  Axis = (0,1,0)
  Base = (0,0,0)
  FaceMakerClass = Part::FaceMakerBullseye
  Placement = pos=(12.5,0,62) rot=(0,0,1;0rad)
  Solid = false
  Source = -> Face146
  Symmetric = false
FEATURE [Part::Revolution] Revolve151  label="removeToCreateScrewAndThreadedInsertHole059"
  Angle = 360
  Axis = (0,1,0)
  Base = (0,0,0)
  FaceMakerClass = Part::FaceMakerBullseye
  Placement = pos=(89.5,0,68.5) rot=(0,0,1;0rad)
  Solid = false
  Source = -> Face143
  Symmetric = false
FEATURE [Part::Revolution] Revolve152  label="removeToCreateScrewAndThreadedInsertHole060"
  Angle = 360
  Axis = (0,1,0)
  Base = (0,0,0)
  FaceMakerClass = Part::FaceMakerBullseye
  Placement = pos=(89.5,0,3.5) rot=(0,0,1;0rad)
  Solid = false
  Source = -> Face142
  Symmetric = false
FEATURE [Part::Revolution] Revolve153  label="removeToCreateScrewAndThreadedInsertHole061"
  Angle = 360
  Axis = (0,1,0)
  Base = (0,0,0)
  FaceMakerClass = Part::FaceMakerBullseye
  Placement = pos=(109.5,4.7,3.5) rot=(0,0,1;0rad)
  Solid = false
  Source = -> Face145
  Symmetric = false
FEATURE [Part::Revolution] Revolve154  label="removeToCreateScrewAndThreadedInsertHole062"
  Angle = 360
  Axis = (0,1,0)
  Base = (0,0,0)
  FaceMakerClass = Part::FaceMakerBullseye
  Placement = pos=(109.5,4.7,68.5) rot=(0,0,1;0rad)
  Solid = false
  Source = -> Face144
  Symmetric = false
FEATURE [Part::MultiFuse] Fusion115  label="removeToCreateScrewAndThreadedInsertHole056"
  Shapes = -> [Revolve154,Revolve153,Revolve152,Revolve151,Revolve150,Revolve149]
FEATURE [Part::Feature] Face147
  shape: bbox 9.8 x 26.5 x 2e-07 mm, 1 faces, 0 solids (baked)
FEATURE [Part::Revolution] Revolve155
  Angle = 360
  Axis = (0,1,0)
  Base = (0,0,0)
  FaceMakerClass = Part::FaceMakerBullseye
  Placement = pos=(0,0,0) rot=(0,0,1;1.5708rad)
  Solid = false
  Source = -> Face147
  Symmetric = false
FEATURE [Part::Feature] Face148
  shape: bbox 9.8 x 26.5 x 2e-07 mm, 1 faces, 0 solids (baked)
FEATURE [Part::Revolution] Revolve156
  Angle = 360
  Axis = (0,1,0)
  Base = (0,0,0)
  FaceMakerClass = Part::FaceMakerBullseye
  Placement = pos=(0,0,0) rot=(0,0,1;1.5708rad)
  Solid = false
  Source = -> Face148
  Symmetric = false
FEATURE [Part::MultiFuse] Fusion116
  Placement = pos=(-18,19,36) rot=(0,0,1;0rad)
  Shapes = -> [Revolve156,Revolve155]
FEATURE [Part::Box] Box029  label="Cube016"
  AttacherType = Attacher::AttachEngine3D
  Height = 28
  Length = 3
  Placement = pos=(110.7,19,22) rot=(0,0,1;0rad)
  Width = 15.7
FEATURE [Part::Cylinder] Cylinder046
  Angle = 360
  AttacherType = Attacher::AttachEngine3D
  Height = 10
  Placement = pos=(0,0,36.15) rot=(0,0,1;0rad)
  Radius = 4
FEATURE [Part::Cylinder] Cylinder047
  Angle = 360
  AttacherType = Attacher::AttachEngine3D
  Height = 20
  Placement = pos=(0,0,36.15) rot=(0,0,1;0rad)
  Radius = 10.3
FEATURE [Part::MultiFuse] Fusion117  label="removeToCreteHoleForPlugHousing041"
  Placement = pos=(70,19,36) rot=(0,1,0;1.5708rad)
  Shapes = -> [Cylinder047,Cylinder046]
FEATURE [Part::Cut] Cut049  label="plugHousingTab004"
  Base = -> Box029
  Placement = pos=(-107.4,-14,0) rot=(0,0,1;0rad)
  Tool = -> Fusion117
FEATURE [Part::Box] Box030  label="Cube017"
  AttacherType = Attacher::AttachEngine3D
  Height = 28
  Length = 3
  Placement = pos=(110.7,19,22) rot=(0,0,1;0rad)
  Width = 15.7
FEATURE [Part::Cylinder] Cylinder048
  Angle = 360
  AttacherType = Attacher::AttachEngine3D
  Height = 10
  Placement = pos=(0,0,36.15) rot=(0,0,1;0rad)
  Radius = 4
FEATURE [Part::Cylinder] Cylinder049
  Angle = 360
  AttacherType = Attacher::AttachEngine3D
  Height = 20
  Placement = pos=(0,0,36.15) rot=(0,0,1;0rad)
  Radius = 10.3
FEATURE [Part::MultiFuse] Fusion118  label="removeToCreteHoleForPlugHousing042"
  Placement = pos=(70,19,36) rot=(0,1,0;1.5708rad)
  Shapes = -> [Cylinder049,Cylinder048]
FEATURE [Part::Cut] Cut050  label="plugHousingTab005"
  Base = -> Box030
  Placement = pos=(-107.4,-14,0) rot=(0,0,1;0rad)
  Tool = -> Fusion118
FEATURE [Part::MultiFuse] Fusion119
  Placement = pos=(9.6,23,0) rot=(0,0,1;3.14159rad)
  Shapes = -> [Cut049,Cut050]
FEATURE [Part::Box] Box031  label="Cube018"
  AttacherType = Attacher::AttachEngine3D
  Height = 10
  Length = 3
  Placement = pos=(3.3,4,12) rot=(0,0,1;0rad)
  Width = 10
FEATURE [Part::Fillet] Fillet044
  Base = -> Box031
  Edges = 1 edges r=2: [Edge11]
FEATURE [Part::Box] Box032  label="Cube019"
  AttacherType = Attacher::AttachEngine3D
  Height = 10
  Length = 3
  Placement = pos=(3.3,4,50) rot=(0,0,1;0rad)
  Width = 10
FEATURE [Part::Fillet] Fillet045
  Base = -> Box032
  Edges = 1 edges r=2: [Edge12]
FEATURE [Part::Box] Box033  label="Cube020"
  AttacherType = Attacher::AttachEngine3D
  Height = 28
  Length = 4
  Placement = pos=(5,0,22) rot=(0,0,1;0rad)
  Width = 10
FEATURE [Part::Fillet] Fillet046
  Base = -> Box033
  Edges = 1 edges r=1: [Edge7]
FEATURE [Part::Fillet] Fillet047
  Base = -> Fillet046
  Edges = 1 edges r=2: [Edge5]
FEATURE [Part::Fillet] Fillet048
  Base = -> Fillet047
  Edges = 1 edges r=2: [Edge2]
FEATURE [Part::Cylinder] Cylinder050
  Angle = 360
  AttacherType = Attacher::AttachEngine3D
  Height = 20
  Placement = pos=(0,0,36.15) rot=(0,0,1;0rad)
  Radius = 8.2
FEATURE [Part::Cylinder] Cylinder051
  Angle = 360
  AttacherType = Attacher::AttachEngine3D
  Height = 10
  Placement = pos=(0,0,36.15) rot=(0,0,1;0rad)
  Radius = 4
FEATURE [Part::MultiFuse] Fusion120  label="removeToCreteHoleForPlugHousing043"
  Placement = pos=(-42,19,36) rot=(0,1,0;1.5708rad)
  Shapes = -> [Cylinder050,Cylinder051]
FEATURE [Sketcher::SketchObject] Sketch067  label="topSketch018"
  FullyConstrained = true
  sketch-geometry (4):
    g0: LineSegment StartX=16.8446 StartY=31.512 StartZ=0 EndX=16.3251 EndY=34.4666 EndZ=0
    g1: ArcOfCircle CenterX=19 CenterY=19.2524 CenterZ=0 NormalX=0 NormalY=0 NormalZ=1 AngleXU=0 Radius=15.4476 StartAngle=1.74483 EndAngle=2.72717
    g2: ArcOfCircle CenterX=19 CenterY=19.2524 CenterZ=0 NormalX=0 NormalY=0 NormalZ=1 AngleXU=0 Radius=12.4476 StartAngle=1.74483 EndAngle=2.73189
    g3: LineSegment StartX=4.86004 StartY=25.4725 StartZ=0 EndX=7.58253 EndY=24.2107 EndZ=0
  constraints (7):
    c: Block(g0)
    c: Coincident(g1,g0)
    c: Coincident(g2,g0)
    c: Coincident(g3,g1)
    c: Coincident(g3,g2)
    c: Block(g1)
    c: Block(g2)
FEATURE [Part::Extrusion] Extrude058
  Base = -> Sketch067
  Dir = (0,0,1)
  DirMode = 2
  FaceMakerClass = Part::FaceMakerBullseye
  LengthFwd = 10
  LengthRev = 0
  Placement = pos=(0,0,31) rot=(0,0,1;0rad)
  Solid = true
  Symmetric = false
FEATURE [Part::Cut] Cut051
  Base = -> Extrude058
  Tool = -> Fusion120
FEATURE [Part::Fillet] Fillet049
  Base = -> Cut051
  Edges = 1 edges r=2: [Edge1]
FEATURE [Part::Fillet] Fillet050
  Base = -> Fillet049
  Edges = 1 edges r=2.5: [Edge1]
FEATURE [Part::Fillet] Fillet051
  Base = -> Fillet050
  Edges = 1 edges r=2.5: [Edge2]
FEATURE [Part::MultiFuse] Fusion121  label="wireHolder003"
  Shapes = -> [Fusion116,Fillet051]
FEATURE [Part::MultiFuse] Fusion122
  Shapes = -> [Fillet045,Fusion121]
FEATURE [Part::MultiFuse] Fusion123  label="wireHolder004"
  Shapes = -> [Fusion122,Fillet048]
FEATURE [Part::MultiFuse] Fusion124  label="wireHolder005"
  Shapes = -> [Fillet044,Fusion119,Fusion123]
FEATURE [Sketcher::SketchObject] Sketch068  label="topSketch019"
  FullyConstrained = true
  sketch-geometry (6):
    g0: LineSegment StartX=19 StartY=38 StartZ=0 EndX=117 EndY=38 EndZ=0
    g1: ArcOfCircle CenterX=19 CenterY=19 CenterZ=0 NormalX=0 NormalY=0 NormalZ=1 AngleXU=0 Radius=19 StartAngle=1.5708 EndAngle=3.14159
    g2: LineSegment StartX=117 StartY=38 StartZ=0 EndX=117 EndY=19 EndZ=0
    g3: LineSegment StartX=98 StartY=1.0161e-12 StartZ=0 EndX=5.22862e-06 EndY=1.0161e-12 EndZ=0
    g4: LineSegment StartX=5.22862e-06 StartY=19 StartZ=0 EndX=5.22862e-06 EndY=1.0161e-12 EndZ=0
    g5: ArcOfCircle CenterX=98 CenterY=19 CenterZ=0 NormalX=0 NormalY=0 NormalZ=1 AngleXU=0 Radius=19 StartAngle=4.71239 EndAngle=6.28319
  constraints (16):
    c: Horizontal(g0)
    c: Distance(g0) = 98
    c: Coincident(g1,g0)
    c: Block(g1)
    c: Coincident(g2,g0)
    c: Vertical(g2)
    c: Distance(g2) = 19
    c: Horizontal(g3)
    c: Coincident(g4,g1)
    c: Vertical(g4)
    c: Coincident(g3,g4)
    c: Block(g3)
    c: Coincident(g5,g2)
    c: Coincident(g5,g3)
    c: Block(g0)
    c: Block(g5)
FEATURE [Part::Extrusion] Extrude059  label="sideA002"
  Base = -> Sketch068
  Dir = (0,0,1)
  DirMode = 2
  FaceMakerClass = Part::FaceMakerBullseye
  LengthFwd = 3
  LengthRev = 0
  Placement = pos=(0,0,-2.7) rot=(0,0,1;0rad)
  Solid = true
  Symmetric = false
FEATURE [Sketcher::SketchObject] Sketch069  label="topSketch020"
  FullyConstrained = true
  sketch-geometry (6):
    g0: LineSegment StartX=19 StartY=38 StartZ=0 EndX=117 EndY=38 EndZ=0
    g1: ArcOfCircle CenterX=19 CenterY=19 CenterZ=0 NormalX=0 NormalY=0 NormalZ=1 AngleXU=0 Radius=19 StartAngle=1.5708 EndAngle=3.14159
    g2: LineSegment StartX=117 StartY=38 StartZ=0 EndX=117 EndY=19 EndZ=0
    g3: LineSegment StartX=98 StartY=1.0161e-12 StartZ=0 EndX=5.22862e-06 EndY=1.0161e-12 EndZ=0
    g4: LineSegment StartX=5.22862e-06 StartY=19 StartZ=0 EndX=5.22862e-06 EndY=1.0161e-12 EndZ=0
    g5: ArcOfCircle CenterX=98 CenterY=19 CenterZ=0 NormalX=0 NormalY=0 NormalZ=1 AngleXU=0 Radius=19 StartAngle=4.71239 EndAngle=6.28319
  constraints (16):
    c: Horizontal(g0)
    c: Distance(g0) = 98
    c: Coincident(g1,g0)
    c: Block(g1)
    c: Coincident(g2,g0)
    c: Vertical(g2)
    c: Distance(g2) = 19
    c: Horizontal(g3)
    c: Coincident(g4,g1)
    c: Vertical(g4)
    c: Coincident(g3,g4)
    c: Block(g3)
    c: Coincident(g5,g2)
    c: Coincident(g5,g3)
    c: Block(g0)
    c: Block(g5)
FEATURE [Part::Extrusion] Extrude060  label="sideB002"
  Base = -> Sketch069
  Dir = (0,0,1)
  DirMode = 2
  FaceMakerClass = Part::FaceMakerBullseye
  LengthFwd = 3
  LengthRev = 0
  Placement = pos=(0,0,71.7) rot=(0,0,1;0rad)
  Solid = true
  Symmetric = false
FEATURE [Part::MultiFuse] Fusion127  label="removeFromBottom001"
  Placement = pos=(2,0,0) rot=(0,0,1;0rad)
  Shapes = -> [Extrude059,Extrude060]
FEATURE [Part::Cylinder] Cylinder052
  Angle = 360
  AttacherType = Attacher::AttachEngine3D
  Height = 20
  Placement = pos=(0,0,36.15) rot=(0,0,1;0rad)
  Radius = 14
FEATURE [Part::Cylinder] Cylinder053
  Angle = 360
  AttacherType = Attacher::AttachEngine3D
  Height = 10
  Placement = pos=(0,0,36.15) rot=(0,0,1;0rad)
  Radius = 4
FEATURE [Part::MultiFuse] Fusion128  label="removeToCreteHoleForPlugHousing044"
  Placement = pos=(70,19,36) rot=(0,1,0;1.5708rad)
  Shapes = -> [Cylinder052,Cylinder053]
FEATURE [Part::Cut] Cut052  label="bottom011"
  Base = -> Extrude043
  Tool = -> Fusion128
FEATURE [Part::Cut] Cut054  label="bottom012"
  Base = -> Cut052
  Tool = -> Fusion115
FEATURE [Sketcher::SketchObject] Sketch070
  FullyConstrained = true
  Placement = pos=(117,19,0) rot=(0.57735,0.57735,0.57735;2.0944rad)
  sketch-geometry (48):
    g0: LineSegment StartX=-49.19 StartY=69.25 StartZ=0 EndX=-49.19 EndY=66.25 EndZ=0
    g1: LineSegment StartX=-49.19 StartY=63.5 StartZ=0 EndX=-49.19 EndY=60.5 EndZ=0
    g2: LineSegment StartX=-49.19 StartY=57.75 StartZ=0 EndX=-49.19 EndY=54.75 EndZ=0
    g3: LineSegment StartX=-49.19 StartY=52 StartZ=0 EndX=-49.19 EndY=49 EndZ=0
    g4: LineSegment StartX=-49.19 StartY=46.25 StartZ=0 EndX=-49.19 EndY=43.25 EndZ=0
    g5: LineSegment StartX=-49.19 StartY=40.5 StartZ=0 EndX=-49.19 EndY=37.5 EndZ=0
    g6: LineSegment StartX=-49.19 StartY=34.5 StartZ=0 EndX=-49.19 EndY=31.5 EndZ=0
    g7: LineSegment StartX=-49.19 StartY=28.75 StartZ=0 EndX=-49.19 EndY=25.75 EndZ=0
    g8: LineSegment StartX=-49.19 StartY=23 StartZ=0 EndX=-49.19 EndY=20 EndZ=0
    g9: LineSegment StartX=-49.19 StartY=17.25 StartZ=0 EndX=-49.19 EndY=14.25 EndZ=0
    g10: LineSegment StartX=-49.19 StartY=11.5 StartZ=0 EndX=-49.19 EndY=8.5 EndZ=0
    g11: LineSegment StartX=-49.19 StartY=5.75 StartZ=0 EndX=-49.19 EndY=2.75 EndZ=0
    g12: ArcOfCircle CenterX=-1.5 CenterY=67.75 CenterZ=0 NormalX=0 NormalY=0 NormalZ=1 AngleXU=0 Radius=1.5 StartAngle=4.71239 EndAngle=7.85398
    g13: ArcOfCircle CenterX=-1.5 CenterY=62 CenterZ=0 NormalX=0 NormalY=0 NormalZ=1 AngleXU=0 Radius=1.5 StartAngle=4.71239 EndAngle=7.85398
    g14: ArcOfCircle CenterX=-1.5 CenterY=56.25 CenterZ=0 NormalX=0 NormalY=0 NormalZ=1 AngleXU=0 Radius=1.5 StartAngle=4.71239 EndAngle=7.85398
    g15: ArcOfCircle CenterX=-11.49 CenterY=50.5 CenterZ=0 NormalX=0 NormalY=0 NormalZ=1 AngleXU=0 Radius=1.5 StartAngle=4.71239 EndAngle=7.85398
    g16: ArcOfCircle CenterX=-16.28 CenterY=44.75 CenterZ=0 NormalX=0 NormalY=0 NormalZ=1 AngleXU=0 Radius=1.5 StartAngle=4.71239 EndAngle=7.85398
    g17: ArcOfCircle CenterX=-18.2337 CenterY=39 CenterZ=0 NormalX=0 NormalY=0 NormalZ=1 AngleXU=0 Radius=1.5 StartAngle=4.71485 EndAngle=7.85398
    g18: ArcOfCircle CenterX=-16.2837 CenterY=27.25 CenterZ=0 NormalX=0 NormalY=0 NormalZ=1 AngleXU=0 Radius=1.5 StartAngle=4.71485 EndAngle=7.85398
    g19: ArcOfCircle CenterX=-18.2337 CenterY=33 CenterZ=0 NormalX=0 NormalY=0 NormalZ=1 AngleXU=0 Radius=1.5 StartAngle=4.71485 EndAngle=7.85398
    g20: ArcOfCircle CenterX=-11.49 CenterY=21.5 CenterZ=0 NormalX=0 NormalY=0 NormalZ=1 AngleXU=0 Radius=1.5 StartAngle=4.71239 EndAngle=7.85398
    g21: ArcOfCircle CenterX=-1.5 CenterY=4.25 CenterZ=0 NormalX=0 NormalY=0 NormalZ=1 AngleXU=0 Radius=1.5 StartAngle=4.71239 EndAngle=7.85398
    g22: ArcOfCircle CenterX=-1.5 CenterY=10 CenterZ=0 NormalX=0 NormalY=0 NormalZ=1 AngleXU=0 Radius=1.5 StartAngle=4.71239 EndAngle=7.85398
    g23: ArcOfCircle CenterX=-1.5 CenterY=15.75 CenterZ=0 NormalX=0 NormalY=0 NormalZ=1 AngleXU=0 Radius=1.5 StartAngle=4.71239 EndAngle=7.85398
    g24: LineSegment StartX=-49.19 StartY=69.25 StartZ=0 EndX=-1.5 EndY=69.25 EndZ=0
    g25: LineSegment StartX=-49.19 StartY=66.25 StartZ=0 EndX=-1.5 EndY=66.25 EndZ=0
    g26: LineSegment StartX=-49.19 StartY=63.5 StartZ=0 EndX=-1.5 EndY=63.5 EndZ=0
    g27: LineSegment StartX=-49.19 StartY=60.5 StartZ=0 EndX=-1.5 EndY=60.5 EndZ=0
    g28: LineSegment StartX=-49.19 StartY=57.75 StartZ=0 EndX=-1.5 EndY=57.75 EndZ=0
    g29: LineSegment StartX=-49.19 StartY=54.75 StartZ=0 EndX=-1.5 EndY=54.75 EndZ=0
    g30: LineSegment StartX=-49.19 StartY=52 StartZ=0 EndX=-11.49 EndY=52 EndZ=0
    g31: LineSegment StartX=-49.19 StartY=49 StartZ=0 EndX=-11.49 EndY=49 EndZ=0
    g32: LineSegment StartX=-49.19 StartY=46.25 StartZ=0 EndX=-16.28 EndY=46.25 EndZ=0
    g33: LineSegment StartX=-49.19 StartY=43.25 StartZ=0 EndX=-16.28 EndY=43.25 EndZ=0
    g34: LineSegment StartX=-49.19 StartY=40.5 StartZ=0 EndX=-18.2337 EndY=40.5 EndZ=0
    g35: LineSegment StartX=-49.19 StartY=37.5 StartZ=0 EndX=-18.23 EndY=37.5 EndZ=0
    g36: LineSegment StartX=-49.19 StartY=34.5 StartZ=0 EndX=-18.2337 EndY=34.5 EndZ=0
    g37: LineSegment StartX=-49.19 StartY=31.5 StartZ=0 EndX=-18.23 EndY=31.5 EndZ=0
    g38: LineSegment StartX=-49.19 StartY=28.75 StartZ=0 EndX=-16.2837 EndY=28.75 EndZ=0
    g39: LineSegment StartX=-49.19 StartY=25.75 StartZ=0 EndX=-16.28 EndY=25.75 EndZ=0
    g40: LineSegment StartX=-49.19 StartY=23 StartZ=0 EndX=-11.49 EndY=23 EndZ=0
    g41: LineSegment StartX=-49.19 StartY=20 StartZ=0 EndX=-11.49 EndY=20 EndZ=0
    g42: LineSegment StartX=-49.19 StartY=17.25 StartZ=0 EndX=-1.5 EndY=17.25 EndZ=0
    g43: LineSegment StartX=-49.19 StartY=14.25 StartZ=0 EndX=-1.5 EndY=14.25 EndZ=0
    g44: LineSegment StartX=-49.19 StartY=11.5 StartZ=0 EndX=-1.5 EndY=11.5 EndZ=0
    g45: LineSegment StartX=-49.19 StartY=8.5 StartZ=0 EndX=-1.5 EndY=8.5 EndZ=0
    g46: LineSegment StartX=-49.19 StartY=5.75 StartZ=0 EndX=-1.5 EndY=5.75 EndZ=0
    g47: LineSegment StartX=-49.19 StartY=2.75 StartZ=0 EndX=-1.5 EndY=2.75 EndZ=0
  constraints (120):
    c: Vertical(g0)
    c: Distance(g0) = 3
    c: Block(g0)
    c: Vertical(g1)
    c: Distance(g1) = 3
    c: Vertical(g2)
    c: Equal(g0,g2) = 3
    c: Block(g2)
    c: Vertical(g3)
    c: Equal(g1,g3) = 3
    c: Vertical(g4)
    c: Equal(g0,g4) = 3
    c: Block(g4)
    c: Vertical(g5)
    c: Equal(g1,g5) = 3
    c: Vertical(g6)
    c: Equal(g0,g6) = 3
    c: Block(g6)
    c: Vertical(g7)
    c: Equal(g1,g7) = 3
    c: Vertical(g8)
    c: Equal(g0,g8) = 3
    c: Block(g8)
    c: Vertical(g9)
    c: Equal(g1,g9) = 3
    c: Vertical(g10)
    c: Equal(g0,g10) = 3
    c: Block(g10)
    c: Vertical(g11)
    c: Equal(g1,g11) = 3
    c: Block(g12)
    c: Block(g13)
    c: Block(g14)
    c: Block(g15)
    c: Block(g16)
    c: Block(g17)
    c: Block(g18)
    c: Block(g19)
    c: Block(g20)
    c: Block(g21)
    c: Block(g22)
    c: Block(g23)
    c: Block(g11)
    c: Block(g9)
    c: Block(g7)
    c: Block(g5)
    c: Block(g3)
    c: Block(g1)
    c: Coincident(g24,g0)
    c: Coincident(g24,g12)
    c: Horizontal(g24)
    c: Coincident(g25,g0)
    c: Coincident(g25,g12)
    c: Horizontal(g25)
    c: Coincident(g26,g1)
    c: Coincident(g26,g13)
    c: Horizontal(g26)
    c: Coincident(g27,g1)
    c: Coincident(g27,g13)
    c: Horizontal(g27)
    c: Coincident(g28,g2)
    c: Coincident(g28,g14)
    c: Horizontal(g28)
    c: Coincident(g29,g2)
    c: Coincident(g29,g14)
    c: Horizontal(g29)
    c: Coincident(g30,g3)
    c: Coincident(g30,g15)
    c: Horizontal(g30)
    c: Coincident(g31,g3)
    c: Coincident(g31,g15)
    c: Horizontal(g31)
    c: Coincident(g32,g4)
    c: Coincident(g32,g16)
    c: Horizontal(g32)
    c: Coincident(g33,g4)
    c: Coincident(g33,g16)
    c: Horizontal(g33)
    c: Coincident(g34,g5)
    c: Coincident(g34,g17)
    c: Horizontal(g34)
    c: Coincident(g35,g5)
    c: Coincident(g35,g17)
    c: Horizontal(g35)
    c: Coincident(g36,g6)
    c: Coincident(g36,g19)
    c: Horizontal(g36)
    c: Coincident(g37,g6)
    c: Coincident(g37,g19)
    c: Horizontal(g37)
    c: Coincident(g38,g7)
    c: Coincident(g38,g18)
    c: Horizontal(g38)
    c: Coincident(g39,g7)
    c: Coincident(g39,g18)
    c: Horizontal(g39)
    c: Coincident(g40,g8)
    c: Coincident(g40,g20)
    c: Horizontal(g40)
    c: Coincident(g41,g8)
    c: Coincident(g41,g20)
    c: Horizontal(g41)
    c: Coincident(g42,g9)
    c: Coincident(g42,g23)
    c: Horizontal(g42)
    c: Coincident(g43,g9)
    c: Coincident(g43,g23)
    c: Horizontal(g43)
    c: Coincident(g44,g10)
    c: Coincident(g44,g22)
    c: Horizontal(g44)
    c: Coincident(g45,g10)
    c: Coincident(g45,g22)
    c: Horizontal(g45)
    c: Coincident(g46,g11)
    c: Coincident(g46,g21)
    c: Horizontal(g46)
    c: Coincident(g47,g11)
    c: Coincident(g47,g21)
    c: Horizontal(g47)
FEATURE [Part::Extrusion] Extrude061
  Base = -> Sketch070
  Dir = (1,0,0)
  DirMode = 2
  FaceMakerClass = Part::FaceMakerBullseye
  LengthFwd = 23
  LengthRev = 0
  Placement = pos=(-19,0,0) rot=(0,0,1;0rad)
  Solid = true
  Symmetric = false
FEATURE [Part::Fillet] Fillet052  label="removeToCreateVentalationHoles002"
  Base = -> Extrude061
  Edges = <same value as first occurrence — deduplicated (x6 in doc)>
  Placement = pos=(7,0.02,0) rot=(0,0,1;0rad)
FEATURE [Part::MultiFuse] Fusion130  label="bottom013"
  Shapes = -> [Cut054,Cut034]
FEATURE [Part::Cut] Cut055
  Base = -> Fusion130
  Tool = -> Fillet052
FEATURE [Part::Cylinder] Cylinder054
  Angle = 360
  AttacherType = Attacher::AttachEngine3D
  Height = 20
  Placement = pos=(0,0,36.15) rot=(0,0,1;0rad)
  Radius = 4
FEATURE [Sketcher::SketchObject] Sketch071  label="bottomSketch002"
  FullyConstrained = true
  sketch-geometry (32):
    g0: LineSegment StartX=3.3 StartY=-6.03275e-07 StartZ=0 EndX=98 EndY=-6.03275e-07 EndZ=0
    g1: ArcOfCircle CenterX=98 CenterY=19 CenterZ=0 NormalX=0 NormalY=0 NormalZ=1 AngleXU=0 Radius=19 StartAngle=4.71239 EndAngle=5.71103
    g2: LineSegment StartX=6.3 StartY=8 StartZ=0 EndX=3.3 EndY=8 EndZ=0
    g3: LineSegment StartX=3.3 StartY=8 StartZ=0 EndX=3.3 EndY=-6.03275e-07 EndZ=0
    g4: ArcOfCircle CenterX=8.3 CenterY=5 CenterZ=0 NormalX=0 NormalY=0 NormalZ=1 AngleXU=0 Radius=2 StartAngle=3.14159 EndAngle=4.71239
    g5: LineSegment StartX=6.3 StartY=8 StartZ=0 EndX=6.3 EndY=5 EndZ=0
    g6: ArcOfCircle CenterX=98 CenterY=19 CenterZ=0 NormalX=0 NormalY=0 NormalZ=1 AngleXU=0 Radius=12.7 StartAngle=4.71239 EndAngle=6.28319
    g7: LineSegment StartX=94.7 StartY=3 StartZ=0 EndX=8.3 EndY=3 EndZ=0
    g8-g12: Circle x5 (B-spline internal-alignment scaffolding for g13; pole/knot coordinates omitted)
    g13: BSplineCurve PolesCount=5 KnotsCount=3 Degree=3 IsPeriodic=0
    g14: GeomPoint X=98 Y=6.3 Z=0
    g15: GeomPoint X=96.3938 Y=4.71946 Z=0
    g16: GeomPoint X=94.7 Y=3 Z=0
    g17-g23: Circle x7 (B-spline internal-alignment scaffolding for g24; pole/knot coordinates omitted)
    g24: BSplineCurve PolesCount=7 KnotsCount=5 Degree=3 IsPeriodic=0
    g25-g29: GeomPoint x5 (B-spline internal-alignment scaffolding for g24; pole/knot coordinates omitted)
    g30: ArcOfCircle CenterX=98 CenterY=19 CenterZ=0 NormalX=0 NormalY=0 NormalZ=1 AngleXU=0 Radius=15.7 StartAngle=5.81226 EndAngle=6.28319
    g31: LineSegment StartX=110.7 StartY=19 StartZ=0 EndX=113.7 EndY=19 EndZ=0
  constraints (41):
    c: Horizontal(g0)
    c: Coincident(g1,g0)
    c: Block(g1)
    c: Horizontal(g2)
    c: Distance(g2) = 3
    c: Coincident(g3,g2)
    c: Vertical(g3)
    c: Coincident(g3,g0)
    c: Block(g4)
    c: Block(g2)
    c: Coincident(g5,g2)
    c: Coincident(g5,g4)
    c: Vertical(g5)
    c: Coincident(g6,g1)
    c: Block(g6)
    c: Coincident(g7,g4)
    c: Horizontal(g7)
    c: Block(g0)
    c: Block(g7)
    c: Block(g3)
    c: Coincident(g13,g6)
    c: Weight(g8) = 1
    c: Equal(g8, g9-g12) x4
    c: Coincident(g13,g7)
    c: InternalAlignment(g8-g12 -> g13) x5
    c: InternalAlignment(g14,g13)
    c: InternalAlignment(g15,g13)
    c: InternalAlignment(g16,g13)
    c: Block(g13)
    c: Weight(g17) = 1
    c: Equal(g17, g18-g23) x6
    c: Coincident(g24,g1)
    c: InternalAlignment(g17-g23 -> g24) x7
    c: InternalAlignment(g25-g29 -> g24) x5
    c: Block(g24)
    c: Coincident(g30,g24)
    c: Coincident(g31,g6)
    c: Coincident(g31,g30)
    c: Horizontal(g31)
    c: Block(g31)
    c: Block(g30)
FEATURE [Part::Extrusion] Extrude062  label="bottom014"
  Base = -> Sketch071
  Dir = (0,0,1)
  DirMode = 2
  FaceMakerClass = Part::FaceMakerBullseye
  LengthFwd = 71.4
  LengthRev = 0
  Placement = pos=(0,0,0.3) rot=(0,0,1;0rad)
  Solid = true
  Symmetric = false
FEATURE [Part::Fillet] Fillet054
  Base = -> Extrude062
  Edges = 1 edges r=2.4: [Edge17]
FEATURE [Part::Fillet] Fillet055  label="bottom015"
  Base = -> Fillet054
  Edges = 1 edges r=2.4: [Edge36]
FEATURE [Part::Cylinder] Cylinder055
  Angle = 360
  AttacherType = Attacher::AttachEngine3D
  Height = 10
  Placement = pos=(0,0,36.15) rot=(0,0,1;0rad)
  Radius = 4
FEATURE [Part::MultiFuse] Fusion131  label="removeToCreateHoleForPlugHousing002"
  Placement = pos=(70,19,36.15) rot=(0,1,0;1.5708rad)
  Shapes = -> [Cylinder054,Cylinder055]
FEATURE [Part::Cut] Cut056  label="Bottom001"
  Base = -> Fillet055
  Placement = pos=(9,0,0) rot=(0,0,1;0rad)
  Tool = -> Fusion131
FEATURE [Part::Cut] Cut057
  Base = -> Cut055
  Tool = -> Cut056
FEATURE [Sketcher::SketchObject] Sketch072  label="topSketch021"
  FullyConstrained = true
  sketch-geometry (4):
    g0: ArcOfCircle CenterX=105 CenterY=19 CenterZ=0 NormalX=0 NormalY=0 NormalZ=1 AngleXU=0 Radius=20.6155 StartAngle=5.54125 EndAngle=6.28319
    g1: ArcOfCircle CenterX=105 CenterY=19 CenterZ=0 NormalX=0 NormalY=0 NormalZ=1 AngleXU=0 Radius=13 StartAngle=5.54125 EndAngle=6.28319
    g2: LineSegment StartX=118 StartY=19 StartZ=0 EndX=125.616 EndY=19 EndZ=0
    g3: LineSegment StartX=114.583 StartY=10.2157 StartZ=0 EndX=120.197 EndY=5.06982 EndZ=0
  constraints (7):
    c: Block(g0)
    c: Block(g1)
    c: Coincident(g2,g1)
    c: Coincident(g2,g0)
    c: Horizontal(g2)
    c: Coincident(g3,g1)
    c: Coincident(g3,g0)
FEATURE [Part::Extrusion] Extrude063  label="bottomPlugHousingBit003"
  Base = -> Sketch072
  Dir = (0,0,1)
  DirMode = 2
  FaceMakerClass = Part::FaceMakerBullseye
  LengthFwd = 72
  LengthRev = 0
  Solid = true
  Symmetric = false
FEATURE [Part::Cylinder] Cylinder056
  Angle = 360
  AttacherType = Attacher::AttachEngine3D
  Height = 20
  Placement = pos=(0,0,36.15) rot=(0,0,1;0rad)
  Radius = 14.3
FEATURE [Part::Cylinder] Cylinder057
  Angle = 360
  AttacherType = Attacher::AttachEngine3D
  Height = 10
  Placement = pos=(0,0,36.15) rot=(0,0,1;0rad)
  Radius = 4
FEATURE [Part::Box] Box034  label="removeToCreteHoleForPlugHousing047"
  AttacherType = Attacher::AttachEngine3D
  Height = 28.6
  Length = 20
  Placement = pos=(106.15,0,21.7) rot=(0,0,1;0rad)
  Width = 19
FEATURE [Part::Cylinder] Cylinder058
  Angle = 360
  AttacherType = Attacher::AttachEngine3D
  Height = 20
  Placement = pos=(0,0,36.15) rot=(0,0,1;0rad)
  Radius = 14.3
FEATURE [Part::Cylinder] Cylinder059
  Angle = 360
  AttacherType = Attacher::AttachEngine3D
  Height = 10
  Placement = pos=(0,0,36.15) rot=(0,0,1;0rad)
  Radius = 4
FEATURE [Part::MultiFuse] Fusion134  label="removeToCreteHoleForPlugHousing046"
  Placement = pos=(70,19,36) rot=(0,1,0;1.5708rad)
  Shapes = -> [Cylinder058,Cylinder059]
FEATURE [Part::Cylinder] Cylinder060
  Angle = 360
  AttacherType = Attacher::AttachEngine3D
  Height = 20
  Placement = pos=(0,0,36.15) rot=(0,0,1;0rad)
  Radius = 14
FEATURE [Part::Cylinder] Cylinder061
  Angle = 360
  AttacherType = Attacher::AttachEngine3D
  Height = 10
  Placement = pos=(0,0,36.15) rot=(0,0,1;0rad)
  Radius = 4
FEATURE [Part::MultiFuse] Fusion135  label="removeToCreteHoleForPlugHousing048"
  Placement = pos=(70,19,36) rot=(0,1,0;1.5708rad)
  Shapes = -> [Cylinder060,Cylinder061]
FEATURE [Part::Box] Box035  label="removeToCreteHoleForPlugHousing049"
  AttacherType = Attacher::AttachEngine3D
  Height = 28.6
  Length = 20
  Placement = pos=(106.15,0,21.7) rot=(0,0,1;0rad)
  Width = 19
FEATURE [Part::MultiFuse] Fusion133  label="removeToCreteHoleForPlugHousing045"
  Placement = pos=(0,0,-28.3) rot=(0,0,1;0rad)
  Shapes = -> [Box035,Fusion134]
FEATURE [Part::MultiFuse] Fusion138  label="removeToCreteHoleForPlugHousing051"
  Placement = pos=(70,19,36) rot=(0,1,0;1.5708rad)
  Shapes = -> [Cylinder056,Cylinder057]
FEATURE [Part::MultiFuse] Fusion137  label="removeToCreteHoleForPlugHousing050"
  Placement = pos=(0,0,28.3) rot=(0,0,1;0rad)
  Shapes = -> [Box034,Fusion138]
FEATURE [Part::MultiFuse] Fusion132  label="removeToCreatePlugHousingBottomBit002"
  Shapes = -> [Fusion133,Fusion137]
FEATURE [Part::MultiFuse] Fusion136  label="removeToCreatePlugHousingBottomBit003"
  Shapes = -> [Fusion135,Fusion132]
FEATURE [Part::Cut] Cut058  label="bottomPlugHousingBit002"
  Base = -> Extrude063
  Placement = pos=(-0.09,0,0) rot=(0,0,1;0rad)
  Tool = -> Fusion136
FEATURE [Sketcher::SketchObject] Sketch073  label="bottomSketch003"
  FullyConstrained = true
  sketch-geometry (45):
    g0: LineSegment StartX=6.29999 StartY=8 StartZ=0 EndX=3.29999 EndY=8 EndZ=0
    g1: LineSegment StartX=3.29999 StartY=8 StartZ=0 EndX=3.29999 EndY=-6.03275e-07 EndZ=0
    g2: ArcOfCircle CenterX=8.29999 CenterY=5 CenterZ=0 NormalX=0 NormalY=0 NormalZ=1 AngleXU=0 Radius=2 StartAngle=3.14159 EndAngle=4.71239
    g3: LineSegment StartX=6.29999 StartY=8 StartZ=0 EndX=6.29999 EndY=5 EndZ=0
    g4: ArcOfCircle CenterX=105 CenterY=19 CenterZ=0 NormalX=0 NormalY=0 NormalZ=1 AngleXU=0 Radius=12.7 StartAngle=4.71239 EndAngle=5.94289
    g5-g11: Circle x7 (B-spline internal-alignment scaffolding for g12; pole/knot coordinates omitted)
    g12: BSplineCurve PolesCount=7 KnotsCount=5 Degree=3 IsPeriodic=0
    g13-g17: GeomPoint x5 (B-spline internal-alignment scaffolding for g12; pole/knot coordinates omitted)
    g18: ArcOfCircle CenterX=105 CenterY=19 CenterZ=0 NormalX=0 NormalY=0 NormalZ=1 AngleXU=0 Radius=15.7 StartAngle=5.81226 EndAngle=6.28319
    g19: BSplineCurve PolesCount=5 KnotsCount=3 Degree=3 IsPeriodic=0
    g20: LineSegment StartX=8.29999 StartY=3 StartZ=0 EndX=101.7 EndY=3 EndZ=0
    g21: LineSegment StartX=3.29999 StartY=-6.03275e-07 StartZ=0 EndX=105 EndY=-6.03275e-07 EndZ=0
    g22: LineSegment StartX=120.974 StartY=8.71251 StartZ=0 EndX=122.332 EndY=7.83778 EndZ=0
    g23: LineSegment StartX=105 StartY=-6.03274e-07 StartZ=0 EndX=113 EndY=-6.03274e-07 EndZ=0
    g24: ArcOfCircle CenterX=105 CenterY=19 CenterZ=0 NormalX=0 NormalY=0 NormalZ=1 AngleXU=0 Radius=20.6155 StartAngle=5.11091 EndAngle=5.71103
    g25: ArcOfCircle CenterX=117.7 CenterY=19 CenterZ=0 NormalX=0 NormalY=0 NormalZ=1 AngleXU=0 Radius=3 StartAngle=1.2e-15 EndAngle=2.10468
    g26: Circle CenterX=116.345 CenterY=16.3232 CenterZ=0 NormalX=0 NormalY=0 NormalZ=1 AngleXU=0 Radius=1
    g27: Circle CenterX=117.24 CenterY=15.7584 CenterZ=0 NormalX=0 NormalY=0 NormalZ=1 AngleXU=0 Radius=1
    g28: Circle CenterX=116.972 CenterY=14.7612 CenterZ=0 NormalX=0 NormalY=0 NormalZ=1 AngleXU=0 Radius=1
    g29: BSplineCurve PolesCount=3 KnotsCount=2 Degree=2 IsPeriodic=0
    g30: GeomPoint X=116.345 Y=16.3232 Z=0
    g31: GeomPoint X=116.972 Y=14.7612 Z=0
    g32: Circle CenterX=115.828 CenterY=17.157 CenterZ=0 NormalX=0 NormalY=0 NormalZ=1 AngleXU=0 Radius=1
    g33: Circle CenterX=115.841 CenterY=16.639 CenterZ=0 NormalX=0 NormalY=0 NormalZ=1 AngleXU=0 Radius=1
    g34: Circle CenterX=116.345 CenterY=16.3232 CenterZ=0 NormalX=0 NormalY=0 NormalZ=1 AngleXU=0 Radius=1
    g35: BSplineCurve PolesCount=3 KnotsCount=2 Degree=2 IsPeriodic=0
    g36: GeomPoint X=115.828 Y=17.157 Z=0
    g37: GeomPoint X=116.345 Y=16.3232 Z=0
    g38: LineSegment StartX=115.828 StartY=17.157 StartZ=0 EndX=115.828 EndY=20.8307 EndZ=0
    g39: Circle CenterX=115.828 CenterY=20.8307 CenterZ=0 NormalX=0 NormalY=0 NormalZ=1 AngleXU=0 Radius=1
    g40: Circle CenterX=115.831 CenterY=21.3396 CenterZ=0 NormalX=0 NormalY=0 NormalZ=1 AngleXU=0 Radius=1
    g41: Circle CenterX=116.173 CenterY=21.5825 CenterZ=0 NormalX=0 NormalY=0 NormalZ=1 AngleXU=0 Radius=1
    g42: BSplineCurve PolesCount=3 KnotsCount=2 Degree=2 IsPeriodic=0
    g43: GeomPoint X=115.828 Y=20.8307 Z=0
    g44: GeomPoint X=116.173 Y=21.5825 Z=0
  constraints (70):
    c: Horizontal(g0)
    c: Distance(g0) = 3
    c: Coincident(g1,g0)
    c: Vertical(g1)
    c: Block(g2)
    c: Block(g0)
    c: Coincident(g3,g0)
    c: Coincident(g3,g2)
    c: Vertical(g3)
    c: Block(g1)
    c: Block(g4)
    c: Coincident(g19,g4)
    c: Block(g19)
    c: Equal(g5, g6-g11) x6
    c: InternalAlignment(g5-g11 -> g12) x7
    c: InternalAlignment(g13-g17 -> g12) x5
    c: Block(g12)
    c: Coincident(g18,g12)
    c: Block(g18)
    c: Coincident(g20,g2)
    c: Coincident(g20,g19)
    c: Horizontal(g20)
    c: Distance(g20) = 93.4
    c: Coincident(g21,g1)
    c: Horizontal(g21)
    c: Distance(g21) = 101.7
    c: Horizontal(g23)
    c: Distance(g23) = 8
    c: Coincident(g24,g23)
    c: Block(g23)
    c: Coincident(g22,g24)
    c: Block(g24)
    c: Block(g22)
    c: Distance(g22) = 1.61553
    c: Coincident(g25,g18)
    c: Block(g25)
    c: Weight(g26) = 1
    c: Equal(g26,g27)
    c: Equal(g26,g28)
    c: Coincident(g29,g4)
    c: InternalAlignment(g26,g29)
    c: InternalAlignment(g27,g29)
    c: InternalAlignment(g28,g29)
    c: InternalAlignment(g30,g29)
    c: InternalAlignment(g31,g29)
    c: Block(g29)
    c: Weight(g32) = 1
    c: Equal(g32,g33)
    c: Equal(g32,g34)
    c: Coincident(g35,g29)
    c: InternalAlignment(g32,g35)
    c: InternalAlignment(g33,g35)
    c: InternalAlignment(g34,g35)
    c: InternalAlignment(g36,g35)
    c: InternalAlignment(g37,g35)
    c: Block(g35)
    c: Coincident(g38,g35)
    c: Vertical(g38)
    c: Block(g38)
    c: Coincident(g42,g38)
    c: Weight(g39) = 1
    c: Equal(g39,g40)
    c: Equal(g39,g41)
    c: Coincident(g42,g25)
    c: InternalAlignment(g39,g42)
    c: InternalAlignment(g40,g42)
    c: InternalAlignment(g41,g42)
    c: InternalAlignment(g43,g42)
    c: InternalAlignment(g44,g42)
    c: Block(g42)
FEATURE [Part::Extrusion] Extrude064  label="bottom016"
  Base = -> Sketch073
  Dir = (0,0,1)
  DirMode = 2
  FaceMakerClass = Part::FaceMakerBullseye
  LengthFwd = 71.4
  LengthRev = 0
  Placement = pos=(0,0,0.3) rot=(0,0,1;0rad)
  Solid = true
  Symmetric = false
FEATURE [Part::Revolution] Revolve157  label="removeToCreateScrewAndThreadedInsertHole063"
  Angle = 360
  Axis = (0,1,0)
  Base = (0,0,0)
  FaceMakerClass = Part::FaceMakerBullseye
  Placement = pos=(12.5,0,10) rot=(0,0,1;0rad)
  Solid = false
  Source = -> Face141
  Symmetric = false
FEATURE [Sketcher::SketchObject] Sketch074
  FullyConstrained = true
  Placement = pos=(117,19,0) rot=(0.57735,0.57735,0.57735;2.0944rad)
  sketch-geometry (48):
    g0: LineSegment StartX=-49.19 StartY=69.25 StartZ=0 EndX=-49.19 EndY=66.25 EndZ=0
    g1: LineSegment StartX=-49.19 StartY=63.5 StartZ=0 EndX=-49.19 EndY=60.5 EndZ=0
    g2: LineSegment StartX=-49.19 StartY=57.75 StartZ=0 EndX=-49.19 EndY=54.75 EndZ=0
    g3: LineSegment StartX=-49.19 StartY=52 StartZ=0 EndX=-49.19 EndY=49 EndZ=0
    g4: LineSegment StartX=-49.19 StartY=46.25 StartZ=0 EndX=-49.19 EndY=43.25 EndZ=0
    g5: LineSegment StartX=-49.19 StartY=40.5 StartZ=0 EndX=-49.19 EndY=37.5 EndZ=0
    g6: LineSegment StartX=-49.19 StartY=34.5 StartZ=0 EndX=-49.19 EndY=31.5 EndZ=0
    g7: LineSegment StartX=-49.19 StartY=28.75 StartZ=0 EndX=-49.19 EndY=25.75 EndZ=0
    g8: LineSegment StartX=-49.19 StartY=23 StartZ=0 EndX=-49.19 EndY=20 EndZ=0
    g9: LineSegment StartX=-49.19 StartY=17.25 StartZ=0 EndX=-49.19 EndY=14.25 EndZ=0
    g10: LineSegment StartX=-49.19 StartY=11.5 StartZ=0 EndX=-49.19 EndY=8.5 EndZ=0
    g11: LineSegment StartX=-49.19 StartY=5.75 StartZ=0 EndX=-49.19 EndY=2.75 EndZ=0
    g12: ArcOfCircle CenterX=-1.5 CenterY=67.75 CenterZ=0 NormalX=0 NormalY=0 NormalZ=1 AngleXU=0 Radius=1.5 StartAngle=4.71239 EndAngle=7.85398
    g13: ArcOfCircle CenterX=-1.5 CenterY=62 CenterZ=0 NormalX=0 NormalY=0 NormalZ=1 AngleXU=0 Radius=1.5 StartAngle=4.71239 EndAngle=7.85398
    g14: ArcOfCircle CenterX=-1.5 CenterY=56.25 CenterZ=0 NormalX=0 NormalY=0 NormalZ=1 AngleXU=0 Radius=1.5 StartAngle=4.71239 EndAngle=7.85398
    g15: ArcOfCircle CenterX=-11.49 CenterY=50.5 CenterZ=0 NormalX=0 NormalY=0 NormalZ=1 AngleXU=0 Radius=1.5 StartAngle=4.71239 EndAngle=7.85398
    g16: ArcOfCircle CenterX=-16.28 CenterY=44.75 CenterZ=0 NormalX=0 NormalY=0 NormalZ=1 AngleXU=0 Radius=1.5 StartAngle=4.71239 EndAngle=7.85398
    g17: ArcOfCircle CenterX=-18.2337 CenterY=39 CenterZ=0 NormalX=0 NormalY=0 NormalZ=1 AngleXU=0 Radius=1.5 StartAngle=4.71485 EndAngle=7.85398
    g18: ArcOfCircle CenterX=-16.2837 CenterY=27.25 CenterZ=0 NormalX=0 NormalY=0 NormalZ=1 AngleXU=0 Radius=1.5 StartAngle=4.71485 EndAngle=7.85398
    g19: ArcOfCircle CenterX=-18.2337 CenterY=33 CenterZ=0 NormalX=0 NormalY=0 NormalZ=1 AngleXU=0 Radius=1.5 StartAngle=4.71485 EndAngle=7.85398
    g20: ArcOfCircle CenterX=-11.49 CenterY=21.5 CenterZ=0 NormalX=0 NormalY=0 NormalZ=1 AngleXU=0 Radius=1.5 StartAngle=4.71239 EndAngle=7.85398
    g21: ArcOfCircle CenterX=-1.5 CenterY=4.25 CenterZ=0 NormalX=0 NormalY=0 NormalZ=1 AngleXU=0 Radius=1.5 StartAngle=4.71239 EndAngle=7.85398
    g22: ArcOfCircle CenterX=-1.5 CenterY=10 CenterZ=0 NormalX=0 NormalY=0 NormalZ=1 AngleXU=0 Radius=1.5 StartAngle=4.71239 EndAngle=7.85398
    g23: ArcOfCircle CenterX=-1.5 CenterY=15.75 CenterZ=0 NormalX=0 NormalY=0 NormalZ=1 AngleXU=0 Radius=1.5 StartAngle=4.71239 EndAngle=7.85398
    g24: LineSegment StartX=-49.19 StartY=69.25 StartZ=0 EndX=-1.5 EndY=69.25 EndZ=0
    g25: LineSegment StartX=-49.19 StartY=66.25 StartZ=0 EndX=-1.5 EndY=66.25 EndZ=0
    g26: LineSegment StartX=-49.19 StartY=63.5 StartZ=0 EndX=-1.5 EndY=63.5 EndZ=0
    g27: LineSegment StartX=-49.19 StartY=60.5 StartZ=0 EndX=-1.5 EndY=60.5 EndZ=0
    g28: LineSegment StartX=-49.19 StartY=57.75 StartZ=0 EndX=-1.5 EndY=57.75 EndZ=0
    g29: LineSegment StartX=-49.19 StartY=54.75 StartZ=0 EndX=-1.5 EndY=54.75 EndZ=0
    g30: LineSegment StartX=-49.19 StartY=52 StartZ=0 EndX=-11.49 EndY=52 EndZ=0
    g31: LineSegment StartX=-49.19 StartY=49 StartZ=0 EndX=-11.49 EndY=49 EndZ=0
    g32: LineSegment StartX=-49.19 StartY=46.25 StartZ=0 EndX=-16.28 EndY=46.25 EndZ=0
    g33: LineSegment StartX=-49.19 StartY=43.25 StartZ=0 EndX=-16.28 EndY=43.25 EndZ=0
    g34: LineSegment StartX=-49.19 StartY=40.5 StartZ=0 EndX=-18.2337 EndY=40.5 EndZ=0
    g35: LineSegment StartX=-49.19 StartY=37.5 StartZ=0 EndX=-18.23 EndY=37.5 EndZ=0
    g36: LineSegment StartX=-49.19 StartY=34.5 StartZ=0 EndX=-18.2337 EndY=34.5 EndZ=0
    g37: LineSegment StartX=-49.19 StartY=31.5 StartZ=0 EndX=-18.23 EndY=31.5 EndZ=0
    g38: LineSegment StartX=-49.19 StartY=28.75 StartZ=0 EndX=-16.2837 EndY=28.75 EndZ=0
    g39: LineSegment StartX=-49.19 StartY=25.75 StartZ=0 EndX=-16.28 EndY=25.75 EndZ=0
    g40: LineSegment StartX=-49.19 StartY=23 StartZ=0 EndX=-11.49 EndY=23 EndZ=0
    g41: LineSegment StartX=-49.19 StartY=20 StartZ=0 EndX=-11.49 EndY=20 EndZ=0
    g42: LineSegment StartX=-49.19 StartY=17.25 StartZ=0 EndX=-1.5 EndY=17.25 EndZ=0
    g43: LineSegment StartX=-49.19 StartY=14.25 StartZ=0 EndX=-1.5 EndY=14.25 EndZ=0
    g44: LineSegment StartX=-49.19 StartY=11.5 StartZ=0 EndX=-1.5 EndY=11.5 EndZ=0
    g45: LineSegment StartX=-49.19 StartY=8.5 StartZ=0 EndX=-1.5 EndY=8.5 EndZ=0
    g46: LineSegment StartX=-49.19 StartY=5.75 StartZ=0 EndX=-1.5 EndY=5.75 EndZ=0
    g47: LineSegment StartX=-49.19 StartY=2.75 StartZ=0 EndX=-1.5 EndY=2.75 EndZ=0
  constraints (120):
    c: Vertical(g0)
    c: Distance(g0) = 3
    c: Block(g0)
    c: Vertical(g1)
    c: Distance(g1) = 3
    c: Vertical(g2)
    c: Equal(g0,g2) = 3
    c: Block(g2)
    c: Vertical(g3)
    c: Equal(g1,g3) = 3
    c: Vertical(g4)
    c: Equal(g0,g4) = 3
    c: Block(g4)
    c: Vertical(g5)
    c: Equal(g1,g5) = 3
    c: Vertical(g6)
    c: Equal(g0,g6) = 3
    c: Block(g6)
    c: Vertical(g7)
    c: Equal(g1,g7) = 3
    c: Vertical(g8)
    c: Equal(g0,g8) = 3
    c: Block(g8)
    c: Vertical(g9)
    c: Equal(g1,g9) = 3
    c: Vertical(g10)
    c: Equal(g0,g10) = 3
    c: Block(g10)
    c: Vertical(g11)
    c: Equal(g1,g11) = 3
    c: Block(g12)
    c: Block(g13)
    c: Block(g14)
    c: Block(g15)
    c: Block(g16)
    c: Block(g17)
    c: Block(g18)
    c: Block(g19)
    c: Block(g20)
    c: Block(g21)
    c: Block(g22)
    c: Block(g23)
    c: Block(g11)
    c: Block(g9)
    c: Block(g7)
    c: Block(g5)
    c: Block(g3)
    c: Block(g1)
    c: Coincident(g24,g0)
    c: Coincident(g24,g12)
    c: Horizontal(g24)
    c: Coincident(g25,g0)
    c: Coincident(g25,g12)
    c: Horizontal(g25)
    c: Coincident(g26,g1)
    c: Coincident(g26,g13)
    c: Horizontal(g26)
    c: Coincident(g27,g1)
    c: Coincident(g27,g13)
    c: Horizontal(g27)
    c: Coincident(g28,g2)
    c: Coincident(g28,g14)
    c: Horizontal(g28)
    c: Coincident(g29,g2)
    c: Coincident(g29,g14)
    c: Horizontal(g29)
    c: Coincident(g30,g3)
    c: Coincident(g30,g15)
    c: Horizontal(g30)
    c: Coincident(g31,g3)
    c: Coincident(g31,g15)
    c: Horizontal(g31)
    c: Coincident(g32,g4)
    c: Coincident(g32,g16)
    c: Horizontal(g32)
    c: Coincident(g33,g4)
    c: Coincident(g33,g16)
    c: Horizontal(g33)
    c: Coincident(g34,g5)
    c: Coincident(g34,g17)
    c: Horizontal(g34)
    c: Coincident(g35,g5)
    c: Coincident(g35,g17)
    c: Horizontal(g35)
    c: Coincident(g36,g6)
    c: Coincident(g36,g19)
    c: Horizontal(g36)
    c: Coincident(g37,g6)
    c: Coincident(g37,g19)
    c: Horizontal(g37)
    c: Coincident(g38,g7)
    c: Coincident(g38,g18)
    c: Horizontal(g38)
    c: Coincident(g39,g7)
    c: Coincident(g39,g18)
    c: Horizontal(g39)
    c: Coincident(g40,g8)
    c: Coincident(g40,g20)
    c: Horizontal(g40)
    c: Coincident(g41,g8)
    c: Coincident(g41,g20)
    c: Horizontal(g41)
    c: Coincident(g42,g9)
    c: Coincident(g42,g23)
    c: Horizontal(g42)
    c: Coincident(g43,g9)
    c: Coincident(g43,g23)
    c: Horizontal(g43)
    c: Coincident(g44,g10)
    c: Coincident(g44,g22)
    c: Horizontal(g44)
    c: Coincident(g45,g10)
    c: Coincident(g45,g22)
    c: Horizontal(g45)
    c: Coincident(g46,g11)
    c: Coincident(g46,g21)
    c: Horizontal(g46)
    c: Coincident(g47,g11)
    c: Coincident(g47,g21)
    c: Horizontal(g47)
FEATURE [Part::Extrusion] Extrude065
  Base = -> Sketch074
  Dir = (1,0,0)
  DirMode = 2
  FaceMakerClass = Part::FaceMakerBullseye
  LengthFwd = 23
  LengthRev = 0
  Placement = pos=(-19,0,0) rot=(0,0,1;0rad)
  Solid = true
  Symmetric = false
FEATURE [Part::Fillet] Fillet056  label="removeToCreateVentalationHoles003"
  Base = -> Extrude065
  Edges = <same value as first occurrence — deduplicated (x6 in doc)>
  Placement = pos=(7,0.02,0) rot=(0,0,1;0rad)
FEATURE [Part::Revolution] Revolve158  label="removeToCreateScrewAndThreadedInsertHole065"
  Angle = 360
  Axis = (0,1,0)
  Base = (0,0,0)
  FaceMakerClass = Part::FaceMakerBullseye
  Placement = pos=(12.5,0,62) rot=(0,0,1;0rad)
  Solid = false
  Source = -> Face146
  Symmetric = false
FEATURE [Part::Revolution] Revolve159  label="removeToCreateScrewAndThreadedInsertHole066"
  Angle = 360
  Axis = (0,1,0)
  Base = (0,0,0)
  FaceMakerClass = Part::FaceMakerBullseye
  Placement = pos=(89.5,0,68.5) rot=(0,0,1;0rad)
  Solid = false
  Source = -> Face143
  Symmetric = false
FEATURE [Part::Revolution] Revolve160  label="removeToCreateScrewAndThreadedInsertHole067"
  Angle = 360
  Axis = (0,1,0)
  Base = (0,0,0)
  FaceMakerClass = Part::FaceMakerBullseye
  Placement = pos=(89.5,0,3.5) rot=(0,0,1;0rad)
  Solid = false
  Source = -> Face142
  Symmetric = false
FEATURE [Part::Revolution] Revolve161  label="removeToCreateScrewAndThreadedInsertHole068"
  Angle = 360
  Axis = (0,1,0)
  Base = (0,0,0)
  FaceMakerClass = Part::FaceMakerBullseye
  Placement = pos=(109.5,4.7,3.5) rot=(0,0,1;0rad)
  Solid = false
  Source = -> Face145
  Symmetric = false
FEATURE [Part::Revolution] Revolve162  label="removeToCreateScrewAndThreadedInsertHole069"
  Angle = 360
  Axis = (0,1,0)
  Base = (0,0,0)
  FaceMakerClass = Part::FaceMakerBullseye
  Placement = pos=(109.5,4.7,68.5) rot=(0,0,1;0rad)
  Solid = false
  Source = -> Face144
  Symmetric = false
FEATURE [Part::MultiFuse] Fusion141  label="removeToCreateScrewAndThreadedInsertHole064"
  Shapes = -> [Revolve162,Revolve161,Revolve160,Revolve159,Revolve158,Revolve157]
FEATURE [Part::Cylinder] Cylinder062
  Angle = 360
  AttacherType = Attacher::AttachEngine3D
  Height = 20
  Placement = pos=(0,0,36.15) rot=(0,0,1;0rad)
  Radius = 14
FEATURE [Part::Cylinder] Cylinder063
  Angle = 360
  AttacherType = Attacher::AttachEngine3D
  Height = 10
  Placement = pos=(0,0,36.15) rot=(0,0,1;0rad)
  Radius = 4
FEATURE [Part::MultiFuse] Fusion139  label="removeToCreteHoleForPlugHousing052"
  Placement = pos=(70,19,36) rot=(0,1,0;1.5708rad)
  Shapes = -> [Cylinder062,Cylinder063]
FEATURE [Part::Cut] Cut060  label="bottom017"
  Base = -> Extrude064
  Tool = -> Fusion139
FEATURE [Part::Cut] Cut061  label="bottom019"
  Base = -> Cut060
  Tool = -> Fusion141
FEATURE [Part::MultiFuse] Fusion140  label="bottom018"
  Shapes = -> [Cut061,Cut058]
FEATURE [Part::Cut] Cut059  label="bottom020"
  Base = -> Fusion140
  Tool = -> Fillet056
FEATURE [Part::Box] Box036  label="Cube021"
  AttacherType = Attacher::AttachEngine3D
  Height = 80
  Length = 26
  Placement = pos=(0,-1,-5) rot=(0,0,1;0rad)
  Width = 11
FEATURE [Part::Cut] Cut062  label="removeFromBottom002"
  Base = -> Cut057
  Tool = -> Box036
FEATURE [Part::Cut] Cut063
  Base = -> Cut059
  Tool = -> Cut062
FEATURE [Part::Cut] Cut064  label="pcbStands"
  Base = -> Fusion095
  Tool = -> Fusion127
FEATURE [Sketcher::SketchObject] Sketch075  label="topSketch022"
  FullyConstrained = true
  sketch-geometry (6):
    g0: LineSegment StartX=19 StartY=38 StartZ=0 EndX=117 EndY=38 EndZ=0
    g1: ArcOfCircle CenterX=19 CenterY=19 CenterZ=0 NormalX=0 NormalY=0 NormalZ=1 AngleXU=0 Radius=19 StartAngle=1.5708 EndAngle=3.14159
    g2: LineSegment StartX=117 StartY=38 StartZ=0 EndX=117 EndY=19 EndZ=0
    g3: LineSegment StartX=98 StartY=1.0161e-12 StartZ=0 EndX=5.22862e-06 EndY=1.0161e-12 EndZ=0
    g4: LineSegment StartX=5.22862e-06 StartY=19 StartZ=0 EndX=5.22862e-06 EndY=1.0161e-12 EndZ=0
    g5: ArcOfCircle CenterX=98 CenterY=19 CenterZ=0 NormalX=0 NormalY=0 NormalZ=1 AngleXU=0 Radius=19 StartAngle=4.71239 EndAngle=6.28319
  constraints (16):
    c: Horizontal(g0)
    c: Distance(g0) = 98
    c: Coincident(g1,g0)
    c: Block(g1)
    c: Coincident(g2,g0)
    c: Vertical(g2)
    c: Distance(g2) = 19
    c: Horizontal(g3)
    c: Coincident(g4,g1)
    c: Vertical(g4)
    c: Coincident(g3,g4)
    c: Block(g3)
    c: Coincident(g5,g2)
    c: Coincident(g5,g3)
    c: Block(g0)
    c: Block(g5)
FEATURE [Part::Extrusion] Extrude067  label="sideB003"
  Base = -> Sketch075
  Dir = (0,0,1)
  DirMode = 2
  FaceMakerClass = Part::FaceMakerBullseye
  LengthFwd = 3
  LengthRev = 0
  Placement = pos=(0,0,71.7) rot=(0,0,1;0rad)
  Solid = true
  Symmetric = false
FEATURE [Sketcher::SketchObject] Sketch076  label="topSketch023"
  FullyConstrained = true
  sketch-geometry (6):
    g0: LineSegment StartX=19 StartY=38 StartZ=0 EndX=117 EndY=38 EndZ=0
    g1: ArcOfCircle CenterX=19 CenterY=19 CenterZ=0 NormalX=0 NormalY=0 NormalZ=1 AngleXU=0 Radius=19 StartAngle=1.5708 EndAngle=3.14159
    g2: LineSegment StartX=117 StartY=38 StartZ=0 EndX=117 EndY=19 EndZ=0
    g3: LineSegment StartX=98 StartY=1.0161e-12 StartZ=0 EndX=5.22862e-06 EndY=1.0161e-12 EndZ=0
    g4: LineSegment StartX=5.22862e-06 StartY=19 StartZ=0 EndX=5.22862e-06 EndY=1.0161e-12 EndZ=0
    g5: ArcOfCircle CenterX=98 CenterY=19 CenterZ=0 NormalX=0 NormalY=0 NormalZ=1 AngleXU=0 Radius=19 StartAngle=4.71239 EndAngle=6.28319
  constraints (16):
    c: Horizontal(g0)
    c: Distance(g0) = 98
    c: Coincident(g1,g0)
    c: Block(g1)
    c: Coincident(g2,g0)
    c: Vertical(g2)
    c: Distance(g2) = 19
    c: Horizontal(g3)
    c: Coincident(g4,g1)
    c: Vertical(g4)
    c: Coincident(g3,g4)
    c: Block(g3)
    c: Coincident(g5,g2)
    c: Coincident(g5,g3)
    c: Block(g0)
    c: Block(g5)
FEATURE [Part::Extrusion] Extrude066  label="sideA003"
  Base = -> Sketch076
  Dir = (0,0,1)
  DirMode = 2
  FaceMakerClass = Part::FaceMakerBullseye
  LengthFwd = 3
  LengthRev = 0
  Placement = pos=(0,0,-2.7) rot=(0,0,1;0rad)
  Solid = true
  Symmetric = false
FEATURE [Part::MultiFuse] Fusion142  label="removeFromBottom003"
  Placement = pos=(2,0,0) rot=(0,0,1;0rad)
  Shapes = -> [Extrude066,Extrude067]
FEATURE [Part::Cut] Cut065  label="screwRetainers002"
  Base = -> Fusion096
  Tool = -> Fusion142
FEATURE [Sketcher::SketchObject] Sketch077
  FullyConstrained = true
  Placement = pos=(117,19,0) rot=(0.57735,0.57735,0.57735;2.0944rad)
  sketch-geometry (8):
    g0: LineSegment StartX=-49.19 StartY=63.5 StartZ=0 EndX=-49.19 EndY=60.5 EndZ=0
    g1: LineSegment StartX=-49.19 StartY=11.5 StartZ=0 EndX=-49.19 EndY=8.5 EndZ=0
    g2: ArcOfCircle CenterX=-1.5 CenterY=62 CenterZ=0 NormalX=0 NormalY=0 NormalZ=1 AngleXU=0 Radius=1.5 StartAngle=4.71239 EndAngle=7.85398
    g3: ArcOfCircle CenterX=-1.5 CenterY=10 CenterZ=0 NormalX=0 NormalY=0 NormalZ=1 AngleXU=0 Radius=1.5 StartAngle=4.71239 EndAngle=7.85398
    g4: LineSegment StartX=-49.19 StartY=63.5 StartZ=0 EndX=-1.5 EndY=63.5 EndZ=0
    g5: LineSegment StartX=-49.19 StartY=60.5 StartZ=0 EndX=-1.5 EndY=60.5 EndZ=0
    g6: LineSegment StartX=-49.19 StartY=11.5 StartZ=0 EndX=-1.5 EndY=11.5 EndZ=0
    g7: LineSegment StartX=-49.19 StartY=8.5 StartZ=0 EndX=-1.5 EndY=8.5 EndZ=0
  constraints (19):
    c: Vertical(g0)
    c: Distance(g0) = 3
    c: Vertical(g1)
    c: Block(g1)
    c: Block(g2)
    c: Block(g3)
    c: Block(g0)
    c: Coincident(g4,g0)
    c: Coincident(g4,g2)
    c: Horizontal(g4)
    c: Coincident(g5,g0)
    c: Coincident(g5,g2)
    c: Horizontal(g5)
    c: Coincident(g6,g1)
    c: Coincident(g6,g3)
    c: Horizontal(g6)
    c: Coincident(g7,g1)
    c: Coincident(g7,g3)
    c: Horizontal(g7)
FEATURE [Part::Extrusion] Extrude068
  Base = -> Sketch077
  Dir = (1,0,0)
  DirMode = 2
  FaceMakerClass = Part::FaceMakerBullseye
  LengthFwd = 10
  LengthRev = 0
  Solid = true
  Symmetric = false
FEATURE [Part::Fillet] Fillet057  label="removeFromtMoreFrontCaseScrewRetainers002"
  Base = -> Extrude068
  Edges = 4 edges r=1.49: [Edge6,Edge11,Edge18,Edge23]
  Placement = pos=(-12,0,0) rot=(0,0,1;0rad)
FEATURE [Sketcher::SketchObject] Sketch078
  FullyConstrained = true
  Placement = pos=(117,19,0) rot=(0.57735,0.57735,0.57735;2.0944rad)
  sketch-geometry (8):
    g0: LineSegment StartX=-49.19 StartY=69.25 StartZ=0 EndX=-49.19 EndY=66.25 EndZ=0
    g1: LineSegment StartX=-49.19 StartY=5.75 StartZ=0 EndX=-49.19 EndY=2.75 EndZ=0
    g2: ArcOfCircle CenterX=-1.5 CenterY=67.75 CenterZ=0 NormalX=0 NormalY=0 NormalZ=1 AngleXU=0 Radius=1.5 StartAngle=4.71239 EndAngle=7.85398
    g3: ArcOfCircle CenterX=-1.5 CenterY=4.25 CenterZ=0 NormalX=0 NormalY=0 NormalZ=1 AngleXU=0 Radius=1.5 StartAngle=4.71239 EndAngle=7.85398
    g4: LineSegment StartX=-49.19 StartY=69.25 StartZ=0 EndX=-1.5 EndY=69.25 EndZ=0
    g5: LineSegment StartX=-49.19 StartY=66.25 StartZ=0 EndX=-1.5 EndY=66.25 EndZ=0
    g6: LineSegment StartX=-49.19 StartY=5.75 StartZ=0 EndX=-1.5 EndY=5.75 EndZ=0
    g7: LineSegment StartX=-49.19 StartY=2.75 StartZ=0 EndX=-1.5 EndY=2.75 EndZ=0
  constraints (19):
    c: Vertical(g0)
    c: Distance(g0) = 3
    c: Block(g0)
    c: Vertical(g1)
    c: Block(g2)
    c: Block(g3)
    c: Block(g1)
    c: Coincident(g4,g0)
    c: Coincident(g4,g2)
    c: Horizontal(g4)
    c: Coincident(g5,g0)
    c: Coincident(g5,g2)
    c: Horizontal(g5)
    c: Coincident(g6,g1)
    c: Coincident(g6,g3)
    c: Horizontal(g6)
    c: Coincident(g7,g1)
    c: Coincident(g7,g3)
    c: Horizontal(g7)
FEATURE [Part::Extrusion] Extrude069
  Base = -> Sketch078
  Dir = (1,0,0)
  DirMode = 2
  FaceMakerClass = Part::FaceMakerBullseye
  LengthFwd = 10
  LengthRev = 0
  Solid = true
  Symmetric = false
FEATURE [Part::Fillet] Fillet058  label="removeFromtMoreFrontCaseScrewRetainers003"
  Base = -> Extrude069
  Edges = 4 edges r=1.49: [Edge6,Edge11,Edge18,Edge23]
  Placement = pos=(-4,0,0) rot=(0,0,1;0rad)
FEATURE [Part::Cut] Cut066
  Base = -> Cut065
  Tool = -> Fillet058
FEATURE [Part::Cut] Cut067  label="screwPillars"
  Base = -> Cut066
  Tool = -> Fillet057
FEATURE [Part::MultiFuse] Fusion143  label="bottom021"
  Shapes = -> [Cut031,Cut063]
FEATURE [Part::Cylinder] Cylinder
  Angle = 360
  AttacherType = Attacher::AttachEngine3D
  Height = 10
  Placement = pos=(20.65,12,4.68) rot=(1,0,0;1.5708rad)
  Radius = 2
FEATURE [Part::Cylinder] Cylinder064
  Angle = 360
  AttacherType = Attacher::AttachEngine3D
  Height = 10
  Placement = pos=(20.65,12,67.38) rot=(1,0,0;1.5708rad)
  Radius = 2
FEATURE [Part::Cylinder] Cylinder065
  Angle = 360
  AttacherType = Attacher::AttachEngine3D
  Height = 10
  Placement = pos=(77.15,12,67.38) rot=(1,0,0;1.5708rad)
  Radius = 2
FEATURE [Part::Cylinder] Cylinder066
  Angle = 360
  AttacherType = Attacher::AttachEngine3D
  Height = 10
  Placement = pos=(77.15,12,4.68) rot=(1,0,0;1.5708rad)
  Radius = 2
FEATURE [Part::MultiFuse] Fusion144  label="removeFromThreadedInsertHousing"
  Shapes = -> [Cylinder065,Cylinder064,Cylinder,Cylinder066]
FEATURE [Part::Cut] Cut068  label="pcbStands001"
  Base = -> Cut064
  Tool = -> Fusion144
FEATURE [Part::MultiFuse] Fusion145
  Shapes = -> [Cut068,Fusion143]
FEATURE [Part::MultiFuse] Fusion146
  Shapes = -> [Fusion145]
FEATURE [Part::MultiFuse] Fusion147  label="bottom022"
  Shapes = -> [Cut067,Fusion146]
FEATURE [Part::MultiFuse] Fusion148  label="casePillars005"
  Shapes = -> [Cut047,Fusion092]
FEATURE [Part::MultiFuse] Fusion149  label="bottom023"
  Shapes = -> [Fusion124,Fusion113,Fusion147]
FEATURE [Part::MultiFuse] Fusion150  label="topBits"
  Shapes = -> [Cut025,Fusion148,Cut030,Fillet034]
FEATURE [Part::Feature] Face149 .. Face152  x4 (patterned run collapsed; names and placements below)
  shape: bbox 3.2 x 1.5 x 2e-07 mm, 1 faces, 0 solids (baked)
FEATURE [Part::Feature] Face153
  shape: bbox 3.6 x 3.2 x 2e-07 mm, 1 faces, 0 solids (baked)
FEATURE [Part::Feature] Face154
  shape: bbox 3.6 x 3.2 x 2e-07 mm, 1 faces, 0 solids (baked)
FEATURE [Sketcher::SketchObject] Sketch079  label="topSketch024"
  FullyConstrained = true
  sketch-geometry (6):
    g0: LineSegment StartX=19 StartY=38 StartZ=0 EndX=117 EndY=38 EndZ=0
    g1: ArcOfCircle CenterX=19 CenterY=19 CenterZ=0 NormalX=0 NormalY=0 NormalZ=1 AngleXU=0 Radius=19 StartAngle=1.5708 EndAngle=3.14159
    g2: LineSegment StartX=117 StartY=38 StartZ=0 EndX=117 EndY=19 EndZ=0
    g3: LineSegment StartX=98 StartY=1.0161e-12 StartZ=0 EndX=5.22862e-06 EndY=1.0161e-12 EndZ=0
    g4: LineSegment StartX=5.22862e-06 StartY=19 StartZ=0 EndX=5.22862e-06 EndY=1.0161e-12 EndZ=0
    g5: ArcOfCircle CenterX=98 CenterY=19 CenterZ=0 NormalX=0 NormalY=0 NormalZ=1 AngleXU=0 Radius=19 StartAngle=4.71239 EndAngle=6.28319
  constraints (16):
    c: Horizontal(g0)
    c: Distance(g0) = 98
    c: Coincident(g1,g0)
    c: Block(g1)
    c: Coincident(g2,g0)
    c: Vertical(g2)
    c: Distance(g2) = 19
    c: Horizontal(g3)
    c: Coincident(g4,g1)
    c: Vertical(g4)
    c: Coincident(g3,g4)
    c: Block(g3)
    c: Coincident(g5,g2)
    c: Coincident(g5,g3)
    c: Block(g0)
    c: Block(g5)
FEATURE [Sketcher::SketchObject] Sketch080  label="topSketch025"
  FullyConstrained = true
  sketch-geometry (6):
    g0: LineSegment StartX=19 StartY=38 StartZ=0 EndX=117 EndY=38 EndZ=0
    g1: ArcOfCircle CenterX=19 CenterY=19 CenterZ=0 NormalX=0 NormalY=0 NormalZ=1 AngleXU=0 Radius=19 StartAngle=1.5708 EndAngle=3.14159
    g2: LineSegment StartX=117 StartY=38 StartZ=0 EndX=117 EndY=19 EndZ=0
    g3: LineSegment StartX=98 StartY=1.0161e-12 StartZ=0 EndX=5.22862e-06 EndY=1.0161e-12 EndZ=0
    g4: LineSegment StartX=5.22862e-06 StartY=19 StartZ=0 EndX=5.22862e-06 EndY=1.0161e-12 EndZ=0
    g5: ArcOfCircle CenterX=98 CenterY=19 CenterZ=0 NormalX=0 NormalY=0 NormalZ=1 AngleXU=0 Radius=19 StartAngle=4.71239 EndAngle=6.28319
  constraints (16):
    c: Horizontal(g0)
    c: Distance(g0) = 98
    c: Coincident(g1,g0)
    c: Block(g1)
    c: Coincident(g2,g0)
    c: Vertical(g2)
    c: Distance(g2) = 19
    c: Horizontal(g3)
    c: Coincident(g4,g1)
    c: Vertical(g4)
    c: Coincident(g3,g4)
    c: Block(g3)
    c: Coincident(g5,g2)
    c: Coincident(g5,g3)
    c: Block(g0)
    c: Block(g5)
FEATURE [Part::Extrusion] Extrude070  label="sideA004"
  Base = -> Sketch080
  Dir = (0,0,1)
  DirMode = 2
  FaceMakerClass = Part::FaceMakerBullseye
  LengthFwd = 3
  LengthRev = 0
  Placement = pos=(0,0,-2.7) rot=(0,0,1;0rad)
  Solid = true
  Symmetric = false
FEATURE [Sketcher::SketchObject] Sketch081
  FullyConstrained = true
  Placement = pos=(117,19,0) rot=(0.57735,0.57735,0.57735;2.0944rad)
  sketch-geometry (8):
    g0: LineSegment StartX=-49.19 StartY=63.5 StartZ=0 EndX=-49.19 EndY=60.5 EndZ=0
    g1: LineSegment StartX=-49.19 StartY=11.5 StartZ=0 EndX=-49.19 EndY=8.5 EndZ=0
    g2: ArcOfCircle CenterX=-1.5 CenterY=62 CenterZ=0 NormalX=0 NormalY=0 NormalZ=1 AngleXU=0 Radius=1.5 StartAngle=4.71239 EndAngle=7.85398
    g3: ArcOfCircle CenterX=-1.5 CenterY=10 CenterZ=0 NormalX=0 NormalY=0 NormalZ=1 AngleXU=0 Radius=1.5 StartAngle=4.71239 EndAngle=7.85398
    g4: LineSegment StartX=-49.19 StartY=63.5 StartZ=0 EndX=-1.5 EndY=63.5 EndZ=0
    g5: LineSegment StartX=-49.19 StartY=60.5 StartZ=0 EndX=-1.5 EndY=60.5 EndZ=0
    g6: LineSegment StartX=-49.19 StartY=11.5 StartZ=0 EndX=-1.5 EndY=11.5 EndZ=0
    g7: LineSegment StartX=-49.19 StartY=8.5 StartZ=0 EndX=-1.5 EndY=8.5 EndZ=0
  constraints (19):
    c: Vertical(g0)
    c: Distance(g0) = 3
    c: Vertical(g1)
    c: Block(g1)
    c: Block(g2)
    c: Block(g3)
    c: Block(g0)
    c: Coincident(g4,g0)
    c: Coincident(g4,g2)
    c: Horizontal(g4)
    c: Coincident(g5,g0)
    c: Coincident(g5,g2)
    c: Horizontal(g5)
    c: Coincident(g6,g1)
    c: Coincident(g6,g3)
    c: Horizontal(g6)
    c: Coincident(g7,g1)
    c: Coincident(g7,g3)
    c: Horizontal(g7)
FEATURE [Part::Extrusion] Extrude071  label="sideB004"
  Base = -> Sketch079
  Dir = (0,0,1)
  DirMode = 2
  FaceMakerClass = Part::FaceMakerBullseye
  LengthFwd = 3
  LengthRev = 0
  Placement = pos=(0,0,71.7) rot=(0,0,1;0rad)
  Solid = true
  Symmetric = false
FEATURE [Part::MultiFuse] Fusion152  label="removeFromBottom004"
  Placement = pos=(2,0,0) rot=(0,0,1;0rad)
  Shapes = -> [Extrude070,Extrude071]
FEATURE [Part::Extrusion] Extrude072
  Base = -> Sketch081
  Dir = (1,0,0)
  DirMode = 2
  FaceMakerClass = Part::FaceMakerBullseye
  LengthFwd = 10
  LengthRev = 0
  Solid = true
  Symmetric = false
FEATURE [Part::Fillet] Fillet059  label="removeFromtMoreFrontCaseScrewRetainers004"
  Base = -> Extrude072
  Edges = 4 edges r=1.49: [Edge6,Edge11,Edge18,Edge23]
  Placement = pos=(-12,0,0) rot=(0,0,1;0rad)
FEATURE [Sketcher::SketchObject] Sketch082
  FullyConstrained = true
  Placement = pos=(117,19,0) rot=(0.57735,0.57735,0.57735;2.0944rad)
  sketch-geometry (8):
    g0: LineSegment StartX=-49.19 StartY=69.25 StartZ=0 EndX=-49.19 EndY=66.25 EndZ=0
    g1: LineSegment StartX=-49.19 StartY=5.75 StartZ=0 EndX=-49.19 EndY=2.75 EndZ=0
    g2: ArcOfCircle CenterX=-1.5 CenterY=67.75 CenterZ=0 NormalX=0 NormalY=0 NormalZ=1 AngleXU=0 Radius=1.5 StartAngle=4.71239 EndAngle=7.85398
    g3: ArcOfCircle CenterX=-1.5 CenterY=4.25 CenterZ=0 NormalX=0 NormalY=0 NormalZ=1 AngleXU=0 Radius=1.5 StartAngle=4.71239 EndAngle=7.85398
    g4: LineSegment StartX=-49.19 StartY=69.25 StartZ=0 EndX=-1.5 EndY=69.25 EndZ=0
    g5: LineSegment StartX=-49.19 StartY=66.25 StartZ=0 EndX=-1.5 EndY=66.25 EndZ=0
    g6: LineSegment StartX=-49.19 StartY=5.75 StartZ=0 EndX=-1.5 EndY=5.75 EndZ=0
    g7: LineSegment StartX=-49.19 StartY=2.75 StartZ=0 EndX=-1.5 EndY=2.75 EndZ=0
  constraints (19):
    c: Vertical(g0)
    c: Distance(g0) = 3
    c: Block(g0)
    c: Vertical(g1)
    c: Block(g2)
    c: Block(g3)
    c: Block(g1)
    c: Coincident(g4,g0)
    c: Coincident(g4,g2)
    c: Horizontal(g4)
    c: Coincident(g5,g0)
    c: Coincident(g5,g2)
    c: Horizontal(g5)
    c: Coincident(g6,g1)
    c: Coincident(g6,g3)
    c: Horizontal(g6)
    c: Coincident(g7,g1)
    c: Coincident(g7,g3)
    c: Horizontal(g7)
FEATURE [Part::Extrusion] Extrude073
  Base = -> Sketch082
  Dir = (1,0,0)
  DirMode = 2
  FaceMakerClass = Part::FaceMakerBullseye
  LengthFwd = 10
  LengthRev = 0
  Solid = true
  Symmetric = false
FEATURE [Part::Fillet] Fillet060  label="removeFromtMoreFrontCaseScrewRetainers005"
  Base = -> Extrude073
  Edges = 4 edges r=1.49: [Edge6,Edge11,Edge18,Edge23]
  Placement = pos=(-4,0,0) rot=(0,0,1;0rad)
FEATURE [Part::Revolution] Revolve163  label="backCaseScrewRetainer004"
  Angle = 360
  Axis = (0,1,0)
  Base = (0,0,0)
  FaceMakerClass = Part::FaceMakerBullseye
  Placement = pos=(12.5,3,62) rot=(0,0,1;0rad)
  Solid = false
  Source = -> Face149
  Symmetric = false
FEATURE [Part::Revolution] Revolve164  label="frontCaseScrewRetainer006"
  Angle = 360
  Axis = (0,1,0)
  Base = (0,0,0)
  FaceMakerClass = Part::FaceMakerBullseye
  Placement = pos=(89.5,3,68.5) rot=(0,0,1;0rad)
  Solid = false
  Source = -> Face151
  Symmetric = false
FEATURE [Part::Revolution] Revolve165  label="frontCaseScrewRetainer007"
  Angle = 360
  Axis = (0,1,0)
  Base = (0,0,0)
  FaceMakerClass = Part::FaceMakerBullseye
  Placement = pos=(89.5,3,3.5) rot=(0,0,1;0rad)
  Solid = false
  Source = -> Face152
  Symmetric = false
FEATURE [Part::Revolution] Revolve166  label="backCaseScrewRetainer005"
  Angle = 360
  Axis = (0,1,0)
  Base = (0,0,0)
  FaceMakerClass = Part::FaceMakerBullseye
  Placement = pos=(12.5,3,10) rot=(0,0,1;0rad)
  Solid = false
  Source = -> Face150
  Symmetric = false
FEATURE [Part::Revolution] Revolve167  label="moreFrontCaseScrewRetainer006"
  Angle = 360
  Axis = (0,1,0)
  Base = (0,0,0)
  FaceMakerClass = Part::FaceMakerBullseye
  Placement = pos=(109.5,4.5,68.5) rot=(0,0,1;0rad)
  Solid = false
  Source = -> Face153
  Symmetric = false
FEATURE [Part::Revolution] Revolve168  label="moreFrontCaseScrewRetainer007"
  Angle = 360
  Axis = (0,1,0)
  Base = (0,0,0)
  FaceMakerClass = Part::FaceMakerBullseye
  Placement = pos=(109.5,4.5,3.5) rot=(0,0,1;0rad)
  Solid = false
  Source = -> Face154
  Symmetric = false
FEATURE [Part::MultiFuse] Fusion151  label="screwRetainers003"
  Shapes = -> [Revolve168,Revolve167,Revolve166,Revolve165,Revolve164,Revolve163]
FEATURE [Part::Cut] Cut069  label="screwRetainers004"
  Base = -> Fusion151
  Tool = -> Fusion152
FEATURE [Part::Cut] Cut070
  Base = -> Cut069
  Tool = -> Fillet060
FEATURE [Part::Cut] Cut071  label="screwPillars001"
  Base = -> Cut070
  Tool = -> Fillet059
FEATURE [Part::MultiFuse] Fusion153  label="bottom024"
  Shapes = -> [Fusion149,Cut071]
FEATURE [Part::Cylinder] Cylinder067
  Angle = 360
  AttacherType = Attacher::AttachEngine3D
  Height = 10
  Placement = pos=(20.65,12,4.68) rot=(1,0,0;1.5708rad)
  Radius = 2
FEATURE [Part::Cylinder] Cylinder068
  Angle = 360
  AttacherType = Attacher::AttachEngine3D
  Height = 10
  Placement = pos=(20.65,12,67.38) rot=(1,0,0;1.5708rad)
  Radius = 2
FEATURE [Part::Cylinder] Cylinder069
  Angle = 360
  AttacherType = Attacher::AttachEngine3D
  Height = 10
  Placement = pos=(77.15,12,67.38) rot=(1,0,0;1.5708rad)
  Radius = 2
FEATURE [Part::Cylinder] Cylinder070
  Angle = 360
  AttacherType = Attacher::AttachEngine3D
  Height = 10
  Placement = pos=(77.15,12,4.68) rot=(1,0,0;1.5708rad)
  Radius = 2
FEATURE [Part::MultiFuse] Fusion154  label="removeFromThreadedInsertHousing001"
  Shapes = -> [Cylinder069,Cylinder068,Cylinder067,Cylinder070]
FEATURE [Part::Cut] Cut072  label="bottom025"
  Base = -> Fusion153
  Tool = -> Fusion154
FEATURE [Image::ImagePlane] ImagePlane
  XSize = 339
  YSize = 72
FEATURE [Sketcher::SketchObject] Sketch083
  FullyConstrained = true
  MapMode = 5
  Support = -> [XY_Plane]
  sketch-geometry (200):
    g0: LineSegment StartX=-151.619 StartY=28.8932 StartZ=0 EndX=-140.819 EndY=28.8932 EndZ=0
    g1: LineSegment StartX=-151.619 StartY=24.0313 StartZ=0 EndX=-151.619 EndY=28.8932 EndZ=0
    g2: LineSegment StartX=-140.819 StartY=17.7713 StartZ=0 EndX=-151.619 EndY=17.7713 EndZ=0
    g3: LineSegment StartX=-151.619 StartY=17.7713 StartZ=0 EndX=-151.619 EndY=22.6313 EndZ=0
    g4: LineSegment StartX=-151.619 StartY=22.6313 StartZ=0 EndX=-145.128 EndY=22.6313 EndZ=0
    g5: LineSegment StartX=-145.128 StartY=24.0313 StartZ=0 EndX=-140.819 EndY=28.8932 EndZ=0
    g6: LineSegment StartX=-145.128 StartY=22.6313 StartZ=0 EndX=-140.819 EndY=17.7713 EndZ=0
    g7: ArcOfCircle CenterX=-155.157 CenterY=23.3323 CenterZ=0 NormalX=0 NormalY=0 NormalZ=1 AngleXU=0 Radius=6.92354 StartAngle=1.03434 EndAngle=5.24885
    g8: ArcOfCircle CenterX=-155.157 CenterY=23.3323 CenterZ=0 NormalX=0 NormalY=0 NormalZ=1 AngleXU=0 Radius=12.6269 StartAngle=1.28675 EndAngle=4.99643
    g9: LineSegment StartX=-151.619 StartY=35.4532 StartZ=0 EndX=-151.619 EndY=29.2832 EndZ=0
    g10: LineSegment StartX=-151.619 StartY=17.3813 StartZ=0 EndX=-151.619 EndY=11.2113 EndZ=0
    g11-g21: Circle x11 (B-spline internal-alignment scaffolding for g22; pole/knot coordinates omitted)
    g22: BSplineCurve PolesCount=11 KnotsCount=9 Degree=3 IsPeriodic=0
    g23-g31: GeomPoint x9 (B-spline internal-alignment scaffolding for g22; pole/knot coordinates omitted)
    g32-g49: Circle x18 (B-spline internal-alignment scaffolding for g50; pole/knot coordinates omitted)
    g50: BSplineCurve PolesCount=18 KnotsCount=16 Degree=3 IsPeriodic=0
    g51-g66: GeomPoint x16 (B-spline internal-alignment scaffolding for g50; pole/knot coordinates omitted)
    g67: LineSegment StartX=-117.124 StartY=30.093 StartZ=0 EndX=-117.603 EndY=26.5272 EndZ=0
    g68: LineSegment StartX=-117.603 StartY=17.8472 StartZ=0 EndX=-117.124 EndY=14.2659 EndZ=0
    g69: Ellipse CenterX=-109.671 CenterY=20.025 CenterZ=0 NormalX=0 NormalY=0 NormalZ=1 MajorRadius=3.34798 MinorRadius=2.71052 AngleXU=-1.56793
    g70: GeomPoint X=-109.666 Y=18.0598 Z=0
    g71: GeomPoint X=-109.677 Y=21.9902 Z=0
    g72: Ellipse CenterX=-109.671 CenterY=20.0123 CenterZ=0 NormalX=0 NormalY=0 NormalZ=1 MajorRadius=6.93002 MinorRadius=6.36273 AngleXU=-3.13976
    g73: GeomPoint X=-112.417 Y=20.0073 Z=0
    g74: GeomPoint X=-106.925 Y=20.0173 Z=0
    g75: Ellipse CenterX=-51.7682 CenterY=20.1463 CenterZ=0 NormalX=0 NormalY=0 NormalZ=1 MajorRadius=3.19279 MinorRadius=2.71052 AngleXU=-1.52774
    g76: GeomPoint X=-51.6955 Y=18.4606 Z=0
    g77: GeomPoint X=-51.8408 Y=21.832 Z=0
    g78: GeomPoint X=-54.5142 Y=20.1413 Z=0
    g79: GeomPoint X=-49.0221 Y=20.1513 Z=0
    g80: Ellipse CenterX=-51.7682 CenterY=20.1463 CenterZ=0 NormalX=0 NormalY=0 NormalZ=1 MajorRadius=6.93002 MinorRadius=6.36273 AngleXU=-3.13976
    g81: Ellipse CenterX=-22.8436 CenterY=20.1783 CenterZ=0 NormalX=0 NormalY=0 NormalZ=1 MajorRadius=3.31512 MinorRadius=2.71052 AngleXU=-1.60214
    g82: GeomPoint X=-22.9034 Y=18.2706 Z=0
    g83: GeomPoint X=-22.7838 Y=22.0861 Z=0
    g84: GeomPoint X=-25.5897 Y=20.1733 Z=0
    g85: GeomPoint X=-20.0976 Y=20.1833 Z=0
    g86: Ellipse CenterX=-22.8436 CenterY=20.1783 CenterZ=0 NormalX=0 NormalY=0 NormalZ=1 MajorRadius=6.93002 MinorRadius=6.36273 AngleXU=-3.13976
    g87: LineSegment StartX=-101.889 StartY=14.1107 StartZ=0 EndX=-97.7455 EndY=14.1107 EndZ=0
    g88: LineSegment StartX=-93.8155 StartY=14.1107 StartZ=0 EndX=-89.6755 EndY=14.1107 EndZ=0
    g89: LineSegment StartX=-85.7455 StartY=14.1107 StartZ=0 EndX=-81.6055 EndY=14.1107 EndZ=0
    g90: LineSegment StartX=-101.889 StartY=14.1107 StartZ=0 EndX=-101.889 EndY=25.9907 EndZ=0
    g91: LineSegment StartX=-101.889 StartY=25.9907 StartZ=0 EndX=-97.8594 EndY=25.9907 EndZ=0
    g92: LineSegment StartX=-97.8594 StartY=25.9907 StartZ=0 EndX=-97.8594 EndY=24.0907 EndZ=0
    g93: LineSegment StartX=-97.7455 StartY=14.1107 StartZ=0 EndX=-97.7455 EndY=19.9107 EndZ=0
    g94: LineSegment StartX=-89.6755 StartY=14.1107 StartZ=0 EndX=-89.6755 EndY=19.9107 EndZ=0
    g95: LineSegment StartX=-93.8155 StartY=14.1107 StartZ=0 EndX=-93.8155 EndY=21.0107 EndZ=0
    g96-g106: Circle x11 (B-spline internal-alignment scaffolding for g107; pole/knot coordinates omitted)
    g107: BSplineCurve PolesCount=11 KnotsCount=9 Degree=3 IsPeriodic=0
    g108-g116: GeomPoint x9 (B-spline internal-alignment scaffolding for g107; pole/knot coordinates omitted)
    g117: BSplineCurve PolesCount=11 KnotsCount=9 Degree=3 IsPeriodic=0
    g118-g125: Circle x8 (B-spline internal-alignment scaffolding for g126; pole/knot coordinates omitted)
    g126: BSplineCurve PolesCount=8 KnotsCount=6 Degree=3 IsPeriodic=0
    g127-g132: GeomPoint x6 (B-spline internal-alignment scaffolding for g126; pole/knot coordinates omitted)
    g133: BSplineCurve PolesCount=8 KnotsCount=6 Degree=3 IsPeriodic=0
    g134: LineSegment StartX=-85.7455 StartY=21.0107 StartZ=0 EndX=-85.7455 EndY=14.1107 EndZ=0
    g135: LineSegment StartX=-80.0879 StartY=14.1107 StartZ=0 EndX=-75.944 EndY=14.1107 EndZ=0
    g136: LineSegment StartX=-72.014 StartY=14.1107 StartZ=0 EndX=-67.874 EndY=14.1107 EndZ=0
    g137: LineSegment StartX=-63.944 StartY=14.1107 StartZ=0 EndX=-59.804 EndY=14.1107 EndZ=0
    g138: LineSegment StartX=-80.0879 StartY=14.1107 StartZ=0 EndX=-80.0879 EndY=25.9907 EndZ=0
    g139: LineSegment StartX=-80.0879 StartY=25.9907 StartZ=0 EndX=-76.0579 EndY=25.9907 EndZ=0
    g140: LineSegment StartX=-76.0579 StartY=25.9907 StartZ=0 EndX=-76.0579 EndY=24.0907 EndZ=0
    g141: LineSegment StartX=-75.944 StartY=14.1107 StartZ=0 EndX=-75.944 EndY=19.9107 EndZ=0
    g142: LineSegment StartX=-67.874 StartY=14.1107 StartZ=0 EndX=-67.874 EndY=19.9107 EndZ=0
    g143: LineSegment StartX=-72.014 StartY=14.1107 StartZ=0 EndX=-72.014 EndY=21.0107 EndZ=0
    g144-g148: Circle x5 (B-spline internal-alignment scaffolding for g149; pole/knot coordinates omitted)
    g149: BSplineCurve PolesCount=11 KnotsCount=9 Degree=3 IsPeriodic=0
    g150-g158: GeomPoint x9 (B-spline internal-alignment scaffolding for g149; pole/knot coordinates omitted)
    g159: BSplineCurve PolesCount=11 KnotsCount=9 Degree=3 IsPeriodic=0
    g160-g167: Circle x8 (B-spline internal-alignment scaffolding for g168; pole/knot coordinates omitted)
    g168: BSplineCurve PolesCount=8 KnotsCount=6 Degree=3 IsPeriodic=0
    g169-g174: GeomPoint x6 (B-spline internal-alignment scaffolding for g168; pole/knot coordinates omitted)
    g175: BSplineCurve PolesCount=8 KnotsCount=6 Degree=3 IsPeriodic=0
    g176: LineSegment StartX=-63.944 StartY=21.0107 StartZ=0 EndX=-63.944 EndY=14.1107 EndZ=0
    g177: LineSegment StartX=-59.804 StartY=14.1107 StartZ=0 EndX=-59.804 EndY=21.5868 EndZ=0
    g178: BSplineCurve PolesCount=4 KnotsCount=2 Degree=3 IsPeriodic=0
    g179: GeomPoint X=-59.804 Y=21.5868 Z=0
    g180: GeomPoint X=-60.2379 Y=24.0907 Z=0
    g181: LineSegment StartX=-81.6055 StartY=14.1107 StartZ=0 EndX=-81.6055 EndY=21.5868 EndZ=0
    g182: LineSegment StartX=-151.619 StartY=24.0313 StartZ=0 EndX=-145.128 EndY=24.0313 EndZ=0
    g183: Circle CenterX=-82.0394 CenterY=24.0907 CenterZ=0 NormalX=0 NormalY=0 NormalZ=1 AngleXU=0 Radius=1
    g184: Circle CenterX=-81.7131 CenterY=23.2736 CenterZ=0 NormalX=0 NormalY=0 NormalZ=1 AngleXU=0 Radius=1
    g185: Circle CenterX=-81.6055 CenterY=21.5868 CenterZ=0 NormalX=0 NormalY=0 NormalZ=1 AngleXU=0 Radius=1
    g186: BSplineCurve PolesCount=3 KnotsCount=2 Degree=2 IsPeriodic=0
    g187: GeomPoint X=-82.0394 Y=24.0907 Z=0
    g188: GeomPoint X=-81.6055 Y=21.5868 Z=0
    g189: Ellipse CenterX=-37.3522 CenterY=19.9515 CenterZ=0 NormalX=0 NormalY=0 NormalZ=1 MajorRadius=2.99755 MinorRadius=2.49 AngleXU=1.5708
    g190: GeomPoint X=-37.3522 Y=21.6203 Z=0
    g191: GeomPoint X=-37.3522 Y=18.2826 Z=0
    g192: LineSegment StartX=-38.8121 StartY=26.36 StartZ=0 EndX=-38.8121 EndY=13.76 EndZ=0
    g193: LineSegment StartX=-38.8121 StartY=26.36 StartZ=0 EndX=-38.8121 EndY=20.06 EndZ=0
    g194: LineSegment StartX=-38.8121 StartY=20.06 StartZ=0 EndX=-44.1496 EndY=20.06 EndZ=0
    g195: Ellipse CenterX=-38.7647 CenterY=20.06 CenterZ=0 NormalX=0 NormalY=0 NormalZ=1 MajorRadius=6.30025 MinorRadius=5.3849 AngleXU=1.57276
    g196: LineSegment StartX=-38.777 StartY=26.3602 StartZ=0 EndX=-38.7523 EndY=13.7597 EndZ=0
    g197: LineSegment StartX=-44.1496 StartY=20.0494 StartZ=0 EndX=-33.3798 EndY=20.0705 EndZ=0
    g198: GeomPoint X=-38.7711 Y=23.3304 Z=0
    g199: GeomPoint X=-38.7583 Y=16.7895 Z=0
  constraints (189):
    c: Coincident(g1,g0)
    c: Horizontal(g0)
    c: Vertical(g1)
    c: Coincident(g2,g3)
    c: Coincident(g3,g4)
    c: Horizontal(g4)
    c: Horizontal(g2)
    c: Vertical(g3)
    c: Block(g1)
    c: Distance(g3) = 4.86
    c: Block(g4)
    c: Distance(g0) = 10.8
    c: Distance(g2) = 10.8
    c: Coincident(g5,g0)
    c: Coincident(g6,g4)
    c: Coincident(g6,g2)
    c: Block(g8)
    c: Block(g7)
    c: Coincident(g9,g8)
    c: Coincident(g9,g7)
    c: Vertical(g9)
    c: Coincident(g10,g7)
    c: Coincident(g10,g8)
    c: Vertical(g10)
    c: Weight(g11) = 1
    c: Equal(g11, g12-g21) x10
    c: InternalAlignment(g11-g21 -> g22) x11
    c: InternalAlignment(g23-g31 -> g22) x9
    c: Block(g22)
    c: Weight(g32) = 1
    c: Equal(g32, g33-g49) x17
    c: InternalAlignment(g32-g49 -> g50) x18
    c: InternalAlignment(g51-g66 -> g50) x16
    c: Block(g50)
    c: Coincident(g67,g50)
    c: Coincident(g67,g22)
    c: Coincident(g68,g22)
    c: Coincident(g68,g50)
    c: InternalAlignment(g70,g69)
    c: InternalAlignment(g71,g69)
    c: Block(g69)
    c: InternalAlignment(g73,g72)
    c: InternalAlignment(g74,g72)
    c: Block(g72)
    c: InternalAlignment(g76,g75)
    c: InternalAlignment(g77,g75)
    c: InternalAlignment(g78,g80)
    c: InternalAlignment(g79,g80)
    c: Block(g80)
    c: Coincident(g75,g80)
    c: Block(g75)
    c: InternalAlignment(g82,g81)
    c: InternalAlignment(g83,g81)
    c: InternalAlignment(g84,g86)
    c: InternalAlignment(g85,g86)
    c: Block(g86)
    c: Coincident(g81,g86)
    c: Block(g81)
    c: Horizontal(g87)
    c: Block(g87)
    c: Horizontal(g88)
    c: Distance(g88) = 4.14
    c: Horizontal(g89)
    c: Equal(g88,g89) = 4.14
    c: Block(g89)
    c: Block(g88)
    c: Coincident(g90,g87)
    c: Vertical(g90)
    c: Distance(g90) = 11.88
    c: Coincident(g91,g90)
    c: Horizontal(g91)
    c: Coincident(g92,g91)
    c: Vertical(g92)
    c: Distance(g91) = 4.03
    c: Distance(g92) = 1.9
    c: Coincident(g93,g87)
    c: Vertical(g93)
    c: Vertical(g94)
    c: Coincident(g94,g88)
    c: Distance(g93) = 5.8
    c: Distance(g94) = 5.8
    c: Vertical(g95)
    c: Coincident(g95,g88)
    c: Distance(g95) = 6.9
    c: Coincident(g107,g92)
    c: Weight(g96) = 1
    c: Equal(g96, g97-g106) x10
    c: InternalAlignment(g96-g106 -> g107) x11
    c: InternalAlignment(g108-g116 -> g107) x9
    c: Block(g107)
    c: Block(g117)
    c: Coincident(g126,g93)
    c: Weight(g118) = 1
    c: Equal(g118, g119-g125) x7
    c: Coincident(g126,g95)
    c: InternalAlignment(g118-g125 -> g126) x8
    c: InternalAlignment(g127-g132 -> g126) x6
    c: Coincident(g133,g94)
    c: Block(g126)
    c: Block(g133)
    c: Coincident(g134,g133)
    c: Coincident(g134,g89)
    c: Vertical(g134)
    c: Horizontal(g135)
    c: Block(g135)
    c: Horizontal(g136)
    c: Equal(g88,g136) = 4.14
    c: Horizontal(g137)
    c: Equal(g136,g137) = 4.14
    c: Block(g137)
    c: Block(g136)
    c: Coincident(g138,g135)
    c: Vertical(g138)
    c: Equal(g90,g138) = 11.88
    c: Coincident(g139,g138)
    c: Horizontal(g139)
    c: Coincident(g140,g139)
    c: Vertical(g140)
    c: Equal(g91,g139) = 4.03
    c: Equal(g92,g140) = 1.9
    c: Coincident(g141,g135)
    c: Vertical(g141)
    c: Vertical(g142)
    c: Coincident(g142,g136)
    c: Equal(g93,g141) = 5.8
    c: Equal(g94,g142) = 5.8
    c: Vertical(g143)
    c: Coincident(g143,g136)
    c: Equal(g95,g143) = 6.9
    c: Coincident(g149,g140)
    c: Equal(g96,g144) = 1
    c: Equal(g144, g145-g148) x4
    c: InternalAlignment(g144-g148 -> g149) x5
    c: InternalAlignment(g150-g158 -> g149) x9
    c: Block(g149)
    c: Block(g159)
    c: Coincident(g168,g141)
    c: Equal(g118,g160) = 1
    c: Equal(g160, g161-g167) x7
    c: Coincident(g168,g143)
    c: InternalAlignment(g160-g167 -> g168) x8
    c: InternalAlignment(g169-g174 -> g168) x6
    c: Coincident(g175,g142)
    c: Block(g168)
    c: Block(g175)
    c: Coincident(g176,g175)
    c: Coincident(g176,g137)
    c: Vertical(g176)
    c: Coincident(g177,g137)
    c: Vertical(g177)
    c: Coincident(g178,g177)
    c: Coincident(g178,g159)
    c: InternalAlignment(g179,g178)
    c: InternalAlignment(g180,g178)
    c: Block(g178)
    c: Vertical(g181)
    c: Coincident(g181,g89)
    c: Block(g5)
    c: Coincident(g182,g1)
    c: Coincident(g182,g5)
    c: Horizontal(g182)
    c: Coincident(g186,g117)
    c: Weight(g183) = 1
    c: Equal(g183,g184)
    c: Equal(g183,g185)
    c: Coincident(g186,g181)
    c: InternalAlignment(g183,g186)
    c: InternalAlignment(g184,g186)
    c: InternalAlignment(g185,g186)
    c: InternalAlignment(g187,g186)
    c: InternalAlignment(g188,g186)
    c: Block(g186)
    c: InternalAlignment(g190,g189)
    c: InternalAlignment(g191,g189)
    c: Block(g189)
    c: Vertical(g192)
    c: Distance(g192) = 12.6
    c: Block(g192)
    c: Vertical(g193)
    c: Distance(g193) = 6.3
    c: Coincident(g193,g192)
    c: Coincident(g194,g193)
    c: Horizontal(g194)
    c: Block(g194)
    c: InternalAlignment(g196-g199 -> g195) x4
    c: PointOnObject(g192,g195)
    c: PointOnObject(g192,g195)
    c: PointOnObject(g194,g195)
    c: Block(g195)
FEATURE [PartDesign::Body] Body
  Group = -> [Sketch083]
  Origin = -> Origin
FEATURE [Sketcher::SketchObject] Sketch084
  FullyConstrained = true
  MapMode = 5
  Support = -> [XY_Plane001]
FEATURE [PartDesign::Body] Body001
  Group = -> [Sketch084]
  Origin = -> Origin001
